FCSTD DOCUMENT  (FreeCAD 1.0R39109 (Git))
Label: roommake
License: All rights reserved
LicenseURL: https://en.wikipedia.org/wiki/All_rights_reserved
objects: App::Link×25, Assembly::JointGroup×1, Assembly::AssemblyObject×1
EXTERNAL_REF file=../room/room.FCStd obj=Part
EXTERNAL_REF file=../sofa/sofa.FCStd obj=Part002
EXTERNAL_REF file=../tvboard/tvboard.FCStd obj=Part
EXTERNAL_REF file=../tv/tv.FCStd obj=Part001
EXTERNAL_REF file=../balanceball/balanceball.FCStd obj=Part001
EXTERNAL_REF file=../clothes_drying_pole/clothes_drying_pole.FCStd obj=Part002
EXTERNAL_REF file=../refrigerator/refrigerator.FCStd obj=Part
EXTERNAL_REF file=../table02/table02.FCStd obj=Part
EXTERNAL_REF file=../toasteroven/toasteroven.FCStd obj=Part
EXTERNAL_REF file=../washing_machine/washing_machine.FCStd obj=Part
EXTERNAL_REF file=../furniture/furniture.FCStd obj=Part003
EXTERNAL_REF file=../dressing_table/Dressing_Table.FCStd obj=Part
EXTERNAL_REF file=../wall1500/wall1500.FCStd obj=Part
EXTERNAL_REF file=../table/table.FCStd obj=Part001
EXTERNAL_REF file=../cocktail/cocktail.FCStd obj=Part001
EXTERNAL_REF file=../moniter/moniter.FCStd obj=Part
EXTERNAL_REF file=../clock/clock.FCStd obj=Part012
EXTERNAL_REF file=../pylon/pylon.FCStd obj=Part001

FEATURE [Assembly::JointGroup] Joints
FEATURE [App::Link] room
  LinkedObject = -> <external ../room/room.FCStd>#Part
FEATURE [App::Link] sofa
  LinkPlacement = pos=(-6.91189e-05,821.257,-6.10352e-05) rot=(0,0,1;3.14159rad)
  LinkedObject = -> <external ../sofa/sofa.FCStd>#Part002
  Placement = pos=(-6.91189e-05,821.257,-6.10352e-05) rot=(0,0,1;3.14159rad)
FEATURE [App::Link] tvboard
  LinkPlacement = pos=(0,2298,-1.52588e-05) rot=(0,0,1;0rad)
  LinkedObject = -> <external ../tvboard/tvboard.FCStd>#Part
  Placement = pos=(0,2298,-1.52588e-05) rot=(0,0,1;0rad)
FEATURE [App::Link] tv
  LinkPlacement = pos=(0,2301,332) rot=(0,0,1;0rad)
  LinkedObject = -> <external ../tv/tv.FCStd>#Part001
  Placement = pos=(0,2301,332) rot=(0,0,1;0rad)
FEATURE [App::Link] balanceball
  LinkPlacement = pos=(-943,2144,-1.26064e-05) rot=(0,0,1;0rad)
  LinkedObject = -> <external ../balanceball/balanceball.FCStd>#Part001
  Placement = pos=(-943,2144,-1.26064e-05) rot=(0,0,1;0rad)
FEATURE [App::Link] clothesdryingpole
  LinkPlacement = pos=(-2049,1585,0) rot=(0,0,1;0rad)
  LinkedObject = -> <external ../clothes_drying_pole/clothes_drying_pole.FCStd>#Part002
  Placement = pos=(-2049,1585,0) rot=(0,0,1;0rad)
FEATURE [App::Link] refrigerator
  LinkPlacement = pos=(-1631,0.00019455,0) rot=(0,0,1;0rad)
  LinkedObject = -> <external ../refrigerator/refrigerator.FCStd>#Part
  Placement = pos=(-1631,0.00019455,0) rot=(0,0,1;0rad)
FEATURE [App::Link] table02
  LinkPlacement = pos=(-2198,-1060,-3.05176e-05) rot=(0,0,-1;1.5708rad)
  LinkedObject = -> <external ../table02/table02.FCStd>#Part
  Placement = pos=(-2198,-1060,-3.05176e-05) rot=(0,0,-1;1.5708rad)
FEATURE [App::Link] toasteroven
  LinkPlacement = pos=(-2215.04,-812.253,802.77) rot=(0,0,1;1.5708rad)
  LinkedObject = -> <external ../toasteroven/toasteroven.FCStd>#Part
  Placement = pos=(-2215.04,-812.253,802.77) rot=(0,0,1;1.5708rad)
FEATURE [App::Link] wachingmachine
  LinkPlacement = pos=(-2220,280,0) rot=(0,0,1;1.5708rad)
  LinkedObject = -> <external ../washing_machine/washing_machine.FCStd>#Part
  Placement = pos=(-2220,280,0) rot=(0,0,1;1.5708rad)
FEATURE [App::Link] furniture
  LinkPlacement = pos=(1220,2120,0) rot=(0,0,1;0rad)
  LinkedObject = -> <external ../furniture/furniture.FCStd>#Part003
  Placement = pos=(1220,2120,0) rot=(0,0,1;0rad)
FEATURE [App::Link] dressing_table
  LinkPlacement = pos=(2017,270,4.547e-13) rot=(0,0,-1;1.5708rad)
  LinkedObject = -> <external ../dressing_table/Dressing_Table.FCStd>#Part
  Placement = pos=(2017,270,4.547e-13) rot=(0,0,-1;1.5708rad)
FEATURE [App::Link] wall1500
  LinkPlacement = pos=(1706,-740.001,0) rot=(0,0,1;0rad)
  LinkedObject = -> <external ../wall1500/wall1500.FCStd>#Part
  Placement = pos=(1706,-740.001,0) rot=(0,0,1;0rad)
FEATURE [App::Link] wall1501
  LinkPlacement = pos=(2,-1703,-0.00012207) rot=(0,0,1;1.5708rad)
  LinkedObject = -> <external ../wall1500/wall1500.FCStd>#Part
  Placement = pos=(2,-1703,-0.00012207) rot=(0,0,1;1.5708rad)
FEATURE [App::Link] table
  LinkPlacement = pos=(-421,-1876,39.9999) rot=(0,0,-1;1.5708rad)
  LinkedObject = -> <external ../table/table.FCStd>#Part001
  Placement = pos=(-421,-1876,39.9999) rot=(0,0,-1;1.5708rad)
FEATURE [App::Link] cocktail
  LinkPlacement = pos=(-475,-1788,670) rot=(0,0,1;0rad)
  LinkedObject = -> <external ../cocktail/cocktail.FCStd>#Part001
  Placement = pos=(-475,-1788,670) rot=(0,0,1;0rad)
FEATURE [App::Link] cocktail001
  LinkPlacement = pos=(-272.591,-1674.31,668.798) rot=(0,0,-1;0.785398rad)
  LinkedObject = -> <external ../cocktail/cocktail.FCStd>#Part001
  Placement = pos=(-272.591,-1674.31,668.798) rot=(0,0,-1;0.785398rad)
FEATURE [App::Link] cocktail002
  LinkPlacement = pos=(-400.482,-2006.5,671.622) rot=(0,0,1;0.785398rad)
  LinkedObject = -> <external ../cocktail/cocktail.FCStd>#Part001
  Placement = pos=(-400.482,-2006.5,671.622) rot=(0,0,1;0.785398rad)
FEATURE [App::Link] table003
  LinkPlacement = pos=(411,-1895,-3.05176e-05) rot=(0,0,-1;1.5708rad)
  LinkedObject = -> <external ../table/table.FCStd>#Part001
  Placement = pos=(411,-1895,-3.05176e-05) rot=(0,0,-1;1.5708rad)
FEATURE [App::Link] moniter
  LinkPlacement = pos=(565.3,-2170.7,631) rot=(0,0,1;1.5708rad)
  LinkedObject = -> <external ../moniter/moniter.FCStd>#Part
  Placement = pos=(565.3,-2170.7,631) rot=(0,0,1;1.5708rad)
FEATURE [App::Link] moniter001
  LinkPlacement = pos=(563.3,-1618.7,633) rot=(0,0,1;1.5708rad)
  LinkedObject = -> <external ../moniter/moniter.FCStd>#Part
  Placement = pos=(563.3,-1618.7,633) rot=(0,0,1;1.5708rad)
FEATURE [App::Link] clock
  LinkPlacement = pos=(0,2440,2040) rot=(0,0,1;0rad)
  LinkedObject = -> <external ../clock/clock.FCStd>#Part012
  Placement = pos=(0,2440,2040) rot=(0,0,1;0rad)
FEATURE [App::Link] pylon
  LinkPlacement = pos=(2295,-958,-1.52588e-05) rot=(0,0,1;0rad)
  LinkedObject = -> <external ../pylon/pylon.FCStd>#Part001
  Placement = pos=(2295,-958,-1.52588e-05) rot=(0,0,1;0rad)
FEATURE [App::Link] pylon001
  LinkPlacement = pos=(2006,-961.001,0) rot=(0,0,1;0rad)
  LinkedObject = -> <external ../pylon/pylon.FCStd>#Part001
  Placement = pos=(2006,-961.001,0) rot=(0,0,1;0rad)
FEATURE [App::Link] pylon002
  LinkPlacement = pos=(2291,-976.001,74) rot=(0,0,1;0rad)
  LinkedObject = -> <external ../pylon/pylon.FCStd>#Part001
  Placement = pos=(2291,-976.001,74) rot=(0,0,1;0rad)
FEATURE [Assembly::AssemblyObject] Assembly
  Group = -> [Joints,room,sofa,tvboard,tv,balanceball,clothesdryingpole,refrigerator,table02,toasteroven,wachingmachine,furniture,dressing_table,wall1500,wall1501,table,cocktail,cocktail001,cocktail002,table003,moniter,moniter001,clock,pylon,pylon001,pylon002]
  Origin = -> Origin
  Type = Assembly

RESOLVED EXTERNAL PARTS (link-assembly join: the EXTERNAL_REF files above that resolve inside this repo's crawl, each included once):
---- part ../balanceball/balanceball.FCStd = doc fcstd_4663324129a9 ----
FCSTD DOCUMENT  (FreeCAD 1.0R39109 (Git))
Label: balanceball
License: All rights reserved
LicenseURL: https://en.wikipedia.org/wiki/All_rights_reserved
objects: Sketcher::SketchObject×4, PartDesign::Body×3, PartDesign::AdditiveSphere×2, PartDesign::Plane×2, App::Part×2, PartDesign::Pad×1, Part::MultiCommon×1, PartDesign::ShapeBinder×1, PartDesign::AdditivePipe×1, Part::MultiFuse×1, Part::FeaturePython×1
note: 29 computed .brp shape members not serialized (recipe doc carries the construction recipe); baked Part::Feature solids carry a one-line shape summary decoded from their .brp

FEATURE [PartDesign::AdditiveSphere] Sphere
  Angle1 = -90
  Angle2 = 90
  Angle3 = 360
  AttacherType = Attacher::AttachEngine3D
  Radius = 275
  Refine = true
  Suppressed = false
FEATURE [Sketcher::SketchObject] Sketch
  ArcFitTolerance = 1e-06
  AttachmentSupport = -> [XZ_Plane]
  ExternalGeometry = -> [Sphere]
  FullyConstrained = false
  MakeInternals = false
  MapMode = 5
  Placement = pos=(0,0,0) rot=(1,0,0;1.5708rad)
  sketch-geometry (131):
    g0: LineSegment StartX=-291.447 StartY=9.66667 StartZ=0 EndX=-291.447 EndY=10.6667 EndZ=0
    g1: LineSegment StartX=-291.447 StartY=10.6667 StartZ=0 EndX=291.447 EndY=10.6667 EndZ=0
    g2: LineSegment StartX=291.447 StartY=10.6667 StartZ=0 EndX=291.447 EndY=9.66667 EndZ=0
    g3: LineSegment StartX=291.447 StartY=9.66667 StartZ=0 EndX=-291.447 EndY=9.66667 EndZ=0
    g4: LineSegment StartX=-280.491 StartY=30 StartZ=0 EndX=-280.491 EndY=31 EndZ=0
    g5: LineSegment StartX=-280.491 StartY=31 StartZ=0 EndX=280.491 EndY=31 EndZ=0
    g6: LineSegment StartX=280.491 StartY=31 StartZ=0 EndX=280.491 EndY=30 EndZ=0
    g7: LineSegment StartX=280.491 StartY=30 StartZ=0 EndX=-280.491 EndY=30 EndZ=0
    g8: LineSegment StartX=282.77 StartY=51.3333 StartZ=0 EndX=282.77 EndY=50.3333 EndZ=0
    g9: LineSegment StartX=282.77 StartY=50.3333 StartZ=0 EndX=-282.77 EndY=50.3333 EndZ=0
    g10: LineSegment StartX=-282.77 StartY=50.3333 StartZ=0 EndX=-282.77 EndY=51.3333 EndZ=0
    g11: LineSegment StartX=-282.77 StartY=51.3333 StartZ=0 EndX=282.77 EndY=51.3333 EndZ=0
    g12: LineSegment StartX=-276.996 StartY=70.6667 StartZ=0 EndX=-276.996 EndY=71.6667 EndZ=0
    g13: LineSegment StartX=-276.996 StartY=71.6667 StartZ=0 EndX=276.996 EndY=71.6667 EndZ=0
    g14: LineSegment StartX=276.996 StartY=71.6667 StartZ=0 EndX=276.996 EndY=70.6667 EndZ=0
    g15: LineSegment StartX=276.996 StartY=70.6667 StartZ=0 EndX=-276.996 EndY=70.6667 EndZ=0
    g16: LineSegment StartX=271.883 StartY=91 StartZ=0 EndX=-271.883 EndY=91 EndZ=0
    g17: LineSegment StartX=-271.883 StartY=91 StartZ=0 EndX=-271.883 EndY=92 EndZ=0
    g18: LineSegment StartX=-271.883 StartY=92 StartZ=0 EndX=271.883 EndY=92 EndZ=0
    g19: LineSegment StartX=271.883 StartY=92 StartZ=0 EndX=271.883 EndY=91 EndZ=0
    g20: LineSegment StartX=-264.412 StartY=112.333 StartZ=0 EndX=264.412 EndY=112.333 EndZ=0
    g21: LineSegment StartX=264.412 StartY=112.333 StartZ=0 EndX=264.412 EndY=111.333 EndZ=0
    g22: LineSegment StartX=264.412 StartY=111.333 StartZ=0 EndX=-264.412 EndY=111.333 EndZ=0
    g23: LineSegment StartX=-264.412 StartY=111.333 StartZ=0 EndX=-264.412 EndY=112.333 EndZ=0
    g24: LineSegment StartX=256.154 StartY=132.667 StartZ=0 EndX=256.154 EndY=131.667 EndZ=0
    g25: LineSegment StartX=256.154 StartY=131.667 StartZ=0 EndX=-256.154 EndY=131.667 EndZ=0
    g26: LineSegment StartX=-256.154 StartY=131.667 StartZ=0 EndX=-256.154 EndY=132.667 EndZ=0
    g27: LineSegment StartX=-256.154 StartY=132.667 StartZ=0 EndX=256.154 EndY=132.667 EndZ=0
    g28: LineSegment StartX=-246.008 StartY=153 StartZ=0 EndX=246.008 EndY=153 EndZ=0
    g29: LineSegment StartX=246.008 StartY=153 StartZ=0 EndX=246.008 EndY=152 EndZ=0
    g30: LineSegment StartX=246.008 StartY=152 StartZ=0 EndX=-246.008 EndY=152 EndZ=0
    g31: LineSegment StartX=-246.008 StartY=152 StartZ=0 EndX=-246.008 EndY=153 EndZ=0
    g32: LineSegment StartX=237.302 StartY=173.333 StartZ=0 EndX=237.302 EndY=172.333 EndZ=0
    g33: LineSegment StartX=237.302 StartY=172.333 StartZ=0 EndX=-237.302 EndY=172.333 EndZ=0
    g34: LineSegment StartX=-237.302 StartY=172.333 StartZ=0 EndX=-237.302 EndY=173.333 EndZ=0
    g35: LineSegment StartX=-237.302 StartY=173.333 StartZ=0 EndX=237.302 EndY=173.333 EndZ=0
    g36: LineSegment StartX=-221.839 StartY=192.667 StartZ=0 EndX=-221.839 EndY=193.667 EndZ=0
    g37: LineSegment StartX=-221.839 StartY=193.667 StartZ=0 EndX=221.839 EndY=193.667 EndZ=0
    g38: LineSegment StartX=221.839 StartY=193.667 StartZ=0 EndX=221.839 EndY=192.667 EndZ=0
    g39: LineSegment StartX=221.839 StartY=192.667 StartZ=0 EndX=-221.839 EndY=192.667 EndZ=0
    g40: LineSegment StartX=212.405 StartY=214 StartZ=0 EndX=212.405 EndY=213 EndZ=0
    g41: LineSegment StartX=212.405 StartY=213 StartZ=0 EndX=-212.405 EndY=213 EndZ=0
    g42: LineSegment StartX=-212.405 StartY=213 StartZ=0 EndX=-212.405 EndY=214 EndZ=0
    g43: LineSegment StartX=-212.405 StartY=214 StartZ=0 EndX=212.405 EndY=214 EndZ=0
    g44: LineSegment StartX=-195.863 StartY=234.333 StartZ=0 EndX=195.863 EndY=234.333 EndZ=0
    g45: LineSegment StartX=195.863 StartY=234.333 StartZ=0 EndX=195.863 EndY=233.333 EndZ=0
    g46: LineSegment StartX=195.863 StartY=233.333 StartZ=0 EndX=-195.863 EndY=233.333 EndZ=0
    g47: LineSegment StartX=-195.863 StartY=233.333 StartZ=0 EndX=-195.863 EndY=234.333 EndZ=0
    g48: LineSegment StartX=184.098 StartY=254.667 StartZ=0 EndX=184.098 EndY=253.667 EndZ=0
    g49: LineSegment StartX=184.098 StartY=253.667 StartZ=0 EndX=-184.098 EndY=253.667 EndZ=0
    g50: LineSegment StartX=-184.098 StartY=253.667 StartZ=0 EndX=-184.098 EndY=254.667 EndZ=0
    g51: LineSegment StartX=-184.098 StartY=254.667 StartZ=0 EndX=184.098 EndY=254.667 EndZ=0
    g52: LineSegment StartX=-283.15 StartY=-10.6667 StartZ=0 EndX=-283.15 EndY=-9.66667 EndZ=0
    g53: LineSegment StartX=-283.15 StartY=-9.66667 StartZ=0 EndX=283.15 EndY=-9.66667 EndZ=0
    g54: LineSegment StartX=283.15 StartY=-9.66667 StartZ=0 EndX=283.15 EndY=-10.6667 EndZ=0
    g55: LineSegment StartX=283.15 StartY=-10.6667 StartZ=0 EndX=-283.15 EndY=-10.6667 EndZ=0
    g56: LineSegment StartX=285.733 StartY=-31 StartZ=0 EndX=-285.733 EndY=-31 EndZ=0
    g57: LineSegment StartX=-285.733 StartY=-31 StartZ=0 EndX=-285.733 EndY=-30 EndZ=0
    g58: LineSegment StartX=-285.733 StartY=-30 StartZ=0 EndX=285.733 EndY=-30 EndZ=0
    g59: LineSegment StartX=285.733 StartY=-30 StartZ=0 EndX=285.733 EndY=-31 EndZ=0
    g60: LineSegment StartX=-283.692 StartY=-51.3333 StartZ=0 EndX=-283.692 EndY=-50.3333 EndZ=0
    g61: LineSegment StartX=-283.692 StartY=-50.3333 StartZ=0 EndX=283.692 EndY=-50.3333 EndZ=0
    g62: LineSegment StartX=283.692 StartY=-50.3333 StartZ=0 EndX=283.692 EndY=-51.3333 EndZ=0
    g63: LineSegment StartX=283.692 StartY=-51.3333 StartZ=0 EndX=-283.692 EndY=-51.3333 EndZ=0
    g64: LineSegment StartX=278.903 StartY=-71.6667 StartZ=0 EndX=-278.903 EndY=-71.6667 EndZ=0
    g65: LineSegment StartX=-278.903 StartY=-71.6667 StartZ=0 EndX=-278.903 EndY=-70.6667 EndZ=0
    g66: LineSegment StartX=-278.903 StartY=-70.6667 StartZ=0 EndX=278.903 EndY=-70.6667 EndZ=0
    g67: LineSegment StartX=278.903 StartY=-70.6667 StartZ=0 EndX=278.903 EndY=-71.6667 EndZ=0
    g68: LineSegment StartX=-269.142 StartY=-92 StartZ=0 EndX=-269.142 EndY=-91 EndZ=0
    g69: LineSegment StartX=-269.142 StartY=-91 StartZ=0 EndX=269.142 EndY=-91 EndZ=0
    g70: LineSegment StartX=269.142 StartY=-91 StartZ=0 EndX=269.142 EndY=-92 EndZ=0
    g71: LineSegment StartX=269.142 StartY=-92 StartZ=0 EndX=-269.142 EndY=-92 EndZ=0
    g72: LineSegment StartX=260.857 StartY=-112.333 StartZ=0 EndX=-260.857 EndY=-112.333 EndZ=0
    g73: LineSegment StartX=-260.857 StartY=-112.333 StartZ=0 EndX=-260.857 EndY=-111.333 EndZ=0
    g74: LineSegment StartX=-260.857 StartY=-111.333 StartZ=0 EndX=260.857 EndY=-111.333 EndZ=0
    g75: LineSegment StartX=260.857 StartY=-111.333 StartZ=0 EndX=260.857 EndY=-112.333 EndZ=0
    g76: LineSegment StartX=-246.128 StartY=-132.667 StartZ=0 EndX=-246.128 EndY=-131.667 EndZ=0
    g77: LineSegment StartX=-246.128 StartY=-131.667 StartZ=0 EndX=246.128 EndY=-131.667 EndZ=0
    g78: LineSegment StartX=246.128 StartY=-131.667 StartZ=0 EndX=246.128 EndY=-132.667 EndZ=0
    g79: LineSegment StartX=246.128 StartY=-132.667 StartZ=0 EndX=-246.128 EndY=-132.667 EndZ=0
    g80: LineSegment StartX=237.57 StartY=-153 StartZ=0 EndX=-237.57 EndY=-153 EndZ=0
    g81: LineSegment StartX=-237.57 StartY=-153 StartZ=0 EndX=-237.57 EndY=-152 EndZ=0
    g82: LineSegment StartX=-237.57 StartY=-152 StartZ=0 EndX=237.57 EndY=-152 EndZ=0
    g83: LineSegment StartX=237.57 StartY=-152 StartZ=0 EndX=237.57 EndY=-153 EndZ=0
    g84: LineSegment StartX=-225.124 StartY=-173.333 StartZ=0 EndX=-225.124 EndY=-172.333 EndZ=0
    g85: LineSegment StartX=-225.124 StartY=-172.333 StartZ=0 EndX=225.124 EndY=-172.333 EndZ=0
    g86: LineSegment StartX=225.124 StartY=-172.333 StartZ=0 EndX=225.124 EndY=-173.333 EndZ=0
    g87: LineSegment StartX=225.124 StartY=-173.333 StartZ=0 EndX=-225.124 EndY=-173.333 EndZ=0
    g88: LineSegment StartX=209.157 StartY=-193.667 StartZ=0 EndX=-209.157 EndY=-193.667 EndZ=0
    g89: LineSegment StartX=-209.157 StartY=-193.667 StartZ=0 EndX=-209.157 EndY=-192.667 EndZ=0
    g90: LineSegment StartX=-209.157 StartY=-192.667 StartZ=0 EndX=209.157 EndY=-192.667 EndZ=0
    g91: LineSegment StartX=209.157 StartY=-192.667 StartZ=0 EndX=209.157 EndY=-193.667 EndZ=0
    g92: LineSegment StartX=-190.627 StartY=-214 StartZ=0 EndX=-190.627 EndY=-213 EndZ=0
    g93: LineSegment StartX=-190.627 StartY=-213 StartZ=0 EndX=190.627 EndY=-213 EndZ=0
    g94: LineSegment StartX=190.627 StartY=-213 StartZ=0 EndX=190.627 EndY=-214 EndZ=0
    g95: LineSegment StartX=190.627 StartY=-214 StartZ=0 EndX=-190.627 EndY=-214 EndZ=0
    g96: LineSegment StartX=-172.023 StartY=-234.333 StartZ=0 EndX=-172.023 EndY=-233.333 EndZ=0
    g97: LineSegment StartX=-172.023 StartY=-233.333 StartZ=0 EndX=172.023 EndY=-233.333 EndZ=0
    g98: LineSegment StartX=172.023 StartY=-233.333 StartZ=0 EndX=172.023 EndY=-234.333 EndZ=0
    g99: LineSegment StartX=172.023 StartY=-234.333 StartZ=0 EndX=-172.023 EndY=-234.333 EndZ=0
    g100: LineSegment StartX=-150.671 StartY=-254.667 StartZ=0 EndX=-150.671 EndY=-253.667 EndZ=0
    g101: LineSegment StartX=-150.671 StartY=-253.667 StartZ=0 EndX=150.671 EndY=-253.667 EndZ=0
    g102: LineSegment StartX=150.671 StartY=-253.667 StartZ=0 EndX=150.671 EndY=-254.667 EndZ=0
    g103: LineSegment StartX=150.671 StartY=-254.667 StartZ=0 EndX=-150.671 EndY=-254.667 EndZ=0
    g104: LineSegment [constr] StartX=8.42e-14 StartY=275 StartZ=0 EndX=8.42e-14 EndY=253.667 EndZ=0
    g105: LineSegment [constr] StartX=7.37e-14 StartY=254.667 StartZ=0 EndX=7.37e-14 EndY=233.333 EndZ=0
    g106: LineSegment [constr] StartX=6.83e-14 StartY=234.333 StartZ=0 EndX=6.83e-14 EndY=213 EndZ=0
    g107: LineSegment [constr] StartX=9.01e-14 StartY=214 StartZ=0 EndX=9.01e-14 EndY=192.667 EndZ=0
    g108: LineSegment [constr] StartX=7.41e-14 StartY=193.667 StartZ=0 EndX=7.41e-14 EndY=172.333 EndZ=0
    g109: LineSegment [constr] StartX=8.64e-14 StartY=173.333 StartZ=0 EndX=8.64e-14 EndY=152 EndZ=0
    g110: LineSegment [constr] StartX=8.72e-14 StartY=153 StartZ=0 EndX=8.72e-14 EndY=131.667 EndZ=0
    g111: LineSegment [constr] StartX=1.192e-13 StartY=132.667 StartZ=0 EndX=1.192e-13 EndY=111.333 EndZ=0
    g112: LineSegment [constr] StartX=1.25e-13 StartY=112.333 StartZ=0 EndX=1.25e-13 EndY=91 EndZ=0
    g113: LineSegment [constr] StartX=1.363e-13 StartY=92 StartZ=0 EndX=1.363e-13 EndY=70.6667 EndZ=0
    g114: LineSegment [constr] StartX=1.131e-13 StartY=71.6667 StartZ=0 EndX=1.131e-13 EndY=50.3333 EndZ=0
    g115: LineSegment [constr] StartX=8.7e-14 StartY=51.3333 StartZ=0 EndX=8.7e-14 EndY=30 EndZ=0
    g116: LineSegment [constr] StartX=1.326e-13 StartY=31 StartZ=0 EndX=1.326e-13 EndY=9.66667 EndZ=0
    g117: LineSegment [constr] StartX=9.7e-14 StartY=10.6667 StartZ=0 EndX=9.7e-14 EndY=-10.6667 EndZ=0
    g118: LineSegment [constr] StartX=1.219e-13 StartY=-9.66667 StartZ=0 EndX=1.219e-13 EndY=-31 EndZ=0
    g119: LineSegment [constr] StartX=8.3e-14 StartY=-30 StartZ=0 EndX=8.3e-14 EndY=-51.3333 EndZ=0
    g120: LineSegment [constr] StartX=9.47e-14 StartY=-50.3333 StartZ=0 EndX=9.47e-14 EndY=-71.6667 EndZ=0
    g121: LineSegment [constr] StartX=1.138e-13 StartY=-70.6667 StartZ=0 EndX=1.138e-13 EndY=-92 EndZ=0
    g122: LineSegment [constr] StartX=1.058e-13 StartY=-91 StartZ=0 EndX=1.058e-13 EndY=-112.333 EndZ=0
    g123: LineSegment [constr] StartX=1.327e-13 StartY=-111.333 StartZ=0 EndX=1.327e-13 EndY=-132.667 EndZ=0
    g124: LineSegment [constr] StartX=1.275e-13 StartY=-131.667 StartZ=0 EndX=1.275e-13 EndY=-153 EndZ=0
    g125: LineSegment [constr] StartX=1.325e-13 StartY=-152 StartZ=0 EndX=1.325e-13 EndY=-173.333 EndZ=0
    g126: LineSegment [constr] StartX=1.362e-13 StartY=-172.333 StartZ=0 EndX=1.362e-13 EndY=-193.667 EndZ=0
    g127: LineSegment [constr] StartX=1.246e-13 StartY=-192.667 StartZ=0 EndX=1.246e-13 EndY=-214 EndZ=0
    g128: LineSegment [constr] StartX=1.449e-13 StartY=-213 StartZ=0 EndX=1.449e-13 EndY=-234.333 EndZ=0
    g129: LineSegment [constr] StartX=1.405e-13 StartY=-233.333 StartZ=0 EndX=1.405e-13 EndY=-254.667 EndZ=0
    g130: LineSegment [constr] StartX=1.48e-13 StartY=-253.667 StartZ=0 EndX=-5.05e-14 EndY=-275 EndZ=0
  constraints (340):
    c: Coincident(g0,g1)
    c: Coincident(g1,g2)
    c: Coincident(g2,g3)
    c: Coincident(g3,g0)
    c: Vertical(g0)
    c: Vertical(g2)
    c: Horizontal(g1)
    c: Horizontal(g3)
    c: Coincident(g4,g5)
    c: Coincident(g5,g6)
    c: Coincident(g6,g7)
    c: Coincident(g7,g4)
    c: Vertical(g4)
    c: Vertical(g6)
    c: Horizontal(g5)
    c: Horizontal(g7)
    c: Coincident(g8,g9)
    c: Coincident(g9,g10)
    c: Coincident(g10,g11)
    c: Coincident(g11,g8)
    c: Vertical(g8)
    c: Vertical(g10)
    c: Horizontal(g9)
    c: Horizontal(g11)
    c: Coincident(g12,g13)
    c: Coincident(g13,g14)
    c: Coincident(g14,g15)
    c: Coincident(g15,g12)
    c: Vertical(g12)
    c: Vertical(g14)
    c: Horizontal(g13)
    c: Horizontal(g15)
    c: Coincident(g16,g17)
    c: Coincident(g17,g18)
    c: Coincident(g18,g19)
    c: Coincident(g19,g16)
    c: Horizontal(g16)
    c: Horizontal(g18)
    c: Vertical(g17)
    c: Vertical(g19)
    c: Coincident(g20,g21)
    c: Coincident(g21,g22)
    c: Coincident(g22,g23)
    c: Coincident(g23,g20)
    c: Horizontal(g20)
    c: Horizontal(g22)
    c: Vertical(g21)
    c: Vertical(g23)
    c: Coincident(g24,g25)
    c: Coincident(g25,g26)
    c: Coincident(g26,g27)
    c: Coincident(g27,g24)
    c: Vertical(g24)
    c: Vertical(g26)
    c: Horizontal(g25)
    c: Horizontal(g27)
    c: Coincident(g28,g29)
    c: Coincident(g29,g30)
    c: Coincident(g30,g31)
    c: Coincident(g31,g28)
    c: Horizontal(g28)
    c: Horizontal(g30)
    c: Vertical(g29)
    c: Vertical(g31)
    c: Coincident(g32,g33)
    c: Coincident(g33,g34)
    c: Coincident(g34,g35)
    c: Coincident(g35,g32)
    c: Vertical(g32)
    c: Vertical(g34)
    c: Horizontal(g33)
    c: Horizontal(g35)
    c: Coincident(g36,g37)
    c: Coincident(g37,g38)
    c: Coincident(g38,g39)
    c: Coincident(g39,g36)
    c: Vertical(g36)
    c: Vertical(g38)
    c: Horizontal(g37)
    c: Horizontal(g39)
    c: Coincident(g40,g41)
    c: Coincident(g41,g42)
    c: Coincident(g42,g43)
    c: Coincident(g43,g40)
    c: Vertical(g40)
    c: Vertical(g42)
    c: Horizontal(g41)
    c: Horizontal(g43)
    c: Coincident(g44,g45)
    c: Coincident(g45,g46)
    c: Coincident(g46,g47)
    c: Coincident(g47,g44)
    c: Horizontal(g44)
    c: Horizontal(g46)
    c: Vertical(g45)
    c: Vertical(g47)
    c: Coincident(g48,g49)
    c: Coincident(g49,g50)
    c: Coincident(g50,g51)
    c: Coincident(g51,g48)
    c: Vertical(g48)
    c: Vertical(g50)
    c: Horizontal(g49)
    c: Horizontal(g51)
    c: Coincident(g52,g53)
    c: Coincident(g53,g54)
    c: Coincident(g54,g55)
    c: Coincident(g55,g52)
    c: Vertical(g52)
    c: Vertical(g54)
    c: Horizontal(g53)
    c: Horizontal(g55)
    c: Coincident(g56,g57)
    c: Coincident(g57,g58)
    c: Coincident(g58,g59)
    c: Coincident(g59,g56)
    c: Horizontal(g56)
    c: Horizontal(g58)
    c: Vertical(g57)
    c: Vertical(g59)
    c: Coincident(g60,g61)
    c: Coincident(g61,g62)
    c: Coincident(g62,g63)
    c: Coincident(g63,g60)
    c: Vertical(g60)
    c: Vertical(g62)
    c: Horizontal(g61)
    c: Horizontal(g63)
    c: Coincident(g64,g65)
    c: Coincident(g65,g66)
    c: Coincident(g66,g67)
    c: Coincident(g67,g64)
    c: Horizontal(g64)
    c: Horizontal(g66)
    c: Vertical(g65)
    c: Vertical(g67)
    c: Coincident(g68,g69)
    c: Coincident(g69,g70)
    c: Coincident(g70,g71)
    c: Coincident(g71,g68)
    c: Vertical(g68)
    c: Vertical(g70)
    c: Horizontal(g69)
    c: Horizontal(g71)
    c: Coincident(g72,g73)
    c: Coincident(g73,g74)
    c: Coincident(g74,g75)
    c: Coincident(g75,g72)
    c: Horizontal(g72)
    c: Horizontal(g74)
    c: Vertical(g73)
    c: Vertical(g75)
    c: Coincident(g76,g77)
    c: Coincident(g77,g78)
    c: Coincident(g78,g79)
    c: Coincident(g79,g76)
    c: Vertical(g76)
    c: Vertical(g78)
    c: Horizontal(g77)
    c: Horizontal(g79)
    c: Coincident(g80,g81)
    c: Coincident(g81,g82)
    c: Coincident(g82,g83)
    c: Coincident(g83,g80)
    c: Horizontal(g80)
    c: Horizontal(g82)
    c: Vertical(g81)
    c: Vertical(g83)
    c: Coincident(g84,g85)
    c: Coincident(g85,g86)
    c: Coincident(g86,g87)
    c: Coincident(g87,g84)
    c: Vertical(g84)
    c: Vertical(g86)
    c: Horizontal(g85)
    c: Horizontal(g87)
    c: Coincident(g88,g89)
    c: Coincident(g89,g90)
    c: Coincident(g90,g91)
    c: Coincident(g91,g88)
    c: Horizontal(g88)
    c: Horizontal(g90)
    c: Vertical(g89)
    c: Vertical(g91)
    c: Coincident(g92,g93)
    c: Coincident(g93,g94)
    c: Coincident(g94,g95)
    c: Coincident(g95,g92)
    c: Vertical(g92)
    c: Vertical(g94)
    c: Horizontal(g93)
    c: Horizontal(g95)
    c: Coincident(g96,g97)
    c: Coincident(g97,g98)
    c: Coincident(g98,g99)
    c: Coincident(g99,g96)
    c: Vertical(g96)
    c: Vertical(g98)
    c: Horizontal(g97)
    c: Horizontal(g99)
    c: Coincident(g100,g101)
    c: Coincident(g101,g102)
    c: Coincident(g102,g103)
    c: Coincident(g103,g100)
    c: Vertical(g100)
    c: Vertical(g102)
    c: Horizontal(g101)
    c: Horizontal(g103)
    c: Equal(g50,g47)
    c: Equal(g47,g42)
    c: Equal(g42,g36)
    c: Equal(g36,g34)
    c: Equal(g34,g31)
    c: Equal(g31,g26)
    c: Equal(g26,g23)
    c: Equal(g23,g17)
    c: Equal(g17,g12)
    c: Equal(g12,g10)
    c: Equal(g10,g4)
    c: Equal(g4,g0)
    c: Equal(g0,g52)
    c: Equal(g52,g57)
    c: Equal(g57,g60)
    c: Equal(g60,g65)
    c: Equal(g65,g68)
    c: Equal(g68,g73)
    c: Equal(g73,g76)
    c: Equal(g76,g81)
    c: Equal(g81,g84)
    c: Equal(g84,g89)
    c: Equal(g89,g92)
    c: Equal(g92,g96)
    c: Equal(g96,g100)
    c: Coincident(g104,g-3)
    c: Symmetric(g49,g49,g104)
    c: Symmetric(g51,g51,g105)
    c: Symmetric(g46,g46,g105)
    c: Symmetric(g44,g44,g106)
    c: Symmetric(g41,g41,g106)
    c: Symmetric(g43,g43,g107)
    c: Symmetric(g39,g39,g107)
    c: Symmetric(g37,g37,g108)
    c: Symmetric(g33,g33,g108)
    c: Vertical(g108)
    c: Symmetric(g35,g35,g109)
    c: Symmetric(g30,g30,g109)
    c: Symmetric(g28,g28,g110)
    c: Symmetric(g25,g25,g110)
    c: Symmetric(g27,g27,g111)
    c: Symmetric(g22,g22,g111)
    c: Vertical(g111)
    c: Symmetric(g20,g20,g112)
    c: Symmetric(g16,g16,g112)
    c: Vertical(g112)
    c: Symmetric(g18,g18,g113)
    c: Symmetric(g15,g15,g113)
    c: Symmetric(g13,g13,g114)
    c: Symmetric(g9,g9,g114)
    c: Symmetric(g11,g11,g115)
    c: Symmetric(g7,g7,g115)
    c: Vertical(g115)
    c: Symmetric(g5,g5,g116)
    c: Symmetric(g3,g3,g116)
    c: Symmetric(g1,g1,g117)
    c: Symmetric(g55,g55,g117)
    c: Symmetric(g53,g53,g118)
    c: Symmetric(g56,g56,g118)
    c: Symmetric(g58,g58,g119)
    c: Symmetric(g63,g63,g119)
    c: Symmetric(g61,g61,g120)
    c: Symmetric(g64,g64,g120)
    c: Symmetric(g66,g66,g121)
    c: Symmetric(g71,g71,g121)
    c: Symmetric(g69,g69,g122)
    c: Symmetric(g72,g72,g122)
    c: Vertical(g122)
    c: Symmetric(g74,g74,g123)
    c: Symmetric(g79,g79,g123)
    c: Symmetric(g77,g77,g124)
    c: Symmetric(g80,g80,g124)
    c: Symmetric(g82,g82,g125)
    c: Symmetric(g87,g87,g125)
    c: Symmetric(g85,g85,g126)
    c: Symmetric(g88,g88,g126)
    c: Symmetric(g90,g90,g127)
    c: Symmetric(g95,g95,g127)
    c: Symmetric(g93,g93,g128)
    c: Symmetric(g99,g99,g128)
    c: Symmetric(g97,g97,g129)
    c: Symmetric(g103,g103,g129)
    c: Symmetric(g101,g101,g130)
    c: Coincident(g130,g-3)
    c: Equal(g104,g105)
    c: Equal(g105,g106)
    c: Equal(g106,g107)
    c: Equal(g107,g108)
    c: Equal(g108,g109)
    c: Equal(g109,g110)
    c: Equal(g110,g111)
    c: Equal(g111,g112)
    c: Equal(g112,g113)
    c: Equal(g113,g114)
    c: Equal(g114,g115)
    c: Equal(g115,g116)
    c: Equal(g116,g117)
    c: Equal(g117,g118)
    c: Equal(g118,g119)
    c: Equal(g119,g120)
    c: Equal(g120,g121)
    c: Equal(g121,g122)
    c: Equal(g122,g123)
    c: Equal(g123,g124)
    c: Equal(g124,g125)
    c: Equal(g125,g126)
    c: Equal(g126,g127)
    c: Equal(g127,g128)
    c: Equal(g128,g129)
    c: Equal(g129,g130)
    c: Vertical(g104)
    c: Vertical(g105)
    c: Vertical(g106)
    c: Vertical(g107)
    c: Vertical(g109)
    c: Vertical(g110)
    c: Vertical(g113)
    c: Vertical(g114)
    c: Vertical(g116)
    c: Vertical(g117)
    c: Vertical(g118)
    c: Vertical(g119)
    c: Vertical(g120)
    c: Vertical(g121)
    c: Vertical(g123)
    c: Vertical(g124)
    c: Vertical(g125)
    c: Vertical(g126)
    c: Vertical(g127)
    c: Vertical(g128)
    c: Vertical(g129)
    c: DistanceY(g50,g50) = 1
FEATURE [PartDesign::Pad] Pad
  BaseFeature = -> Sphere
  Direction = (0,-1,2e-16)
  Length = 560
  Length2 = 10
  Midplane = true
  Profile = -> Sketch
  ReferenceAxis = -> Sketch [N_Axis]
  Refine = true
  Suppressed = false
  Type = 0
FEATURE [PartDesign::Body] Body
  AllowCompound = false
  Group = -> [Sphere,Sketch,Pad]
  Origin = -> Origin
  Tip = -> Pad
FEATURE [PartDesign::AdditiveSphere] Sphere001
  Angle1 = -90
  Angle2 = 90
  Angle3 = 360
  AttacherType = Attacher::AttachEngine3D
  Radius = 275.5
  Refine = true
  Suppressed = false
FEATURE [PartDesign::Body] Body001
  AllowCompound = false
  Group = -> [Sphere001]
  Origin = -> Origin001
  Tip = -> Sphere001
FEATURE [Part::MultiCommon] Common
  Refine = true
  Shapes = -> [Body,Body001]
FEATURE [PartDesign::ShapeBinder] CopyCommon
  TraceSupport = false
FEATURE [Sketcher::SketchObject] Sketch001
  ArcFitTolerance = 1e-06
  AttachmentSupport = -> [XZ_Plane002]
  ExternalGeometry = -> [CopyCommon]
  FullyConstrained = false
  MakeInternals = false
  MapMode = 5
  Placement = pos=(0,0,0) rot=(1,0,0;1.5708rad)
  sketch-geometry (2):
    g0: Circle CenterX=-157.732 CenterY=-255.772 CenterZ=0 NormalX=0 NormalY=0 NormalZ=1 AngleXU=0 Radius=25
    g1: LineSegment StartX=-144.873 StartY=-234.333 StartZ=0 EndX=-157.732 EndY=-255.772 EndZ=0
  constraints (4):
    c: PointOnObject(g-3,g0)
    c: Radius(g0) = 25
    c: Coincident(g1,g-3)
    c: Coincident(g1,g0)
FEATURE [PartDesign::Plane] DatumPlane
  AttachmentSupport = -> [Sketch001]
  Length = 438.471
  MapMode = 1
  Placement = pos=(-157.732,-5.68e-14,-255.772) rot=(0,0,1;0rad)
  ResizeMode = 0
  Width = 438.506
FEATURE [Sketcher::SketchObject] Sketch002
  ArcFitTolerance = 1e-06
  AttachmentSupport = -> [DatumPlane]
  ExternalGeometry = -> [CopyCommon]
  FullyConstrained = true
  MakeInternals = false
  MapMode = 5
  Placement = pos=(-157.732,-5.68e-14,-255.772) rot=(0,0,1;0rad)
  sketch-geometry (1):
    g0: Circle CenterX=157.732 CenterY=4.8e-15 CenterZ=0 NormalX=0 NormalY=0 NormalZ=1 AngleXU=0 Radius=157.732
  constraints (2):
    c: Coincident(g0,g-3)
    c: PointOnObject(g-1,g0)
FEATURE [PartDesign::Plane] DatumPlane001
  AttachmentSupport = -> [Sketch001]
  Length = 372.613
  MapMode = 11
  Placement = pos=(-157.732,-5.68e-14,-255.772) rot=(0.57735,-0.57735,0.57735;2.0944rad)
  ResizeMode = 0
  Width = 432.239
FEATURE [Sketcher::SketchObject] Sketch003
  ArcFitTolerance = 1e-06
  AttachmentSupport = -> [DatumPlane001]
  ExternalGeometry = -> [Sketch001]
  FullyConstrained = false
  MakeInternals = false
  MapMode = 5
  Placement = pos=(-157.732,-5.68e-14,-255.772) rot=(0.57735,-0.57735,0.57735;2.0944rad)
  sketch-geometry (1):
    g0: Circle CenterX=0 CenterY=0 CenterZ=0 NormalX=0 NormalY=0 NormalZ=1 AngleXU=0 Radius=25
  constraints (1):
    c: Coincident(g0,g-1)
FEATURE [PartDesign::AdditivePipe] AdditivePipe
  AuxilleryCurvelinear = true
  AuxillerySpineTangent = false
  Binormal = (0,0,0)
  Mode = 0
  Placement = pos=(-157.732,-5.68e-14,-255.772) rot=(0.57735,-0.57735,0.57735;2.0944rad)
  Profile = -> Sketch003
  Refine = true
  Spine = -> Sketch002
  SpineTangent = false
  Suppressed = false
  Transformation = 0
  Transition = 0
FEATURE [PartDesign::Body] Body002
  AllowCompound = false
  Group = -> [CopyCommon,Sketch001,DatumPlane,Sketch002,DatumPlane001,Sketch003,AdditivePipe]
  Origin = -> Origin002
  Tip = -> AdditivePipe
FEATURE [Part::MultiFuse] Fusion
  Placement = pos=(0,0,280) rot=(0,0,1;0rad)
  Refine = true
  Shapes = -> [Common,Body002]
FEATURE [App::Part] Part  label="balanceball1"
  Group = -> [Body,Body001,Common,Body002,Fusion]
  Origin = -> Origin003
  Placement = pos=(0,0,280) rot=(0,0,1;0rad)
FEATURE [Part::FeaturePython] Clone  label="balanceball_clone"  # Draft clone (typed FeaturePython)
  AttacherType = Attacher::AttachEngine3D
  Fuse = false
  Objects = -> [Part]
  Scale = (1,1,1)
FEATURE [App::Part] Part001  label="balanceball"
  Group = -> [Clone]
  Origin = -> Origin004
---- part ../clock/clock.FCStd = doc fcstd_bdbfecd46041 ----
FCSTD DOCUMENT  (FreeCAD 1.0R39109 (Git))
Label: clock
License: All rights reserved
LicenseURL: https://en.wikipedia.org/wiki/All_rights_reserved
objects: Part::FeaturePython×13, App::Part×13, Sketcher::SketchObject×6, PartDesign::Body×6, PartDesign::ShapeBinder×5, PartDesign::Pad×5, PartDesign::Revolution×1
note: 53 computed .brp shape members not serialized (recipe doc carries the construction recipe); baked Part::Feature solids carry a one-line shape summary decoded from their .brp

FEATURE [Sketcher::SketchObject] Sketch
  ArcFitTolerance = 1e-06
  AttachmentSupport = -> [XZ_Plane]
  FullyConstrained = true
  MakeInternals = false
  MapMode = 5
  Placement = pos=(0,0,0) rot=(1,0,0;1.5708rad)
  sketch-geometry (12):
    g0: LineSegment StartX=0 StartY=0 StartZ=0 EndX=150 EndY=0 EndZ=0
    g1: LineSegment StartX=150 StartY=0 StartZ=0 EndX=150 EndY=55 EndZ=0
    g2: LineSegment StartX=150 StartY=55 StartZ=0 EndX=135 EndY=55 EndZ=0
    g3: LineSegment StartX=135 StartY=55 StartZ=0 EndX=135 EndY=50 EndZ=0
    g4: LineSegment StartX=135 StartY=50 StartZ=0 EndX=140 EndY=50 EndZ=0
    g5: LineSegment StartX=140 StartY=50 StartZ=0 EndX=140 EndY=48 EndZ=0
    g6: LineSegment StartX=140 StartY=48 StartZ=0 EndX=135 EndY=48 EndZ=0
    g7: LineSegment StartX=135 StartY=48 StartZ=0 EndX=135 EndY=25 EndZ=0
    g8: LineSegment StartX=135 StartY=25 StartZ=0 EndX=2.5 EndY=25 EndZ=0
    g9: LineSegment StartX=2.5 StartY=25 StartZ=0 EndX=2.5 EndY=28 EndZ=0
    g10: LineSegment StartX=2.5 StartY=28 StartZ=0 EndX=0 EndY=28 EndZ=0
    g11: LineSegment StartX=0 StartY=28 StartZ=0 EndX=0 EndY=0 EndZ=0
  constraints (35):
    c: Coincident(g-1,g0)
    c: PointOnObject(g0,g-1)
    c: Coincident(g0,g1)
    c: Vertical(g1)
    c: Coincident(g1,g2)
    c: Horizontal(g2)
    c: Coincident(g2,g3)
    c: Vertical(g3)
    c: Coincident(g3,g4)
    c: Horizontal(g4)
    c: Coincident(g4,g5)
    c: Vertical(g5)
    c: Coincident(g5,g6)
    c: Horizontal(g6)
    c: Coincident(g6,g7)
    c: Vertical(g7)
    c: Coincident(g7,g8)
    c: Horizontal(g8)
    c: Coincident(g8,g9)
    c: Vertical(g9)
    c: Coincident(g9,g10)
    c: PointOnObject(g10,g-2)
    c: Horizontal(g10)
    c: Coincident(g10,g11)
    c: Coincident(g11,g0)
    c: DistanceX(g0,g0) = 150
    c: DistanceY(g1,g1) = 55
    c: DistanceX(g2,g2) = 15
    c: DistanceY(g3,g3) = 5
    c: DistanceX(g4,g4) = 5
    c: Equal(g4,g6)
    c: DistanceY(g5,g5) = 2
    c: DistanceY(g7,g2) = 30
    c: DistanceY(g9,g9) = 3
    c: DistanceX(g10,g10) = 2.5
FEATURE [PartDesign::Revolution] Revolution
  Angle = 360
  Angle2 = 60
  Axis = (0,2e-16,1)
  Base = (0,0,0)
  Placement = pos=(0,0,0) rot=(1,0,0;1.5708rad)
  Profile = -> Sketch
  ReferenceAxis = -> Sketch [V_Axis]
  Refine = true
  Reversed = true
  Suppressed = false
  Type = 0
FEATURE [PartDesign::Body] Body
  AllowCompound = false
  Group = -> [Sketch,Revolution]
  Origin = -> Origin
  Tip = -> Revolution
FEATURE [PartDesign::ShapeBinder] CopyRevolution
  Placement = pos=(0,0,0) rot=(1,0,0;1.5708rad)
  TraceSupport = false
FEATURE [Sketcher::SketchObject] Sketch001
  ArcFitTolerance = 1e-06
  AttachmentSupport = -> [CopyRevolution]
  FullyConstrained = true
  MakeInternals = false
  MapMode = 5
  Placement = pos=(0,1.1e-14,25) rot=(0,0,1;3.14159rad)
  sketch-geometry (5):
    g0: Circle CenterX=0 CenterY=6e-16 CenterZ=0 NormalX=0 NormalY=0 NormalZ=1 AngleXU=0 Radius=2.5
    g1: ArcOfCircle CenterX=0 CenterY=6e-16 CenterZ=0 NormalX=0 NormalY=0 NormalZ=1 AngleXU=0 Radius=5 StartAngle=1e-16 EndAngle=3.14159
    g2: LineSegment StartX=5 StartY=1.2e-15 StartZ=0 EndX=5 EndY=-100 EndZ=0
    g3: LineSegment StartX=5 StartY=-100 StartZ=0 EndX=-5 EndY=-100 EndZ=0
    g4: LineSegment StartX=-5 StartY=-100 StartZ=0 EndX=-5 EndY=0 EndZ=0
  constraints (13):
    c: Coincident(g1,g0)
    c: Radius(g0) = 2.5
    c: PointOnObject(g0,g-2)
    c: Vertical(g2)
    c: Coincident(g2,g3)
    c: Horizontal(g3)
    c: Coincident(g3,g4)
    c: Vertical(g4)
    c: PointOnObject(g4,g-1)
    c: Tangent(g1,g4) = 1.5708
    c: Tangent(g1,g2) = 1.5708
    c: DistanceX(g3,g3) = 10
    c: DistanceY(g4,g4) = 100
FEATURE [PartDesign::Pad] Pad
  Direction = (0,0,1)
  Length = 1
  Length2 = 10
  Placement = pos=(0,0,0) rot=(1,0,0;1.5708rad)
  Profile = -> Sketch001
  ReferenceAxis = -> Sketch001 [N_Axis]
  Refine = true
  Suppressed = false
  Type = 0
FEATURE [PartDesign::Body] Body001
  AllowCompound = false
  Group = -> [CopyRevolution,Sketch001,Pad]
  Origin = -> Origin001
  Tip = -> Pad
FEATURE [PartDesign::ShapeBinder] CopyRevolution001
  Placement = pos=(0,0,0) rot=(1,0,0;1.5708rad)
  TraceSupport = false
FEATURE [Sketcher::SketchObject] Sketch002
  ArcFitTolerance = 1e-06
  AttachmentSupport = -> [CopyRevolution001]
  FullyConstrained = true
  MakeInternals = false
  MapMode = 5
  Placement = pos=(0,1.1e-14,25) rot=(0,0,1;3.14159rad)
  sketch-geometry (5):
    g0: Circle CenterX=0 CenterY=0 CenterZ=0 NormalX=0 NormalY=0 NormalZ=1 AngleXU=0 Radius=2.5
    g1: ArcOfCircle CenterX=0 CenterY=0 CenterZ=0 NormalX=0 NormalY=0 NormalZ=1 AngleXU=0 Radius=5 StartAngle=0 EndAngle=3.14159
    g2: LineSegment StartX=5 StartY=0 StartZ=0 EndX=5 EndY=-65 EndZ=0
    g3: LineSegment StartX=5 StartY=-65 StartZ=0 EndX=-5 EndY=-65 EndZ=0
    g4: LineSegment StartX=-5 StartY=-65 StartZ=0 EndX=-5 EndY=0 EndZ=0
  constraints (12):
    c: Coincident(g1,g0)
    c: Radius(g0) = 2.5
    c: Coincident(g0,g-1)
    c: PointOnObject(g2,g-1)
    c: Coincident(g2,g3)
    c: Horizontal(g3)
    c: Coincident(g3,g4)
    c: PointOnObject(g4,g-1)
    c: Tangent(g1,g4) = 1.5708
    c: Tangent(g1,g2) = 1.5708
    c: DistanceX(g3,g3) = 10
    c: DistanceY(g4,g4) = 65
FEATURE [PartDesign::Pad] Pad001
  Direction = (0,0,1)
  Length = 1
  Length2 = 10
  Placement = pos=(0,0,0) rot=(1,0,0;1.5708rad)
  Profile = -> Sketch002
  ReferenceAxis = -> Sketch002 [N_Axis]
  Refine = true
  Suppressed = false
  Type = 0
FEATURE [PartDesign::Body] Body002
  AllowCompound = false
  Group = -> [CopyRevolution001,Sketch002,Pad001]
  Origin = -> Origin002
  Placement = pos=(0,0,1) rot=(0,0,1;1.0472rad)
  Tip = -> Pad001
FEATURE [PartDesign::ShapeBinder] CopyRevolution002
  Placement = pos=(0,0,0) rot=(1,0,0;1.5708rad)
  TraceSupport = false
FEATURE [Sketcher::SketchObject] Sketch003
  ArcFitTolerance = 1e-06
  AttachmentSupport = -> [CopyRevolution002]
  FullyConstrained = false
  MakeInternals = false
  MapMode = 5
  Placement = pos=(0,1.1e-14,25) rot=(0,0,1;3.14159rad)
  sketch-geometry (6):
    g0: Circle CenterX=0 CenterY=0 CenterZ=0 NormalX=0 NormalY=0 NormalZ=1 AngleXU=0 Radius=2.5
    g1: ArcOfCircle CenterX=0 CenterY=0 CenterZ=0 NormalX=0 NormalY=0 NormalZ=1 AngleXU=0 Radius=5 StartAngle=0.986756 EndAngle=6.86723
    g2: LineSegment StartX=4.17121 StartY=2.75699 StartZ=0 EndX=88.2635 EndY=86.8493 EndZ=0
    g3: LineSegment StartX=88.2635 StartY=86.8493 StartZ=0 EndX=86.8493 EndY=88.2635 EndZ=0
    g4: LineSegment StartX=2.75699 StartY=4.17121 StartZ=0 EndX=86.8493 EndY=88.2635 EndZ=0
    g5: LineSegment [constr] StartX=0 StartY=0 StartZ=0 EndX=87.5564 EndY=87.5564 EndZ=0
  constraints (14):
    c: Coincident(g0,g-1)
    c: Coincident(g0,g1)
    c: Radius(g0) = 2.5
    c: Coincident(g3,g2)
    c: Coincident(g4,g3)
    c: Coincident(g5,g0)
    c: Symmetric(g3,g3,g5)
    c: Angle(g-1,g5) = 0.785398
    c: Perpendicular(g3,g4)
    c: Perpendicular(g2,g3)
    c: Distance(g3) = 2
    c: Coincident(g1,g2)
    c: Coincident(g1,g4)
    c: Radius(g1) = 5
FEATURE [PartDesign::Pad] Pad002
  Direction = (0,0,1)
  Length = 0.5
  Length2 = 10
  Placement = pos=(0,0,0) rot=(1,0,0;1.5708rad)
  Profile = -> Sketch003
  ReferenceAxis = -> Sketch003 [N_Axis]
  Refine = true
  Suppressed = false
  Type = 0
FEATURE [PartDesign::Body] Body003
  AllowCompound = false
  Group = -> [CopyRevolution002,Sketch003,Pad002]
  Origin = -> Origin003
  Placement = pos=(0,0,2) rot=(0,0,1;0rad)
  Tip = -> Pad002
FEATURE [PartDesign::ShapeBinder] CopyRevolution003
  Placement = pos=(0,0,0) rot=(1,0,0;1.5708rad)
  TraceSupport = false
FEATURE [Sketcher::SketchObject] Sketch004
  ArcFitTolerance = 1e-06
  AttachmentSupport = -> [CopyRevolution003]
  FullyConstrained = true
  MakeInternals = false
  MapMode = 5
  Placement = pos=(0,1.1e-14,25) rot=(0,0,1;3.14159rad)
  sketch-geometry (4):
    g0: LineSegment StartX=-2.5 StartY=-110 StartZ=0 EndX=-2.5 EndY=-130 EndZ=0
    g1: LineSegment StartX=-2.5 StartY=-130 StartZ=0 EndX=2.5 EndY=-130 EndZ=0
    g2: LineSegment StartX=2.5 StartY=-130 StartZ=0 EndX=2.5 EndY=-110 EndZ=0
    g3: LineSegment StartX=2.5 StartY=-110 StartZ=0 EndX=-2.5 EndY=-110 EndZ=0
  constraints (11):
    c: Coincident(g0,g1)
    c: Coincident(g1,g2)
    c: Coincident(g2,g3)
    c: Coincident(g3,g0)
    c: Vertical(g0)
    c: Vertical(g2)
    c: Horizontal(g1)
    c: DistanceY(g0,g0) = 20
    c: DistanceX(g3,g3) = 5
    c: Symmetric(g0,g2,g-2)
    c: DistanceY(g0) = -110
FEATURE [PartDesign::Pad] Pad003
  Direction = (0,0,1)
  Length = 1
  Length2 = 10
  Placement = pos=(0,0,0) rot=(1,0,0;1.5708rad)
  Profile = -> Sketch004
  ReferenceAxis = -> Sketch004 [N_Axis]
  Refine = true
  Suppressed = false
  Type = 0
FEATURE [PartDesign::Body] Body004
  AllowCompound = false
  Group = -> [CopyRevolution003,Sketch004,Pad003]
  Origin = -> Origin004
  Tip = -> Pad003
FEATURE [Part::FeaturePython] Array  # Draft array (typed FeaturePython)
  AlwaysSyncPlacement = false
  Angle = 360
  ArrayType = 1
  Axis = (0,0,1)
  Base = -> Body004
  Center = (0,0,0)
  Count = 12
  ExpandArray = false
  Fuse = false
  IntervalAxis = (0,0,0)
  IntervalX = (100,0,0)
  IntervalY = (0,100,0)
  IntervalZ = (0,0,100)
  NumberCircles = 3
  NumberPolar = 12
  NumberX = 2
  NumberY = 2
  NumberZ = 1
  PlacementList = 12 placements: [(0,0,0),(0,0,0),(0,0,0),(0,0,0),(0,0,0),(0,0,0),(0,0,0),(0,0,0),(0,0,0),(0,0,0),(0,0,0),(0,0,0)]
  RadialDistance = 50
  ScaleList = (12) [(1,1,1),(1,1,1),(1,1,1),(1,1,1),(1,1,1),(1,1,1),(1,1,1),(1,1,1),(1,1,1),(1,1,1),(1,1,1),(1,1,1)]
  Symmetry = 1
  TangentialDistance = 25
FEATURE [PartDesign::ShapeBinder] CopyRevolution004
  Placement = pos=(0,0,0) rot=(1,0,0;1.5708rad)
  TraceSupport = false
FEATURE [Sketcher::SketchObject] Sketch005
  ArcFitTolerance = 1e-06
  AttachmentSupport = -> [CopyRevolution004]
  FullyConstrained = true
  MakeInternals = false
  MapMode = 5
  Placement = pos=(0,2.11e-14,48) rot=(0,0,1;3.14159rad)
  sketch-geometry (1):
    g0: Circle CenterX=0 CenterY=0 CenterZ=0 NormalX=0 NormalY=0 NormalZ=1 AngleXU=0 Radius=140
  constraints (2):
    c: Coincident(g0,g-1)
    c: Radius(g0) = 140
FEATURE [PartDesign::Pad] Pad004
  Direction = (0,0,1)
  Length = 2
  Length2 = 10
  Placement = pos=(0,0,0) rot=(1,0,0;1.5708rad)
  Profile = -> Sketch005
  ReferenceAxis = -> Sketch005 [N_Axis]
  Refine = true
  Suppressed = false
  Type = 0
FEATURE [PartDesign::Body] Body005
  AllowCompound = false
  Group = -> [CopyRevolution004,Sketch005,Pad004]
  Origin = -> Origin005
  Tip = -> Pad004
FEATURE [App::Part] Part  label="clock1"
  Group = -> [Body,Body001,Body002,Body003,Array,Body005]
  Origin = -> Origin006
  Placement = pos=(0,0,0) rot=(1,0,0;1.5708rad)
FEATURE [App::Part] Part001  label="clock2"
  Group = -> [Part]
  Origin = -> Origin007
  Placement = pos=(0,0,150) rot=(0,0,1;0rad)
FEATURE [App::Part] Part002  label="clock3"
  Group = -> [Part001]
  Origin = -> Origin008
  Placement = pos=(0,0,150) rot=(0,0,1;0rad)
FEATURE [Part::FeaturePython] Clone  label="around"  # Draft clone (typed FeaturePython)
  AttacherType = Attacher::AttachEngine3D
  Fuse = false
  Objects = -> [Body]
  Placement = pos=(0,0,150) rot=(1,0,0;1.5708rad)
  Scale = (1,1,1)
FEATURE [App::Part] Part003  label="around_p"
  Group = -> [Clone]
  Origin = -> Origin009
  Placement = pos=(0,0,150) rot=(0,0,1;0rad)
FEATURE [Part::FeaturePython] Clone001  label="hour"  # Draft clone (typed FeaturePython)
  AttacherType = Attacher::AttachEngine3D
  Fuse = false
  Objects = -> [Body002]
  Placement = pos=(0,0,1) rot=(0,0,1;1.0472rad)
  Scale = (1,1,1)
FEATURE [App::Part] Part005  label="hour1"
  Group = -> [Clone001]
  Origin = -> Origin011
  Placement = pos=(0,0,150) rot=(1,0,0;1.5708rad)
FEATURE [App::Part] Part004  label="hour_p"
  Group = -> [Part005]
  Origin = -> Origin010
  Placement = pos=(0,0,150) rot=(0,0,1;0rad)
FEATURE [Part::FeaturePython] Clone002  label="minute"  # Draft clone (typed FeaturePython)
  AttacherType = Attacher::AttachEngine3D
  Fuse = false
  Objects = -> [Body001]
  Scale = (1,1,1)
FEATURE [App::Part] Part007  label="minute1"
  Group = -> [Clone002]
  Origin = -> Origin013
  Placement = pos=(0,0,150) rot=(1,0,0;1.5708rad)
FEATURE [App::Part] Part006  label="minute_p"
  Group = -> [Part007]
  Origin = -> Origin012
  Placement = pos=(0,0,150) rot=(0,0,1;0rad)
FEATURE [Part::FeaturePython] Clone003  label="symbol"  # Draft clone (typed FeaturePython)
  AttacherType = Attacher::AttachEngine3D
  Fuse = false
  Objects = -> [Array]
  Placement = pos=(0,0,150) rot=(1,0,0;1.5708rad)
  Scale = (1,1,1)
FEATURE [App::Part] Part008  label="symbol_p"
  Group = -> [Clone003]
  Origin = -> Origin014
  Placement = pos=(0,0,150) rot=(0,0,1;0rad)
FEATURE [Part::FeaturePython] Clone004  label="second"  # Draft clone (typed FeaturePython)
  AttacherType = Attacher::AttachEngine3D
  Fuse = false
  Objects = -> [Body003]
  Placement = pos=(0,0,2) rot=(0,0,1;0rad)
  Scale = (1,1,1)
FEATURE [App::Part] Part010  label="second1"
  Group = -> [Clone004]
  Origin = -> Origin016
  Placement = pos=(0,0,150) rot=(1,0,0;1.5708rad)
FEATURE [App::Part] Part009  label="second_p"
  Group = -> [Part010]
  Origin = -> Origin015
  Placement = pos=(0,0,150) rot=(0,0,1;0rad)
FEATURE [Part::FeaturePython] Clone005  label="glass"  # Draft clone (typed FeaturePython)
  AttacherType = Attacher::AttachEngine3D
  Fuse = false
  Objects = -> [Body005]
  Placement = pos=(0,0,150) rot=(1,0,0;1.5708rad)
  Scale = (1,1,1)
FEATURE [App::Part] Part011  label="glass_p"
  Group = -> [Clone005]
  Origin = -> Origin017
  Placement = pos=(0,0,150) rot=(0,0,1;0rad)
FEATURE [Part::FeaturePython] Clone006  label="around_clone"  # Draft clone (typed FeaturePython)
  AttacherType = Attacher::AttachEngine3D
  Fuse = false
  Objects = -> [Part003]
  Scale = (1,1,1)
FEATURE [Part::FeaturePython] Clone007  label="hour_clone"  # Draft clone (typed FeaturePython)
  AttacherType = Attacher::AttachEngine3D
  Fuse = false
  Objects = -> [Part004]
  Scale = (1,1,1)
FEATURE [Part::FeaturePython] Clone008  label="minute_clone"  # Draft clone (typed FeaturePython)
  AttacherType = Attacher::AttachEngine3D
  Fuse = false
  Objects = -> [Part006]
  Scale = (1,1,1)
FEATURE [Part::FeaturePython] Clone009  label="second_clone"  # Draft clone (typed FeaturePython)
  AttacherType = Attacher::AttachEngine3D
  Fuse = false
  Objects = -> [Part009]
  Scale = (1,1,1)
FEATURE [Part::FeaturePython] Clone010  label="symbol_clone"  # Draft clone (typed FeaturePython)
  AttacherType = Attacher::AttachEngine3D
  Fuse = false
  Objects = -> [Part008]
  Scale = (1,1,1)
FEATURE [Part::FeaturePython] Clone011  label="glass_clone"  # Draft clone (typed FeaturePython)
  AttacherType = Attacher::AttachEngine3D
  Fuse = false
  Objects = -> [Part011]
  Scale = (1,1,1)
FEATURE [App::Part] Part012  label="clock"
  Group = -> [Clone006,Clone007,Clone008,Clone009,Clone010,Clone011]
  Origin = -> Origin018
---- part ../clothes_drying_pole/clothes_drying_pole.FCStd = doc fcstd_321dd4cf6566 ----
FCSTD DOCUMENT  (FreeCAD 1.0R39109 (Git))
Label: clothesdryingpole
License: All rights reserved
LicenseURL: https://en.wikipedia.org/wiki/All_rights_reserved
objects: Sketcher::SketchObject×9, PartDesign::Pad×8, PartDesign::ShapeBinder×5, PartDesign::Body×4, PartDesign::Line×2, App::Part×2, PartDesign::Pocket×1, Part::FeaturePython×1, Assembly::JointGroup×1, App::Link×1, Assembly::AssemblyObject×1
note: 56 computed .brp shape members not serialized (recipe doc carries the construction recipe); baked Part::Feature solids carry a one-line shape summary decoded from their .brp

FEATURE [Sketcher::SketchObject] Sketch
  ArcFitTolerance = 1e-06
  AttachmentSupport = -> [XZ_Plane]
  FullyConstrained = true
  MakeInternals = false
  MapMode = 5
  Placement = pos=(0,0,0) rot=(1,0,0;1.5708rad)
  sketch-geometry (16):
    g0: LineSegment StartX=-345 StartY=0 StartZ=0 EndX=-315 EndY=0 EndZ=0
    g1: LineSegment [constr] StartX=315 StartY=0 StartZ=0 EndX=345 EndY=0 EndZ=0
    g2: LineSegment [constr] StartX=-250 StartY=1300 StartZ=0 EndX=-220 EndY=1300 EndZ=0
    g3: LineSegment StartX=220 StartY=1300 StartZ=0 EndX=250 EndY=1300 EndZ=0
    g4: LineSegment [constr] StartX=-220 StartY=1300 StartZ=0 EndX=345 EndY=0 EndZ=0
    g5: LineSegment [constr] StartX=315 StartY=0 StartZ=0 EndX=-250 EndY=1300 EndZ=0
    g6: LineSegment StartX=220 StartY=1300 StartZ=0 EndX=6 EndY=780 EndZ=0
    g7: LineSegment StartX=-345 StartY=0 StartZ=0 EndX=-24 EndY=780 EndZ=0
    g8: LineSegment StartX=-315 StartY=0 StartZ=0 EndX=-8.59091 EndY=744.545 EndZ=0
    g9: LineSegment StartX=250 StartY=1300 StartZ=0 EndX=21.4091 EndY=744.545 EndZ=0
    g10: LineSegment [constr] StartX=-8.59091 StartY=744.545 StartZ=0 EndX=-8.59091 EndY=780 EndZ=0
    g11: LineSegment [constr] StartX=-8.59091 StartY=780 StartZ=0 EndX=-24 EndY=780 EndZ=0
    g12: LineSegment [constr] StartX=6 StartY=780 StartZ=0 EndX=6 EndY=744.545 EndZ=0
    g13: LineSegment [constr] StartX=21.4091 StartY=744.545 StartZ=0 EndX=6 EndY=744.545 EndZ=0
    g14: LineSegment StartX=-24 StartY=780 StartZ=0 EndX=6 EndY=780 EndZ=0
    g15: LineSegment StartX=-8.59091 StartY=744.545 StartZ=0 EndX=21.4091 EndY=744.545 EndZ=0
  constraints (44):
    c: PointOnObject(g0,g-1)
    c: PointOnObject(g0,g-1)
    c: PointOnObject(g1,g-1)
    c: Symmetric(g1,g0,g-1)
    c: DistanceX(g0,g1) = 690
    c: Equal(g1,g0)
    c: Horizontal(g2)
    c: DistanceY(g-1,g2) = 1300
    c: Symmetric(g3,g2,g-2)
    c: Horizontal(g3)
    c: DistanceX(g2,g3) = 500
    c: Equal(g3,g2)
    c: Equal(g2,g1)
    c: Coincident(g4,g2)
    c: Coincident(g4,g1)
    c: Coincident(g5,g1)
    c: Coincident(g5,g2)
    c: Coincident(g6,g3)
    c: Coincident(g7,g0)
    c: Coincident(g8,g0)
    c: Parallel(g6,g8)
    c: Parallel(g8,g7)
    c: Coincident(g9,g3)
    c: Parallel(g9,g6)
    c: Coincident(g10,g8)
    c: Vertical(g10)
    c: Coincident(g11,g10)
    c: Coincident(g11,g7)
    c: Horizontal(g11)
    c: Coincident(g12,g6)
    c: Vertical(g12)
    c: Coincident(g13,g9)
    c: Coincident(g13,g12)
    c: Horizontal(g13)
    c: Equal(g13,g11)
    c: PointOnObject(g9,g4)
    c: PointOnObject(g7,g5)
    c: PointOnObject(g8,g5)
    c: Horizontal(g6,g7)
    c: DistanceX(g0,g0) = 30
    c: Coincident(g14,g7)
    c: Coincident(g14,g6)
    c: Coincident(g15,g8)
    c: Coincident(g15,g9)
FEATURE [PartDesign::Pad] Pad
  Direction = (0,-1,2e-16)
  Length = 35
  Length2 = 10
  Midplane = true
  Placement = pos=(0,0,0) rot=(1,0,0;1.5708rad)
  Profile = -> Sketch
  ReferenceAxis = -> Sketch [N_Axis]
  Refine = true
  Suppressed = false
  Type = 0
FEATURE [Sketcher::SketchObject] Sketch001
  ArcFitTolerance = 1e-06
  AttachmentSupport = -> [XZ_Plane]
  FullyConstrained = false
  MakeInternals = false
  MapMode = 5
  Placement = pos=(0,0,0) rot=(1,0,0;1.5708rad)
  sketch-geometry (4):
    g0: LineSegment StartX=315 StartY=0 StartZ=0 EndX=345 EndY=0 EndZ=0
    g1: LineSegment StartX=-250 StartY=1300 StartZ=0 EndX=-220 EndY=1300 EndZ=0
    g2: LineSegment StartX=-220 StartY=1300 StartZ=0 EndX=345 EndY=0 EndZ=0
    g3: LineSegment StartX=315 StartY=0 StartZ=0 EndX=-250 EndY=1300 EndZ=0
  constraints (9):
    c: PointOnObject(g0,g-1)
    c: Horizontal(g1)
    c: DistanceY(g-1,g1) = 1300
    c: Equal(g1,g0)
    c: Coincident(g2,g1)
    c: Coincident(g2,g0)
    c: Coincident(g3,g0)
    c: Coincident(g3,g1)
    c: DistanceX(g1,g1) = 30
FEATURE [PartDesign::Pad] Pad001
  BaseFeature = -> Pad
  Direction = (0,-1,2e-16)
  Length = 30
  Length2 = 10
  Midplane = true
  Placement = pos=(0,0,0) rot=(1,0,0;1.5708rad)
  Profile = -> Sketch001
  ReferenceAxis = -> Sketch001 [N_Axis]
  Refine = true
  Suppressed = false
  Type = 0
FEATURE [Sketcher::SketchObject] Sketch002
  ArcFitTolerance = 1e-06
  AttachmentSupport = -> [Pad001]
  ExternalGeometry = -> [Pad001]
  FullyConstrained = true
  MakeInternals = false
  MapMode = 5
  Placement = pos=(0,0,-1e-16) rot=(1,0,0;3.14159rad)
  sketch-geometry (8):
    g0: LineSegment StartX=-347 StartY=19.5 StartZ=0 EndX=-347 EndY=-19.5 EndZ=0
    g1: LineSegment StartX=-347 StartY=-19.5 StartZ=0 EndX=-313 EndY=-19.5 EndZ=0
    g2: LineSegment StartX=-313 StartY=-19.5 StartZ=0 EndX=-313 EndY=19.5 EndZ=0
    g3: LineSegment StartX=-313 StartY=19.5 StartZ=0 EndX=-347 EndY=19.5 EndZ=0
    g4: LineSegment [constr] StartX=-345 StartY=17.5 StartZ=0 EndX=-347 EndY=17.5 EndZ=0
    g5: LineSegment [constr] StartX=-345 StartY=17.5 StartZ=0 EndX=-345 EndY=19.5 EndZ=0
    g6: LineSegment [constr] StartX=-315 StartY=-17.5 StartZ=0 EndX=-315 EndY=-19.5 EndZ=0
    g7: LineSegment [constr] StartX=-315 StartY=-17.5 StartZ=0 EndX=-313 EndY=-17.5 EndZ=0
  constraints (24):
    c: Coincident(g0,g1)
    c: Coincident(g1,g2)
    c: Coincident(g2,g3)
    c: Coincident(g3,g0)
    c: Vertical(g0)
    c: Vertical(g2)
    c: Horizontal(g1)
    c: Horizontal(g3)
    c: Coincident(g4,g-3)
    c: PointOnObject(g4,g0)
    c: Horizontal(g4)
    c: Coincident(g5,g4)
    c: PointOnObject(g5,g3)
    c: Vertical(g5)
    c: Coincident(g6,g-4)
    c: PointOnObject(g6,g1)
    c: Vertical(g6)
    c: Coincident(g7,g6)
    c: PointOnObject(g7,g2)
    c: Horizontal(g7)
    c: Equal(g7,g6)
    c: Equal(g6,g5)
    c: Equal(g5,g4)
    c: DistanceY(g5,g5) = 2
FEATURE [PartDesign::Pad] Pad002
  BaseFeature = -> Pad001
  Direction = (0.380571,2e-16,0.924752)
  Length = 30
  Length2 = 10
  Placement = pos=(0,0,0) rot=(1,0,0;1.5708rad)
  Profile = -> Sketch002
  ReferenceAxis = -> Pad001 [Edge24]
  Refine = true
  Suppressed = false
  Type = 0
FEATURE [Sketcher::SketchObject] Sketch003
  ArcFitTolerance = 1e-06
  AttachmentSupport = -> [Pad002]
  ExternalGeometry = -> [Pad002]
  FullyConstrained = true
  MakeInternals = false
  MapMode = 5
  Placement = pos=(0,0,-1e-16) rot=(1,0,0;3.14159rad)
  sketch-geometry (8):
    g0: LineSegment StartX=313 StartY=17 StartZ=0 EndX=313 EndY=-17 EndZ=0
    g1: LineSegment StartX=313 StartY=-17 StartZ=0 EndX=347 EndY=-17 EndZ=0
    g2: LineSegment StartX=347 StartY=-17 StartZ=0 EndX=347 EndY=17 EndZ=0
    g3: LineSegment StartX=347 StartY=17 StartZ=0 EndX=313 EndY=17 EndZ=0
    g4: LineSegment [constr] StartX=315 StartY=15 StartZ=0 EndX=313 EndY=15 EndZ=0
    g5: LineSegment [constr] StartX=315 StartY=15 StartZ=0 EndX=315 EndY=17 EndZ=0
    g6: LineSegment [constr] StartX=345 StartY=-15 StartZ=0 EndX=345 EndY=-17 EndZ=0
    g7: LineSegment [constr] StartX=345 StartY=-15 StartZ=0 EndX=347 EndY=-15 EndZ=0
  constraints (24):
    c: Coincident(g0,g1)
    c: Coincident(g1,g2)
    c: Coincident(g2,g3)
    c: Coincident(g3,g0)
    c: Vertical(g0)
    c: Vertical(g2)
    c: Horizontal(g1)
    c: Horizontal(g3)
    c: Coincident(g4,g-3)
    c: PointOnObject(g4,g0)
    c: Horizontal(g4)
    c: Coincident(g5,g4)
    c: PointOnObject(g5,g3)
    c: Vertical(g5)
    c: Coincident(g6,g-4)
    c: PointOnObject(g6,g1)
    c: Vertical(g6)
    c: Coincident(g7,g6)
    c: PointOnObject(g7,g2)
    c: Horizontal(g7)
    c: Equal(g5,g4)
    c: Equal(g4,g6)
    c: Equal(g6,g7)
    c: DistanceY(g5,g5) = 2
FEATURE [PartDesign::Pad] Pad003
  BaseFeature = -> Pad002
  Direction = (-0.398597,2e-16,0.917126)
  Length = 30
  Length2 = 10
  Placement = pos=(0,0,0) rot=(1,0,0;1.5708rad)
  Profile = -> Sketch003
  ReferenceAxis = -> Pad002 [Edge49]
  Refine = true
  Suppressed = false
  Type = 0
FEATURE [Sketcher::SketchObject] Sketch004
  ArcFitTolerance = 1e-06
  AttachmentSupport = -> [XZ_Plane]
  ExternalGeometry = -> [Pad003]
  FullyConstrained = true
  MakeInternals = false
  MapMode = 5
  Placement = pos=(0,0,0) rot=(1,0,0;1.5708rad)
  sketch-geometry (4):
    g0: Circle CenterX=-235 CenterY=1300 CenterZ=0 NormalX=0 NormalY=0 NormalZ=1 AngleXU=0 Radius=15
    g1: LineSegment [constr] StartX=-220 StartY=1300 StartZ=0 EndX=-219 EndY=1300 EndZ=0
    g2: Circle CenterX=235 CenterY=1300 CenterZ=0 NormalX=0 NormalY=0 NormalZ=1 AngleXU=0 Radius=15
    g3: LineSegment [constr] StartX=220 StartY=1300 StartZ=0 EndX=219 EndY=1300 EndZ=0
  constraints (14):
    c: PointOnObject(g1,g0)
    c: Horizontal(g1)
    c: DistanceX(g1,g1) = 1
    c: PointOnObject(g-3,g0)
    c: PointOnObject(g-3,g0)
    c: Horizontal(g1,g0)
    c: PointOnObject(g3,g2)
    c: Horizontal(g3,g2)
    c: Horizontal(g3)
    c: Radius(g0) = 15
    c: DistanceX(g3,g3) = 1
    c: Radius(g2) = 15
    c: PointOnObject(g-4,g2)
    c: PointOnObject(g-4,g2)
FEATURE [PartDesign::Pocket] Pocket
  BaseFeature = -> Pad003
  Direction = (0,1,-2e-16)
  Length = 40
  Length2 = 5
  Midplane = true
  Placement = pos=(0,0,0) rot=(1,0,0;1.5708rad)
  Profile = -> Sketch004
  ReferenceAxis = -> Sketch004 [N_Axis]
  Refine = true
  Suppressed = false
  Type = 0
FEATURE [Sketcher::SketchObject] Sketch005
  ArcFitTolerance = 1e-06
  AttachmentSupport = -> [XZ_Plane]
  ExternalGeometry = -> [Pocket]
  FullyConstrained = false
  MakeInternals = false
  MapMode = 5
  Placement = pos=(0,0,0) rot=(1,0,0;1.5708rad)
  sketch-geometry (6):
    g0: Circle CenterX=-235 CenterY=1300.01 CenterZ=0 NormalX=0 NormalY=0 NormalZ=1 AngleXU=0 Radius=15
    g1: Circle CenterX=-235 CenterY=1300.01 CenterZ=0 NormalX=0 NormalY=0 NormalZ=1 AngleXU=0 Radius=16
    g2: Circle CenterX=235 CenterY=1300 CenterZ=0 NormalX=0 NormalY=0 NormalZ=1 AngleXU=0 Radius=16
    g3: LineSegment [constr] StartX=220 StartY=1300 StartZ=0 EndX=219 EndY=1300 EndZ=0
    g4: LineSegment [constr] StartX=-220 StartY=1300 StartZ=0 EndX=-219 EndY=1300 EndZ=0
    g5: Circle CenterX=235 CenterY=1300 CenterZ=0 NormalX=0 NormalY=0 NormalZ=1 AngleXU=0 Radius=15
  constraints (13):
    c: Radius(g0) = 15
    c: Coincident(g1,g0)
    c: PointOnObject(g3,g2)
    c: PointOnObject(g4,g0)
    c: PointOnObject(g4,g1)
    c: Coincident(g4,g-4)
    c: Horizontal(g4)
    c: Coincident(g3,g-3)
    c: Horizontal(g3)
    c: Equal(g4,g3)
    c: DistanceX(g4,g4) = 1
    c: Coincident(g5,g2)
    c: Radius(g5) = 15
FEATURE [PartDesign::Pad] Pad004
  BaseFeature = -> Pocket
  Direction = (0,-1,2e-16)
  Length = 40
  Length2 = 10
  Midplane = true
  Placement = pos=(0,0,0) rot=(1,0,0;1.5708rad)
  Profile = -> Sketch005
  ReferenceAxis = -> Sketch005 [N_Axis]
  Refine = true
  Suppressed = false
  Type = 0
FEATURE [PartDesign::Body] Body
  AllowCompound = false
  Group = -> [Sketch,Pad,Sketch001,Pad001,Sketch002,Pad002,Sketch003,Pad003,Sketch004,Pocket,Sketch005,Pad004]
  Origin = -> Origin
  Tip = -> Pad004
FEATURE [Part::FeaturePython] Array  # Draft array (typed FeaturePython)
  AlwaysSyncPlacement = false
  Angle = 360
  ArrayType = 0
  Axis = (0,0,1)
  Base = -> Pad004
  Center = (0,0,0)
  Count = 2
  ExpandArray = false
  Fuse = false
  IntervalAxis = (0,0,0)
  IntervalX = (100,0,0)
  IntervalY = (0,1600,0)
  IntervalZ = (0,0,100)
  NumberCircles = 3
  NumberPolar = 5
  NumberX = 1
  NumberY = 2
  NumberZ = 1
  PlacementList = 2 placements: [(0,0,0),(0,1600,0)]
  RadialDistance = 50
  ScaleList = (2) [(1,1,1),(1,1,1)]
  Symmetry = 1
  TangentialDistance = 25
FEATURE [PartDesign::ShapeBinder] CopyPad004
  Placement = pos=(0,0,0) rot=(1,0,0;1.5708rad)
  TraceSupport = false
FEATURE [Sketcher::SketchObject] Sketch006
  ArcFitTolerance = 1e-06
  AttachmentSupport = -> [CopyPad004]
  FullyConstrained = false
  MakeInternals = false
  MapMode = 5
  Placement = pos=(0,-17.5,3.8e-15) rot=(1,0,0;1.5708rad)
  sketch-geometry (2):
    g0: Circle CenterX=-235 CenterY=1300.01 CenterZ=0 NormalX=0 NormalY=0 NormalZ=1 AngleXU=0 Radius=15
    g1: Circle CenterX=235 CenterY=1300 CenterZ=0 NormalX=0 NormalY=0 NormalZ=1 AngleXU=0 Radius=15
  constraints (2):
    c: Radius(g0) = 15
    c: Radius(g1) = 15
FEATURE [PartDesign::Pad] Pad005
  Direction = (0,-1,2e-16)
  Length = 1650
  Length2 = 10
  Placement = pos=(0,0,0) rot=(1,0,0;1.5708rad)
  Profile = -> Sketch006
  ReferenceAxis = -> Sketch006 [N_Axis]
  Refine = true
  Suppressed = false
  Type = 0
FEATURE [PartDesign::Body] Body001
  AllowCompound = false
  Group = -> [CopyPad004,Sketch006,Pad005]
  Origin = -> Origin001
  Placement = pos=(0,1640,0) rot=(0,0,1;0rad)
  Tip = -> Pad005
FEATURE [PartDesign::ShapeBinder] CopyPad005
  Placement = pos=(0,0,0) rot=(1,0,0;1.5708rad)
  TraceSupport = false
FEATURE [Sketcher::SketchObject] Sketch007
  ArcFitTolerance = 1e-06
  AttachmentSupport = -> [CopyPad005]
  FullyConstrained = false
  MakeInternals = false
  MapMode = 5
  Placement = pos=(0,-15,3.3e-15) rot=(1,0,0;1.5708rad)
  sketch-geometry (1):
    g0: Circle CenterX=-235 CenterY=1300.01 CenterZ=0 NormalX=0 NormalY=0 NormalZ=1 AngleXU=0 Radius=15
  constraints (1):
    c: Radius(g0) = 15
FEATURE [PartDesign::Pad] Pad006
  Direction = (0,-1,2e-16)
  Length = 1650
  Length2 = 10
  Placement = pos=(0,0,0) rot=(1,0,0;1.5708rad)
  Profile = -> Sketch007
  ReferenceAxis = -> Sketch007 [N_Axis]
  Refine = true
  Suppressed = false
  Type = 0
FEATURE [PartDesign::Body] Body002
  AllowCompound = false
  Group = -> [CopyPad005,Sketch007,Pad006]
  Origin = -> Origin002
  Placement = pos=(0,1640,0) rot=(0,0,1;0rad)
  Tip = -> Pad006
FEATURE [PartDesign::ShapeBinder] CopyPad006
  Placement = pos=(0,-15,3.3e-15) rot=(1,0,0;1.5708rad)
  TraceSupport = false
FEATURE [PartDesign::Line] DatumLine
  AttacherType = Attacher::AttachEngineLine
  AttachmentSupport = -> [CopyPad006]
  Length = 20
  MapMode = 29
  Placement = pos=(290.187,-15,126.12) rot=(0.699587,0.699587,0.145454;2.85271rad)
  ResizeMode = 0
FEATURE [PartDesign::ShapeBinder] CopyPad007
  Placement = pos=(0,-17.5,3.9e-15) rot=(1,0,0;1.5708rad)
  TraceSupport = false
FEATURE [PartDesign::Line] DatumLine001
  AttacherType = Attacher::AttachEngineLine
  AttachmentSupport = -> [CopyPad007]
  Length = 20
  MapMode = 29
  Placement = pos=(-269.377,-17.5,110.859) rot=(0.700295,-0.700295,-0.138466;2.86641rad)
  ResizeMode = 0
FEATURE [PartDesign::ShapeBinder] CopyPad008
  Placement = pos=(0,0,0) rot=(1,0,0;1.5708rad)
  TraceSupport = false
FEATURE [Sketcher::SketchObject] Sketch008
  ArcFitTolerance = 1e-06
  AttachmentSupport = -> [CopyPad008]
  ExternalGeometry = -> [DatumLine,DatumLine001]
  FullyConstrained = true
  MakeInternals = false
  MapMode = 5
  Placement = pos=(0,-17.5,3.8e-15) rot=(1,0,0;1.5708rad)
  sketch-geometry (1):
    g0: Circle CenterX=5.62322 CenterY=818.499 CenterZ=0 NormalX=0 NormalY=0 NormalZ=1 AngleXU=0 Radius=15
  constraints (3):
    c: Radius(g0) = 15
    c: Tangent(g0,g-4)
    c: Tangent(g0,g-3)
FEATURE [PartDesign::Pad] Pad007
  Direction = (0,-1,2e-16)
  Length = 1650
  Length2 = 10
  Placement = pos=(0,0,0) rot=(1,0,0;1.5708rad)
  Profile = -> Sketch008
  ReferenceAxis = -> Sketch008 [N_Axis]
  Refine = true
  Suppressed = false
  Type = 0
FEATURE [PartDesign::Body] Body003
  AllowCompound = false
  Group = -> [DatumLine,CopyPad006,DatumLine001,CopyPad007,CopyPad008,Sketch008,Pad007]
  Origin = -> Origin003
  Placement = pos=(0,1640,0) rot=(0,0,1;0rad)
  Tip = -> Pad007
FEATURE [App::Part] Part
  Group = -> [Body,Array,Body001,Body002,Body003]
  Origin = -> Origin004
  Placement = pos=(0,-812.5,0) rot=(0,0,1;0rad)
FEATURE [Assembly::JointGroup] Joints
FEATURE [App::Link] Part001
  LinkedObject = -> Part
FEATURE [Assembly::AssemblyObject] Assembly
  Group = -> [Joints,Part001]
  Origin = -> Origin005
  Placement = pos=(0,-812.5,0) rot=(0,0,1;0rad)
  Type = Assembly
FEATURE [App::Part] Part002  label="clothesdryingpole"
  Group = -> [Assembly,Part]
  Origin = -> Origin006
---- part ../cocktail/cocktail.FCStd = doc fcstd_cef7cd4f3ac4 ----
FCSTD DOCUMENT  (FreeCAD 1.0R39109 (Git))
Label: cocktail
License: All rights reserved
LicenseURL: https://en.wikipedia.org/wiki/All_rights_reserved
objects: Sketcher::SketchObject×4, PartDesign::Body×3, Part::FeaturePython×3, PartDesign::Revolution×2, PartDesign::Fillet×2, App::Part×2, PartDesign::AdditivePipe×1
note: 29 computed .brp shape members not serialized (recipe doc carries the construction recipe); baked Part::Feature solids carry a one-line shape summary decoded from their .brp

FEATURE [Sketcher::SketchObject] Sketch
  ArcFitTolerance = 1e-06
  AttachmentSupport = -> [XZ_Plane]
  FullyConstrained = true
  MakeInternals = false
  MapMode = 5
  Placement = pos=(0,0,0) rot=(1,0,0;1.5708rad)
  sketch-geometry (18):
    g0: LineSegment StartX=0 StartY=50 StartZ=0 EndX=0 EndY=0 EndZ=0
    g1: LineSegment StartX=0 StartY=0 StartZ=0 EndX=40 EndY=0 EndZ=0
    g2: LineSegment StartX=40 StartY=0 StartZ=0 EndX=40 EndY=1 EndZ=0
    g3: LineSegment StartX=40 StartY=1 StartZ=0 EndX=2.5 EndY=2.5 EndZ=0
    g4: LineSegment StartX=2.5 StartY=2.5 StartZ=0 EndX=2.5 EndY=47.5 EndZ=0
    g5: Circle [constr] CenterX=0 CenterY=50 CenterZ=0 NormalX=0 NormalY=0 NormalZ=1 AngleXU=0 Radius=1
    g6: Circle [constr] CenterX=40 CenterY=82.5 CenterZ=0 NormalX=0 NormalY=0 NormalZ=1 AngleXU=0 Radius=1
    g7: Circle [constr] CenterX=40 CenterY=150 CenterZ=0 NormalX=0 NormalY=0 NormalZ=1 AngleXU=0 Radius=1
    g8: BSplineCurve PolesCount=3 KnotsCount=2 Degree=2 IsPeriodic=0
    g9: GeomPoint [constr] X=0 Y=50 Z=0
    g10: GeomPoint [constr] X=40 Y=150 Z=0
    g11: Circle [constr] CenterX=42.5 CenterY=150 CenterZ=0 NormalX=0 NormalY=0 NormalZ=1 AngleXU=0 Radius=1
    g12: Circle [constr] CenterX=42.5 CenterY=80 CenterZ=0 NormalX=0 NormalY=0 NormalZ=1 AngleXU=0 Radius=1
    g13: Circle [constr] CenterX=2.5 CenterY=47.5 CenterZ=0 NormalX=0 NormalY=0 NormalZ=1 AngleXU=0 Radius=1
    g14: BSplineCurve PolesCount=3 KnotsCount=2 Degree=2 IsPeriodic=0
    g15: GeomPoint [constr] X=42.5 Y=150 Z=0
    g16: GeomPoint [constr] X=2.5 Y=47.5 Z=0
    g17: LineSegment StartX=40 StartY=150 StartZ=0 EndX=42.5 EndY=150 EndZ=0
  constraints (43):
    c: PointOnObject(g0,g-2)
    c: Coincident(g0,g-1)
    c: Coincident(g0,g1)
    c: PointOnObject(g1,g-1)
    c: Coincident(g1,g2)
    c: Vertical(g2)
    c: Coincident(g2,g3)
    c: Coincident(g3,g4)
    c: Vertical(g4)
    c: DistanceY(g0,g0) = 50
    c: DistanceX(g1) = 40
    c: DistanceY(g2) = 1
    c: DistanceY(g0,g3) = 2.5
    c: DistanceX(g0,g3) = 2.5
    c: DistanceY(g4,g0) = 2.5
    c: Weight(g5) = 1
    c: Equal(g5,g6)
    c: Equal(g5,g7)
    c: InternalAlignment(g5,g8)
    c: InternalAlignment(g6,g8)
    c: InternalAlignment(g7,g8)
    c: InternalAlignment(g9,g8)
    c: InternalAlignment(g10,g8)
    c: Coincident(g5,g0)
    c: Weight(g11) = 1
    c: Equal(g11,g12)
    c: Equal(g11,g13)
    c: InternalAlignment(g11,g14)
    c: InternalAlignment(g12,g14)
    c: InternalAlignment(g13,g14)
    c: InternalAlignment(g15,g14)
    c: InternalAlignment(g16,g14)
    c: Coincident(g13,g4)
    c: DistanceY(g12,g6) = 2.5
    c: DistanceY(g12) = 80
    c: Vertical(g14,g12)
    c: Vertical(g6,g8)
    c: DistanceY(g14) = 150
    c: DistanceX(g8) = 40
    c: Coincident(g17,g8)
    c: Coincident(g17,g14)
    c: Horizontal(g17)
    c: DistanceX(g17,g17) = 2.5
FEATURE [PartDesign::Revolution] Revolution
  Angle = 360
  Angle2 = 60
  Axis = (0,2e-16,1)
  Base = (0,0,0)
  Placement = pos=(0,0,0) rot=(1,0,0;1.5708rad)
  Profile = -> Sketch
  ReferenceAxis = -> Sketch [V_Axis]
  Refine = true
  Reversed = true
  Suppressed = false
  Type = 0
FEATURE [PartDesign::Fillet] Fillet
  Base = -> Revolution [Face6]
  BaseFeature = -> Revolution
  Placement = pos=(0,0,0) rot=(1,0,0;1.5708rad)
  Radius = 0.5
  Refine = true
  SupportTransform = false
  Suppressed = false
  UseAllEdges = false
FEATURE [PartDesign::Fillet] Fillet001
  Base = -> Fillet [Edge6,Edge3]
  BaseFeature = -> Fillet
  Placement = pos=(0,0,0) rot=(1,0,0;1.5708rad)
  Radius = 5
  Refine = true
  SupportTransform = false
  Suppressed = false
  UseAllEdges = false
FEATURE [PartDesign::Body] Body
  AllowCompound = false
  Group = -> [Sketch,Revolution,Fillet,Fillet001]
  Origin = -> Origin
  Tip = -> Fillet001
FEATURE [Sketcher::SketchObject] Sketch001
  ArcFitTolerance = 1e-06
  AttachmentSupport = -> [XZ_Plane001]
  FullyConstrained = true
  MakeInternals = false
  MapMode = 5
  Placement = pos=(0,0,0) rot=(1,0,0;1.5708rad)
  sketch-geometry (8):
    g0: LineSegment StartX=0 StartY=120 StartZ=0 EndX=0 EndY=50 EndZ=0
    g1: LineSegment StartX=0 StartY=120 StartZ=0 EndX=37.5 EndY=120 EndZ=0
    g2: Circle [constr] CenterX=37.5 CenterY=120 CenterZ=0 NormalX=0 NormalY=0 NormalZ=1 AngleXU=0 Radius=1
    g3: Circle [constr] CenterX=30 CenterY=75 CenterZ=0 NormalX=0 NormalY=0 NormalZ=1 AngleXU=0 Radius=1
    g4: Circle [constr] CenterX=0 CenterY=50 CenterZ=0 NormalX=0 NormalY=0 NormalZ=1 AngleXU=0 Radius=1
    g5: BSplineCurve PolesCount=3 KnotsCount=2 Degree=2 IsPeriodic=0
    g6: GeomPoint [constr] X=37.5 Y=120 Z=0
    g7: GeomPoint [constr] X=0 Y=50 Z=0
  constraints (19):
    c: Coincident(g0,g1)
    c: Horizontal(g1)
    c: Vertical(g0)
    c: PointOnObject(g0,g-2)
    c: DistanceY(g0) = 50
    c: DistanceX(g1) = 37.5
    c: Weight(g2) = 1
    c: Equal(g2,g3)
    c: Equal(g2,g4)
    c: InternalAlignment(g2,g5)
    c: InternalAlignment(g3,g5)
    c: InternalAlignment(g4,g5)
    c: InternalAlignment(g6,g5)
    c: InternalAlignment(g7,g5)
    c: Coincident(g4,g0)
    c: Coincident(g5,g1)
    c: DistanceX(g3) = 30
    c: DistanceY(g3) = 75
    c: DistanceY(g1) = 120
FEATURE [PartDesign::Revolution] Revolution001
  Angle = 360
  Angle2 = 60
  Axis = (0,2e-16,1)
  Base = (0,0,0)
  Placement = pos=(0,0,0) rot=(1,0,0;1.5708rad)
  Profile = -> Sketch001
  ReferenceAxis = -> Sketch001 [V_Axis]
  Refine = true
  Reversed = true
  Suppressed = false
  Type = 0
FEATURE [PartDesign::Body] Body001
  AllowCompound = false
  Group = -> [Sketch001,Revolution001]
  Origin = -> Origin001
  Tip = -> Revolution001
FEATURE [Sketcher::SketchObject] Sketch002
  ArcFitTolerance = 1e-06
  AttachmentSupport = -> [XZ_Plane002]
  FullyConstrained = true
  MakeInternals = false
  MapMode = 5
  Placement = pos=(0,0,0) rot=(1,0,0;1.5708rad)
  sketch-geometry (2):
    g0: LineSegment StartX=0 StartY=53 StartZ=0 EndX=45.6096 EndY=169.382 EndZ=0
    g1: LineSegment StartX=45.6096 StartY=169.382 StartZ=0 EndX=84.3394 EndY=179.382 EndZ=0
  constraints (7):
    c: PointOnObject(g0,g-2)
    c: Coincident(g0,g1)
    c: Distance(g1) = 40
    c: Distance(g0) = 125
    c: DistanceY(g0) = 53
    c: DistanceY(g0,g1) = 10
    c: Angle(g-1,g0) = 1.1973
FEATURE [Sketcher::SketchObject] Sketch003
  ArcFitTolerance = 1e-06
  AttachmentSupport = -> [XY_Plane002]
  FullyConstrained = true
  MakeInternals = false
  Placement = pos=(0,0,53) rot=(0,1,0;0.3735rad)
  sketch-geometry (2):
    g0: Circle CenterX=0 CenterY=0 CenterZ=0 NormalX=0 NormalY=0 NormalZ=1 AngleXU=0 Radius=1.8
    g1: Circle CenterX=0 CenterY=0 CenterZ=0 NormalX=0 NormalY=0 NormalZ=1 AngleXU=0 Radius=2
  constraints (4):
    c: Coincident(g0,g-1)
    c: Coincident(g1,g0)
    c: Radius(g1) = 2
    c: Radius(g0) = 1.8
FEATURE [PartDesign::AdditivePipe] AdditivePipe
  AuxilleryCurvelinear = true
  AuxillerySpineTangent = false
  Binormal = (0,0,0)
  Mode = 0
  Profile = -> Sketch003
  Refine = true
  Spine = -> Sketch002
  SpineTangent = false
  Suppressed = false
  Transformation = 0
  Transition = 2
FEATURE [PartDesign::Body] Body002
  AllowCompound = false
  Group = -> [Sketch002,Sketch003,AdditivePipe]
  Origin = -> Origin002
  Tip = -> AdditivePipe
FEATURE [App::Part] Part  label="cocktail_p"
  Group = -> [Body,Body001,Body002]
  Origin = -> Origin003
FEATURE [Part::FeaturePython] Clone  label="glass"  # Draft clone (typed FeaturePython)
  AttacherType = Attacher::AttachEngine3D
  Fuse = false
  Objects = -> [Body]
  Scale = (1,1,1)
FEATURE [Part::FeaturePython] Clone001  label="content"  # Draft clone (typed FeaturePython)
  AttacherType = Attacher::AttachEngine3D
  Fuse = false
  Objects = -> [Body001]
  Scale = (1,1,1)
FEATURE [Part::FeaturePython] Clone002  label="straw"  # Draft clone (typed FeaturePython)
  AttacherType = Attacher::AttachEngine3D
  Fuse = false
  Objects = -> [Body002]
  Scale = (1,1,1)
FEATURE [App::Part] Part001  label="cocktail"
  Group = -> [Clone,Clone001,Clone002]
  Origin = -> Origin004
---- part ../dressing_table/Dressing_Table.FCStd = doc fcstd_4a7c8d0d2b5c (61602 chars; too large to inline — full recipe in that document) ----
---- part ../furniture/furniture.FCStd = doc fcstd_ed94128c1266 ----
FCSTD DOCUMENT  (FreeCAD 1.0R39109 (Git))
Label: furniture
License: All rights reserved
LicenseURL: https://en.wikipedia.org/wiki/All_rights_reserved
objects: App::Part×4, Sketcher::SketchObject×3, PartDesign::Pad×3, Part::FeaturePython×3, PartDesign::Body×2, Assembly::JointGroup×2, App::Link×2, Assembly::AssemblyObject×2, PartDesign::Fillet×1, PartDesign::Thickness×1, PartDesign::ShapeBinder×1, PartDesign::Plane×1
note: 27 computed .brp shape members not serialized (recipe doc carries the construction recipe); baked Part::Feature solids carry a one-line shape summary decoded from their .brp

FEATURE [Sketcher::SketchObject] Sketch
  ArcFitTolerance = 1e-06
  AttachmentSupport = -> [XY_Plane]
  FullyConstrained = true
  MakeInternals = false
  MapMode = 5
  sketch-geometry (4):
    g0: LineSegment StartX=-600 StartY=200 StartZ=0 EndX=-600 EndY=-200 EndZ=0
    g1: LineSegment StartX=-600 StartY=-200 StartZ=0 EndX=600 EndY=-200 EndZ=0
    g2: LineSegment StartX=600 StartY=-200 StartZ=0 EndX=600 EndY=200 EndZ=0
    g3: LineSegment StartX=600 StartY=200 StartZ=0 EndX=-600 EndY=200 EndZ=0
  constraints (11):
    c: Coincident(g0,g1)
    c: Coincident(g1,g2)
    c: Coincident(g2,g3)
    c: Coincident(g3,g0)
    c: Vertical(g0)
    c: Vertical(g2)
    c: Horizontal(g1)
    c: Horizontal(g3)
    c: Symmetric(g1,g0,g-1)
    c: DistanceX(g3,g3) = 1200
    c: DistanceY(g0,g0) = 400
FEATURE [PartDesign::Pad] Pad
  Direction = (0,0,1)
  Length = 600
  Length2 = 10
  Midplane = true
  Profile = -> Sketch
  ReferenceAxis = -> Sketch [N_Axis]
  Refine = true
  Suppressed = false
  Type = 0
FEATURE [PartDesign::Fillet] Fillet
  Base = -> Pad [Edge8,Edge5,Face5,Edge2,Edge1]
  BaseFeature = -> Pad
  Radius = 50
  Refine = true
  SupportTransform = false
  Suppressed = false
  UseAllEdges = false
FEATURE [PartDesign::Thickness] Thickness
  Base = -> Fillet [Face2]
  BaseFeature = -> Fillet
  Intersection = false
  Join = 0
  Mode = 0
  Refine = true
  Reversed = true
  SupportTransform = false
  Suppressed = false
  Value = 25
FEATURE [Sketcher::SketchObject] Sketch001
  ArcFitTolerance = 1e-06
  AttachmentSupport = -> [Thickness]
  ExternalGeometry = -> [Thickness]
  FullyConstrained = true
  MakeInternals = false
  MapMode = 5
  Placement = pos=(0,0,300) rot=(0,0,1;0rad)
  sketch-geometry (4):
    g0: LineSegment StartX=-575 StartY=12.5 StartZ=0 EndX=-575 EndY=-12.5 EndZ=0
    g1: LineSegment StartX=-575 StartY=-12.5 StartZ=0 EndX=575 EndY=-12.5 EndZ=0
    g2: LineSegment StartX=575 StartY=-12.5 StartZ=0 EndX=575 EndY=12.5 EndZ=0
    g3: LineSegment StartX=575 StartY=12.5 StartZ=0 EndX=-575 EndY=12.5 EndZ=0
  constraints (11):
    c: Coincident(g1,g2)
    c: Coincident(g2,g3)
    c: Coincident(g3,g0)
    c: Vertical(g0)
    c: Vertical(g2)
    c: Horizontal(g3)
    c: Coincident(g0,g1)
    c: PointOnObject(g0,g-4)
    c: Symmetric(g2,g0,g-1)
    c: Parallel(g1,g3)
    c: DistanceY(g0,g0) = 25
FEATURE [PartDesign::Pad] Pad001
  BaseFeature = -> Thickness
  Direction = (0,0,1)
  Length = 10
  Length2 = 10
  Profile = -> Sketch001
  ReferenceAxis = -> Sketch001 [N_Axis]
  Refine = true
  Suppressed = false
  Type = 3
  UpToFace = -> Thickness [Face28]
FEATURE [PartDesign::Body] Body
  AllowCompound = false
  Group = -> [Sketch,Pad,Fillet,Thickness,Sketch001,Pad001]
  Origin = -> Origin
  Tip = -> Pad001
FEATURE [PartDesign::ShapeBinder] CopyPad001
  TraceSupport = false
FEATURE [PartDesign::Plane] DatumPlane
  AttachmentSupport = -> [CopyPad001]
  Length = 60
  MapMode = 5
  Placement = pos=(0,0,300) rot=(0,0,1;0rad)
  ResizeMode = 0
  Width = 60
FEATURE [Sketcher::SketchObject] Sketch002
  ArcFitTolerance = 1e-06
  AttachmentSupport = -> [CopyPad001]
  ExternalGeometry = -> [CopyPad001]
  FullyConstrained = true
  MakeInternals = false
  MapMode = 5
  Placement = pos=(0,0,300) rot=(0,0,1;0rad)
  sketch-geometry (12):
    g0: ArcOfCircle CenterX=-550 CenterY=-150 CenterZ=0 NormalX=0 NormalY=0 NormalZ=1 AngleXU=0 Radius=74.9999 StartAngle=3.14159 EndAngle=4.71239
    g1: ArcOfCircle CenterX=550 CenterY=-150 CenterZ=0 NormalX=0 NormalY=0 NormalZ=1 AngleXU=0 Radius=50 StartAngle=4.71239 EndAngle=6.28319
    g2: ArcOfCircle CenterX=550 CenterY=-150 CenterZ=0 NormalX=0 NormalY=0 NormalZ=1 AngleXU=0 Radius=75 StartAngle=4.71239 EndAngle=6.28318
    g3: ArcOfCircle CenterX=-550 CenterY=-150 CenterZ=0 NormalX=0 NormalY=0 NormalZ=1 AngleXU=0 Radius=49.9999 StartAngle=3.14159 EndAngle=4.71239
    g4: LineSegment StartX=-550 StartY=-225 StartZ=0 EndX=550 EndY=-225 EndZ=0
    g5: LineSegment StartX=-625 StartY=-150 StartZ=0 EndX=-625 EndY=100 EndZ=0
    g6: LineSegment StartX=-625 StartY=100 StartZ=0 EndX=-600 EndY=100 EndZ=0
    g7: LineSegment StartX=-600 StartY=100 StartZ=0 EndX=-600 EndY=-150 EndZ=0
    g8: LineSegment StartX=625 StartY=-150 StartZ=0 EndX=625 EndY=100 EndZ=0
    g9: LineSegment StartX=625 StartY=100 StartZ=0 EndX=600 EndY=100 EndZ=0
    g10: LineSegment StartX=600 StartY=100 StartZ=0 EndX=600 EndY=-150 EndZ=0
    g11: LineSegment StartX=-550 StartY=-200 StartZ=0 EndX=550 EndY=-200 EndZ=0
  constraints (31):
    c: Coincident(g1,g-4)
    c: Coincident(g2,g1)
    c: Coincident(g3,g0)
    c: Coincident(g3,g-6)
    c: Coincident(g4,g0)
    c: Horizontal(g4)
    c: Vertical(g5)
    c: PointOnObject(g6,g-6)
    c: Horizontal(g6)
    c: Coincident(g7,g6)
    c: Coincident(g7,g3)
    c: Coincident(g8,g2)
    c: Vertical(g8)
    c: Coincident(g9,g8)
    c: PointOnObject(g9,g-3)
    c: Horizontal(g9)
    c: Coincident(g10,g9)
    c: Coincident(g1,g-4)
    c: Coincident(g11,g1)
    c: Horizontal(g11)
    c: DistanceX(g6,g6) = 25
    c: Coincident(g5,g6)
    c: Equal(g9,g6)
    c: DistanceY(g6,g-6) = 50
    c: Equal(g5,g8)
    c: Tangent(g0,g4,g0) = -1.5708
    c: Tangent(g4,g2) = -1.5708
    c: Tangent(g10,g1) = 1.5708
    c: DistanceY(g9,g-3) = 50
    c: Tangent(g5,g0) = 1.5708
    c: Tangent(g11,g3) = -1.5708
FEATURE [PartDesign::Pad] Pad002
  Direction = (0,0,1)
  Length = 50
  Length2 = 10
  Midplane = true
  Profile = -> Sketch002
  ReferenceAxis = -> Sketch002 [N_Axis]
  Refine = true
  Suppressed = false
  Type = 0
FEATURE [PartDesign::Body] Body001
  AllowCompound = false
  Group = -> [DatumPlane,CopyPad001,Sketch002,Pad002]
  Origin = -> Origin001
  Placement = pos=(0,0,-150) rot=(0,0,1;0rad)
  Tip = -> Pad002
FEATURE [Part::FeaturePython] Array  # Draft array (typed FeaturePython)
  AlwaysSyncPlacement = false
  Angle = 360
  ArrayType = 0
  Axis = (0,0,1)
  Base = -> Body001
  Center = (0,0,0)
  Count = 2
  ExpandArray = false
  Fuse = false
  IntervalAxis = (0,0,0)
  IntervalX = (100,0,0)
  IntervalY = (0,100,0)
  IntervalZ = (0,0,-350)
  NumberCircles = 3
  NumberPolar = 5
  NumberX = 1
  NumberY = 1
  NumberZ = 2
  PlacementList = 2 placements: [(0,0,-150),(0,0,-500)]
  RadialDistance = 50
  ScaleList = (2) [(1,1,1),(1,1,1)]
  Symmetry = 1
  TangentialDistance = 25
FEATURE [App::Part] Part  label="furniture1"
  Group = -> [Body,Array]
  Origin = -> Origin002
  Placement = pos=(0,0,0) rot=(1,0,0;1.5708rad)
FEATURE [App::Part] Part001  label="furniture2"
  Group = -> [Part]
  Origin = -> Origin003
  Placement = pos=(0,0,225) rot=(0,0,1;0rad)
FEATURE [App::Part] Part002  label="furniture3"
  Group = -> [Part001]
  Origin = -> Origin004
  Placement = pos=(0,0,225) rot=(0,0,1;0rad)
FEATURE [Assembly::JointGroup] Joints
FEATURE [Assembly::JointGroup] Joints001
FEATURE [App::Link] Body002
  LinkPlacement = pos=(0,0,225) rot=(1,0,0;1.5708rad)
  LinkedObject = -> Body
  Placement = pos=(0,0,225) rot=(1,0,0;1.5708rad)
FEATURE [Assembly::AssemblyObject] Assembly  label="body_a"
  Group = -> [Joints,Body002]
  Origin = -> Origin005
  Placement = pos=(0,0,225) rot=(0,0,1;0rad)
  Type = Assembly
FEATURE [App::Link] Array001
  LinkPlacement = pos=(0,0,225) rot=(1,0,0;1.5708rad)
  LinkedObject = -> Array
  Placement = pos=(0,0,225) rot=(1,0,0;1.5708rad)
FEATURE [Assembly::AssemblyObject] Assembly001  label="stand_a"
  Group = -> [Joints001,Array001]
  Origin = -> Origin006
  Placement = pos=(0,0,225) rot=(0,0,1;0rad)
  Type = Assembly
FEATURE [Part::FeaturePython] Clone  label="body_clone"  # Draft clone (typed FeaturePython)
  AttacherType = Attacher::AttachEngine3D
  Fuse = false
  Objects = -> [Assembly]
  Scale = (1,1,1)
FEATURE [Part::FeaturePython] Clone001  label="stand_clone"  # Draft clone (typed FeaturePython)
  AttacherType = Attacher::AttachEngine3D
  Fuse = false
  Objects = -> [Assembly001]
  Scale = (1,1,1)
FEATURE [App::Part] Part003  label="furniture"
  Group = -> [Clone,Clone001]
  Origin = -> Origin007
---- part ../moniter/moniter.FCStd = doc fcstd_a52a240c2762 ----
FCSTD DOCUMENT  (FreeCAD 1.0R39109 (Git))
Label: moniter
License: All rights reserved
LicenseURL: https://en.wikipedia.org/wiki/All_rights_reserved
objects: Sketcher::SketchObject×8, PartDesign::Pad×6, PartDesign::Body×3, PartDesign::Fillet×2, PartDesign::Pocket×2, PartDesign::ShapeBinder×2, Part::FeaturePython×2, Part::Fuse×1, App::Part×1
note: 54 computed .brp shape members not serialized (recipe doc carries the construction recipe); baked Part::Feature solids carry a one-line shape summary decoded from their .brp

FEATURE [Sketcher::SketchObject] Sketch
  ArcFitTolerance = 1e-06
  AttachmentSupport = -> [XY_Plane]
  FullyConstrained = false
  MakeInternals = false
  MapMode = 5
  sketch-geometry (17):
    g0: LineSegment StartX=-47.8454 StartY=29.1131 StartZ=0 EndX=47.8454 EndY=29.1131 EndZ=0
    g1: LineSegment StartX=61.011 StartY=51.3954 StartZ=0 EndX=40.1625 EndY=89.247 EndZ=0
    g2: LineSegment StartX=17.5666 StartY=102.598 StartZ=0 EndX=-17.5666 EndY=102.598 EndZ=0
    g3: LineSegment StartX=-40.1625 StartY=89.247 StartZ=0 EndX=-61.011 EndY=51.3954 EndZ=0
    g4: GeomPoint [constr] X=0 Y=0 Z=0
    g5: ArcOfCircle CenterX=-17.5666 CenterY=76.8013 CenterZ=0 NormalX=0 NormalY=0 NormalZ=1 AngleXU=0 Radius=25.7967 StartAngle=1.5708 EndAngle=2.63814
    g6: GeomPoint [constr] X=-32.8089 Y=102.598 Z=0
    g7: ArcOfCircle CenterX=17.5666 CenterY=76.8013 CenterZ=0 NormalX=0 NormalY=0 NormalZ=1 AngleXU=0 Radius=25.7967 StartAngle=0.503453 EndAngle=1.5708
    g8: GeomPoint [constr] X=32.8089 Y=102.598 Z=0
    g9: ArcOfCircle CenterX=47.8454 CenterY=44.1438 CenterZ=0 NormalX=0 NormalY=0 NormalZ=1 AngleXU=0 Radius=15.0306 StartAngle=4.71239 EndAngle=6.78664
    g10: GeomPoint [constr] X=73.284 Y=29.1131 Z=0
    g11: ArcOfCircle CenterX=-47.8454 CenterY=44.1438 CenterZ=0 NormalX=0 NormalY=0 NormalZ=1 AngleXU=0 Radius=15.0306 StartAngle=2.63814 EndAngle=4.71239
    g12: GeomPoint [constr] X=-73.284 Y=29.1131 Z=0
    g13: LineSegment [constr] StartX=-17.5666 StartY=76.8013 StartZ=0 EndX=47.8454 EndY=44.1438 EndZ=0
    g14: LineSegment [constr] StartX=17.5666 StartY=76.8013 StartZ=0 EndX=-47.8454 EndY=44.1438 EndZ=0
    g15: LineSegment [constr] StartX=17.5666 StartY=76.8013 StartZ=0 EndX=47.8454 EndY=44.1438 EndZ=0
    g16: LineSegment [constr] StartX=-17.5666 StartY=76.8013 StartZ=0 EndX=-47.8454 EndY=44.1438 EndZ=0
  constraints (30):
    c: Horizontal(g0)
    c: Horizontal(g2)
    c: Coincident(g4,g-1)
    c: PointOnObject(g6,g2)
    c: PointOnObject(g6,g3)
    c: Tangent(g2,g5) = -1.5708
    c: Tangent(g3,g5) = -1.5708
    c: PointOnObject(g8,g2)
    c: PointOnObject(g8,g1)
    c: Tangent(g2,g7) = -1.5708
    c: Tangent(g1,g7) = -1.5708
    c: PointOnObject(g10,g1)
    c: PointOnObject(g10,g0)
    c: Tangent(g1,g9) = -1.5708
    c: Tangent(g0,g9) = -1.5708
    c: PointOnObject(g12,g3)
    c: PointOnObject(g12,g0)
    c: Tangent(g3,g11) = -1.5708
    c: Tangent(g0,g11) = -1.5708
    c: Equal(g11,g9)
    c: Coincident(g13,g5)
    c: Coincident(g13,g9)
    c: Coincident(g14,g7)
    c: Coincident(g14,g11)
    c: Equal(g14,g13)
    c: Symmetric(g7,g5,g-2)
    c: Coincident(g15,g7)
    c: Coincident(g15,g9)
    c: Coincident(g16,g5)
    c: Coincident(g16,g11)
FEATURE [PartDesign::Pad] Pad
  Direction = (0,0,1)
  Length = 10
  Length2 = 10
  Profile = -> Sketch
  ReferenceAxis = -> Sketch [N_Axis]
  Refine = true
  Suppressed = false
  Type = 0
FEATURE [Sketcher::SketchObject] Sketch001
  ArcFitTolerance = 1e-06
  AttachmentSupport = -> [Pad]
  FullyConstrained = false
  MakeInternals = false
  MapMode = 5
  Placement = pos=(0,0,10) rot=(0,0,1;0rad)
  sketch-geometry (10):
    g0: LineSegment StartX=-30.568 StartY=79.6606 StartZ=0 EndX=-30.568 EndY=73.3721 EndZ=0
    g1: LineSegment StartX=-20.568 StartY=63.3721 StartZ=0 EndX=20.568 EndY=63.3721 EndZ=0
    g2: LineSegment StartX=30.568 StartY=73.3721 StartZ=0 EndX=30.568 EndY=79.6619 EndZ=0
    g3: ArcOfCircle CenterX=0.00125496 CenterY=43.2656 CenterZ=0 NormalX=0 NormalY=0 NormalZ=1 AngleXU=0 Radius=52.8585 StartAngle=1.09908 EndAngle=2.04258
    g4: ArcOfCircle CenterX=-18.568 CenterY=79.6606 CenterZ=0 NormalX=0 NormalY=0 NormalZ=1 AngleXU=0 Radius=12 StartAngle=2.04258 EndAngle=3.14159
    g5: ArcOfCircle CenterX=18.568 CenterY=79.6619 CenterZ=0 NormalX=0 NormalY=0 NormalZ=1 AngleXU=0 Radius=12 StartAngle=1e-16 EndAngle=1.09908
    g6: ArcOfCircle CenterX=20.568 CenterY=73.3721 CenterZ=0 NormalX=0 NormalY=0 NormalZ=1 AngleXU=0 Radius=10 StartAngle=4.71239 EndAngle=6.28319
    g7: GeomPoint [constr] X=30.568 Y=63.3721 Z=0
    g8: ArcOfCircle CenterX=-20.568 CenterY=73.3721 CenterZ=0 NormalX=0 NormalY=0 NormalZ=1 AngleXU=0 Radius=10 StartAngle=3.14159 EndAngle=4.71239
    g9: GeomPoint [constr] X=-30.568 Y=63.3721 Z=0
  constraints (19):
    c: Vertical(g0)
    c: Vertical(g2)
    c: Symmetric(g9,g7,g-2)
    c: Tangent(g3,g4) = -1.5708
    c: Tangent(g0,g4) = -1.5708
    c: Tangent(g3,g5) = -1.5708
    c: Tangent(g2,g5) = -1.5708
    c: PointOnObject(g7,g2)
    c: PointOnObject(g7,g1)
    c: Tangent(g2,g6) = -1.5708
    c: Tangent(g1,g6) = -1.5708
    c: PointOnObject(g9,g0)
    c: PointOnObject(g9,g1)
    c: Tangent(g0,g8) = -1.5708
    c: Tangent(g1,g8) = -1.5708
    c: Equal(g8,g6)
    c: Equal(g5,g4)
    c: Radius(g8) = 10
    c: Radius(g4) = 12
FEATURE [Sketcher::SketchObject] Sketch002
  ArcFitTolerance = 1e-06
  AttachmentSupport = -> [XZ_Plane001]
  FullyConstrained = false
  MakeInternals = false
  MapMode = 5
  Placement = pos=(0,0,0) rot=(1,0,0;1.5708rad)
  sketch-geometry (4):
    g0: LineSegment StartX=-265.2 StartY=359.744 StartZ=0 EndX=-265.2 EndY=59.7441 EndZ=0
    g1: LineSegment StartX=-265.2 StartY=59.7441 StartZ=0 EndX=265.2 EndY=59.7441 EndZ=0
    g2: LineSegment StartX=265.2 StartY=59.7441 StartZ=0 EndX=265.2 EndY=359.744 EndZ=0
    g3: LineSegment StartX=265.2 StartY=359.744 StartZ=0 EndX=-265.2 EndY=359.744 EndZ=0
  constraints (10):
    c: Coincident(g0,g1)
    c: Coincident(g1,g2)
    c: Coincident(g2,g3)
    c: Coincident(g3,g0)
    c: Vertical(g0)
    c: Vertical(g2)
    c: Horizontal(g1)
    c: Distance(g0,g2) = 530.4
    c: Distance(g1,g3) = 300
    c: Symmetric(g2,g0,g-2)
FEATURE [PartDesign::Pad] Pad002
  Direction = (0,-1,2e-16)
  Length = 30
  Length2 = 10
  Placement = pos=(0,0,0) rot=(1,0,0;1.5708rad)
  Profile = -> Sketch002
  ReferenceAxis = -> Sketch002 [N_Axis]
  Refine = true
  Reversed = true
  Suppressed = false
  TaperAngle = -20
  Type = 0
FEATURE [PartDesign::Fillet] Fillet
  Base = -> Pad002 [Edge6,Edge9,Edge4,Edge2]
  BaseFeature = -> Pad002
  Placement = pos=(0,0,0) rot=(1,0,0;1.5708rad)
  Radius = 5
  Refine = true
  SupportTransform = false
  Suppressed = false
  UseAllEdges = false
FEATURE [Sketcher::SketchObject] Sketch003
  ArcFitTolerance = 1e-06
  AttachmentSupport = -> [Fillet]
  FullyConstrained = false
  MakeInternals = false
  MapMode = 5
  Placement = pos=(0,30,-1.38e-14) rot=(-1,0,0;1.5708rad)
  sketch-geometry (4):
    g0: LineSegment StartX=190.861 StartY=-107.821 StartZ=0 EndX=190.861 EndY=-55.3481 EndZ=0
    g1: LineSegment StartX=190.861 StartY=-55.3481 StartZ=0 EndX=-190.861 EndY=-55.3481 EndZ=0
    g2: LineSegment StartX=-190.861 StartY=-55.3481 StartZ=0 EndX=-190.861 EndY=-107.821 EndZ=0
    g3: LineSegment StartX=-190.861 StartY=-107.821 StartZ=0 EndX=190.861 EndY=-107.821 EndZ=0
  constraints (8):
    c: Coincident(g0,g1)
    c: Coincident(g1,g2)
    c: Coincident(g2,g3)
    c: Coincident(g3,g0)
    c: Vertical(g0)
    c: Vertical(g2)
    c: Horizontal(g1)
    c: Symmetric(g2,g0,g-2)
FEATURE [PartDesign::Pocket] Pocket
  BaseFeature = -> Fillet
  Direction = (0,-1,-2e-16)
  Length = 20
  Length2 = 5
  Placement = pos=(0,0,0) rot=(1,0,0;1.5708rad)
  Profile = -> Sketch003
  ReferenceAxis = -> Sketch003 [N_Axis]
  Refine = true
  Suppressed = false
  Type = 0
FEATURE [Sketcher::SketchObject] Sketch004
  ArcFitTolerance = 1e-06
  AttachmentSupport = -> [Pocket]
  FullyConstrained = false
  MakeInternals = false
  MapMode = 5
  Placement = pos=(0,30,-1.38e-14) rot=(-1,0,0;1.5708rad)
  sketch-geometry (14):
    g0: LineSegment StartX=60 StartY=-228.06 StartZ=0 EndX=60 EndY=-128.06 EndZ=0
    g1: LineSegment StartX=50 StartY=-118.06 StartZ=0 EndX=-50 EndY=-118.06 EndZ=0
    g2: LineSegment StartX=-60 StartY=-128.06 StartZ=0 EndX=-60 EndY=-228.06 EndZ=0
    g3: LineSegment StartX=-50 StartY=-238.06 StartZ=0 EndX=50 EndY=-238.06 EndZ=0
    g4: ArcOfCircle CenterX=50 CenterY=-228.06 CenterZ=0 NormalX=0 NormalY=0 NormalZ=1 AngleXU=0 Radius=10 StartAngle=4.71239 EndAngle=6.28319
    g5: ArcOfCircle CenterX=50 CenterY=-128.06 CenterZ=0 NormalX=0 NormalY=0 NormalZ=1 AngleXU=0 Radius=10 StartAngle=1.1e-15 EndAngle=1.5708
    g6: ArcOfCircle CenterX=-50 CenterY=-128.06 CenterZ=0 NormalX=0 NormalY=0 NormalZ=1 AngleXU=0 Radius=10 StartAngle=1.5708 EndAngle=3.14159
    g7: ArcOfCircle CenterX=-50 CenterY=-228.06 CenterZ=0 NormalX=0 NormalY=0 NormalZ=1 AngleXU=0 Radius=10 StartAngle=3.14159 EndAngle=4.71239
    g8: GeomPoint [constr] X=60 Y=-238.06 Z=0
    g9: GeomPoint [constr] X=-60 Y=-118.06 Z=0
    g10: Circle CenterX=50 CenterY=-228.06 CenterZ=0 NormalX=0 NormalY=0 NormalZ=1 AngleXU=0 Radius=2
    g11: Circle CenterX=-50 CenterY=-228.06 CenterZ=0 NormalX=0 NormalY=0 NormalZ=1 AngleXU=0 Radius=2
    g12: Circle CenterX=50 CenterY=-128.06 CenterZ=0 NormalX=0 NormalY=0 NormalZ=1 AngleXU=0 Radius=2
    g13: Circle CenterX=-50 CenterY=-128.06 CenterZ=0 NormalX=0 NormalY=0 NormalZ=1 AngleXU=0 Radius=2
  constraints (30):
    c: Tangent(g0,g4) = -1.5708
    c: Tangent(g0,g5) = -1.5708
    c: Tangent(g1,g5) = -1.5708
    c: Tangent(g1,g6) = -1.5708
    c: Tangent(g2,g6) = -1.5708
    c: Tangent(g2,g7) = -1.5708
    c: Tangent(g3,g7) = -1.5708
    c: Tangent(g3,g4) = -1.5708
    c: Vertical(g0)
    c: Vertical(g2)
    c: Horizontal(g1)
    c: Horizontal(g3)
    c: Equal(g4,g5)
    c: Equal(g5,g6)
    c: PointOnObject(g8,g0)
    c: PointOnObject(g8,g3)
    c: PointOnObject(g9,g1)
    c: PointOnObject(g9,g2)
    c: DistanceX(g7,g4) = 100
    c: DistanceY(g7,g6) = 100
    c: Symmetric(g4,g7,g-2)
    c: Radius(g4) = 10
    c: Coincident(g10,g4)
    c: Coincident(g11,g7)
    c: Coincident(g12,g5)
    c: Coincident(g13,g6)
    c: Equal(g13,g11)
    c: Equal(g11,g10)
    c: Equal(g10,g12)
    c: Radius(g10) = 2
FEATURE [PartDesign::Pad] Pad003
  BaseFeature = -> Pocket
  Direction = (0,1,2e-16)
  Length = 2
  Length2 = 10
  Placement = pos=(0,0,0) rot=(1,0,0;1.5708rad)
  Profile = -> Sketch004
  ReferenceAxis = -> Sketch004 [N_Axis]
  Refine = true
  Suppressed = false
  Type = 0
FEATURE [PartDesign::Pad] Pad001
  BaseFeature = -> Pad
  Direction = (0,0,1)
  Length = 204
  Length2 = 10
  Profile = -> Sketch001
  ReferenceAxis = -> Sketch001 [N_Axis]
  Refine = true
  Suppressed = false
  Type = 0
FEATURE [PartDesign::ShapeBinder] CopyPad003
  Placement = pos=(0,2,4e-16) rot=(0,0,1;0rad)
  TraceSupport = false
FEATURE [Sketcher::SketchObject] Sketch005
  ArcFitTolerance = 1e-06
  AttachmentSupport = -> [CopyPad003]
  ExternalGeometry = -> [CopyPad003]
  FullyConstrained = false
  MakeInternals = false
  MapMode = 5
  Placement = pos=(0,32,7.3e-15) rot=(0,0.707107,0.707107;3.14159rad)
  sketch-geometry (12):
    g0: LineSegment [constr] StartX=-60 StartY=228.06 StartZ=0 EndX=60 EndY=128.06 EndZ=0
    g1: LineSegment [constr] StartX=60 StartY=228.06 StartZ=0 EndX=-7.1e-15 EndY=178.06 EndZ=0
    g2: LineSegment StartX=-17.106 StartY=184.304 StartZ=0 EndX=-17.106 EndY=171.815 EndZ=0
    g3: LineSegment StartX=-12.1108 StartY=166.82 StartZ=0 EndX=12.1108 EndY=166.82 EndZ=0
    g4: LineSegment StartX=17.106 StartY=171.815 StartZ=0 EndX=17.106 EndY=184.304 EndZ=0
    g5: LineSegment StartX=12.1108 StartY=189.299 StartZ=0 EndX=-12.1108 EndY=189.299 EndZ=0
    g6: ArcOfCircle CenterX=-12.1108 CenterY=184.304 CenterZ=0 NormalX=0 NormalY=0 NormalZ=1 AngleXU=0 Radius=4.99514 StartAngle=1.5708 EndAngle=3.14159
    g7: ArcOfCircle CenterX=-12.1108 CenterY=171.815 CenterZ=0 NormalX=0 NormalY=0 NormalZ=1 AngleXU=0 Radius=4.99514 StartAngle=3.14159 EndAngle=4.71239
    g8: ArcOfCircle CenterX=12.1108 CenterY=171.815 CenterZ=0 NormalX=0 NormalY=0 NormalZ=1 AngleXU=0 Radius=4.99514 StartAngle=4.71239 EndAngle=6.28319
    g9: ArcOfCircle CenterX=12.1108 CenterY=184.304 CenterZ=0 NormalX=0 NormalY=0 NormalZ=1 AngleXU=0 Radius=4.99514 StartAngle=8e-16 EndAngle=1.5708
    g10: GeomPoint [constr] X=-17.106 Y=189.299 Z=0
    g11: GeomPoint [constr] X=17.106 Y=166.82 Z=0
  constraints (23):
    c: Coincident(g0,g-4)
    c: Coincident(g0,g-5)
    c: Coincident(g1,g-4)
    c: Symmetric(g0,g0,g1)
    c: Tangent(g2,g6) = -1.5708
    c: Tangent(g2,g7) = -1.5708
    c: Tangent(g3,g7) = -1.5708
    c: Tangent(g3,g8) = -1.5708
    c: Tangent(g4,g8) = -1.5708
    c: Tangent(g4,g9) = -1.5708
    c: Tangent(g5,g9) = -1.5708
    c: Tangent(g5,g6) = -1.5708
    c: Vertical(g2)
    c: Vertical(g4)
    c: Horizontal(g3)
    c: Horizontal(g5)
    c: Equal(g7,g8)
    c: PointOnObject(g10,g2)
    c: PointOnObject(g10,g5)
    c: PointOnObject(g11,g3)
    c: PointOnObject(g11,g4)
    c: Symmetric(g9,g6,g-2)
    c: Symmetric(g9,g7,g1)
FEATURE [PartDesign::Pad] Pad004
  BaseFeature = -> Pad001
  Direction = (0,1,-2e-16)
  Length = 10
  Length2 = 10
  Profile = -> Sketch005
  ReferenceAxis = -> Sketch005 [N_Axis]
  Refine = true
  Suppressed = false
  Type = 3
  UpToFace = -> Pad001 [Face13]
FEATURE [PartDesign::Fillet] Fillet001
  Base = -> Pad004 [Edge10]
  BaseFeature = -> Pad004
  Radius = 2
  Refine = true
  SupportTransform = false
  Suppressed = false
  UseAllEdges = false
FEATURE [PartDesign::Body] Body
  AllowCompound = false
  Group = -> [Sketch,Pad,Sketch001,Pad001,CopyPad003,Sketch005,Pad004,Fillet001]
  Origin = -> Origin
  Tip = -> Fillet001
FEATURE [Sketcher::SketchObject] Sketch006
  ArcFitTolerance = 1e-06
  AttachmentSupport = -> [Pad003]
  ExternalGeometry = -> [Pad003]
  FullyConstrained = true
  MakeInternals = false
  MapMode = 5
  Placement = pos=(0,1.5e-15,0) rot=(1,0,0;1.5708rad)
  sketch-geometry (9):
    g0: LineSegment StartX=260.502 StartY=64.4426 StartZ=0 EndX=260.502 EndY=355.046 EndZ=0
    g1: LineSegment StartX=260.502 StartY=355.046 StartZ=0 EndX=-260.502 EndY=355.046 EndZ=0
    g2: LineSegment StartX=-260.502 StartY=355.046 StartZ=0 EndX=-260.502 EndY=64.4426 EndZ=0
    g3: LineSegment StartX=-260.502 StartY=64.4426 StartZ=0 EndX=260.502 EndY=64.4426 EndZ=0
    g4: GeomPoint [constr] X=0 Y=209.744 Z=0
    g5: LineSegment [constr] StartX=-260.502 StartY=359.744 StartZ=0 EndX=-260.502 EndY=355.046 EndZ=0
    g6: LineSegment [constr] StartX=260.502 StartY=64.4426 StartZ=0 EndX=260.502 EndY=59.7441 EndZ=0
    g7: LineSegment [constr] StartX=265.2 StartY=64.4426 StartZ=0 EndX=260.502 EndY=64.4426 EndZ=0
    g8: LineSegment [constr] StartX=-265.2 StartY=355.046 StartZ=0 EndX=-260.502 EndY=355.046 EndZ=0
  constraints (21):
    c: Coincident(g0,g1)
    c: Coincident(g1,g2)
    c: Coincident(g2,g3)
    c: Coincident(g3,g0)
    c: Vertical(g0)
    c: Vertical(g2)
    c: Horizontal(g1)
    c: Horizontal(g3)
    c: Symmetric(g2,g0,g4)
    c: PointOnObject(g4,g-2)
    c: Coincident(g5,g-3)
    c: Coincident(g5,g1)
    c: Coincident(g6,g0)
    c: Coincident(g6,g-6)
    c: Vertical(g6)
    c: Equal(g5,g6)
    c: Coincident(g7,g-4)
    c: Coincident(g7,g0)
    c: Coincident(g8,g-5)
    c: Coincident(g8,g1)
    c: Equal(g8,g5)
FEATURE [PartDesign::Pocket] Pocket001
  BaseFeature = -> Pad003
  Direction = (0,1,-2e-16)
  Length = 5
  Length2 = 5
  Placement = pos=(0,0,0) rot=(1,0,0;1.5708rad)
  Profile = -> Sketch006
  ReferenceAxis = -> Sketch006 [N_Axis]
  Refine = true
  Suppressed = false
  Type = 0
FEATURE [PartDesign::Body] Body001
  AllowCompound = false
  Group = -> [Sketch002,Pad002,Fillet,Sketch003,Pocket,Sketch004,Pad003,Sketch006,Pocket001]
  Origin = -> Origin001
  Tip = -> Pocket001
FEATURE [Part::Fuse] Fusion  label="moniter_body"
  Base = -> Body
  Refine = true
  Tool = -> Body001
FEATURE [PartDesign::ShapeBinder] CopyPocket001
  Placement = pos=(0,5,-2e-15) rot=(0,0,1;0rad)
  TraceSupport = false
FEATURE [Sketcher::SketchObject] Sketch007
  ArcFitTolerance = 1e-06
  AttachmentSupport = -> [CopyPocket001]
  ExternalGeometry = -> [CopyPocket001]
  FullyConstrained = true
  MakeInternals = false
  MapMode = 5
  Placement = pos=(0,5,-2e-15) rot=(1,0,0;1.5708rad)
  sketch-geometry (4):
    g0: LineSegment StartX=-260.502 StartY=355.046 StartZ=0 EndX=-260.502 EndY=64.4426 EndZ=0
    g1: LineSegment StartX=-260.502 StartY=64.4426 StartZ=0 EndX=260.502 EndY=64.4426 EndZ=0
    g2: LineSegment StartX=260.502 StartY=64.4426 StartZ=0 EndX=260.502 EndY=355.046 EndZ=0
    g3: LineSegment StartX=260.502 StartY=355.046 StartZ=0 EndX=-260.502 EndY=355.046 EndZ=0
  constraints (10):
    c: Coincident(g0,g1)
    c: Coincident(g1,g2)
    c: Coincident(g2,g3)
    c: Coincident(g3,g0)
    c: Vertical(g0)
    c: Vertical(g2)
    c: Horizontal(g1)
    c: Horizontal(g3)
    c: Coincident(g0,g-3)
    c: Coincident(g1,g-4)
FEATURE [PartDesign::Pad] Pad005
  Direction = (0,-1,2e-16)
  Length = 1
  Length2 = 10
  Placement = pos=(0,5,-2e-15) rot=(0,0,1;0rad)
  Profile = -> Sketch007
  ReferenceAxis = -> Sketch007 [N_Axis]
  Refine = true
  Suppressed = false
  Type = 0
FEATURE [PartDesign::Body] Body002  label="moniter_screen"
  AllowCompound = false
  Group = -> [CopyPocket001,Sketch007,Pad005]
  Origin = -> Origin002
  Tip = -> Pad005
FEATURE [Part::FeaturePython] Clone  label="moniter_body_clone"  # Draft clone (typed FeaturePython)
  AttacherType = Attacher::AttachEngine3D
  Fuse = false
  Objects = -> [Fusion]
  Scale = (1,1,1)
FEATURE [Part::FeaturePython] Clone001  label="moniter_screen_clone"  # Draft clone (typed FeaturePython)
  AttacherType = Attacher::AttachEngine3D
  Fuse = false
  Objects = -> [Body002]
  Scale = (1,1,1)
FEATURE [App::Part] Part  label="moniter"
  Group = -> [Clone,Clone001]
  Origin = -> Origin004
---- part ../pylon/pylon.FCStd = doc fcstd_9ce646337770 ----
FCSTD DOCUMENT  (FreeCAD 1.0R39109 (Git))
Label: pylon
License: All rights reserved
LicenseURL: https://en.wikipedia.org/wiki/All_rights_reserved
objects: Sketcher::SketchObject×2, App::Part×2, PartDesign::Pad×1, PartDesign::Revolution×1, PartDesign::Fillet×1, PartDesign::Thickness×1, PartDesign::Body×1, Part::FeaturePython×1
note: 18 computed .brp shape members not serialized (recipe doc carries the construction recipe); baked Part::Feature solids carry a one-line shape summary decoded from their .brp

FEATURE [Sketcher::SketchObject] Sketch
  ArcFitTolerance = 1e-06
  AttachmentSupport = -> [XY_Plane]
  FullyConstrained = true
  MakeInternals = false
  MapMode = 5
  sketch-geometry (4):
    g0: LineSegment StartX=-125 StartY=125 StartZ=0 EndX=-125 EndY=-125 EndZ=0
    g1: LineSegment StartX=-125 StartY=-125 StartZ=0 EndX=125 EndY=-125 EndZ=0
    g2: LineSegment StartX=125 StartY=-125 StartZ=0 EndX=125 EndY=125 EndZ=0
    g3: LineSegment StartX=125 StartY=125 StartZ=0 EndX=-125 EndY=125 EndZ=0
  constraints (11):
    c: Coincident(g0,g1)
    c: Coincident(g1,g2)
    c: Coincident(g2,g3)
    c: Coincident(g3,g0)
    c: Vertical(g0)
    c: Vertical(g2)
    c: Horizontal(g1)
    c: Horizontal(g3)
    c: Symmetric(g0,g1,g-1)
    c: DistanceX(g3,g3) = 250
    c: Equal(g3,g0)
FEATURE [PartDesign::Pad] Pad
  Direction = (0,0,1)
  Length = 10
  Length2 = 10
  Profile = -> Sketch
  ReferenceAxis = -> Sketch [N_Axis]
  Refine = true
  Reversed = true
  Suppressed = false
  Type = 0
FEATURE [Sketcher::SketchObject] Sketch001
  ArcFitTolerance = 1e-06
  AttachmentSupport = -> [XZ_Plane]
  FullyConstrained = true
  MakeInternals = false
  MapMode = 5
  Placement = pos=(0,0,0) rot=(1,0,0;1.5708rad)
  sketch-geometry (13):
    g0: LineSegment StartX=115 StartY=0 StartZ=0 EndX=0 EndY=0 EndZ=0
    g1: LineSegment StartX=0 StartY=0 StartZ=0 EndX=0 EndY=500 EndZ=0
    g2: LineSegment StartX=0 StartY=500 StartZ=0 EndX=20 EndY=500 EndZ=0
    g3: LineSegment StartX=20 StartY=500 StartZ=0 EndX=33 EndY=405 EndZ=0
    g4: LineSegment StartX=33 StartY=405 StartZ=0 EndX=32.9009 EndY=404.986 EndZ=0
    g5: LineSegment StartX=32.9009 StartY=404.986 StartZ=0 EndX=45.9009 EndY=309.986 EndZ=0
    g6: LineSegment StartX=45.9009 StartY=309.986 StartZ=0 EndX=46 EndY=310 EndZ=0
    g7: LineSegment StartX=46 StartY=310 StartZ=0 EndX=59 EndY=215 EndZ=0
    g8: LineSegment StartX=59 StartY=215 StartZ=0 EndX=58.9009 EndY=214.986 EndZ=0
    g9: LineSegment StartX=58.9009 StartY=214.986 StartZ=0 EndX=71.9009 EndY=119.986 EndZ=0
    g10: LineSegment StartX=71.9009 StartY=119.986 StartZ=0 EndX=72 EndY=120 EndZ=0
    g11: LineSegment StartX=72 StartY=120 StartZ=0 EndX=85 EndY=25 EndZ=0
    g12: LineSegment StartX=85 StartY=25 StartZ=0 EndX=115 EndY=0 EndZ=0
  constraints (38):
    c: PointOnObject(g0,g-1)
    c: Coincident(g0,g-1)
    c: Coincident(g0,g1)
    c: Vertical(g1)
    c: Coincident(g1,g2)
    c: Coincident(g2,g3)
    c: Coincident(g3,g4)
    c: Coincident(g4,g5)
    c: Coincident(g5,g6)
    c: Coincident(g6,g7)
    c: Coincident(g7,g8)
    c: Coincident(g8,g9)
    c: Coincident(g9,g10)
    c: Coincident(g10,g11)
    c: Equal(g3,g5)
    c: Equal(g5,g7)
    c: Equal(g7,g9)
    c: Perpendicular(g4,g3)
    c: Perpendicular(g7,g6)
    c: Perpendicular(g6,g5)
    c: Perpendicular(g5,g4)
    c: Perpendicular(g9,g8)
    c: Perpendicular(g8,g7)
    c: Perpendicular(g9,g10)
    c: Perpendicular(g10,g11)
    c: Horizontal(g2)
    c: Equal(g4,g6)
    c: Equal(g6,g8)
    c: Equal(g8,g10)
    c: DistanceX(g0,g0) = 115
    c: DistanceY(g1,g1) = 500
    c: Distance(g6) = 0.1
    c: DistanceX(g2,g2) = 20
    c: Coincident(g12,g11)
    c: Coincident(g12,g0)
    c: DistanceY(g11) = 25
    c: DistanceX(g12,g12) = 30
    c: Equal(g9,g11)
FEATURE [PartDesign::Revolution] Revolution
  Angle = 360
  Angle2 = 60
  Axis = (0,2e-16,1)
  Base = (0,0,0)
  BaseFeature = -> Pad
  Profile = -> Sketch001
  ReferenceAxis = -> Sketch001 [V_Axis]
  Refine = true
  Reversed = true
  Suppressed = false
  Type = 0
FEATURE [PartDesign::Fillet] Fillet
  Base = -> Revolution [Edge26,Edge29,Edge31,Edge27]
  BaseFeature = -> Revolution
  Radius = 25
  Refine = true
  SupportTransform = false
  Suppressed = false
  UseAllEdges = false
FEATURE [PartDesign::Thickness] Thickness
  Base = -> Fillet [Face11,Face21]
  BaseFeature = -> Fillet
  Intersection = false
  Join = 1
  Mode = 0
  Refine = true
  Reversed = true
  SupportTransform = false
  Suppressed = false
  Value = 3
FEATURE [PartDesign::Body] Body
  AllowCompound = false
  Group = -> [Sketch,Pad,Sketch001,Revolution,Fillet,Thickness]
  Origin = -> Origin
  Placement = pos=(0,0,10) rot=(0,0,1;0rad)
  Tip = -> Thickness
FEATURE [App::Part] Part
  Group = -> [Body]
  Origin = -> Origin001
  Placement = pos=(0,0,10) rot=(0,0,1;0rad)
FEATURE [Part::FeaturePython] Clone  label="pylon_clone"  # Draft clone (typed FeaturePython)
  AttacherType = Attacher::AttachEngine3D
  Fuse = false
  Objects = -> [Part]
  Scale = (1,1,1)
FEATURE [App::Part] Part001  label="pylon"
  Group = -> [Clone]
  Origin = -> Origin002
---- part ../refrigerator/refrigerator.FCStd = doc fcstd_40720735dab3 ----
FCSTD DOCUMENT  (FreeCAD 1.0R39109 (Git))
Label: refrigerator
License: All rights reserved
LicenseURL: https://en.wikipedia.org/wiki/All_rights_reserved
objects: Sketcher::SketchObject×4, PartDesign::Pad×4, PartDesign::Body×1, Part::FeaturePython×1, App::Part×1
note: 22 computed .brp shape members not serialized (recipe doc carries the construction recipe); baked Part::Feature solids carry a one-line shape summary decoded from their .brp

FEATURE [Sketcher::SketchObject] Sketch
  ArcFitTolerance = 1e-06
  AttachmentSupport = -> [XY_Plane]
  FullyConstrained = true
  MakeInternals = false
  MapMode = 5
  sketch-geometry (5):
    g0: LineSegment StartX=-370 StartY=-364.5 StartZ=0 EndX=370 EndY=-364.5 EndZ=0
    g1: LineSegment StartX=370 StartY=-364.5 StartZ=0 EndX=370 EndY=364.5 EndZ=0
    g2: LineSegment StartX=370 StartY=364.5 StartZ=0 EndX=-370 EndY=364.5 EndZ=0
    g3: LineSegment StartX=-370 StartY=364.5 StartZ=0 EndX=-370 EndY=-364.5 EndZ=0
    g4: GeomPoint [constr] X=0 Y=0 Z=0
  constraints (12):
    c: Coincident(g0,g1)
    c: Coincident(g1,g2)
    c: Coincident(g2,g3)
    c: Coincident(g3,g0)
    c: Horizontal(g0)
    c: Horizontal(g2)
    c: Vertical(g1)
    c: Vertical(g3)
    c: Symmetric(g2,g0,g4)
    c: Distance(g1,g3) = 740
    c: Distance(g0,g2) = 729
    c: Coincident(g4,g-1)
FEATURE [PartDesign::Pad] Pad
  Direction = (0,0,1)
  Length = 1818
  Length2 = 10
  Profile = -> Sketch
  ReferenceAxis = -> Sketch [N_Axis]
  Refine = true
  Suppressed = false
  Type = 0
FEATURE [Sketcher::SketchObject] Sketch001
  ArcFitTolerance = 1e-06
  AttachmentSupport = -> [Pad]
  ExternalGeometry = -> [Pad]
  FullyConstrained = true
  MakeInternals = false
  MapMode = 5
  Placement = pos=(0,-364.5,0) rot=(1,0,0;1.5708rad)
  sketch-geometry (10):
    g0: LineSegment [constr] StartX=370 StartY=1818 StartZ=0 EndX=370 EndY=1813 EndZ=0
    g1: LineSegment [constr] StartX=370 StartY=1818 StartZ=0 EndX=365 EndY=1818 EndZ=0
    g2: LineSegment [constr] StartX=-370 StartY=0 StartZ=0 EndX=-370 EndY=5 EndZ=0
    g3: LineSegment [constr] StartX=-370 StartY=0 StartZ=0 EndX=-365 EndY=0 EndZ=0
    g4: LineSegment [constr] StartX=-370 StartY=5 StartZ=0 EndX=-365 EndY=5 EndZ=0
    g5: LineSegment [constr] StartX=370 StartY=1813 StartZ=0 EndX=365 EndY=1813 EndZ=0
    g6: LineSegment StartX=365 StartY=1813 StartZ=0 EndX=-365 EndY=1813 EndZ=0
    g7: LineSegment StartX=-365 StartY=1813 StartZ=0 EndX=-365 EndY=5 EndZ=0
    g8: LineSegment StartX=-365 StartY=5 StartZ=0 EndX=365 EndY=5 EndZ=0
    g9: LineSegment StartX=365 StartY=5 StartZ=0 EndX=365 EndY=1813 EndZ=0
  constraints (28):
    c: Distance(g0) = 5
    c: Coincident(g0,g-4)
    c: PointOnObject(g0,g-3)
    c: Distance(g1) = 5
    c: Coincident(g1,g0)
    c: PointOnObject(g1,g-4)
    c: Distance(g2) = 5
    c: Coincident(g2,g-5)
    c: PointOnObject(g2,g-5)
    c: Distance(g3) = 5
    c: Coincident(g3,g2)
    c: PointOnObject(g3,g-1)
    c: Distance(g4) = 5
    c: Coincident(g4,g2)
    c: Horizontal(g4)
    c: Distance(g5) = 5
    c: Coincident(g5,g0)
    c: Horizontal(g5)
    c: Coincident(g6,g7)
    c: Coincident(g7,g8)
    c: Coincident(g8,g9)
    c: Coincident(g9,g6)
    c: Horizontal(g6)
    c: Horizontal(g8)
    c: Vertical(g7)
    c: Vertical(g9)
    c: Coincident(g6,g5)
    c: Coincident(g7,g4)
FEATURE [PartDesign::Pad] Pad001
  BaseFeature = -> Pad
  Direction = (0,-1,2e-16)
  Length = 1
  Length2 = 10
  Profile = -> Sketch001
  ReferenceAxis = -> Sketch001 [N_Axis]
  Refine = true
  Suppressed = false
  Type = 0
FEATURE [Sketcher::SketchObject] Sketch002
  ArcFitTolerance = 1e-06
  AttachmentSupport = -> [Pad001]
  ExternalGeometry = -> [Pad001]
  FullyConstrained = false
  MakeInternals = false
  MapMode = 5
  Placement = pos=(0,-365.5,0) rot=(1,0,0;1.5708rad)
  sketch-geometry (8):
    g0: LineSegment StartX=-370 StartY=1818 StartZ=0 EndX=-370 EndY=909 EndZ=0
    g1: LineSegment StartX=370 StartY=909 StartZ=0 EndX=370 EndY=1818 EndZ=0
    g2: LineSegment StartX=370 StartY=1818 StartZ=0 EndX=-65.0129 EndY=1818 EndZ=0
    g3: LineSegment StartX=-70.0129 StartY=1818 StartZ=0 EndX=-70.0129 EndY=909 EndZ=0
    g4: LineSegment StartX=-65.0129 StartY=1818 StartZ=0 EndX=-65.0129 EndY=909 EndZ=0
    g5: LineSegment StartX=-70.0129 StartY=1818 StartZ=0 EndX=-370 EndY=1818 EndZ=0
    g6: LineSegment StartX=-70.0129 StartY=909 StartZ=0 EndX=-370 EndY=909 EndZ=0
    g7: LineSegment StartX=-65.0129 StartY=909 StartZ=0 EndX=370 EndY=909 EndZ=0
  constraints (17):
    c: Coincident(g1,g2)
    c: Coincident(g5,g0)
    c: Vertical(g0)
    c: Vertical(g1)
    c: Horizontal(g2)
    c: Coincident(g0,g-4)
    c: Vertical(g3)
    c: PointOnObject(g3,g5)
    c: Vertical(g4)
    c: Coincident(g2,g4)
    c: PointOnObject(g5,g3)
    c: Coincident(g6,g3)
    c: Coincident(g6,g0)
    c: Horizontal(g6)
    c: Coincident(g7,g4)
    c: Coincident(g7,g1)
    c: Horizontal(g7)
FEATURE [PartDesign::Pad] Pad002
  BaseFeature = -> Pad001
  Direction = (0,-1,2e-16)
  Length = 20
  Length2 = 10
  Profile = -> Sketch002
  ReferenceAxis = -> Sketch002 [N_Axis]
  Refine = true
  Suppressed = false
  Type = 0
FEATURE [Sketcher::SketchObject] Sketch003
  ArcFitTolerance = 1e-06
  AttachmentSupport = -> [Pad002]
  ExternalGeometry = -> [Pad002]
  FullyConstrained = false
  MakeInternals = false
  MapMode = 5
  Placement = pos=(0,-385.5,0) rot=(1,0,0;1.5708rad)
  sketch-geometry (19):
    g0: LineSegment StartX=-370 StartY=904.002 StartZ=0 EndX=-70 EndY=904.002 EndZ=0
    g1: LineSegment StartX=-65 StartY=904.002 StartZ=0 EndX=370 EndY=904.002 EndZ=0
    g2: LineSegment [constr] StartX=-70 StartY=904.002 StartZ=0 EndX=-65 EndY=904.002 EndZ=0
    g3: LineSegment StartX=-70 StartY=904.002 StartZ=0 EndX=-70 EndY=759.002 EndZ=0
    g4: LineSegment StartX=-70 StartY=759.002 StartZ=0 EndX=-370 EndY=759.002 EndZ=0
    g5: LineSegment StartX=-370 StartY=904.002 StartZ=0 EndX=-370 EndY=759.002 EndZ=0
    g6: LineSegment StartX=-65 StartY=904.002 StartZ=0 EndX=-65 EndY=759.002 EndZ=0
    g7: LineSegment StartX=370 StartY=904.002 StartZ=0 EndX=370 EndY=759.002 EndZ=0
    g8: LineSegment StartX=370 StartY=759.002 StartZ=0 EndX=-65 EndY=759.002 EndZ=0
    g9: LineSegment [constr] StartX=-370 StartY=759.002 StartZ=0 EndX=-370 EndY=754.002 EndZ=0
    g10: LineSegment StartX=-370 StartY=754.002 StartZ=0 EndX=-370 EndY=379.002 EndZ=0
    g11: LineSegment StartX=-370 StartY=379.002 StartZ=0 EndX=370 EndY=379.002 EndZ=0
    g12: LineSegment StartX=370 StartY=379.002 StartZ=0 EndX=370 EndY=754.002 EndZ=0
    g13: LineSegment StartX=370 StartY=754.002 StartZ=0 EndX=-370 EndY=754.002 EndZ=0
    g14: LineSegment [constr] StartX=-370 StartY=379.002 StartZ=0 EndX=-370 EndY=374.002 EndZ=0
    g15: LineSegment StartX=-370 StartY=374.002 StartZ=0 EndX=-370 EndY=0 EndZ=0
    g16: LineSegment StartX=-370 StartY=0 StartZ=0 EndX=370 EndY=0 EndZ=0
    g17: LineSegment StartX=370 StartY=0 StartZ=0 EndX=370 EndY=374.002 EndZ=0
    g18: LineSegment StartX=370 StartY=374.002 StartZ=0 EndX=-370 EndY=374.002 EndZ=0
  constraints (50):
    c: Horizontal(g0)
    c: Horizontal(g1)
    c: Distance(g2) = 5
    c: Coincident(g2,g0)
    c: Coincident(g2,g1)
    c: Horizontal(g2)
    c: DistanceX(g0,g0) = 300
    c: Distance(g3) = 145
    c: Coincident(g3,g0)
    c: Vertical(g3)
    c: Coincident(g4,g3)
    c: Horizontal(g4)
    c: Vertical(g5)
    c: Coincident(g4,g5)
    c: Distance(g6) = 145
    c: Coincident(g6,g1)
    c: Vertical(g6)
    c: Distance(g7) = 145
    c: Coincident(g7,g1)
    c: Vertical(g7)
    c: Coincident(g8,g7)
    c: Coincident(g8,g6)
    c: Distance(g9) = 5
    c: Coincident(g9,g4)
    c: Vertical(g9)
    c: Coincident(g10,g11)
    c: Coincident(g11,g12)
    c: Coincident(g12,g13)
    c: Coincident(g13,g10)
    c: Vertical(g10)
    c: Vertical(g12)
    c: Horizontal(g11)
    c: Horizontal(g13)
    c: Distance(g10,g12) = 740
    c: Distance(g11,g13) = 375
    c: Coincident(g10,g9)
    c: Coincident(g5,g0)
    c: Distance(g14) = 5
    c: Coincident(g14,g10)
    c: Vertical(g14)
    c: Coincident(g15,g16)
    c: Coincident(g16,g17)
    c: Coincident(g17,g18)
    c: Coincident(g18,g15)
    c: Vertical(g15)
    c: Vertical(g17)
    c: Horizontal(g16)
    c: Horizontal(g18)
    c: Coincident(g15,g14)
    c: Coincident(g16,g-7)
FEATURE [PartDesign::Pad] Pad003
  BaseFeature = -> Pad002
  Direction = (0,-1,2e-16)
  Length = 20
  Length2 = 10
  Profile = -> Sketch003
  ReferenceAxis = -> Sketch003 [N_Axis]
  Refine = true
  Reversed = true
  Suppressed = false
  Type = 0
FEATURE [PartDesign::Body] Body
  AllowCompound = false
  Group = -> [Sketch,Pad,Sketch001,Pad001,Sketch002,Pad002,Sketch003,Pad003]
  Origin = -> Origin
  Tip = -> Pad003
FEATURE [Part::FeaturePython] Clone  label="refrigerator_clone"  # Draft clone (typed FeaturePython)
  AttacherType = Attacher::AttachEngine3D
  Fuse = false
  Objects = -> [Body]
  Scale = (1,1,1)
FEATURE [App::Part] Part  label="refrigerator"
  Group = -> [Clone]
  Origin = -> Origin001
---- part ../room/room.FCStd = doc fcstd_4090f42d3940 ----
FCSTD DOCUMENT  (FreeCAD 1.0R39109 (Git))
Label: room
License: All rights reserved
LicenseURL: https://en.wikipedia.org/wiki/All_rights_reserved
objects: Sketcher::SketchObject×3, Part::FeaturePython×3, App::GeometryPython×2, App::Part×1
note: 11 computed .brp shape members not serialized (recipe doc carries the construction recipe); baked Part::Feature solids carry a one-line shape summary decoded from their .brp

FEATURE [Sketcher::SketchObject] Sketch
  ArcFitTolerance = 1e-06
  FullyConstrained = true
  MakeInternals = false
  sketch-geometry (5):
    g0: LineSegment StartX=-2600 StartY=-2600 StartZ=0 EndX=2600 EndY=-2600 EndZ=0
    g1: LineSegment StartX=2600 StartY=-2600 StartZ=0 EndX=2600 EndY=2600 EndZ=0
    g2: LineSegment StartX=2600 StartY=2600 StartZ=0 EndX=-2600 EndY=2600 EndZ=0
    g3: LineSegment StartX=-2600 StartY=2600 StartZ=0 EndX=-2600 EndY=-2600 EndZ=0
    g4: GeomPoint [constr] X=1.53e-14 Y=4.1e-15 Z=0
  constraints (12):
    c: Coincident(g0,g1)
    c: Coincident(g1,g2)
    c: Coincident(g2,g3)
    c: Coincident(g3,g0)
    c: Horizontal(g0)
    c: Horizontal(g2)
    c: Vertical(g1)
    c: Vertical(g3)
    c: Symmetric(g2,g0,g4)
    c: Coincident(g4,g-1)
    c: DistanceX(g2,g2) = 5200
    c: Equal(g2,g3)
FEATURE [Part::FeaturePython] Structure  label="Slab"  # Arch/BIM 118 (typed FeaturePython)
  Base = -> Sketch
  BaseMirror = false
  BaseOffsetX = 0
  BaseOffsetY = 0
  BasePerpendicularToTool = false
  BaseRotation = 0
  ComputedLength = 200
  FaceMaker = 0
  Height = 200
  HorizontalArea = 27040000
  IfcData = attributes={"GlobalId": {"name": "GlobalId", "type": "IfcGloballyUniqueId", "is_enum": false, "enum_values": []}, "Description": {"... (+453 chars omitted),+1 more (map truncated)
  IfcType = 118
  Length = 0
  MoveBase = false
  MoveWithHost = false
  Nodes = (4) [(-2600,-2600,0),(2600,-2600,0),(2600,2600,0),(-2600,2600,0)]
  NodesOffset = 0
  Normal = (0,0,-1)
  PerimeterLength = 20800
  PredefinedType = 0
  ToolOffsetFirst = 0
  ToolOffsetLast = 0
  VerticalArea = 4160000
  Width = 100
FEATURE [Sketcher::SketchObject] Sketch001
  ArcFitTolerance = 1e-06
  FullyConstrained = true
  MakeInternals = false
  sketch-geometry (5):
    g0: LineSegment StartX=-2500 StartY=2500 StartZ=0 EndX=-2500 EndY=-2500 EndZ=0
    g1: LineSegment StartX=-2500 StartY=-2500 StartZ=0 EndX=2500 EndY=-2500 EndZ=0
    g2: LineSegment StartX=2500 StartY=-2500 StartZ=0 EndX=2500 EndY=2500 EndZ=0
    g3: LineSegment StartX=2500 StartY=2500 StartZ=0 EndX=-2500 EndY=2500 EndZ=0
    g4: GeomPoint [constr] X=-7.4e-15 Y=-2.5e-15 Z=0
  constraints (12):
    c: Coincident(g0,g1)
    c: Coincident(g1,g2)
    c: Coincident(g2,g3)
    c: Coincident(g3,g0)
    c: Vertical(g0)
    c: Vertical(g2)
    c: Horizontal(g1)
    c: Horizontal(g3)
    c: Symmetric(g2,g0,g4)
    c: Coincident(g4,g-1)
    c: DistanceX(g3,g3) = 5000
    c: Equal(g3,g0)
FEATURE [Part::FeaturePython] Wall  label="壁"  # Arch/BIM 166 (typed FeaturePython)
  Align = 2
  ArchSketchData = true
  Area = 60000000
  Base = -> Sketch001
  BlockHeight = 0
  BlockLength = 0
  CountBroken = 0
  CountEntire = 0
  Face = 0
  Height = 3000
  HorizontalArea = 2000000
  IfcData = attributes={"GlobalId": {"name": "GlobalId", "type": "IfcGloballyUniqueId", "is_enum": false, "enum_values": []}, "Description": {"... (+533 chars omitted),+1 more (map truncated)
  IfcType = 166
  Joint = 0
  Length = 20000
  MakeBlocks = false
  MoveBase = false
  MoveWithHost = false
  Normal = (0,0,0)
  OffsetFirst = 0
  OffsetSecond = 0
  PerimeterLength = 40000
  PredefinedType = 0
  VerticalArea = 116640000
  Width = 100
FEATURE [App::GeometryPython] BuildingPart001  label="Level"  # Arch/BIM 14 (typed FeaturePython)
  Area = 0
  CompositionType = 0
  Elevation = 0
  Group = -> [Sketch,Structure,Wall]
  Height = 0
  HeightPropagate = true
  IfcData = attributes={"GlobalId": {"name": "GlobalId", "type": "IfcGloballyUniqueId", "is_enum": false, "enum_values": []}, "Description": {"... (+845 chars omitted),+1 more (map truncated)
  IfcType = 14
  LevelOffset = 0
  LongName = Level
  MaterialsTable = Undefined=0,1,2,3
  OnlySolids = true
  expr: Elevation = .Placement.Base.z
FEATURE [App::GeometryPython] BuildingPart  label="ビルディング"  # Arch/BIM 10 (typed FeaturePython)
  Area = 0
  BuildingType = 0
  CompositionType = 0
  ElevationOfRefHeight = 0
  ElevationOfTerrain = 0
  Group = -> [BuildingPart001]
  Height = 0
  HeightPropagate = true
  IfcData = attributes={"GlobalId": {"name": "GlobalId", "type": "IfcGloballyUniqueId", "is_enum": false, "enum_values": []}, "Description": {"... (+1017 chars omitted),+1 more (map truncated)
  IfcType = 10
  LevelOffset = 0
  LongName = ビルディング
  MaterialsTable = Undefined=0,1,2,3
  OnlySolids = true
FEATURE [Sketcher::SketchObject] Sketch002
  ArcFitTolerance = 1e-06
  FullyConstrained = true
  MakeInternals = false
  Placement = pos=(1841,-2453,0) rot=(0,0.707107,0.707107;3.14159rad)
  sketch-geometry (8):
    g0: LineSegment StartX=0 StartY=0 StartZ=0 EndX=900 EndY=0 EndZ=0
    g1: LineSegment StartX=900 StartY=0 StartZ=0 EndX=900 EndY=2100 EndZ=0
    g2: LineSegment StartX=900 StartY=2100 StartZ=0 EndX=0 EndY=2100 EndZ=0
    g3: LineSegment StartX=0 StartY=2100 StartZ=0 EndX=0 EndY=0 EndZ=0
    g4: LineSegment StartX=49 StartY=0 StartZ=0 EndX=851 EndY=0 EndZ=0
    g5: LineSegment StartX=851 StartY=0 StartZ=0 EndX=851 EndY=2051 EndZ=0
    g6: LineSegment StartX=851 StartY=2051 StartZ=0 EndX=49 EndY=2051 EndZ=0
    g7: LineSegment StartX=49 StartY=2051 StartZ=0 EndX=49 EndY=0 EndZ=0
  constraints (23):
    c: Coincident(g0,g1)
    c: Coincident(g1,g2)
    c: Coincident(g2,g3)
    c: Coincident(g3,g0)
    c: Horizontal(g0)
    c: Horizontal(g2)
    c: Vertical(g1)
    c: Vertical(g3)
    c: Coincident(g4,g5)
    c: Coincident(g5,g6)
    c: Coincident(g6,g7)
    c: Coincident(g7,g4)
    c: Horizontal(g4)
    c: Horizontal(g6)
    c: Vertical(g5)
    c: Vertical(g7)
    c: DistanceY(g1) = 2100  'Height'
    c: DistanceX(g0) = 900  'Width'
    c: DistanceY(g6,g2) = 49  'Frame1'
    c: DistanceX(g2,g6) = 49  'Frame2'
    c: DistanceX(g4,g0) = 49  'Frame3'
    c: DistanceY(g0,g4) = 0
    c: Coincident(g0,g-1)
FEATURE [Part::FeaturePython] Window  label="Door"  # Arch/BIM 41 (typed FeaturePython)
  Area = 1890000
  Base = -> Sketch002
  Frame = 50
  Height = 2100
  HoleDepth = 0
  HoleWire = 0
  HorizontalArea = 0
  Hosts = -> [Wall]
  IfcData = attributes={"GlobalId": {"name": "GlobalId", "type": "IfcGloballyUniqueId", "is_enum": false, "enum_values": []}, "Description": {"... (+1933 chars omitted),+1 more (map truncated)
  IfcType = 41
  LouvreSpacing = 0
  LouvreWidth = 0
  MoveBase = false
  MoveWithHost = true
  Normal = (0,-1,2e-16)
  Offset = 50
  Opening = 40
  OperationType = 0
  OverallHeight = 2100
  OverallWidth = 900
  PerimeterLength = 0
  PredefinedType = 0
  Preset = 6
  SymbolElevation = false
  SymbolPlan = false
  VerticalArea = 0
  Width = 900
  WindowParts = OuterFrame | Frame | Wire0,Wire1 | 50.0+V | 0.00+V | Door | Solid panel | Wire1,Edge8,Mode1 | 50.0 | 50.0+V
  expr: OverallHeight = .Height.Value
  expr: OverallWidth = .Width.Value
FEATURE [App::Part] Part  label="room"
  Group = -> [BuildingPart001,Sketch001,Sketch,Sketch002,Structure,Wall,Window,BuildingPart]
  Origin = -> Origin001
---- part ../sofa/sofa.FCStd = doc fcstd_532626a27f76 ----
FCSTD DOCUMENT  (FreeCAD 1.0R39109 (Git))
Label: sofa
License: All rights reserved
LicenseURL: https://en.wikipedia.org/wiki/All_rights_reserved
objects: Sketcher::SketchObject×17, PartDesign::Pad×14, PartDesign::Fillet×11, PartDesign::Plane×9, PartDesign::Body×9, PartDesign::ShapeBinder×8, PartDesign::Pocket×3, App::Part×3, Part::FeaturePython×2, PartDesign::LinearPattern×1
note: 148 computed .brp shape members not serialized (recipe doc carries the construction recipe); baked Part::Feature solids carry a one-line shape summary decoded from their .brp

FEATURE [Sketcher::SketchObject] Sketch
  ArcFitTolerance = 1e-06
  AttachmentSupport = -> [XZ_Plane]
  FullyConstrained = true
  MakeInternals = false
  MapMode = 5
  Placement = pos=(0,0,0) rot=(1,0,0;1.5708rad)
  sketch-geometry (4):
    g0: LineSegment StartX=-300 StartY=380 StartZ=0 EndX=-300 EndY=180 EndZ=0
    g1: LineSegment StartX=-300 StartY=180 StartZ=0 EndX=300 EndY=180 EndZ=0
    g2: LineSegment StartX=300 StartY=180 StartZ=0 EndX=300 EndY=380 EndZ=0
    g3: LineSegment StartX=300 StartY=380 StartZ=0 EndX=-300 EndY=380 EndZ=0
  constraints (11):
    c: Coincident(g0,g1)
    c: Coincident(g1,g2)
    c: Coincident(g2,g3)
    c: Coincident(g3,g0)
    c: Vertical(g0)
    c: Vertical(g2)
    c: Horizontal(g1)
    c: Distance(g0,g2) = 600
    c: Distance(g1,g3) = 200
    c: Symmetric(g0,g2,g-2)
    c: DistanceY(g-1,g1) = 180
FEATURE [PartDesign::Pad] Pad
  Direction = (0,-1,2e-16)
  Length = 700
  Length2 = 10
  Midplane = true
  Placement = pos=(0,0,0) rot=(1,0,0;1.5708rad)
  Profile = -> Sketch
  ReferenceAxis = -> Sketch [N_Axis]
  Refine = true
  Suppressed = false
  Type = 0
FEATURE [Sketcher::SketchObject] Sketch001
  ArcFitTolerance = 1e-06
  AttachmentSupport = -> [YZ_Plane]
  ExternalGeometry = -> [Pad]
  FullyConstrained = false
  MakeInternals = false
  MapMode = 5
  Placement = pos=(0,0,0) rot=(0.57735,0.57735,0.57735;2.0944rad)
  sketch-geometry (6):
    g0: LineSegment StartX=350 StartY=380 StartZ=0 EndX=420 EndY=599.2 EndZ=0
    g1: LineSegment [constr] StartX=350 StartY=380 StartZ=0 EndX=420 EndY=380 EndZ=0
    g2: LineSegment [constr] StartX=420 StartY=380 StartZ=0 EndX=420 EndY=599.2 EndZ=0
    g3: LineSegment StartX=420 StartY=599.2 StartZ=0 EndX=351.422 EndY=613.236 EndZ=0
    g4: LineSegment StartX=351.422 StartY=613.236 StartZ=0 EndX=280 EndY=380 EndZ=0
    g5: LineSegment StartX=280 StartY=380 StartZ=0 EndX=350 EndY=380 EndZ=0
  constraints (14):
    c: Coincident(g0,g-4)
    c: Coincident(g1,g0)
    c: Horizontal(g1)
    c: Coincident(g2,g1)
    c: Coincident(g2,g0)
    c: Vertical(g2)
    c: Coincident(g3,g0)
    c: PointOnObject(g4,g-3)
    c: Coincident(g5,g4)
    c: Coincident(g5,g0)
    c: DistanceX(g1,g1) = 70
    c: DistanceX(g5,g5) = 70
    c: Equal(g5,g3)
    c: Coincident(g4,g3)
FEATURE [PartDesign::Pad] Pad001
  BaseFeature = -> Pad
  Direction = (1,0,0)
  Length = 600
  Length2 = 10
  Midplane = true
  Placement = pos=(0,0,0) rot=(1,0,0;1.5708rad)
  Profile = -> Sketch001
  ReferenceAxis = -> Sketch001 [N_Axis]
  Suppressed = false
  Type = 0
FEATURE [Sketcher::SketchObject] Sketch002
  ArcFitTolerance = 1e-06
  AttachmentSupport = -> [Pad001]
  ExternalGeometry = -> [Pad001]
  FullyConstrained = false
  MakeInternals = false
  MapMode = 5
  Placement = pos=(300,0,0) rot=(0.707107,0,0.707107;3.14159rad)
  sketch-geometry (4):
    g0: LineSegment StartX=380 StartY=-280 StartZ=0 EndX=449.666 EndY=-80 EndZ=0
    g1: LineSegment StartX=449.666 StartY=-80 StartZ=0 EndX=880 EndY=-177.889 EndZ=0
    g2: LineSegment StartX=880 StartY=-177.889 StartZ=0 EndX=799.667 EndY=-408.511 EndZ=0
    g3: LineSegment StartX=799.667 StartY=-408.511 StartZ=0 EndX=380 EndY=-280 EndZ=0
  constraints (9):
    c: Coincident(g0,g-4)
    c: DistanceY(g0,g0) = 200
    c: Coincident(g1,g0)
    c: DistanceX(g0,g1) = 500
    c: Coincident(g2,g1)
    c: Coincident(g3,g2)
    c: Coincident(g3,g0)
    c: Parallel(g2,g0)
    c: Parallel(g3,g-3)
FEATURE [PartDesign::Pad] Pad002
  BaseFeature = -> Pad001
  Direction = (1,0,-2e-16)
  Length = 600
  Length2 = 10
  Placement = pos=(0,0,0) rot=(1,0,0;1.5708rad)
  Profile = -> Sketch002
  ReferenceAxis = -> Sketch002 [N_Axis]
  Reversed = true
  Suppressed = false
  Type = 0
FEATURE [Sketcher::SketchObject] Sketch003
  ArcFitTolerance = 1e-06
  AttachmentSupport = -> [Pad002]
  ExternalGeometry = -> [Pad002]
  FullyConstrained = false
  MakeInternals = false
  MapMode = 5
  Placement = pos=(300,0,0) rot=(0.707107,0,0.707107;3.14159rad)
  sketch-geometry (4):
    g0: LineSegment StartX=180 StartY=-350 StartZ=0 EndX=180 EndY=329.78 EndZ=0
    g1: LineSegment StartX=180 StartY=329.78 StartZ=0 EndX=100 EndY=329.78 EndZ=0
    g2: LineSegment StartX=100 StartY=329.78 StartZ=0 EndX=100 EndY=-350 EndZ=0
    g3: LineSegment StartX=100 StartY=-350 StartZ=0 EndX=180 EndY=-350 EndZ=0
  constraints (10):
    c: Coincident(g0,g1)
    c: Coincident(g1,g2)
    c: Coincident(g2,g3)
    c: Coincident(g3,g0)
    c: Vertical(g0)
    c: Vertical(g2)
    c: Horizontal(g1)
    c: Horizontal(g3)
    c: Coincident(g0,g-3)
    c: DistanceX(g1,g0) = 80
FEATURE [PartDesign::Pad] Pad003
  BaseFeature = -> Pad002
  Direction = (1,0,-2e-16)
  Length = 600
  Length2 = 10
  Placement = pos=(0,0,0) rot=(1,0,0;1.5708rad)
  Profile = -> Sketch003
  ReferenceAxis = -> Sketch003 [N_Axis]
  Refine = true
  Reversed = true
  Suppressed = false
  Type = 0
FEATURE [PartDesign::Fillet] Fillet
  Base = -> Pad003 [Edge9,Edge10]
  BaseFeature = -> Pad003
  Placement = pos=(0,0,0) rot=(1,0,0;1.5708rad)
  Radius = 10
  Refine = true
  SupportTransform = false
  Suppressed = false
  UseAllEdges = false
FEATURE [PartDesign::Fillet] Fillet001
  Base = -> Fillet [Edge4]
  BaseFeature = -> Fillet
  Placement = pos=(0,0,0) rot=(1,0,0;1.5708rad)
  Radius = 30
  Refine = true
  SupportTransform = false
  Suppressed = false
  UseAllEdges = false
FEATURE [PartDesign::Fillet] Fillet002
  Base = -> Fillet001 [Edge1]
  BaseFeature = -> Fillet001
  Placement = pos=(0,0,0) rot=(1,0,0;1.5708rad)
  Radius = 10
  Refine = true
  SupportTransform = false
  Suppressed = false
  UseAllEdges = false
FEATURE [PartDesign::Fillet] Fillet003
  Base = -> Fillet002 [Edge29,Edge41]
  BaseFeature = -> Fillet002
  Placement = pos=(0,0,0) rot=(1,0,0;1.5708rad)
  Radius = 10
  Refine = true
  SupportTransform = false
  Suppressed = false
  UseAllEdges = false
FEATURE [PartDesign::Fillet] Fillet004
  Base = -> Fillet003 [Edge52]
  BaseFeature = -> Fillet003
  Placement = pos=(0,0,0) rot=(1,0,0;1.5708rad)
  Radius = 30
  Refine = true
  SupportTransform = false
  Suppressed = false
  UseAllEdges = false
FEATURE [PartDesign::Fillet] Fillet005
  Base = -> Fillet004 [Edge27,Edge30,Edge36]
  BaseFeature = -> Fillet004
  Placement = pos=(0,0,0) rot=(1,0,0;1.5708rad)
  Radius = 80
  Refine = true
  SupportTransform = false
  Suppressed = false
  UseAllEdges = false
FEATURE [PartDesign::Fillet] Fillet006
  Base = -> Fillet005 [Edge8,Edge33]
  BaseFeature = -> Fillet005
  Placement = pos=(0,0,0) rot=(1,0,0;1.5708rad)
  Radius = 10
  Refine = true
  SupportTransform = false
  Suppressed = false
  UseAllEdges = false
FEATURE [PartDesign::Plane] DatumPlane
  AttachmentSupport = -> [Fillet006]
  Length = 60
  MapMode = 5
  Placement = pos=(300,0,0) rot=(0.707107,0,0.707107;3.14159rad)
  ResizeMode = 0
  Width = 60
FEATURE [PartDesign::LinearPattern] LinearPattern
  BaseFeature = -> Fillet006
  Direction = -> DatumPlane
  Length = 1200
  Mode = 0
  Occurrences = 3
  Offset = 600
  Originals = -> [Fillet006]
  Placement = pos=(0,0,0) rot=(1,0,0;1.5708rad)
  Refine = true
  Suppressed = false
  TransformMode = 1
FEATURE [Sketcher::SketchObject] Sketch004
  ArcFitTolerance = 1e-06
  AttachmentOffset = pos=(0,0,-80) rot=(0,0,1;0rad)
  AttachmentSupport = -> [LinearPattern]
  ExternalGeometry = -> [LinearPattern]
  FullyConstrained = false
  MakeInternals = false
  MapMode = 5
  Placement = pos=(0,-270,-1.78e-14) rot=(1,0,0;1.5708rad)
  sketch-geometry (8):
    g0: LineSegment StartX=-300 StartY=100 StartZ=0 EndX=-300 EndY=618.908 EndZ=0
    g1: LineSegment StartX=-300 StartY=618.908 StartZ=0 EndX=-450 EndY=618.908 EndZ=0
    g2: LineSegment StartX=-450 StartY=618.908 StartZ=0 EndX=-450 EndY=100 EndZ=0
    g3: LineSegment StartX=-450 StartY=100 StartZ=0 EndX=-300 EndY=100 EndZ=0
    g4: LineSegment StartX=1500 StartY=100 StartZ=0 EndX=1650 EndY=100 EndZ=0
    g5: LineSegment StartX=1650 StartY=100 StartZ=0 EndX=1650 EndY=618.908 EndZ=0
    g6: LineSegment StartX=1650 StartY=618.908 StartZ=0 EndX=1500 EndY=618.908 EndZ=0
    g7: LineSegment StartX=1500 StartY=618.908 StartZ=0 EndX=1500 EndY=100 EndZ=0
  constraints (21):
    c: Coincident(g0,g1)
    c: Coincident(g1,g2)
    c: Coincident(g2,g3)
    c: Coincident(g3,g0)
    c: Vertical(g0)
    c: Vertical(g2)
    c: Horizontal(g1)
    c: Horizontal(g3)
    c: Coincident(g0,g-4)
    c: Coincident(g4,g5)
    c: Coincident(g5,g6)
    c: Coincident(g6,g7)
    c: Coincident(g7,g4)
    c: Horizontal(g4)
    c: Horizontal(g6)
    c: Vertical(g5)
    c: Vertical(g7)
    c: Coincident(g4,g-4)
    c: Equal(g6,g1)
    c: DistanceX(g1,g1) = 150
    c: Equal(g2,g5)
FEATURE [PartDesign::Pad] Pad004
  BaseFeature = -> LinearPattern
  Direction = (0,-1,2e-16)
  Length = 620
  Length2 = 10
  Placement = pos=(0,0,0) rot=(1,0,0;1.5708rad)
  Profile = -> Sketch004
  ReferenceAxis = -> Sketch004 [N_Axis]
  Reversed = true
  Suppressed = false
  Type = 0
FEATURE [Sketcher::SketchObject] Sketch005
  ArcFitTolerance = 1e-06
  AttachmentSupport = -> [Pad004]
  ExternalGeometry = -> [Pad004]
  FullyConstrained = false
  MakeInternals = false
  MapMode = 5
  Placement = pos=(1650,0,0) rot=(0.707107,0,0.707107;3.14159rad)
  sketch-geometry (10):
    g0: Circle [constr] CenterX=618.908 CenterY=-350 CenterZ=0 NormalX=0 NormalY=0 NormalZ=1 AngleXU=0 Radius=1
    g1-g4: Circle [constr] x4 (B-spline internal-alignment scaffolding for g5; pole/knot coordinates omitted)
    g5: BSplineCurve PolesCount=4 KnotsCount=2 Degree=3 IsPeriodic=0
    g6: GeomPoint [constr] X=618.908 Y=-350 Z=0
    g7: GeomPoint [constr] X=544.087 Y=270 Z=0
    g8: LineSegment StartX=544.087 StartY=270 StartZ=0 EndX=618.908 EndY=270 EndZ=0
    g9: LineSegment StartX=618.908 StartY=-350 StartZ=0 EndX=618.908 EndY=270 EndZ=0
  constraints (15):
    c: Weight(g0) = 1
    c: Weight(g1) = 1
    c: Equal(g1,g2)
    c: Equal(g1,g3)
    c: Equal(g1,g4)
    c: InternalAlignment(g1-g4 -> g5) x4
    c: InternalAlignment(g6,g5)
    c: InternalAlignment(g7,g5)
    c: Coincident(g1,g0)
    c: PointOnObject(g4,g-4)
    c: Coincident(g-5,g5)
    c: Coincident(g9,g0)
    c: Coincident(g9,g8)
    c: Vertical(g9)
    c: Coincident(g5,g8)
FEATURE [PartDesign::Pocket] Pocket
  BaseFeature = -> Pad004
  Direction = (-1,0,2e-16)
  Length = 150
  Length2 = 5
  Placement = pos=(0,0,0) rot=(1,0,0;1.5708rad)
  Profile = -> Sketch005
  ReferenceAxis = -> Sketch005 [N_Axis]
  Suppressed = false
  Type = 0
FEATURE [Sketcher::SketchObject] Sketch006
  ArcFitTolerance = 1e-06
  AttachmentSupport = -> [Pocket]
  ExternalGeometry = -> [Pocket]
  FullyConstrained = false
  MakeInternals = false
  MapMode = 5
  Placement = pos=(-450,0,0) rot=(0.707107,0,-0.707107;3.14159rad)
  sketch-geometry (10):
    g0: Circle [constr] CenterX=-618.908 CenterY=-350 CenterZ=0 NormalX=0 NormalY=0 NormalZ=1 AngleXU=0 Radius=1
    g1-g4: Circle [constr] x4 (B-spline internal-alignment scaffolding for g5; pole/knot coordinates omitted)
    g5: BSplineCurve PolesCount=4 KnotsCount=2 Degree=3 IsPeriodic=0
    g6: GeomPoint [constr] X=-618.908 Y=-350 Z=0
    g7: GeomPoint [constr] X=-544.087 Y=270 Z=0
    g8: LineSegment StartX=-544.087 StartY=270 StartZ=0 EndX=-618.908 EndY=270 EndZ=0
    g9: LineSegment StartX=-618.908 StartY=-350 StartZ=0 EndX=-618.908 EndY=270 EndZ=0
  constraints (13):
    c: Weight(g0) = 1
    c: Weight(g1) = 1
    c: Equal(g1,g2)
    c: Equal(g1,g3)
    c: Equal(g1,g4)
    c: InternalAlignment(g1-g4 -> g5) x4
    c: InternalAlignment(g6,g5)
    c: InternalAlignment(g7,g5)
    c: Coincident(g1,g0)
    c: Coincident(g9,g0)
    c: Coincident(g9,g8)
    c: Vertical(g9)
    c: Coincident(g5,g8)
FEATURE [PartDesign::Pocket] Pocket001
  BaseFeature = -> Pocket
  Direction = (1,0,2e-16)
  Length = 150
  Length2 = 5
  Placement = pos=(0,0,0) rot=(1,0,0;1.5708rad)
  Profile = -> Sketch006
  ReferenceAxis = -> Sketch006 [N_Axis]
  Suppressed = false
  Type = 0
FEATURE [PartDesign::Fillet] Fillet007
  Base = -> Pocket001 [Edge94,Edge87]
  BaseFeature = -> Pocket001
  Placement = pos=(0,0,0) rot=(1,0,0;1.5708rad)
  Radius = 50
  SupportTransform = false
  Suppressed = false
  UseAllEdges = false
FEATURE [PartDesign::Fillet] Fillet008
  Base = -> Fillet007 [Edge18,Edge155]
  BaseFeature = -> Fillet007
  Placement = pos=(0,0,0) rot=(1,0,0;1.5708rad)
  Radius = 9.9
  Refine = true
  SupportTransform = false
  Suppressed = false
  UseAllEdges = false
FEATURE [PartDesign::Fillet] Fillet009
  Base = -> Fillet008 [Edge102,Edge54]
  BaseFeature = -> Fillet008
  Placement = pos=(0,0,0) rot=(1,0,0;1.5708rad)
  Radius = 100
  Refine = true
  SupportTransform = false
  Suppressed = false
  UseAllEdges = false
FEATURE [PartDesign::Fillet] Fillet010
  Base = -> Fillet009 [Edge147,Edge9]
  BaseFeature = -> Fillet009
  Placement = pos=(0,0,0) rot=(1,0,0;1.5708rad)
  Radius = 5
  Refine = true
  SupportTransform = false
  Suppressed = false
  UseAllEdges = false
FEATURE [Sketcher::SketchObject] Sketch007
  ArcFitTolerance = 1e-06
  AttachmentSupport = -> [Fillet010]
  ExternalGeometry = -> [Fillet010]
  FullyConstrained = false
  MakeInternals = false
  MapMode = 5
  Placement = pos=(0,3e-14,100) rot=(1,0,0;3.14159rad)
  sketch-geometry (14):
    g0: Circle CenterX=900 CenterY=235.906 CenterZ=0 NormalX=0 NormalY=0 NormalZ=1 AngleXU=0 Radius=25
    g1: Circle CenterX=300 CenterY=235.906 CenterZ=0 NormalX=0 NormalY=0 NormalZ=1 AngleXU=0 Radius=25
    g2: Circle CenterX=300 CenterY=-248.707 CenterZ=0 NormalX=0 NormalY=0 NormalZ=1 AngleXU=0 Radius=25
    g3: Circle CenterX=900 CenterY=-248.707 CenterZ=0 NormalX=0 NormalY=0 NormalZ=1 AngleXU=0 Radius=25
    g4: Circle CenterX=1408.78 CenterY=235.906 CenterZ=0 NormalX=0 NormalY=0 NormalZ=1 AngleXU=0 Radius=25
    g5: Circle CenterX=1408.78 CenterY=-248.707 CenterZ=0 NormalX=0 NormalY=0 NormalZ=1 AngleXU=0 Radius=25
    g6: Circle CenterX=-208.781 CenterY=-248.707 CenterZ=0 NormalX=0 NormalY=0 NormalZ=1 AngleXU=0 Radius=25
    g7: Circle CenterX=-208.781 CenterY=235.906 CenterZ=0 NormalX=0 NormalY=0 NormalZ=1 AngleXU=0 Radius=25
    g8: LineSegment [constr] StartX=900 StartY=320 StartZ=0 EndX=900 EndY=235.906 EndZ=0
    g9: LineSegment [constr] StartX=300 StartY=320 StartZ=0 EndX=300 EndY=235.906 EndZ=0
    g10: LineSegment [constr] StartX=900 StartY=235.906 StartZ=0 EndX=1408.78 EndY=235.906 EndZ=0
    g11: LineSegment [constr] StartX=300 StartY=235.906 StartZ=0 EndX=-208.781 EndY=235.906 EndZ=0
    g12: LineSegment [constr] StartX=-208.781 StartY=-248.707 StartZ=0 EndX=300 EndY=-248.707 EndZ=0
    g13: LineSegment [constr] StartX=1408.78 StartY=-248.707 StartZ=0 EndX=900 EndY=-248.707 EndZ=0
  constraints (33):
    c: Equal(g7,g1)
    c: Equal(g1,g0)
    c: Equal(g0,g4)
    c: Equal(g4,g5)
    c: Equal(g5,g3)
    c: Equal(g3,g2)
    c: Equal(g2,g6)
    c: Horizontal(g7,g1)
    c: Horizontal(g1,g0)
    c: Horizontal(g0,g4)
    c: Horizontal(g6,g2)
    c: Horizontal(g2,g3)
    c: Horizontal(g3,g5)
    c: Coincident(g8,g-4)
    c: Vertical(g8)
    c: Coincident(g9,g-3)
    c: Vertical(g9)
    c: Coincident(g10,g0)
    c: Coincident(g10,g4)
    c: Coincident(g11,g1)
    c: Coincident(g11,g7)
    c: Equal(g11,g10)
    c: Coincident(g12,g6)
    c: Coincident(g12,g2)
    c: Coincident(g13,g5)
    c: Coincident(g13,g3)
    c: Equal(g13,g12)
    c: Equal(g12,g10)
    c: Coincident(g1,g9)
    c: Coincident(g8,g0)
    c: Vertical(g0,g3)
    c: Vertical(g1,g2)
    c: Diameter(g7) = 50
FEATURE [PartDesign::Pad] Pad005
  BaseFeature = -> Fillet010
  Direction = (0,0,-1)
  Length = 100
  Length2 = 10
  Placement = pos=(0,0,0) rot=(1,0,0;1.5708rad)
  Profile = -> Sketch007
  ReferenceAxis = -> Sketch007 [N_Axis]
  Refine = true
  Suppressed = false
  TaperAngle = -5
  Type = 0
FEATURE [PartDesign::ShapeBinder] CopyPad005
  Placement = pos=(0,0,0) rot=(1,0,0;1.5708rad)
  TraceSupport = false
FEATURE [PartDesign::Plane] DatumPlane001
  AttachmentSupport = -> [CopyPad005]
  Length = 60
  MapMode = 5
  Placement = pos=(0,7.8e-15,100) rot=(1,0,0;3.14159rad)
  ResizeMode = 0
  Width = 60
FEATURE [Sketcher::SketchObject] Sketch008
  ArcFitTolerance = 1e-06
  AttachmentSupport = -> [DatumPlane001]
  ExternalGeometry = -> [CopyPad005]
  FullyConstrained = true
  MakeInternals = false
  MapMode = 5
  Placement = pos=(0,7.8e-15,100) rot=(1,0,0;3.14159rad)
  sketch-geometry (1):
    g0: Circle CenterX=-208.781 CenterY=235.906 CenterZ=0 NormalX=0 NormalY=0 NormalZ=1 AngleXU=0 Radius=25
  constraints (2):
    c: Coincident(g0,g-3)
    c: Equal(g0,g-3)
FEATURE [PartDesign::Pad] Pad006
  Direction = (0,0,-1)
  Length = 100
  Length2 = 10
  Placement = pos=(0,5.22e-14,100) rot=(1,0,0;3.14159rad)
  Profile = -> Sketch008
  ReferenceAxis = -> Sketch008 [N_Axis]
  Refine = true
  Suppressed = false
  TaperAngle = -5
  Type = 0
FEATURE [PartDesign::Body] Body001
  AllowCompound = false
  Group = -> [DatumPlane001,CopyPad005,Sketch008,Pad006]
  Origin = -> Origin003
  Placement = pos=(-600,0,0) rot=(0,0,1;0rad)
  Tip = -> Pad006
FEATURE [PartDesign::ShapeBinder] CopyPad006
  Placement = pos=(0,0,0) rot=(1,0,0;1.5708rad)
  TraceSupport = false
FEATURE [PartDesign::Plane] DatumPlane002
  AttachmentSupport = -> [CopyPad006]
  Length = 60
  MapMode = 5
  Placement = pos=(0,7.8e-15,100) rot=(1,0,0;3.14159rad)
  ResizeMode = 0
  Width = 60
FEATURE [Sketcher::SketchObject] Sketch009
  ArcFitTolerance = 1e-06
  AttachmentSupport = -> [DatumPlane002]
  ExternalGeometry = -> [CopyPad006]
  FullyConstrained = true
  MakeInternals = false
  MapMode = 5
  Placement = pos=(0,7.8e-15,100) rot=(1,0,0;3.14159rad)
  sketch-geometry (1):
    g0: Circle CenterX=300 CenterY=235.906 CenterZ=0 NormalX=0 NormalY=0 NormalZ=1 AngleXU=0 Radius=25
  constraints (2):
    c: Coincident(g0,g-3)
    c: Equal(g0,g-3)
FEATURE [PartDesign::Pad] Pad007
  Direction = (0,0,-1)
  Length = 100
  Length2 = 10
  Placement = pos=(0,7.44e-14,100) rot=(1,0,0;3.14159rad)
  Profile = -> Sketch009
  ReferenceAxis = -> Sketch009 [N_Axis]
  Refine = true
  Suppressed = false
  TaperAngle = -5
  Type = 0
FEATURE [PartDesign::Body] Body002
  AllowCompound = false
  Group = -> [DatumPlane002,CopyPad006,Sketch009,Pad007]
  Origin = -> Origin004
  Placement = pos=(-600,0,0) rot=(0,0,1;0rad)
  Tip = -> Pad007
FEATURE [PartDesign::ShapeBinder] CopyPad007
  Placement = pos=(0,0,0) rot=(1,0,0;1.5708rad)
  TraceSupport = false
FEATURE [PartDesign::Plane] DatumPlane003
  AttachmentSupport = -> [CopyPad007]
  Length = 60
  MapMode = 5
  Placement = pos=(0,7.8e-15,100) rot=(1,0,0;3.14159rad)
  ResizeMode = 0
  Width = 60
FEATURE [Sketcher::SketchObject] Sketch010
  ArcFitTolerance = 1e-06
  AttachmentSupport = -> [DatumPlane003]
  ExternalGeometry = -> [CopyPad007]
  FullyConstrained = true
  MakeInternals = false
  MapMode = 5
  Placement = pos=(0,7.8e-15,100) rot=(1,0,0;3.14159rad)
  sketch-geometry (1):
    g0: Circle CenterX=900 CenterY=235.906 CenterZ=0 NormalX=0 NormalY=0 NormalZ=1 AngleXU=0 Radius=25
  constraints (2):
    c: Coincident(g0,g-3)
    c: Equal(g0,g-3)
FEATURE [PartDesign::Pad] Pad008
  Direction = (0,0,-1)
  Length = 100
  Length2 = 10
  Placement = pos=(0,7.44e-14,100) rot=(1,0,0;3.14159rad)
  Profile = -> Sketch010
  ReferenceAxis = -> Sketch010 [N_Axis]
  Refine = true
  Suppressed = false
  TaperAngle = -5
  Type = 0
FEATURE [PartDesign::Body] Body003
  AllowCompound = false
  Group = -> [DatumPlane003,CopyPad007,Sketch010,Pad008]
  Origin = -> Origin006
  Placement = pos=(-600,0,0) rot=(0,0,1;0rad)
  Tip = -> Pad008
FEATURE [PartDesign::ShapeBinder] CopyPad008
  Placement = pos=(0,0,0) rot=(1,0,0;1.5708rad)
  TraceSupport = false
FEATURE [PartDesign::Plane] DatumPlane004
  AttachmentSupport = -> [CopyPad008]
  Length = 60
  MapMode = 5
  Placement = pos=(0,7.8e-15,100) rot=(1,0,0;3.14159rad)
  ResizeMode = 0
  Width = 60
FEATURE [Sketcher::SketchObject] Sketch011
  ArcFitTolerance = 1e-06
  AttachmentSupport = -> [DatumPlane004]
  ExternalGeometry = -> [CopyPad008]
  FullyConstrained = true
  MakeInternals = false
  MapMode = 5
  Placement = pos=(0,7.8e-15,100) rot=(1,0,0;3.14159rad)
  sketch-geometry (1):
    g0: Circle CenterX=1408.78 CenterY=235.906 CenterZ=0 NormalX=0 NormalY=0 NormalZ=1 AngleXU=0 Radius=25
  constraints (2):
    c: Coincident(g0,g-3)
    c: Equal(g0,g-3)
FEATURE [PartDesign::Pad] Pad009
  Direction = (0,0,-1)
  Length = 100
  Length2 = 10
  Placement = pos=(0,7.44e-14,100) rot=(1,0,0;3.14159rad)
  Profile = -> Sketch011
  ReferenceAxis = -> Sketch011 [N_Axis]
  Refine = true
  Suppressed = false
  TaperAngle = -5
  Type = 0
FEATURE [PartDesign::Body] Body004
  AllowCompound = false
  Group = -> [DatumPlane004,CopyPad008,Sketch011,Pad009]
  Origin = -> Origin007
  Placement = pos=(-600,0,0) rot=(0,0,1;0rad)
  Tip = -> Pad009
FEATURE [PartDesign::ShapeBinder] CopyPad009
  Placement = pos=(0,0,0) rot=(1,0,0;1.5708rad)
  TraceSupport = false
FEATURE [PartDesign::Plane] DatumPlane005
  AttachmentSupport = -> [CopyPad009]
  Length = 60
  MapMode = 5
  Placement = pos=(0,7.8e-15,100) rot=(1,0,0;3.14159rad)
  ResizeMode = 0
  Width = 60
FEATURE [Sketcher::SketchObject] Sketch012
  ArcFitTolerance = 1e-06
  AttachmentSupport = -> [DatumPlane005]
  ExternalGeometry = -> [CopyPad009]
  FullyConstrained = true
  MakeInternals = false
  MapMode = 5
  Placement = pos=(0,7.8e-15,100) rot=(1,0,0;3.14159rad)
  sketch-geometry (1):
    g0: Circle CenterX=-208.781 CenterY=-248.707 CenterZ=0 NormalX=0 NormalY=0 NormalZ=1 AngleXU=0 Radius=25
  constraints (2):
    c: Coincident(g0,g-3)
    c: Equal(g0,g-3)
FEATURE [PartDesign::Pad] Pad010
  Direction = (0,0,-1)
  Length = 100
  Length2 = 10
  Placement = pos=(0,7.44e-14,100) rot=(1,0,0;3.14159rad)
  Profile = -> Sketch012
  ReferenceAxis = -> Sketch012 [N_Axis]
  Refine = true
  Suppressed = false
  TaperAngle = -5
  Type = 0
FEATURE [PartDesign::Body] Body005
  AllowCompound = false
  Group = -> [DatumPlane005,CopyPad009,Sketch012,Pad010]
  Origin = -> Origin008
  Placement = pos=(-600,0,0) rot=(0,0,1;0rad)
  Tip = -> Pad010
FEATURE [PartDesign::ShapeBinder] CopyPad010
  Placement = pos=(0,0,0) rot=(1,0,0;1.5708rad)
  TraceSupport = false
FEATURE [PartDesign::Plane] DatumPlane006
  AttachmentSupport = -> [CopyPad010]
  Length = 60
  MapMode = 5
  Placement = pos=(0,7.8e-15,100) rot=(1,0,0;3.14159rad)
  ResizeMode = 0
  Width = 60
FEATURE [Sketcher::SketchObject] Sketch013
  ArcFitTolerance = 1e-06
  AttachmentSupport = -> [DatumPlane006]
  ExternalGeometry = -> [CopyPad010]
  FullyConstrained = true
  MakeInternals = false
  MapMode = 5
  Placement = pos=(0,7.8e-15,100) rot=(1,0,0;3.14159rad)
  sketch-geometry (1):
    g0: Circle CenterX=300 CenterY=-248.707 CenterZ=0 NormalX=0 NormalY=0 NormalZ=1 AngleXU=0 Radius=25
  constraints (2):
    c: Coincident(g0,g-3)
    c: Equal(g0,g-3)
FEATURE [PartDesign::Pad] Pad011
  Direction = (0,0,-1)
  Length = 100
  Length2 = 10
  Placement = pos=(0,7.44e-14,100) rot=(1,0,0;3.14159rad)
  Profile = -> Sketch013
  ReferenceAxis = -> Sketch013 [N_Axis]
  Refine = true
  Suppressed = false
  TaperAngle = -5
  Type = 0
FEATURE [PartDesign::Body] Body006
  AllowCompound = false
  Group = -> [DatumPlane006,CopyPad010,Sketch013,Pad011]
  Origin = -> Origin009
  Placement = pos=(-600,0,0) rot=(0,0,1;0rad)
  Tip = -> Pad011
FEATURE [PartDesign::ShapeBinder] CopyPad011
  Placement = pos=(0,0,0) rot=(1,0,0;1.5708rad)
  TraceSupport = false
FEATURE [PartDesign::Plane] DatumPlane007
  AttachmentSupport = -> [CopyPad011]
  Length = 60
  MapMode = 5
  Placement = pos=(0,7.8e-15,100) rot=(1,0,0;3.14159rad)
  ResizeMode = 0
  Width = 60
FEATURE [Sketcher::SketchObject] Sketch014
  ArcFitTolerance = 1e-06
  AttachmentSupport = -> [DatumPlane007]
  ExternalGeometry = -> [CopyPad011]
  FullyConstrained = true
  MakeInternals = false
  MapMode = 5
  Placement = pos=(0,7.8e-15,100) rot=(1,0,0;3.14159rad)
  sketch-geometry (1):
    g0: Circle CenterX=900 CenterY=-248.707 CenterZ=0 NormalX=0 NormalY=0 NormalZ=1 AngleXU=0 Radius=25
  constraints (2):
    c: Coincident(g0,g-3)
    c: Equal(g0,g-3)
FEATURE [PartDesign::Pad] Pad012
  Direction = (0,0,-1)
  Length = 100
  Length2 = 10
  Placement = pos=(0,3e-14,100) rot=(1,0,0;3.14159rad)
  Profile = -> Sketch014
  ReferenceAxis = -> Sketch014 [N_Axis]
  Refine = true
  Suppressed = false
  TaperAngle = -5
  Type = 0
FEATURE [PartDesign::Body] Body007
  AllowCompound = false
  Group = -> [DatumPlane007,CopyPad011,Sketch014,Pad012]
  Origin = -> Origin010
  Placement = pos=(-600,0,0) rot=(0,0,1;0rad)
  Tip = -> Pad012
FEATURE [PartDesign::ShapeBinder] CopyPad012
  Placement = pos=(0,0,0) rot=(1,0,0;1.5708rad)
  TraceSupport = false
FEATURE [PartDesign::Plane] DatumPlane008
  AttachmentSupport = -> [CopyPad012]
  Length = 60
  MapMode = 5
  Placement = pos=(0,7.8e-15,100) rot=(1,0,0;3.14159rad)
  ResizeMode = 0
  Width = 60
FEATURE [Sketcher::SketchObject] Sketch015
  ArcFitTolerance = 1e-06
  AttachmentSupport = -> [DatumPlane008]
  ExternalGeometry = -> [CopyPad012]
  FullyConstrained = true
  MakeInternals = false
  MapMode = 5
  Placement = pos=(0,7.8e-15,100) rot=(1,0,0;3.14159rad)
  sketch-geometry (1):
    g0: Circle CenterX=1408.78 CenterY=-248.707 CenterZ=0 NormalX=0 NormalY=0 NormalZ=1 AngleXU=0 Radius=25
  constraints (2):
    c: Coincident(g0,g-3)
    c: Equal(g0,g-3)
FEATURE [PartDesign::Pad] Pad013
  Direction = (0,0,-1)
  Length = 100
  Length2 = 10
  Placement = pos=(0,7.44e-14,100) rot=(1,0,0;3.14159rad)
  Profile = -> Sketch015
  ReferenceAxis = -> Sketch015 [N_Axis]
  Refine = true
  Suppressed = false
  TaperAngle = -5
  Type = 0
FEATURE [PartDesign::Body] Body008
  AllowCompound = false
  Group = -> [DatumPlane008,CopyPad012,Sketch015,Pad013]
  Origin = -> Origin011
  Placement = pos=(-600,0,0) rot=(0,0,1;0rad)
  Tip = -> Pad013
FEATURE [App::Part] Part  label="Foot"
  Group = -> [Body001,Body002,Body003,Body004,Body005,Body006,Body007,Body008]
  Origin = -> Origin005
  Placement = pos=(-600,0,0) rot=(0,0,1;0rad)
FEATURE [Part::FeaturePython] Clone001  label="foot_clone"  # Draft clone (typed FeaturePython)
  AttacherType = Attacher::AttachEngine3D
  Fuse = false
  Objects = -> [Part]
  Scale = (1,1,1)
FEATURE [Sketcher::SketchObject] Sketch016
  ArcFitTolerance = 1e-06
  AttachmentSupport = -> [Pad005]
  FullyConstrained = false
  MakeInternals = false
  MapMode = 5
  Placement = pos=(0,0,2.89e-14) rot=(1,0,0;3.14159rad)
  sketch-geometry (4):
    g0: LineSegment StartX=-340.164 StartY=321.267 StartZ=0 EndX=-340.164 EndY=-393.446 EndZ=0
    g1: LineSegment StartX=-340.164 StartY=-393.446 StartZ=0 EndX=1597.02 EndY=-393.446 EndZ=0
    g2: LineSegment StartX=1597.02 StartY=-393.446 StartZ=0 EndX=1597.02 EndY=321.267 EndZ=0
    g3: LineSegment StartX=1597.02 StartY=321.267 StartZ=0 EndX=-340.164 EndY=321.267 EndZ=0
  constraints (8):
    c: Coincident(g0,g1)
    c: Coincident(g1,g2)
    c: Coincident(g2,g3)
    c: Coincident(g3,g0)
    c: Vertical(g0)
    c: Vertical(g2)
    c: Horizontal(g1)
    c: Horizontal(g3)
FEATURE [PartDesign::Pocket] Pocket002
  BaseFeature = -> Pad005
  Direction = (0,0,1)
  Length = 100
  Length2 = 5
  Placement = pos=(0,0,0) rot=(1,0,0;1.5708rad)
  Profile = -> Sketch016
  ReferenceAxis = -> Sketch016 [N_Axis]
  Refine = true
  Suppressed = false
  Type = 0
FEATURE [PartDesign::Body] Body
  AllowCompound = false
  Group = -> [Sketch,Pad,Sketch001,Pad001,Sketch002,Pad002,Sketch003,Pad003,Fillet,Fillet001,Fillet002,Fillet003,Fillet004,Fillet005,Fillet006,DatumPlane,LinearPattern,Sketch004,Pad004,Sketch005,Pocket,Sketch006,Pocket001,Fillet007,Fillet008,Fillet009,Fillet010,Sketch007,Pad005,Sketch016,Pocket002]
  Origin = -> Origin
  Placement = pos=(-600,0,0) rot=(0,0,1;0rad)
  Tip = -> Pocket002
FEATURE [App::Part] Part001  label="body_p"
  Group = -> [Body]
  Origin = -> Origin012
  Placement = pos=(-600,0,0) rot=(0,0,1;0rad)
FEATURE [Part::FeaturePython] Clone  label="body_clone"  # Draft clone (typed FeaturePython)
  AttacherType = Attacher::AttachEngine3D
  Fuse = false
  Objects = -> [Part001]
  Scale = (1,1,1)
FEATURE [App::Part] Part002  label="sofa"
  Group = -> [Clone001,Clone]
  Origin = -> Origin013
---- part ../table/table.FCStd = doc fcstd_ad61ff0dbca0 ----
FCSTD DOCUMENT  (FreeCAD 1.0R39109 (Git))
Label: table
License: All rights reserved
LicenseURL: https://en.wikipedia.org/wiki/All_rights_reserved
objects: Sketcher::SketchObject×7, PartDesign::Pad×7, PartDesign::Pocket×2, App::Part×2, PartDesign::Body×1, Assembly::JointGroup×1, Part::FeaturePython×1
note: 43 computed .brp shape members not serialized (recipe doc carries the construction recipe); baked Part::Feature solids carry a one-line shape summary decoded from their .brp

FEATURE [Sketcher::SketchObject] Sketch
  ArcFitTolerance = 1e-06
  AttachmentSupport = -> [XY_Plane]
  FullyConstrained = true
  MakeInternals = false
  MapMode = 5
  sketch-geometry (5):
    g0: LineSegment StartX=-550 StartY=-350 StartZ=0 EndX=550 EndY=-350 EndZ=0
    g1: LineSegment StartX=550 StartY=-350 StartZ=0 EndX=550 EndY=350 EndZ=0
    g2: LineSegment StartX=550 StartY=350 StartZ=0 EndX=-550 EndY=350 EndZ=0
    g3: LineSegment StartX=-550 StartY=350 StartZ=0 EndX=-550 EndY=-350 EndZ=0
    g4: GeomPoint [constr] X=0 Y=0 Z=0
  constraints (12):
    c: Coincident(g0,g1)
    c: Coincident(g1,g2)
    c: Coincident(g2,g3)
    c: Coincident(g3,g0)
    c: Horizontal(g0)
    c: Horizontal(g2)
    c: Vertical(g1)
    c: Vertical(g3)
    c: Symmetric(g2,g0,g4)
    c: Coincident(g4,g-1)
    c: DistanceX(g2,g2) = 1100
    c: DistanceY(g3,g3) = 700
FEATURE [PartDesign::Pad] Pad
  Direction = (0,0,1)
  Length = 30
  Length2 = 10
  Profile = -> Sketch
  ReferenceAxis = -> Sketch [N_Axis]
  Refine = true
  Suppressed = false
  Type = 0
FEATURE [Sketcher::SketchObject] Sketch001
  ArcFitTolerance = 1e-06
  AttachmentSupport = -> [Pad]
  ExternalGeometry = -> [Pad]
  FullyConstrained = true
  MakeInternals = false
  MapMode = 5
  Placement = pos=(0,0,0) rot=(1,0,0;3.14159rad)
  sketch-geometry (16):
    g0: LineSegment StartX=-470 StartY=270 StartZ=0 EndX=-470 EndY=210 EndZ=0
    g1: LineSegment StartX=-470 StartY=210 StartZ=0 EndX=-410 EndY=210 EndZ=0
    g2: LineSegment StartX=-410 StartY=210 StartZ=0 EndX=-410 EndY=270 EndZ=0
    g3: LineSegment StartX=-410 StartY=270 StartZ=0 EndX=-470 EndY=270 EndZ=0
    g4: LineSegment StartX=410 StartY=270 StartZ=0 EndX=410 EndY=210 EndZ=0
    g5: LineSegment StartX=410 StartY=210 StartZ=0 EndX=470 EndY=210 EndZ=0
    g6: LineSegment StartX=470 StartY=210 StartZ=0 EndX=470 EndY=270 EndZ=0
    g7: LineSegment StartX=470 StartY=270 StartZ=0 EndX=410 EndY=270 EndZ=0
    g8: LineSegment StartX=410 StartY=-210 StartZ=0 EndX=410 EndY=-270 EndZ=0
    g9: LineSegment StartX=410 StartY=-270 StartZ=0 EndX=470 EndY=-270 EndZ=0
    g10: LineSegment StartX=470 StartY=-270 StartZ=0 EndX=470 EndY=-210 EndZ=0
    g11: LineSegment StartX=470 StartY=-210 StartZ=0 EndX=410 EndY=-210 EndZ=0
    g12: LineSegment StartX=-470 StartY=-210 StartZ=0 EndX=-470 EndY=-270 EndZ=0
    g13: LineSegment StartX=-470 StartY=-270 StartZ=0 EndX=-410 EndY=-270 EndZ=0
    g14: LineSegment StartX=-410 StartY=-270 StartZ=0 EndX=-410 EndY=-210 EndZ=0
    g15: LineSegment StartX=-410 StartY=-210 StartZ=0 EndX=-470 EndY=-210 EndZ=0
  constraints (48):
    c: Coincident(g0,g1)
    c: Coincident(g1,g2)
    c: Coincident(g2,g3)
    c: Coincident(g3,g0)
    c: Vertical(g0)
    c: Vertical(g2)
    c: Horizontal(g1)
    c: Horizontal(g3)
    c: DistanceX(g1,g1) = 60
    c: DistanceY(g2,g2) = 60
    c: DistanceX(g-4,g0) = 80
    c: DistanceY(g0,g-4) = 80
    c: Coincident(g4,g5)
    c: Coincident(g5,g6)
    c: Coincident(g6,g7)
    c: Coincident(g7,g4)
    c: Vertical(g4)
    c: Vertical(g6)
    c: Horizontal(g5)
    c: Horizontal(g7)
    c: Coincident(g8,g9)
    c: Coincident(g9,g10)
    c: Coincident(g10,g11)
    c: Coincident(g11,g8)
    c: Vertical(g8)
    c: Vertical(g10)
    c: Horizontal(g9)
    c: Horizontal(g11)
    c: Coincident(g12,g13)
    c: Coincident(g13,g14)
    c: Coincident(g14,g15)
    c: Coincident(g15,g12)
    c: Vertical(g12)
    c: Vertical(g14)
    c: Horizontal(g13)
    c: Horizontal(g15)
    c: Equal(g1,g15)
    c: Equal(g15,g11)
    c: Equal(g11,g7)
    c: Equal(g2,g6)
    c: Equal(g6,g10)
    c: Equal(g10,g14)
    c: DistanceX(g-6,g12) = 80
    c: DistanceX(g9,g-6) = 80
    c: DistanceX(g6,g-5) = 80
    c: DistanceY(g6,g-5) = 80
    c: DistanceY(g-6,g9) = 80
    c: DistanceY(g-6,g12) = 80
FEATURE [PartDesign::Pad] Pad001
  BaseFeature = -> Pad
  Direction = (0,0,-1)
  Length = 600
  Length2 = 10
  Profile = -> Sketch001
  ReferenceAxis = -> Sketch001 [N_Axis]
  Refine = true
  Suppressed = false
  Type = 0
FEATURE [Sketcher::SketchObject] Sketch002
  ArcFitTolerance = 1e-06
  AttachmentSupport = -> [Pad001]
  ExternalGeometry = -> [Pad001]
  FullyConstrained = true
  MakeInternals = false
  MapMode = 5
  Placement = pos=(0,-270,0) rot=(1,0,0;1.5708rad)
  sketch-geometry (12):
    g0: LineSegment StartX=470 StartY=-600 StartZ=0 EndX=470 EndY=-200 EndZ=0
    g1: LineSegment StartX=410 StartY=-600 StartZ=0 EndX=410 EndY=-200 EndZ=0
    g2: LineSegment StartX=410 StartY=-600 StartZ=0 EndX=417.5 EndY=-600 EndZ=0
    g3: LineSegment StartX=410 StartY=-200 StartZ=0 EndX=417.5 EndY=-600 EndZ=0
    g4: LineSegment StartX=470 StartY=-200 StartZ=0 EndX=462.5 EndY=-600 EndZ=0
    g5: LineSegment StartX=462.5 StartY=-600 StartZ=0 EndX=470 EndY=-600 EndZ=0
    g6: LineSegment StartX=-410 StartY=-600 StartZ=0 EndX=-410 EndY=-200 EndZ=0
    g7: LineSegment StartX=-470 StartY=-600 StartZ=0 EndX=-470 EndY=-200 EndZ=0
    g8: LineSegment StartX=-470 StartY=-200 StartZ=0 EndX=-462.5 EndY=-600 EndZ=0
    g9: LineSegment StartX=-417.5 StartY=-600 StartZ=0 EndX=-410 EndY=-200 EndZ=0
    g10: LineSegment StartX=-417.5 StartY=-600 StartZ=0 EndX=-410 EndY=-600 EndZ=0
    g11: LineSegment StartX=-462.5 StartY=-600 StartZ=0 EndX=-470 EndY=-600 EndZ=0
  constraints (33):
    c: Coincident(g0,g-3)
    c: Vertical(g0)
    c: DistanceY(g0,g0) = 400
    c: Coincident(g1,g-3)
    c: Vertical(g1)
    c: Equal(g1,g0)
    c: Coincident(g2,g1)
    c: Coincident(g5,g0)
    c: Coincident(g3,g1)
    c: Coincident(g4,g0)
    c: PointOnObject(g4,g5)
    c: Coincident(g2,g3)
    c: PointOnObject(g5,g4)
    c: DistanceX(g1,g2) = 7.5
    c: Equal(g5,g2)
    c: Coincident(g6,g-4)
    c: Vertical(g6)
    c: Coincident(g7,g-4)
    c: Vertical(g7)
    c: Equal(g6,g7)
    c: Equal(g7,g1)
    c: Coincident(g8,g7)
    c: PointOnObject(g8,g-4)
    c: PointOnObject(g9,g-4)
    c: Coincident(g9,g6)
    c: Coincident(g10,g9)
    c: Coincident(g10,g6)
    c: Coincident(g11,g8)
    c: Coincident(g11,g7)
    c: Equal(g10,g11)
    c: Equal(g11,g2)
    c: PointOnObject(g4,g-3)
    c: PointOnObject(g2,g-3)
FEATURE [PartDesign::Pocket] Pocket
  BaseFeature = -> Pad001
  Direction = (0,1,-2e-16)
  Length = 5
  Length2 = 5
  Profile = -> Sketch002
  ReferenceAxis = -> Sketch002 [N_Axis]
  Refine = true
  Suppressed = false
  Type = 1
FEATURE [Sketcher::SketchObject] Sketch003
  ArcFitTolerance = 1e-06
  AttachmentSupport = -> [Pocket]
  ExternalGeometry = -> [Pocket]
  FullyConstrained = true
  MakeInternals = false
  MapMode = 5
  Placement = pos=(-550,0,0) rot=(0.57735,-0.57735,-0.57735;2.0944rad)
  sketch-geometry (12):
    g0: LineSegment StartX=-270 StartY=-200 StartZ=0 EndX=-270 EndY=-600 EndZ=0
    g1: LineSegment StartX=-210 StartY=-200 StartZ=0 EndX=-210 EndY=-600 EndZ=0
    g2: LineSegment StartX=210 StartY=-200 StartZ=0 EndX=210 EndY=-600 EndZ=0
    g3: LineSegment StartX=270 StartY=-200 StartZ=0 EndX=270 EndY=-600 EndZ=0
    g4: LineSegment StartX=-270 StartY=-600 StartZ=0 EndX=-262.5 EndY=-600 EndZ=0
    g5: LineSegment StartX=210 StartY=-600 StartZ=0 EndX=217.5 EndY=-600 EndZ=0
    g6: LineSegment StartX=-270 StartY=-200 StartZ=0 EndX=-262.5 EndY=-600 EndZ=0
    g7: LineSegment StartX=-217.5 StartY=-600 StartZ=0 EndX=-210 EndY=-200 EndZ=0
    g8: LineSegment StartX=210 StartY=-200 StartZ=0 EndX=217.5 EndY=-600 EndZ=0
    g9: LineSegment StartX=262.5 StartY=-600 StartZ=0 EndX=270 EndY=-200 EndZ=0
    g10: LineSegment StartX=262.5 StartY=-600 StartZ=0 EndX=270 EndY=-600 EndZ=0
    g11: LineSegment StartX=-217.5 StartY=-600 StartZ=0 EndX=-210 EndY=-600 EndZ=0
  constraints (30):
    c: Coincident(g0,g-6)
    c: Coincident(g0,g-6)
    c: Coincident(g1,g-5)
    c: Coincident(g1,g-5)
    c: Coincident(g2,g-4)
    c: Coincident(g2,g-4)
    c: Coincident(g3,g-3)
    c: Coincident(g3,g-3)
    c: Coincident(g4,g0)
    c: Coincident(g11,g1)
    c: Coincident(g5,g2)
    c: Coincident(g10,g3)
    c: Coincident(g6,g0)
    c: PointOnObject(g7,g11)
    c: Coincident(g7,g1)
    c: Coincident(g8,g2)
    c: PointOnObject(g9,g10)
    c: Coincident(g9,g3)
    c: Coincident(g5,g8)
    c: PointOnObject(g10,g9)
    c: DistanceX(g10,g10) = 7.5
    c: Coincident(g4,g6)
    c: PointOnObject(g11,g7)
    c: Equal(g4,g11)
    c: Equal(g11,g5)
    c: Equal(g5,g10)
    c: Horizontal(g10)
    c: Horizontal(g5)
    c: Horizontal(g4)
    c: Horizontal(g11)
FEATURE [PartDesign::Pocket] Pocket001
  BaseFeature = -> Pocket
  Direction = (1,0,0)
  Length = 5
  Length2 = 5
  Profile = -> Sketch003
  ReferenceAxis = -> Sketch003 [N_Axis]
  Suppressed = false
  Type = 1
FEATURE [Sketcher::SketchObject] Sketch004
  ArcFitTolerance = 1e-06
  AttachmentSupport = -> [Pocket001]
  ExternalGeometry = -> [Pocket001]
  FullyConstrained = true
  MakeInternals = false
  MapMode = 5
  Placement = pos=(0,-270,0) rot=(1,0,0;1.5708rad)
  sketch-geometry (4):
    g0: LineSegment StartX=-410 StartY=0 StartZ=0 EndX=-410 EndY=-135 EndZ=0
    g1: LineSegment StartX=-410 StartY=-135 StartZ=0 EndX=410 EndY=-135 EndZ=0
    g2: LineSegment StartX=410 StartY=-135 StartZ=0 EndX=410 EndY=0 EndZ=0
    g3: LineSegment StartX=410 StartY=0 StartZ=0 EndX=-410 EndY=0 EndZ=0
  constraints (11):
    c: Coincident(g0,g1)
    c: Coincident(g1,g2)
    c: Coincident(g2,g3)
    c: Coincident(g3,g0)
    c: Vertical(g0)
    c: Vertical(g2)
    c: Horizontal(g1)
    c: Horizontal(g3)
    c: Coincident(g0,g-3)
    c: PointOnObject(g1,g-4)
    c: DistanceY(g2,g2) = 135
FEATURE [PartDesign::Pad] Pad002
  BaseFeature = -> Pocket001
  Direction = (0,-1,2e-16)
  Length = 10
  Length2 = 10
  Profile = -> Sketch004
  ReferenceAxis = -> Sketch004 [N_Axis]
  Suppressed = false
  Type = 3
  UpToFace = -> Pocket001 [Face21]
FEATURE [PartDesign::Pad] Pad003
  BaseFeature = -> Pad002
  Direction = (1,0,0)
  Length = 10
  Length2 = 10
  Profile = -> Pad002 [Face11]
  Suppressed = false
  Type = 3
  UpToFace = -> Pad002 [Face9]
FEATURE [PartDesign::Pad] Pad004
  BaseFeature = -> Pad003
  Direction = (-1,0,0)
  Length = 10
  Length2 = 10
  Profile = -> Pad003 [Face16]
  Suppressed = false
  Type = 3
  UpToFace = -> Pad003 [Face14]
FEATURE [Sketcher::SketchObject] Sketch005
  ArcFitTolerance = 1e-06
  AttachmentSupport = -> [Pad004]
  ExternalGeometry = -> [Pad004]
  FullyConstrained = true
  MakeInternals = false
  MapMode = 5
  Placement = pos=(0,-270,1.134e-13) rot=(1,0,0;1.5708rad)
  sketch-geometry (8):
    g0: LineSegment StartX=-250 StartY=-22.5 StartZ=0 EndX=-250 EndY=-112.5 EndZ=0
    g1: LineSegment StartX=-250 StartY=-112.5 StartZ=0 EndX=250 EndY=-112.5 EndZ=0
    g2: LineSegment StartX=250 StartY=-112.5 StartZ=0 EndX=250 EndY=-22.5 EndZ=0
    g3: LineSegment StartX=250 StartY=-22.5 StartZ=0 EndX=-250 EndY=-22.5 EndZ=0
    g4: LineSegment [constr] StartX=-250 StartY=-22.5 StartZ=0 EndX=250 EndY=-112.5 EndZ=0
    g5: LineSegment [constr] StartX=250 StartY=-22.5 StartZ=0 EndX=-2.84e-14 EndY=-67.5 EndZ=0
    g6: LineSegment [constr] StartX=-410 StartY=-1.137e-13 StartZ=0 EndX=410 EndY=-135 EndZ=0
    g7: LineSegment [constr] StartX=410 StartY=0 StartZ=0 EndX=0 EndY=-67.5 EndZ=0
  constraints (18):
    c: Coincident(g0,g1)
    c: Coincident(g1,g2)
    c: Coincident(g2,g3)
    c: Coincident(g3,g0)
    c: Vertical(g0)
    c: Horizontal(g1)
    c: DistanceY(g0,g0) = 90
    c: DistanceX(g3,g3) = 500
    c: Symmetric(g2,g0,g-2)
    c: Coincident(g4,g0)
    c: Coincident(g4,g1)
    c: Coincident(g5,g2)
    c: Symmetric(g4,g4,g5)
    c: Coincident(g6,g-6)
    c: Coincident(g6,g-5)
    c: Coincident(g7,g-5)
    c: Symmetric(g6,g6,g7)
    c: Coincident(g5,g7)
FEATURE [PartDesign::Pad] Pad005
  BaseFeature = -> Pad004
  Direction = (0,-1,2e-16)
  Length = 3
  Length2 = 10
  Profile = -> Sketch005
  ReferenceAxis = -> Sketch005 [N_Axis]
  Refine = true
  Suppressed = false
  Type = 0
FEATURE [Sketcher::SketchObject] Sketch006
  ArcFitTolerance = 1e-06
  AttachmentSupport = -> [Pad005]
  ExternalGeometry = -> [Pad005]
  FullyConstrained = true
  MakeInternals = false
  MapMode = 5
  Placement = pos=(0,-273,0) rot=(1,0,0;1.5708rad)
  sketch-geometry (8):
    g0: LineSegment StartX=-55 StartY=-57.5 StartZ=0 EndX=-55 EndY=-77.5 EndZ=0
    g1: LineSegment StartX=-55 StartY=-77.5 StartZ=0 EndX=55 EndY=-77.5 EndZ=0
    g2: LineSegment StartX=55 StartY=-77.5 StartZ=0 EndX=55 EndY=-57.5 EndZ=0
    g3: LineSegment StartX=55 StartY=-57.5 StartZ=0 EndX=-55 EndY=-57.5 EndZ=0
    g4: LineSegment [constr] StartX=-55 StartY=-57.5 StartZ=0 EndX=55 EndY=-77.5 EndZ=0
    g5: LineSegment [constr] StartX=55 StartY=-57.5 StartZ=0 EndX=-2.84e-14 EndY=-67.5 EndZ=0
    g6: LineSegment [constr] StartX=-250 StartY=-22.5 StartZ=0 EndX=250 EndY=-112.5 EndZ=0
    g7: LineSegment [constr] StartX=250 StartY=-22.5 StartZ=0 EndX=-2.84e-14 EndY=-67.5 EndZ=0
  constraints (18):
    c: Coincident(g0,g1)
    c: Coincident(g1,g2)
    c: Coincident(g2,g3)
    c: Coincident(g3,g0)
    c: Vertical(g0)
    c: Horizontal(g1)
    c: DistanceX(g3,g3) = 110
    c: DistanceY(g2,g2) = 20
    c: Coincident(g4,g0)
    c: Coincident(g4,g1)
    c: Coincident(g5,g2)
    c: Symmetric(g2,g0,g-2)
    c: Symmetric(g0,g1,g5)
    c: Coincident(g6,g-4)
    c: Coincident(g6,g-3)
    c: Coincident(g7,g-3)
    c: Symmetric(g6,g6,g7)
    c: Coincident(g5,g7)
FEATURE [PartDesign::Pad] Pad006
  BaseFeature = -> Pad005
  Direction = (0,-1,2e-16)
  Length = 10
  Length2 = 10
  Profile = -> Sketch006
  ReferenceAxis = -> Sketch006 [N_Axis]
  Refine = true
  Suppressed = false
  Type = 0
FEATURE [PartDesign::Body] Body  label="table_b"
  AllowCompound = false
  Group = -> [Sketch,Pad,Sketch001,Pad001,Sketch002,Pocket,Sketch003,Pocket001,Sketch004,Pad002,Pad003,Pad004,Sketch005,Pad005,Sketch006,Pad006]
  Origin = -> Origin
  Placement = pos=(0,0,600) rot=(0,0,1;0rad)
  Tip = -> Pad006
FEATURE [Assembly::JointGroup] Joints
FEATURE [App::Part] Part  label="table_p"
  Group = -> [Body]
  Origin = -> Origin001
  Placement = pos=(0,0,600) rot=(0,0,1;0rad)
FEATURE [Part::FeaturePython] Clone  label="table_clone"  # Draft clone (typed FeaturePython)
  AttacherType = Attacher::AttachEngine3D
  Fuse = false
  Objects = -> [Part]
  Scale = (1,1,1)
FEATURE [App::Part] Part001  label="table"
  Group = -> [Clone]
  Origin = -> Origin002
---- part ../table02/table02.FCStd = doc fcstd_72d7ff84d8e0 ----
FCSTD DOCUMENT  (FreeCAD 1.0R39109 (Git))
Label: table02
License: All rights reserved
LicenseURL: https://en.wikipedia.org/wiki/All_rights_reserved
objects: Sketcher::SketchObject×8, PartDesign::Pad×6, PartDesign::Body×6, Part::FeaturePython×6, PartDesign::Pocket×2, App::Part×1
note: 52 computed .brp shape members not serialized (recipe doc carries the construction recipe); baked Part::Feature solids carry a one-line shape summary decoded from their .brp

FEATURE [Sketcher::SketchObject] Sketch
  ArcFitTolerance = 1e-06
  AttachmentSupport = -> [XY_Plane]
  FullyConstrained = false
  MakeInternals = false
  MapMode = 5
  sketch-geometry (24):
    g0: LineSegment [constr] StartX=-600 StartY=-225 StartZ=0 EndX=600 EndY=-225 EndZ=0
    g1: LineSegment [constr] StartX=600 StartY=-225 StartZ=0 EndX=600 EndY=225 EndZ=0
    g2: LineSegment [constr] StartX=600 StartY=225 StartZ=0 EndX=-600 EndY=225 EndZ=0
    g3: LineSegment [constr] StartX=-600 StartY=225 StartZ=0 EndX=-600 EndY=-225 EndZ=0
    g4: GeomPoint [constr] X=0 Y=0 Z=0
    g5: LineSegment [constr] StartX=-600 StartY=225 StartZ=0 EndX=-600 EndY=265 EndZ=0
    g6: LineSegment [constr] StartX=-600 StartY=265 StartZ=0 EndX=-560 EndY=265 EndZ=0
    g7: LineSegment [constr] StartX=-560 StartY=265 StartZ=0 EndX=-560 EndY=185 EndZ=0
    g8: Circle CenterX=-560 CenterY=185 CenterZ=0 NormalX=0 NormalY=0 NormalZ=1 AngleXU=0 Radius=20
    g9: LineSegment [constr] StartX=-600 StartY=-225 StartZ=0 EndX=-600 EndY=-265 EndZ=0
    g10: LineSegment [constr] StartX=-600 StartY=-265 StartZ=0 EndX=-560 EndY=-265 EndZ=0
    g11: LineSegment [constr] StartX=-560 StartY=-265 StartZ=0 EndX=-560 EndY=-185 EndZ=0
    g12: Circle CenterX=-560 CenterY=-185 CenterZ=0 NormalX=0 NormalY=0 NormalZ=1 AngleXU=0 Radius=20
    g13: Circle CenterX=560 CenterY=185 CenterZ=0 NormalX=0 NormalY=0 NormalZ=1 AngleXU=0 Radius=20
    g14: Circle CenterX=560 CenterY=-185.063 CenterZ=0 NormalX=0 NormalY=0 NormalZ=1 AngleXU=0 Radius=20
    g15: LineSegment [constr] StartX=-560 StartY=185 StartZ=0 EndX=-560 EndY=175 EndZ=0
    g16: LineSegment [constr] StartX=-560 StartY=175 StartZ=0 EndX=-570 EndY=175 EndZ=0
    g17: LineSegment [constr] StartX=-570 StartY=175 StartZ=0 EndX=-570 EndY=195 EndZ=0
    g18: LineSegment [constr] StartX=560 StartY=-185.063 StartZ=0 EndX=570 EndY=-185.063 EndZ=0
    g19: LineSegment [constr] StartX=570 StartY=-185.063 StartZ=0 EndX=570 EndY=-195.063 EndZ=0
    g20: LineSegment [constr] StartX=-570 StartY=195 StartZ=0 EndX=-570 EndY=-195.063 EndZ=0
    g21: LineSegment [constr] StartX=-570 StartY=-195.063 StartZ=0 EndX=570 EndY=-195.063 EndZ=0
    g22: LineSegment [constr] StartX=570 StartY=-195.063 StartZ=0 EndX=570 EndY=195 EndZ=0
    g23: LineSegment [constr] StartX=570 StartY=195 StartZ=0 EndX=-570 EndY=195 EndZ=0
  constraints (61):
    c: Coincident(g0,g1)
    c: Coincident(g1,g2)
    c: Coincident(g2,g3)
    c: Coincident(g3,g0)
    c: Horizontal(g0)
    c: Horizontal(g2)
    c: Vertical(g1)
    c: Vertical(g3)
    c: Symmetric(g2,g0,g4)
    c: Distance(g1,g3) = 1200
    c: Distance(g0,g2) = 450
    c: Coincident(g4,g-1)
    c: Coincident(g5,g2)
    c: Vertical(g5)
    c: DistanceY(g5,g5) = 40
    c: Distance(g6) = 40
    c: Coincident(g6,g5)
    c: Horizontal(g6)
    c: Distance(g7) = 80
    c: Coincident(g7,g6)
    c: Vertical(g7)
    c: Diameter(g8) = 40
    c: Coincident(g8,g7)
    c: Distance(g9) = 40
    c: Coincident(g9,g0)
    c: Vertical(g9)
    c: Distance(g10) = 40
    c: Coincident(g10,g9)
    c: Horizontal(g10)
    c: Distance(g11) = 80
    c: Coincident(g11,g10)
    c: Vertical(g11)
    c: Diameter(g12) = 40
    c: Coincident(g12,g11)
    c: Diameter(g13) = 40
    c: Diameter(g14) = 40
    c: Distance(g15) = 10
    c: Coincident(g15,g7)
    c: Vertical(g15)
    c: Distance(g16) = 10
    c: Coincident(g16,g15)
    c: Horizontal(g16)
    c: Distance(g17) = 20
    c: Coincident(g17,g16)
    c: Vertical(g17)
    c: Distance(g18) = 10
    c: Coincident(g18,g14)
    c: Horizontal(g18)
    c: Distance(g19) = 10
    c: Coincident(g19,g18)
    c: Vertical(g19)
    c: Coincident(g20,g21)
    c: Coincident(g21,g22)
    c: Coincident(g22,g23)
    c: Coincident(g23,g20)
    c: Vertical(g20)
    c: Vertical(g22)
    c: Horizontal(g21)
    c: Horizontal(g23)
    c: Coincident(g20,g17)
    c: Coincident(g21,g19)
FEATURE [PartDesign::Pad] Pad
  Direction = (0,0,1)
  Length = 780
  Length2 = 10
  Profile = -> Sketch
  ReferenceAxis = -> Sketch [N_Axis]
  Refine = true
  Suppressed = false
  Type = 0
FEATURE [PartDesign::Body] Body
  AllowCompound = false
  Group = -> [Sketch,Pad]
  Origin = -> Origin
  Tip = -> Pad
FEATURE [Sketcher::SketchObject] Sketch001
  ArcFitTolerance = 1e-06
  AttachmentSupport = -> [XY_Plane001]
  FullyConstrained = false
  MakeInternals = false
  MapMode = 5
  sketch-geometry (21):
    g0: LineSegment [constr] StartX=-600 StartY=-225 StartZ=0 EndX=600 EndY=-225 EndZ=0
    g1: LineSegment [constr] StartX=600 StartY=-225 StartZ=0 EndX=600 EndY=225 EndZ=0
    g2: LineSegment [constr] StartX=600 StartY=225 StartZ=0 EndX=-600 EndY=225 EndZ=0
    g3: LineSegment [constr] StartX=-600 StartY=225 StartZ=0 EndX=-600 EndY=-225 EndZ=0
    g4: GeomPoint [constr] X=0 Y=0 Z=0
    g5: LineSegment [constr] StartX=-600 StartY=225 StartZ=0 EndX=-600 EndY=265 EndZ=0
    g6: LineSegment [constr] StartX=-600 StartY=265 StartZ=0 EndX=-560 EndY=265 EndZ=0
    g7: LineSegment [constr] StartX=-560 StartY=265 StartZ=0 EndX=-560 EndY=185 EndZ=0
    g8: Circle CenterX=-560 CenterY=185 CenterZ=0 NormalX=0 NormalY=0 NormalZ=1 AngleXU=0 Radius=20
    g9: LineSegment [constr] StartX=-600 StartY=-225 StartZ=0 EndX=-600 EndY=-265 EndZ=0
    g10: LineSegment [constr] StartX=-600 StartY=-265 StartZ=0 EndX=-560 EndY=-265 EndZ=0
    g11: LineSegment [constr] StartX=-560 StartY=-265 StartZ=0 EndX=-560 EndY=-185 EndZ=0
    g12: Circle CenterX=-560 CenterY=-185 CenterZ=0 NormalX=0 NormalY=0 NormalZ=1 AngleXU=0 Radius=20
    g13: Circle CenterX=560 CenterY=185 CenterZ=0 NormalX=0 NormalY=0 NormalZ=1 AngleXU=0 Radius=20
    g14: LineSegment [constr] StartX=-560 StartY=185 StartZ=0 EndX=-560 EndY=175 EndZ=0
    g15: LineSegment [constr] StartX=-560 StartY=175 StartZ=0 EndX=-570 EndY=175 EndZ=0
    g16: LineSegment [constr] StartX=-570 StartY=175 StartZ=0 EndX=-570 EndY=195 EndZ=0
    g17: LineSegment [constr] StartX=-570 StartY=195 StartZ=0 EndX=-570 EndY=-195.063 EndZ=0
    g18: LineSegment [constr] StartX=-570 StartY=-195.063 StartZ=0 EndX=570 EndY=-195.063 EndZ=0
    g19: LineSegment [constr] StartX=570 StartY=-195.063 StartZ=0 EndX=570 EndY=195 EndZ=0
    g20: LineSegment [constr] StartX=570 StartY=195 StartZ=0 EndX=-570 EndY=195 EndZ=0
  constraints (52):
    c: Coincident(g0,g1)
    c: Coincident(g1,g2)
    c: Coincident(g2,g3)
    c: Coincident(g3,g0)
    c: Horizontal(g0)
    c: Horizontal(g2)
    c: Vertical(g1)
    c: Vertical(g3)
    c: Symmetric(g2,g0,g4)
    c: Distance(g1,g3) = 1200
    c: Distance(g0,g2) = 450
    c: Coincident(g4,g-1)
    c: Coincident(g5,g2)
    c: Vertical(g5)
    c: DistanceY(g5,g5) = 40
    c: Distance(g6) = 40
    c: Coincident(g6,g5)
    c: Horizontal(g6)
    c: Distance(g7) = 80
    c: Coincident(g7,g6)
    c: Vertical(g7)
    c: Diameter(g8) = 40
    c: Coincident(g8,g7)
    c: Distance(g9) = 40
    c: Coincident(g9,g0)
    c: Vertical(g9)
    c: Distance(g10) = 40
    c: Coincident(g10,g9)
    c: Horizontal(g10)
    c: Distance(g11) = 80
    c: Coincident(g11,g10)
    c: Vertical(g11)
    c: Diameter(g12) = 40
    c: Coincident(g12,g11)
    c: Diameter(g13) = 40
    c: Distance(g14) = 10
    c: Coincident(g14,g7)
    c: Vertical(g14)
    c: Distance(g15) = 10
    c: Coincident(g15,g14)
    c: Horizontal(g15)
    c: Distance(g16) = 20
    c: Coincident(g16,g15)
    c: Vertical(g16)
    c: Coincident(g17,g18)
    c: Coincident(g19,g20)
    c: Coincident(g20,g17)
    c: Vertical(g17)
    c: Vertical(g19)
    c: Horizontal(g18)
    c: Horizontal(g20)
    c: Coincident(g17,g16)
FEATURE [PartDesign::Pad] Pad001
  Direction = (0,0,1)
  Length = 780
  Length2 = 10
  Profile = -> Sketch001
  ReferenceAxis = -> Sketch001 [N_Axis]
  Refine = true
  Suppressed = false
  Type = 0
FEATURE [PartDesign::Body] Body001
  AllowCompound = false
  Group = -> [Sketch001,Pad001]
  Origin = -> Origin001
  Tip = -> Pad001
FEATURE [Sketcher::SketchObject] Sketch002
  ArcFitTolerance = 1e-06
  AttachmentSupport = -> [XY_Plane002]
  FullyConstrained = false
  MakeInternals = false
  MapMode = 5
  sketch-geometry (22):
    g0: LineSegment [constr] StartX=-600 StartY=-225 StartZ=0 EndX=600 EndY=-225 EndZ=0
    g1: LineSegment [constr] StartX=600 StartY=-225 StartZ=0 EndX=600 EndY=225 EndZ=0
    g2: LineSegment [constr] StartX=600 StartY=225 StartZ=0 EndX=-600 EndY=225 EndZ=0
    g3: LineSegment [constr] StartX=-600 StartY=225 StartZ=0 EndX=-600 EndY=-225 EndZ=0
    g4: GeomPoint [constr] X=0 Y=0 Z=0
    g5: LineSegment [constr] StartX=-600 StartY=225 StartZ=0 EndX=-600 EndY=265 EndZ=0
    g6: LineSegment [constr] StartX=-600 StartY=265 StartZ=0 EndX=-560 EndY=265 EndZ=0
    g7: LineSegment [constr] StartX=-560 StartY=265 StartZ=0 EndX=-560 EndY=185 EndZ=0
    g8: Circle CenterX=-560 CenterY=185 CenterZ=0 NormalX=0 NormalY=0 NormalZ=1 AngleXU=0 Radius=20
    g9: LineSegment [constr] StartX=-600 StartY=-225 StartZ=0 EndX=-600 EndY=-265 EndZ=0
    g10: LineSegment [constr] StartX=-600 StartY=-265 StartZ=0 EndX=-560 EndY=-265 EndZ=0
    g11: LineSegment [constr] StartX=-560 StartY=-265 StartZ=0 EndX=-560 EndY=-185 EndZ=0
    g12: Circle CenterX=-560 CenterY=-185 CenterZ=0 NormalX=0 NormalY=0 NormalZ=1 AngleXU=0 Radius=20
    g13: LineSegment [constr] StartX=-560 StartY=185 StartZ=0 EndX=-560 EndY=175 EndZ=0
    g14: LineSegment [constr] StartX=-560 StartY=175 StartZ=0 EndX=-570 EndY=175 EndZ=0
    g15: LineSegment [constr] StartX=-570 StartY=175 StartZ=0 EndX=-570 EndY=195 EndZ=0
    g16: LineSegment [constr] StartX=560 StartY=-185.063 StartZ=0 EndX=570 EndY=-185.063 EndZ=0
    g17: LineSegment [constr] StartX=570 StartY=-185.063 StartZ=0 EndX=570 EndY=-195.063 EndZ=0
    g18: LineSegment [constr] StartX=-570 StartY=195 StartZ=0 EndX=-570 EndY=-195.063 EndZ=0
    g19: LineSegment [constr] StartX=-570 StartY=-195.063 StartZ=0 EndX=570 EndY=-195.063 EndZ=0
    g20: LineSegment [constr] StartX=570 StartY=-195.063 StartZ=0 EndX=570 EndY=195 EndZ=0
    g21: LineSegment [constr] StartX=570 StartY=195 StartZ=0 EndX=-570 EndY=195 EndZ=0
  constraints (58):
    c: Coincident(g0,g1)
    c: Coincident(g1,g2)
    c: Coincident(g2,g3)
    c: Coincident(g3,g0)
    c: Horizontal(g0)
    c: Horizontal(g2)
    c: Vertical(g1)
    c: Vertical(g3)
    c: Symmetric(g2,g0,g4)
    c: Distance(g1,g3) = 1200
    c: Distance(g0,g2) = 450
    c: Coincident(g4,g-1)
    c: Coincident(g5,g2)
    c: Vertical(g5)
    c: DistanceY(g5,g5) = 40
    c: Distance(g6) = 40
    c: Coincident(g6,g5)
    c: Horizontal(g6)
    c: Distance(g7) = 80
    c: Coincident(g7,g6)
    c: Vertical(g7)
    c: Diameter(g8) = 40
    c: Coincident(g8,g7)
    c: Distance(g9) = 40
    c: Coincident(g9,g0)
    c: Vertical(g9)
    c: Distance(g10) = 40
    c: Coincident(g10,g9)
    c: Horizontal(g10)
    c: Distance(g11) = 80
    c: Coincident(g11,g10)
    c: Vertical(g11)
    c: Diameter(g12) = 40
    c: Coincident(g12,g11)
    c: Distance(g13) = 10
    c: Coincident(g13,g7)
    c: Vertical(g13)
    c: Distance(g14) = 10
    c: Coincident(g14,g13)
    c: Horizontal(g14)
    c: Distance(g15) = 20
    c: Coincident(g15,g14)
    c: Vertical(g15)
    c: Distance(g16) = 10
    c: Horizontal(g16)
    c: Distance(g17) = 10
    c: Coincident(g17,g16)
    c: Vertical(g17)
    c: Coincident(g18,g19)
    c: Coincident(g19,g20)
    c: Coincident(g20,g21)
    c: Coincident(g21,g18)
    c: Vertical(g18)
    c: Vertical(g20)
    c: Horizontal(g19)
    c: Horizontal(g21)
    c: Coincident(g18,g15)
    c: Coincident(g19,g17)
FEATURE [PartDesign::Pad] Pad002
  Direction = (0,0,1)
  Length = 780
  Length2 = 10
  Profile = -> Sketch002
  ReferenceAxis = -> Sketch002 [N_Axis]
  Refine = true
  Suppressed = false
  Type = 0
FEATURE [PartDesign::Body] Body002
  AllowCompound = false
  Group = -> [Sketch002,Pad002]
  Origin = -> Origin002
  Tip = -> Pad002
FEATURE [Sketcher::SketchObject] Sketch003
  ArcFitTolerance = 1e-06
  AttachmentSupport = -> [XY_Plane003]
  FullyConstrained = false
  MakeInternals = false
  MapMode = 5
  sketch-geometry (21):
    g0: LineSegment [constr] StartX=-600 StartY=-225 StartZ=0 EndX=600 EndY=-225 EndZ=0
    g1: LineSegment [constr] StartX=600 StartY=-225 StartZ=0 EndX=600 EndY=225 EndZ=0
    g2: LineSegment [constr] StartX=600 StartY=225 StartZ=0 EndX=-600 EndY=225 EndZ=0
    g3: LineSegment [constr] StartX=-600 StartY=225 StartZ=0 EndX=-600 EndY=-225 EndZ=0
    g4: GeomPoint [constr] X=0 Y=0 Z=0
    g5: LineSegment [constr] StartX=-600 StartY=225 StartZ=0 EndX=-600 EndY=265 EndZ=0
    g6: LineSegment [constr] StartX=-600 StartY=265 StartZ=0 EndX=-560 EndY=265 EndZ=0
    g7: LineSegment [constr] StartX=-560 StartY=265 StartZ=0 EndX=-560 EndY=185 EndZ=0
    g8: Circle CenterX=-560 CenterY=185 CenterZ=0 NormalX=0 NormalY=0 NormalZ=1 AngleXU=0 Radius=20
    g9: LineSegment [constr] StartX=-600 StartY=-225 StartZ=0 EndX=-600 EndY=-265 EndZ=0
    g10: LineSegment [constr] StartX=-600 StartY=-265 StartZ=0 EndX=-560 EndY=-265 EndZ=0
    g11: LineSegment [constr] StartX=-560 StartY=-265 StartZ=0 EndX=-560 EndY=-185 EndZ=0
    g12: LineSegment [constr] StartX=-560 StartY=185 StartZ=0 EndX=-560 EndY=175 EndZ=0
    g13: LineSegment [constr] StartX=-560 StartY=175 StartZ=0 EndX=-570 EndY=175 EndZ=0
    g14: LineSegment [constr] StartX=-570 StartY=175 StartZ=0 EndX=-570 EndY=195 EndZ=0
    g15: LineSegment [constr] StartX=560 StartY=-185.063 StartZ=0 EndX=570 EndY=-185.063 EndZ=0
    g16: LineSegment [constr] StartX=570 StartY=-185.063 StartZ=0 EndX=570 EndY=-195.063 EndZ=0
    g17: LineSegment [constr] StartX=-570 StartY=195 StartZ=0 EndX=-570 EndY=-195.063 EndZ=0
    g18: LineSegment [constr] StartX=-570 StartY=-195.063 StartZ=0 EndX=570 EndY=-195.063 EndZ=0
    g19: LineSegment [constr] StartX=570 StartY=-195.063 StartZ=0 EndX=570 EndY=195 EndZ=0
    g20: LineSegment [constr] StartX=570 StartY=195 StartZ=0 EndX=-570 EndY=195 EndZ=0
  constraints (56):
    c: Coincident(g0,g1)
    c: Coincident(g1,g2)
    c: Coincident(g2,g3)
    c: Coincident(g3,g0)
    c: Horizontal(g0)
    c: Horizontal(g2)
    c: Vertical(g1)
    c: Vertical(g3)
    c: Symmetric(g2,g0,g4)
    c: Distance(g1,g3) = 1200
    c: Distance(g0,g2) = 450
    c: Coincident(g4,g-1)
    c: Coincident(g5,g2)
    c: Vertical(g5)
    c: DistanceY(g5,g5) = 40
    c: Distance(g6) = 40
    c: Coincident(g6,g5)
    c: Horizontal(g6)
    c: Distance(g7) = 80
    c: Coincident(g7,g6)
    c: Vertical(g7)
    c: Diameter(g8) = 40
    c: Coincident(g8,g7)
    c: Distance(g9) = 40
    c: Coincident(g9,g0)
    c: Vertical(g9)
    c: Distance(g10) = 40
    c: Coincident(g10,g9)
    c: Horizontal(g10)
    c: Distance(g11) = 80
    c: Coincident(g11,g10)
    c: Vertical(g11)
    c: Distance(g12) = 10
    c: Coincident(g12,g7)
    c: Vertical(g12)
    c: Distance(g13) = 10
    c: Coincident(g13,g12)
    c: Horizontal(g13)
    c: Distance(g14) = 20
    c: Coincident(g14,g13)
    c: Vertical(g14)
    c: Distance(g15) = 10
    c: Horizontal(g15)
    c: Distance(g16) = 10
    c: Coincident(g16,g15)
    c: Vertical(g16)
    c: Coincident(g17,g18)
    c: Coincident(g18,g19)
    c: Coincident(g19,g20)
    c: Coincident(g20,g17)
    c: Vertical(g17)
    c: Vertical(g19)
    c: Horizontal(g18)
    c: Horizontal(g20)
    c: Coincident(g17,g14)
    c: Coincident(g18,g16)
FEATURE [PartDesign::Pad] Pad003
  Direction = (0,0,1)
  Length = 780
  Length2 = 10
  Profile = -> Sketch003
  ReferenceAxis = -> Sketch003 [N_Axis]
  Refine = true
  Suppressed = false
  Type = 0
FEATURE [PartDesign::Body] Body003
  AllowCompound = false
  Group = -> [Sketch003,Pad003]
  Origin = -> Origin003
  Tip = -> Pad003
FEATURE [Sketcher::SketchObject] Sketch004
  ArcFitTolerance = 1e-06
  AttachmentSupport = -> [XY_Plane004]
  FullyConstrained = false
  MakeInternals = false
  MapMode = 5
  sketch-geometry (20):
    g0: LineSegment [constr] StartX=-600 StartY=-225 StartZ=0 EndX=600 EndY=-225 EndZ=0
    g1: LineSegment [constr] StartX=600 StartY=-225 StartZ=0 EndX=600 EndY=225 EndZ=0
    g2: LineSegment [constr] StartX=600 StartY=225 StartZ=0 EndX=-600 EndY=225 EndZ=0
    g3: LineSegment [constr] StartX=-600 StartY=225 StartZ=0 EndX=-600 EndY=-225 EndZ=0
    g4: GeomPoint [constr] X=0 Y=0 Z=0
    g5: LineSegment [constr] StartX=-600 StartY=225 StartZ=0 EndX=-600 EndY=265 EndZ=0
    g6: LineSegment [constr] StartX=-600 StartY=265 StartZ=0 EndX=-560 EndY=265 EndZ=0
    g7: LineSegment [constr] StartX=-560 StartY=265 StartZ=0 EndX=-560 EndY=185 EndZ=0
    g8: LineSegment [constr] StartX=-600 StartY=-225 StartZ=0 EndX=-600 EndY=-265 EndZ=0
    g9: LineSegment [constr] StartX=-600 StartY=-265 StartZ=0 EndX=-560 EndY=-265 EndZ=0
    g10: LineSegment [constr] StartX=-560 StartY=-265 StartZ=0 EndX=-560 EndY=-185 EndZ=0
    g11: LineSegment [constr] StartX=-560 StartY=185 StartZ=0 EndX=-560 EndY=175 EndZ=0
    g12: LineSegment [constr] StartX=-560 StartY=175 StartZ=0 EndX=-570 EndY=175 EndZ=0
    g13: LineSegment [constr] StartX=-570 StartY=175 StartZ=0 EndX=-570 EndY=195 EndZ=0
    g14: LineSegment [constr] StartX=560 StartY=-185.063 StartZ=0 EndX=570 EndY=-185.063 EndZ=0
    g15: LineSegment [constr] StartX=570 StartY=-185.063 StartZ=0 EndX=570 EndY=-195.063 EndZ=0
    g16: LineSegment StartX=-570 StartY=195 StartZ=0 EndX=-570 EndY=-195.063 EndZ=0
    g17: LineSegment StartX=-570 StartY=-195.063 StartZ=0 EndX=570 EndY=-195.063 EndZ=0
    g18: LineSegment StartX=570 StartY=-195.063 StartZ=0 EndX=570 EndY=195 EndZ=0
    g19: LineSegment StartX=570 StartY=195 StartZ=0 EndX=-570 EndY=195 EndZ=0
  constraints (54):
    c: Coincident(g0,g1)
    c: Coincident(g1,g2)
    c: Coincident(g2,g3)
    c: Coincident(g3,g0)
    c: Horizontal(g0)
    c: Horizontal(g2)
    c: Vertical(g1)
    c: Vertical(g3)
    c: Symmetric(g2,g0,g4)
    c: Distance(g1,g3) = 1200
    c: Distance(g0,g2) = 450
    c: Coincident(g4,g-1)
    c: Coincident(g5,g2)
    c: Vertical(g5)
    c: DistanceY(g5,g5) = 40
    c: Distance(g6) = 40
    c: Coincident(g6,g5)
    c: Horizontal(g6)
    c: Distance(g7) = 80
    c: Coincident(g7,g6)
    c: Vertical(g7)
    c: Distance(g8) = 40
    c: Coincident(g8,g0)
    c: Vertical(g8)
    c: Distance(g9) = 40
    c: Coincident(g9,g8)
    c: Horizontal(g9)
    c: Distance(g10) = 80
    c: Coincident(g10,g9)
    c: Vertical(g10)
    c: Distance(g11) = 10
    c: Coincident(g11,g7)
    c: Vertical(g11)
    c: Distance(g12) = 10
    c: Coincident(g12,g11)
    c: Horizontal(g12)
    c: Distance(g13) = 20
    c: Coincident(g13,g12)
    c: Vertical(g13)
    c: Distance(g14) = 10
    c: Horizontal(g14)
    c: Distance(g15) = 10
    c: Coincident(g15,g14)
    c: Vertical(g15)
    c: Coincident(g16,g17)
    c: Coincident(g17,g18)
    c: Coincident(g18,g19)
    c: Coincident(g19,g16)
    c: Vertical(g16)
    c: Vertical(g18)
    c: Horizontal(g17)
    c: Horizontal(g19)
    c: Coincident(g16,g13)
    c: Coincident(g17,g15)
FEATURE [PartDesign::Pad] Pad004
  Direction = (0,0,1)
  Length = 220
  Length2 = 10
  Profile = -> Sketch004
  ReferenceAxis = -> Sketch004 [N_Axis]
  Refine = true
  Suppressed = false
  Type = 0
FEATURE [Sketcher::SketchObject] Sketch005
  ArcFitTolerance = 1e-06
  AttachmentSupport = -> [Pad004]
  ExternalGeometry = -> [Pad004]
  FullyConstrained = true
  MakeInternals = false
  MapMode = 5
  Placement = pos=(0,0,0) rot=(1,0,0;3.14159rad)
  sketch-geometry (4):
    g0: LineSegment StartX=-570 StartY=195.063 StartZ=0 EndX=-570 EndY=-195 EndZ=0
    g1: LineSegment StartX=-570 StartY=-195 StartZ=0 EndX=570 EndY=-195 EndZ=0
    g2: LineSegment StartX=570 StartY=-195 StartZ=0 EndX=570 EndY=195.063 EndZ=0
    g3: LineSegment StartX=570 StartY=195.063 StartZ=0 EndX=-570 EndY=195.063 EndZ=0
  constraints (10):
    c: Coincident(g0,g1)
    c: Coincident(g1,g2)
    c: Coincident(g2,g3)
    c: Coincident(g3,g0)
    c: Vertical(g0)
    c: Vertical(g2)
    c: Horizontal(g1)
    c: Horizontal(g3)
    c: Coincident(g0,g-3)
    c: Coincident(g1,g-4)
FEATURE [PartDesign::Pocket] Pocket
  BaseFeature = -> Pad004
  Direction = (0,0,1)
  Length = 180
  Length2 = 5
  Profile = -> Sketch005
  ReferenceAxis = -> Sketch005 [N_Axis]
  Refine = true
  Suppressed = false
  Type = 0
FEATURE [PartDesign::Body] Body004
  AllowCompound = false
  Group = -> [Sketch004,Pad004,Sketch005,Pocket]
  Origin = -> Origin004
  Tip = -> Pocket
FEATURE [Sketcher::SketchObject] Sketch006
  ArcFitTolerance = 1e-06
  AttachmentSupport = -> [XY_Plane005]
  FullyConstrained = false
  MakeInternals = false
  MapMode = 5
  sketch-geometry (16):
    g0: LineSegment StartX=-600 StartY=-225 StartZ=0 EndX=600 EndY=-225 EndZ=0
    g1: LineSegment StartX=600 StartY=-225 StartZ=0 EndX=600 EndY=225 EndZ=0
    g2: LineSegment StartX=600 StartY=225 StartZ=0 EndX=-600 EndY=225 EndZ=0
    g3: LineSegment StartX=-600 StartY=225 StartZ=0 EndX=-600 EndY=-225 EndZ=0
    g4: GeomPoint [constr] X=0 Y=0 Z=0
    g5: LineSegment [constr] StartX=-600 StartY=225 StartZ=0 EndX=-600 EndY=265 EndZ=0
    g6: LineSegment [constr] StartX=-600 StartY=265 StartZ=0 EndX=-560 EndY=265 EndZ=0
    g7: LineSegment [constr] StartX=-560 StartY=265 StartZ=0 EndX=-560 EndY=185 EndZ=0
    g8: LineSegment [constr] StartX=-600 StartY=-225 StartZ=0 EndX=-600 EndY=-265 EndZ=0
    g9: LineSegment [constr] StartX=-600 StartY=-265 StartZ=0 EndX=-560 EndY=-265 EndZ=0
    g10: LineSegment [constr] StartX=-560 StartY=-265 StartZ=0 EndX=-560 EndY=-185 EndZ=0
    g11: LineSegment [constr] StartX=-560 StartY=185 StartZ=0 EndX=-560 EndY=175 EndZ=0
    g12: LineSegment [constr] StartX=-560 StartY=175 StartZ=0 EndX=-570 EndY=175 EndZ=0
    g13: LineSegment [constr] StartX=-570 StartY=175 StartZ=0 EndX=-570 EndY=195 EndZ=0
    g14: LineSegment [constr] StartX=560 StartY=-185.063 StartZ=0 EndX=570 EndY=-185.063 EndZ=0
    g15: LineSegment [constr] StartX=570 StartY=-185.063 StartZ=0 EndX=570 EndY=-195.063 EndZ=0
  constraints (44):
    c: Coincident(g0,g1)
    c: Coincident(g1,g2)
    c: Coincident(g2,g3)
    c: Coincident(g3,g0)
    c: Horizontal(g0)
    c: Horizontal(g2)
    c: Vertical(g1)
    c: Vertical(g3)
    c: Symmetric(g2,g0,g4)
    c: Distance(g1,g3) = 1200
    c: Distance(g0,g2) = 450
    c: Coincident(g4,g-1)
    c: Coincident(g5,g2)
    c: Vertical(g5)
    c: DistanceY(g5,g5) = 40
    c: Distance(g6) = 40
    c: Coincident(g6,g5)
    c: Horizontal(g6)
    c: Distance(g7) = 80
    c: Coincident(g7,g6)
    c: Vertical(g7)
    c: Distance(g8) = 40
    c: Coincident(g8,g0)
    c: Vertical(g8)
    c: Distance(g9) = 40
    c: Coincident(g9,g8)
    c: Horizontal(g9)
    c: Distance(g10) = 80
    c: Coincident(g10,g9)
    c: Vertical(g10)
    c: Distance(g11) = 10
    c: Coincident(g11,g7)
    c: Vertical(g11)
    c: Distance(g12) = 10
    c: Coincident(g12,g11)
    c: Horizontal(g12)
    c: Distance(g13) = 20
    c: Coincident(g13,g12)
    c: Vertical(g13)
    c: Distance(g14) = 10
    c: Horizontal(g14)
    c: Distance(g15) = 10
    c: Coincident(g15,g14)
    c: Vertical(g15)
FEATURE [PartDesign::Pad] Pad005
  Direction = (0,0,1)
  Length = 800
  Length2 = 10
  Profile = -> Sketch006
  ReferenceAxis = -> Sketch006 [N_Axis]
  Refine = true
  Suppressed = false
  Type = 0
FEATURE [Sketcher::SketchObject] Sketch007
  ArcFitTolerance = 1e-06
  AttachmentSupport = -> [Pad005]
  ExternalGeometry = -> [Pad005]
  FullyConstrained = true
  MakeInternals = false
  MapMode = 5
  Placement = pos=(0,0,0) rot=(1,0,0;3.14159rad)
  sketch-geometry (4):
    g0: LineSegment StartX=-600 StartY=225 StartZ=0 EndX=-600 EndY=-225 EndZ=0
    g1: LineSegment StartX=-600 StartY=-225 StartZ=0 EndX=600 EndY=-225 EndZ=0
    g2: LineSegment StartX=600 StartY=-225 StartZ=0 EndX=600 EndY=225 EndZ=0
    g3: LineSegment StartX=600 StartY=225 StartZ=0 EndX=-600 EndY=225 EndZ=0
  constraints (10):
    c: Coincident(g0,g1)
    c: Coincident(g1,g2)
    c: Coincident(g2,g3)
    c: Coincident(g3,g0)
    c: Vertical(g0)
    c: Vertical(g2)
    c: Horizontal(g1)
    c: Horizontal(g3)
    c: Coincident(g0,g-3)
    c: Coincident(g1,g-4)
FEATURE [PartDesign::Pocket] Pocket001
  BaseFeature = -> Pad005
  Direction = (0,0,1)
  Length = 760
  Length2 = 5
  Profile = -> Sketch007
  ReferenceAxis = -> Sketch007 [N_Axis]
  Refine = true
  Suppressed = false
  Type = 0
FEATURE [PartDesign::Body] Body005
  AllowCompound = false
  Group = -> [Sketch006,Pad005,Sketch007,Pocket001]
  Origin = -> Origin005
  Tip = -> Pocket001
FEATURE [Part::FeaturePython] Clone  label="foot1_clone"  # Draft clone (typed FeaturePython)
  AttacherType = Attacher::AttachEngine3D
  Fuse = false
  Objects = -> [Body]
  Scale = (1,1,1)
FEATURE [Part::FeaturePython] Clone001  label="foot2_clone"  # Draft clone (typed FeaturePython)
  AttacherType = Attacher::AttachEngine3D
  Fuse = false
  Objects = -> [Body001]
  Scale = (1,1,1)
FEATURE [Part::FeaturePython] Clone002  label="foot3_clone"  # Draft clone (typed FeaturePython)
  AttacherType = Attacher::AttachEngine3D
  Fuse = false
  Objects = -> [Body002]
  Scale = (1,1,1)
FEATURE [Part::FeaturePython] Clone003  label="foot4_clone"  # Draft clone (typed FeaturePython)
  AttacherType = Attacher::AttachEngine3D
  Fuse = false
  Objects = -> [Body003]
  Scale = (1,1,1)
FEATURE [Part::FeaturePython] Clone004  label="plate1_clone"  # Draft clone (typed FeaturePython)
  AttacherType = Attacher::AttachEngine3D
  Fuse = false
  Objects = -> [Body004]
  Scale = (1,1,1)
FEATURE [Part::FeaturePython] Clone005  label="plate2_clone"  # Draft clone (typed FeaturePython)
  AttacherType = Attacher::AttachEngine3D
  Fuse = false
  Objects = -> [Body005]
  Scale = (1,1,1)
FEATURE [App::Part] Part  label="table02"
  Group = -> [Clone,Clone001,Clone002,Clone003,Clone004,Clone005]
  Origin = -> Origin006
---- part ../toasteroven/toasteroven.FCStd = doc fcstd_155c2a613932 ----
FCSTD DOCUMENT  (FreeCAD 1.0R39109 (Git))
Label: toasteroven
License: All rights reserved
LicenseURL: https://en.wikipedia.org/wiki/All_rights_reserved
objects: Sketcher::SketchObject×24, PartDesign::Pad×14, PartDesign::Fillet×14, PartDesign::ShapeBinder×13, PartDesign::Pocket×10, PartDesign::Line×8, PartDesign::Body×6, Part::FeaturePython×6, PartDesign::Plane×2, App::Part×1
note: 197 computed .brp shape members not serialized (recipe doc carries the construction recipe); baked Part::Feature solids carry a one-line shape summary decoded from their .brp

FEATURE [Sketcher::SketchObject] Sketch
  ArcFitTolerance = 1e-06
  AttachmentSupport = -> [XY_Plane]
  FullyConstrained = true
  MakeInternals = false
  MapMode = 5
  sketch-geometry (5):
    g0: LineSegment StartX=-250 StartY=-230 StartZ=0 EndX=250 EndY=-230 EndZ=0
    g1: LineSegment StartX=250 StartY=-230 StartZ=0 EndX=250 EndY=230 EndZ=0
    g2: LineSegment StartX=250 StartY=230 StartZ=0 EndX=-250 EndY=230 EndZ=0
    g3: LineSegment StartX=-250 StartY=230 StartZ=0 EndX=-250 EndY=-230 EndZ=0
    g4: GeomPoint [constr] X=0 Y=0 Z=0
  constraints (12):
    c: Coincident(g0,g1)
    c: Coincident(g1,g2)
    c: Coincident(g2,g3)
    c: Coincident(g3,g0)
    c: Horizontal(g0)
    c: Horizontal(g2)
    c: Vertical(g1)
    c: Vertical(g3)
    c: Symmetric(g2,g0,g4)
    c: Distance(g1,g3) = 500
    c: Distance(g0,g2) = 460
    c: Coincident(g4,g-1)
FEATURE [PartDesign::Pad] Pad
  Direction = (0,0,1)
  Length = 14
  Length2 = 10
  Profile = -> Sketch
  ReferenceAxis = -> Sketch [N_Axis]
  Refine = true
  Suppressed = false
  Type = 0
FEATURE [Sketcher::SketchObject] Sketch001
  ArcFitTolerance = 1e-06
  AttachmentSupport = -> [Pad]
  FullyConstrained = true
  MakeInternals = false
  MapMode = 5
  Placement = pos=(0,0,14) rot=(0,0,1;0rad)
  sketch-geometry (5):
    g0: LineSegment StartX=-254.5 StartY=-234 StartZ=0 EndX=254.5 EndY=-234 EndZ=0
    g1: LineSegment StartX=254.5 StartY=-234 StartZ=0 EndX=254.5 EndY=234 EndZ=0
    g2: LineSegment StartX=254.5 StartY=234 StartZ=0 EndX=-254.5 EndY=234 EndZ=0
    g3: LineSegment StartX=-254.5 StartY=234 StartZ=0 EndX=-254.5 EndY=-234 EndZ=0
    g4: GeomPoint [constr] X=0 Y=0 Z=0
  constraints (12):
    c: Coincident(g0,g1)
    c: Coincident(g1,g2)
    c: Coincident(g2,g3)
    c: Coincident(g3,g0)
    c: Horizontal(g0)
    c: Horizontal(g2)
    c: Vertical(g1)
    c: Vertical(g3)
    c: Symmetric(g2,g0,g4)
    c: Distance(g1,g3) = 509
    c: Distance(g0,g2) = 468
    c: Coincident(g4,g-1)
FEATURE [PartDesign::Pad] Pad001
  BaseFeature = -> Pad
  Direction = (0,0,1)
  Length = 400
  Length2 = 10
  Profile = -> Sketch001
  ReferenceAxis = -> Sketch001 [N_Axis]
  Refine = true
  Suppressed = false
  Type = 0
FEATURE [Sketcher::SketchObject] Sketch002
  ArcFitTolerance = 1e-06
  AttachmentSupport = -> [Pad001]
  ExternalGeometry = -> [Pad001]
  FullyConstrained = false
  MakeInternals = false
  MapMode = 5
  Placement = pos=(0,-234,0) rot=(1,0,0;1.5708rad)
  sketch-geometry (23):
    g0: LineSegment StartX=-254.5 StartY=414 StartZ=0 EndX=-254.5 EndY=124 EndZ=0
    g1: LineSegment StartX=-254.5 StartY=124 StartZ=0 EndX=254.5 EndY=124 EndZ=0
    g2: LineSegment StartX=254.5 StartY=124 StartZ=0 EndX=254.5 EndY=414 EndZ=0
    g3: LineSegment StartX=254.5 StartY=414 StartZ=0 EndX=-254.5 EndY=414 EndZ=0
    g4: LineSegment [constr] StartX=-254.5 StartY=124 StartZ=0 EndX=-254.5 EndY=119 EndZ=0
    g5: LineSegment StartX=-254.5 StartY=119 StartZ=0 EndX=-254.5 EndY=14 EndZ=0
    g6: LineSegment StartX=-254.5 StartY=14 StartZ=0 EndX=254.5 EndY=14 EndZ=0
    g7: LineSegment StartX=254.5 StartY=14 StartZ=0 EndX=254.5 EndY=119 EndZ=0
    g8: LineSegment StartX=254.5 StartY=119 StartZ=0 EndX=-254.5 EndY=119 EndZ=0
    g9: LineSegment StartX=-175 StartY=317.961 StartZ=0 EndX=-175 EndY=220.039 EndZ=0
    g10: LineSegment StartX=-160 StartY=205.039 StartZ=0 EndX=160 EndY=205.039 EndZ=0
    g11: LineSegment StartX=175 StartY=220.039 StartZ=0 EndX=175 EndY=317.961 EndZ=0
    g12: LineSegment StartX=160 StartY=332.961 StartZ=0 EndX=-160 EndY=332.961 EndZ=0
    g13: LineSegment [constr] StartX=0 StartY=414 StartZ=0 EndX=8.1e-15 EndY=124 EndZ=0
    g14: LineSegment [constr] StartX=-175 StartY=332.961 StartZ=0 EndX=0 EndY=269 EndZ=0
    g15: ArcOfCircle CenterX=-160 CenterY=317.961 CenterZ=0 NormalX=0 NormalY=0 NormalZ=1 AngleXU=0 Radius=15 StartAngle=1.5708 EndAngle=3.14159
    g16: GeomPoint [constr] X=-175 Y=332.961 Z=0
    g17: ArcOfCircle CenterX=-160 CenterY=220.039 CenterZ=0 NormalX=0 NormalY=0 NormalZ=1 AngleXU=0 Radius=15 StartAngle=3.14159 EndAngle=4.71239
    g18: GeomPoint [constr] X=-175 Y=205.039 Z=0
    g19: ArcOfCircle CenterX=160 CenterY=220.039 CenterZ=0 NormalX=0 NormalY=0 NormalZ=1 AngleXU=0 Radius=15 StartAngle=4.71239 EndAngle=6.28319
    g20: GeomPoint [constr] X=175 Y=205.039 Z=0
    g21: ArcOfCircle CenterX=160 CenterY=317.961 CenterZ=0 NormalX=0 NormalY=0 NormalZ=1 AngleXU=0 Radius=15 StartAngle=-1.7195e-12 EndAngle=1.5708
    g22: GeomPoint [constr] X=175 Y=332.961 Z=0
  constraints (54):
    c: Coincident(g0,g1)
    c: Coincident(g1,g2)
    c: Coincident(g2,g3)
    c: Coincident(g3,g0)
    c: Vertical(g0)
    c: Vertical(g2)
    c: Horizontal(g1)
    c: Horizontal(g3)
    c: Distance(g1,g3) = 290
    c: Coincident(g0,g-3)
    c: PointOnObject(g1,g-4)
    c: Coincident(g4,g0)
    c: PointOnObject(g4,g-3)
    c: DistanceY(g4,g4) = 5
    c: Coincident(g5,g6)
    c: Coincident(g6,g7)
    c: Coincident(g7,g8)
    c: Coincident(g8,g5)
    c: Vertical(g5)
    c: Vertical(g7)
    c: Horizontal(g6)
    c: Horizontal(g8)
    c: Coincident(g5,g4)
    c: Coincident(g6,g-4)
    c: Vertical(g9)
    c: Vertical(g11)
    c: Horizontal(g10)
    c: DistanceX(g16,g22) = 350
    c: Symmetric(g16,g22,g-2)
    c: PointOnObject(g13,g-2)
    c: Symmetric(g1,g1,g13)
    c: PointOnObject(g13,g3)
    c: Coincident(g14,g16)
    c: Symmetric(g13,g13,g14)
    c: PointOnObject(g16,g12)
    c: PointOnObject(g16,g9)
    c: Tangent(g12,g15) = -1.5708
    c: Tangent(g9,g15) = -1.5708
    c: PointOnObject(g18,g10)
    c: Tangent(g9,g17) = -1.5708
    c: Tangent(g10,g17) = -1.5708
    c: PointOnObject(g20,g10)
    c: PointOnObject(g20,g11)
    c: Tangent(g10,g19) = -1.5708
    c: Tangent(g11,g19) = -1.5708
    c: PointOnObject(g22,g11)
    c: PointOnObject(g22,g12)
    c: Tangent(g11,g21) = -1.5708
    c: Tangent(g12,g21) = -1.5708
    c: Equal(g15,g17)
    c: Equal(g17,g19)
    c: Equal(g19,g21)
    c: Symmetric(g22,g18,g14)
    c: Radius(g15) = 15
FEATURE [PartDesign::Pad] Pad002
  BaseFeature = -> Pad001
  Direction = (0,-1,2e-16)
  Length = 15
  Length2 = 10
  Profile = -> Sketch002
  ReferenceAxis = -> Sketch002 [N_Axis]
  Suppressed = false
  Type = 0
FEATURE [Sketcher::SketchObject] Sketch003
  ArcFitTolerance = 1e-06
  AttachmentSupport = -> [Pad002]
  ExternalGeometry = -> [Pad002]
  FullyConstrained = false
  MakeInternals = false
  MapMode = 5
  Placement = pos=(0,-234,0) rot=(1,0,0;1.5708rad)
  sketch-geometry (14):
    g0: LineSegment [constr] StartX=-160.058 StartY=332.961 StartZ=0 EndX=-175 EndY=332.961 EndZ=0
    g1: LineSegment [constr] StartX=175 StartY=220.08 StartZ=0 EndX=175 EndY=205.039 EndZ=0
    g2: LineSegment [constr] StartX=160 StartY=205.039 StartZ=0 EndX=175 EndY=205.039 EndZ=0
    g3: LineSegment [constr] StartX=-175 StartY=317.961 StartZ=0 EndX=-175 EndY=332.961 EndZ=0
    g4: LineSegment StartX=-175 StartY=317.961 StartZ=0 EndX=-175 EndY=220.039 EndZ=0
    g5: LineSegment StartX=-160 StartY=205.039 StartZ=0 EndX=160 EndY=205.039 EndZ=0
    g6: LineSegment StartX=175 StartY=220.039 StartZ=0 EndX=175 EndY=317.961 EndZ=0
    g7: LineSegment StartX=160 StartY=332.961 StartZ=0 EndX=-160 EndY=332.961 EndZ=0
    g8: ArcOfCircle CenterX=-160 CenterY=317.961 CenterZ=0 NormalX=0 NormalY=0 NormalZ=1 AngleXU=0 Radius=15 StartAngle=1.5708 EndAngle=3.14159
    g9: ArcOfCircle CenterX=-160 CenterY=220.039 CenterZ=0 NormalX=0 NormalY=0 NormalZ=1 AngleXU=0 Radius=15 StartAngle=3.14159 EndAngle=4.71239
    g10: ArcOfCircle CenterX=160 CenterY=220.039 CenterZ=0 NormalX=0 NormalY=0 NormalZ=1 AngleXU=0 Radius=15 StartAngle=4.71239 EndAngle=6.28319
    g11: ArcOfCircle CenterX=160 CenterY=317.961 CenterZ=0 NormalX=0 NormalY=0 NormalZ=1 AngleXU=0 Radius=15 StartAngle=0 EndAngle=1.5708
    g12: GeomPoint [constr] X=-175 Y=332.961 Z=0
    g13: GeomPoint [constr] X=175 Y=205.039 Z=0
  constraints (30):
    c: Coincident(g2,g-6)
    c: Horizontal(g2)
    c: Vertical(g1)
    c: Coincident(g1,g2)
    c: Coincident(g3,g-4)
    c: Vertical(g3)
    c: Horizontal(g0)
    c: Coincident(g0,g3)
    c: Tangent(g4,g8) = -1.5708
    c: Tangent(g4,g9) = -1.5708
    c: Tangent(g5,g9) = -1.5708
    c: Tangent(g5,g10) = -1.5708
    c: Tangent(g6,g10) = -1.5708
    c: Tangent(g6,g11) = -1.5708
    c: Tangent(g7,g11) = -1.5708
    c: Tangent(g7,g8) = -1.5708
    c: Vertical(g4)
    c: Vertical(g6)
    c: Horizontal(g5)
    c: Horizontal(g7)
    c: Equal(g8,g9)
    c: Equal(g9,g10)
    c: Equal(g10,g11)
    c: PointOnObject(g12,g4)
    c: PointOnObject(g12,g7)
    c: PointOnObject(g13,g5)
    c: PointOnObject(g13,g6)
    c: Radius(g9) = 15
    c: Coincident(g12,g0)
    c: Coincident(g13,g1)
FEATURE [PartDesign::Pad] Pad003
  BaseFeature = -> Pad002
  Direction = (0,-1,2e-16)
  Length = 15
  Length2 = 10
  Profile = -> Sketch003
  ReferenceAxis = -> Sketch003 [N_Axis]
  Suppressed = false
  Type = 0
FEATURE [Sketcher::SketchObject] Sketch004
  ArcFitTolerance = 1e-06
  AttachmentSupport = -> [Pad003]
  ExternalGeometry = -> [Pad003]
  FullyConstrained = false
  MakeInternals = false
  MapMode = 5
  Placement = pos=(0,-249,0) rot=(1,0,0;1.5708rad)
  sketch-geometry (6):
    g0: LineSegment StartX=-111.613 StartY=386.284 StartZ=0 EndX=-111.613 EndY=360.677 EndZ=0
    g1: LineSegment StartX=-111.613 StartY=360.677 StartZ=0 EndX=111.814 EndY=360.677 EndZ=0
    g2: LineSegment StartX=111.814 StartY=360.677 StartZ=0 EndX=111.814 EndY=386.284 EndZ=0
    g3: LineSegment StartX=111.814 StartY=386.284 StartZ=0 EndX=-111.613 EndY=386.284 EndZ=0
    g4: LineSegment [constr] StartX=0.100445 StartY=414 StartZ=0 EndX=0.100445 EndY=332.961 EndZ=0
    g5: LineSegment [constr] StartX=-111.613 StartY=386.284 StartZ=0 EndX=0.100445 EndY=373.481 EndZ=0
  constraints (14):
    c: Coincident(g0,g1)
    c: Coincident(g1,g2)
    c: Coincident(g2,g3)
    c: Coincident(g3,g0)
    c: Vertical(g0)
    c: Vertical(g2)
    c: Horizontal(g1)
    c: Horizontal(g3)
    c: Vertical(g4)
    c: PointOnObject(g4,g-4)
    c: PointOnObject(g4,g-3)
    c: Coincident(g5,g0)
    c: Symmetric(g4,g4,g5)
    c: Symmetric(g0,g2,g5)
FEATURE [PartDesign::Pad] Pad004
  BaseFeature = -> Pad003
  Direction = (0,-1,2e-16)
  Length = 50
  Length2 = 10
  Profile = -> Sketch004
  ReferenceAxis = -> Sketch004 [N_Axis]
  Suppressed = false
  Type = 0
FEATURE [Sketcher::SketchObject] Sketch005
  ArcFitTolerance = 1e-06
  AttachmentSupport = -> [Pad004]
  ExternalGeometry = -> [Pad004]
  FullyConstrained = false
  MakeInternals = false
  MapMode = 5
  Placement = pos=(0,8.5e-14,386.284) rot=(0,0,1;0rad)
  sketch-geometry (13):
    g0: LineSegment StartX=-92.1016 StartY=-250.2 StartZ=0 EndX=-92.1016 EndY=-274.605 EndZ=0
    g1: LineSegment StartX=-82.1016 StartY=-284.605 StartZ=0 EndX=82.1016 EndY=-284.605 EndZ=0
    g2: LineSegment StartX=92.1016 StartY=-274.605 StartZ=0 EndX=92.1016 EndY=-250.713 EndZ=0
    g3: LineSegment StartX=91.1044 StartY=-249.713 StartZ=0 EndX=-91.0988 EndY=-249.2 EndZ=0
    g4: ArcOfCircle CenterX=-82.1016 CenterY=-274.605 CenterZ=0 NormalX=0 NormalY=0 NormalZ=1 AngleXU=0 Radius=10 StartAngle=3.14159 EndAngle=4.71239
    g5: GeomPoint [constr] X=-92.1016 Y=-284.605 Z=0
    g6: ArcOfCircle CenterX=82.1016 CenterY=-274.605 CenterZ=0 NormalX=0 NormalY=0 NormalZ=1 AngleXU=0 Radius=10 StartAngle=4.71239 EndAngle=6.28319
    g7: GeomPoint [constr] X=92.1016 Y=-284.605 Z=0
    g8: ArcOfCircle CenterX=-91.1016 CenterY=-250.2 CenterZ=0 NormalX=0 NormalY=0 NormalZ=1 AngleXU=0 Radius=1 StartAngle=1.56798 EndAngle=3.14159
    g9: GeomPoint [constr] X=-92.1012 Y=-249 Z=0
    g10: ArcOfCircle CenterX=91.1016 CenterY=-250.713 CenterZ=0 NormalX=0 NormalY=0 NormalZ=1 AngleXU=0 Radius=1 StartAngle=7.3e-15 EndAngle=1.56798
    g11: GeomPoint [constr] X=92.1012 Y=-249 Z=0
    g12: LineSegment [constr] StartX=-91.0988 StartY=-249.2 StartZ=0 EndX=-91.0988 EndY=-249 EndZ=0
  constraints (23):
    c: Vertical(g0)
    c: Vertical(g2)
    c: Symmetric(g5,g7,g-2)
    c: PointOnObject(g5,g0)
    c: PointOnObject(g5,g1)
    c: Tangent(g0,g4) = -1.5708
    c: Tangent(g1,g4) = -1.5708
    c: PointOnObject(g7,g1)
    c: PointOnObject(g7,g2)
    c: Tangent(g1,g6) = -1.5708
    c: Tangent(g2,g6) = -1.5708
    c: Equal(g6,g4)
    c: Radius(g6) = 10
    c: Tangent(g3,g8) = -1.5708
    c: Tangent(g0,g8) = -1.5708
    c: Tangent(g3,g10) = -1.5708
    c: Tangent(g2,g10) = -1.5708
    c: Equal(g10,g8)
    c: Radius(g10) = 1
    c: Coincident(g12,g3)
    c: Vertical(g12)
    c: PointOnObject(g12,g-3)
    c: DistanceY(g12,g12) = 0.2
FEATURE [PartDesign::Pocket] Pocket
  BaseFeature = -> Pad004
  Direction = (0,0,-1)
  Length = 5
  Length2 = 5
  Profile = -> Sketch005
  ReferenceAxis = -> Sketch005 [N_Axis]
  Suppressed = false
  Type = 1
FEATURE [Sketcher::SketchObject] Sketch006
  ArcFitTolerance = 1e-06
  AttachmentSupport = -> [Pocket]
  ExternalGeometry = -> [Pocket]
  FullyConstrained = false
  MakeInternals = false
  MapMode = 5
  Placement = pos=(0,-249,0) rot=(1,0,0;1.5708rad)
  sketch-geometry (4):
    g0: Circle CenterX=162.576 CenterY=66.5 CenterZ=0 NormalX=0 NormalY=0 NormalZ=1 AngleXU=0 Radius=35
    g1: Circle CenterX=18.3518 CenterY=66.5 CenterZ=0 NormalX=0 NormalY=0 NormalZ=1 AngleXU=0 Radius=35
    g2: LineSegment [constr] StartX=18.3518 StartY=66.5 StartZ=0 EndX=18.3518 EndY=119 EndZ=0
    g3: LineSegment [constr] StartX=18.3518 StartY=66.5 StartZ=0 EndX=18.3518 EndY=14 EndZ=0
  constraints (9):
    c: Equal(g0,g1)
    c: Radius(g1) = 35
    c: Coincident(g2,g1)
    c: Vertical(g2)
    c: Coincident(g3,g1)
    c: PointOnObject(g2,g-3)
    c: PointOnObject(g3,g-4)
    c: Symmetric(g2,g3,g1)
    c: Horizontal(g0,g1)
FEATURE [PartDesign::Pocket] Pocket001
  BaseFeature = -> Pocket
  Direction = (0,1,-2e-16)
  Length = 14
  Length2 = 5
  Profile = -> Sketch006
  ReferenceAxis = -> Sketch006 [N_Axis]
  Suppressed = false
  Type = 0
FEATURE [Sketcher::SketchObject] Sketch007
  ArcFitTolerance = 1e-06
  AttachmentSupport = -> [Pocket001]
  ExternalGeometry = -> [Pocket001]
  FullyConstrained = true
  MakeInternals = false
  MapMode = 5
  Placement = pos=(0,-235,1.105e-13) rot=(1,0,0;1.5708rad)
  sketch-geometry (2):
    g0: Circle CenterX=18.3518 CenterY=66.5 CenterZ=0 NormalX=0 NormalY=0 NormalZ=1 AngleXU=0 Radius=30
    g1: Circle CenterX=162.576 CenterY=66.5 CenterZ=0 NormalX=0 NormalY=0 NormalZ=1 AngleXU=0 Radius=30
  constraints (4):
    c: Diameter(g0) = 60
    c: Coincident(g0,g-3)
    c: Diameter(g1) = 60
    c: Coincident(g1,g-4)
FEATURE [PartDesign::Pad] Pad005
  BaseFeature = -> Pocket001
  Direction = (0,-1,2e-16)
  Length = 15
  Length2 = 10
  Profile = -> Sketch007
  ReferenceAxis = -> Sketch007 [N_Axis]
  Suppressed = false
  Type = 0
FEATURE [Sketcher::SketchObject] Sketch008
  ArcFitTolerance = 1e-06
  AttachmentSupport = -> [Pad005]
  ExternalGeometry = -> [Pad005]
  FullyConstrained = false
  MakeInternals = false
  MapMode = 5
  Placement = pos=(0,-250,1.375e-13) rot=(1,0,0;1.5708rad)
  sketch-geometry (8):
    g0: ArcOfCircle CenterX=18.3518 CenterY=89.5 CenterZ=0 NormalX=0 NormalY=0 NormalZ=1 AngleXU=0 Radius=5.5429 StartAngle=1.2e-15 EndAngle=3.14159
    g1: ArcOfCircle CenterX=18.3518 CenterY=43.5 CenterZ=0 NormalX=0 NormalY=0 NormalZ=1 AngleXU=0 Radius=5.5429 StartAngle=3.14159 EndAngle=6.28319
    g2: LineSegment StartX=23.8947 StartY=89.5 StartZ=0 EndX=23.8947 EndY=43.5 EndZ=0
    g3: LineSegment StartX=12.8089 StartY=89.5 StartZ=0 EndX=12.8089 EndY=43.5 EndZ=0
    g4: ArcOfCircle CenterX=162.576 CenterY=89.5 CenterZ=0 NormalX=0 NormalY=0 NormalZ=1 AngleXU=0 Radius=5.5429 StartAngle=-9e-16 EndAngle=3.14159
    g5: ArcOfCircle CenterX=162.576 CenterY=43.5 CenterZ=0 NormalX=0 NormalY=0 NormalZ=1 AngleXU=0 Radius=5.5429 StartAngle=3.14159 EndAngle=6.28319
    g6: LineSegment StartX=168.119 StartY=89.5 StartZ=0 EndX=168.119 EndY=43.5 EndZ=0
    g7: LineSegment StartX=157.033 StartY=89.5 StartZ=0 EndX=157.033 EndY=43.5 EndZ=0
  constraints (17):
    c: Tangent(g0,g2) = 1.5708
    c: Tangent(g0,g3) = -1.5708
    c: Tangent(g1,g2) = 1.5708
    c: Tangent(g1,g3) = -1.5708
    c: Equal(g0,g1)
    c: Vertical(g2)
    c: Tangent(g4,g6) = 1.5708
    c: Tangent(g4,g7) = -1.5708
    c: Tangent(g5,g6) = 1.5708
    c: Tangent(g5,g7) = -1.5708
    c: Equal(g4,g5)
    c: Symmetric(g0,g1,g-3)
    c: Symmetric(g4,g5,g-4)
    c: Vertical(g4,g5)
    c: Equal(g7,g3)
    c: Equal(g0,g4)
    c: DistanceY(g3,g3) = 46
FEATURE [PartDesign::Pad] Pad006
  BaseFeature = -> Pad005
  Direction = (0,-1,2e-16)
  Length = 15
  Length2 = 10
  Profile = -> Sketch008
  ReferenceAxis = -> Sketch008 [N_Axis]
  Suppressed = false
  Type = 0
FEATURE [Sketcher::SketchObject] Sketch009
  ArcFitTolerance = 1e-06
  AttachmentSupport = -> [Pad001]
  FullyConstrained = false
  MakeInternals = false
  MapMode = 5
  Placement = pos=(0,-234,0) rot=(1,0,0;1.5708rad)
  sketch-geometry (4):
    g0: LineSegment StartX=-227.24 StartY=377.791 StartZ=0 EndX=-227.24 EndY=190.77 EndZ=0
    g1: LineSegment StartX=-227.24 StartY=190.77 StartZ=0 EndX=227.24 EndY=190.77 EndZ=0
    g2: LineSegment StartX=227.24 StartY=190.77 StartZ=0 EndX=227.24 EndY=377.791 EndZ=0
    g3: LineSegment StartX=227.24 StartY=377.791 StartZ=0 EndX=-227.24 EndY=377.791 EndZ=0
  constraints (8):
    c: Coincident(g0,g1)
    c: Coincident(g1,g2)
    c: Coincident(g2,g3)
    c: Coincident(g3,g0)
    c: Vertical(g0)
    c: Vertical(g2)
    c: Horizontal(g1)
    c: Symmetric(g0,g2,g-2)
FEATURE [PartDesign::Pocket] Pocket002
  BaseFeature = -> Pad006
  Direction = (0,1,-2e-16)
  Length = 450
  Length2 = 5
  Profile = -> Sketch009
  ReferenceAxis = -> Sketch009 [N_Axis]
  Suppressed = false
  Type = 0
FEATURE [PartDesign::Fillet] Fillet
  Base = -> Pocket002 [Edge13,Edge14]
  BaseFeature = -> Pocket002
  Radius = 3
  SupportTransform = false
  Suppressed = false
  UseAllEdges = false
FEATURE [PartDesign::Fillet] Fillet001
  Base = -> Fillet [Edge45,Edge38]
  BaseFeature = -> Fillet
  Radius = 40
  SupportTransform = false
  Suppressed = false
  UseAllEdges = false
FEATURE [PartDesign::Fillet] Fillet002
  Base = -> Fillet001 [Edge79,Edge80]
  BaseFeature = -> Fillet001
  Radius = 5
  SupportTransform = false
  Suppressed = false
  UseAllEdges = false
FEATURE [PartDesign::Fillet] Fillet003
  Base = -> Fillet002 [Edge74,Edge94]
  BaseFeature = -> Fillet002
  Radius = 2
  SupportTransform = false
  Suppressed = false
  UseAllEdges = false
FEATURE [PartDesign::Fillet] Fillet004
  Base = -> Fillet003 [Edge33,Edge181]
  BaseFeature = -> Fillet003
  Radius = 3
  SupportTransform = false
  Suppressed = false
  UseAllEdges = false
FEATURE [PartDesign::Fillet] Fillet005
  Base = -> Fillet004 [Edge158,Edge147]
  BaseFeature = -> Fillet004
  Radius = 10
  SupportTransform = false
  Suppressed = false
  UseAllEdges = false
FEATURE [PartDesign::Fillet] Fillet006
  Base = -> Fillet005 [Edge4]
  BaseFeature = -> Fillet005
  Radius = 5
  SupportTransform = false
  Suppressed = false
  UseAllEdges = false
FEATURE [PartDesign::Fillet] Fillet007
  Base = -> Fillet006 [Edge14]
  BaseFeature = -> Fillet006
  Radius = 5
  SupportTransform = false
  Suppressed = false
  UseAllEdges = false
FEATURE [Sketcher::SketchObject] Sketch010
  ArcFitTolerance = 1e-06
  AttachmentSupport = -> [Fillet007]
  ExternalGeometry = -> [Fillet007]
  FullyConstrained = false
  MakeInternals = false
  MapMode = 5
  Placement = pos=(0,-249,0) rot=(1,0,0;1.5708rad)
  sketch-geometry (14):
    g0: LineSegment [constr] StartX=-160 StartY=332.961 StartZ=0 EndX=-175 EndY=332.961 EndZ=0
    g1: LineSegment [constr] StartX=-175 StartY=317.961 StartZ=0 EndX=-175 EndY=332.961 EndZ=0
    g2: LineSegment [constr] StartX=175 StartY=220.039 StartZ=0 EndX=175 EndY=205.039 EndZ=0
    g3: LineSegment [constr] StartX=160 StartY=205.039 StartZ=0 EndX=175 EndY=205.039 EndZ=0
    g4: LineSegment StartX=-175 StartY=317.961 StartZ=0 EndX=-175 EndY=220.039 EndZ=0
    g5: LineSegment StartX=-160 StartY=205.039 StartZ=0 EndX=160 EndY=205.039 EndZ=0
    g6: LineSegment StartX=175 StartY=220.039 StartZ=0 EndX=175 EndY=317.961 EndZ=0
    g7: LineSegment StartX=160 StartY=332.961 StartZ=0 EndX=-160 EndY=332.961 EndZ=0
    g8: ArcOfCircle CenterX=-160 CenterY=317.961 CenterZ=0 NormalX=0 NormalY=0 NormalZ=1 AngleXU=0 Radius=15 StartAngle=1.5708 EndAngle=3.14159
    g9: ArcOfCircle CenterX=-160 CenterY=220.039 CenterZ=0 NormalX=0 NormalY=0 NormalZ=1 AngleXU=0 Radius=15 StartAngle=3.14159 EndAngle=4.71239
    g10: ArcOfCircle CenterX=160 CenterY=220.039 CenterZ=0 NormalX=0 NormalY=0 NormalZ=1 AngleXU=0 Radius=15 StartAngle=4.71239 EndAngle=6.28319
    g11: ArcOfCircle CenterX=160 CenterY=317.961 CenterZ=0 NormalX=0 NormalY=0 NormalZ=1 AngleXU=0 Radius=15 StartAngle=0 EndAngle=1.5708
    g12: GeomPoint [constr] X=-175 Y=332.961 Z=0
    g13: GeomPoint [constr] X=175 Y=205.039 Z=0
  constraints (31):
    c: Coincident(g0,g-3)
    c: Horizontal(g0)
    c: Coincident(g1,g-4)
    c: Vertical(g1)
    c: Coincident(g0,g1)
    c: Coincident(g2,g-5)
    c: Vertical(g2)
    c: Coincident(g3,g-6)
    c: Horizontal(g3)
    c: Coincident(g2,g3)
    c: Tangent(g4,g8) = -1.5708
    c: Tangent(g4,g9) = -1.5708
    c: Tangent(g5,g9) = -1.5708
    c: Tangent(g5,g10) = -1.5708
    c: Tangent(g6,g10) = -1.5708
    c: Tangent(g6,g11) = -1.5708
    c: Tangent(g7,g11) = -1.5708
    c: Tangent(g7,g8) = -1.5708
    c: Vertical(g4)
    c: Vertical(g6)
    c: Horizontal(g5)
    c: Horizontal(g7)
    c: Equal(g8,g9)
    c: Equal(g9,g10)
    c: Equal(g10,g11)
    c: PointOnObject(g12,g4)
    c: PointOnObject(g12,g7)
    c: PointOnObject(g13,g5)
    c: PointOnObject(g13,g6)
    c: Coincident(g12,g0)
    c: Coincident(g13,g2)
FEATURE [PartDesign::Pocket] Pocket003
  BaseFeature = -> Fillet007
  Direction = (0,1,-2e-16)
  Length = 30
  Length2 = 5
  Profile = -> Sketch010
  ReferenceAxis = -> Sketch010 [N_Axis]
  Refine = true
  Suppressed = false
  Type = 0
FEATURE [PartDesign::ShapeBinder] CopyPocket003
  Placement = pos=(0,-235,1.1e-13) rot=(1,0,0;1.5708rad)
  TraceSupport = false
FEATURE [PartDesign::Plane] DatumPlane
  AttachmentSupport = -> [CopyPocket003]
  Length = 105.028
  MapMode = 11
  Placement = pos=(18.3518,-235,66.5) rot=(0.57735,-0.57735,0.57735;2.0944rad)
  ResizeMode = 0
  Width = 63.5277
FEATURE [Sketcher::SketchObject] Sketch011
  ArcFitTolerance = 1e-06
  AttachmentSupport = -> [DatumPlane]
  ExternalGeometry = -> [CopyPocket003]
  FullyConstrained = false
  MakeInternals = false
  MapMode = 5
  Placement = pos=(18.3518,-235,66.5) rot=(0.57735,-0.57735,0.57735;2.0944rad)
  sketch-geometry (1):
    g0: Circle CenterX=0 CenterY=0 CenterZ=0 NormalX=0 NormalY=0 NormalZ=1 AngleXU=0 Radius=30
  constraints (1):
    c: Coincident(g0,g-1)
FEATURE [PartDesign::Pad] Pad007
  Direction = (0,-1,0)
  Length = 15
  Length2 = 10
  Placement = pos=(18.3518,-235,66.5) rot=(0.57735,-0.57735,0.57735;2.0944rad)
  Profile = -> Sketch011
  ReferenceAxis = -> Sketch011 [N_Axis]
  Refine = true
  Suppressed = false
  Type = 0
FEATURE [PartDesign::ShapeBinder] CopyPocket004
  Placement = pos=(0,-250,1.37e-13) rot=(1,0,0;1.5708rad)
  TraceSupport = false
FEATURE [PartDesign::Line] DatumLine
  AttacherType = Attacher::AttachEngineLine
  AttachmentSupport = -> [CopyPocket004]
  Length = 20
  MapMode = 29
  Placement = pos=(12.8089,-250,1.421e-13) rot=(0,1,0;3.14159rad)
  ResizeMode = 0
FEATURE [PartDesign::ShapeBinder] CopyPocket005
  TraceSupport = false
FEATURE [PartDesign::Line] DatumLine001
  AttacherType = Attacher::AttachEngineLine
  AttachmentSupport = -> [CopyPocket005]
  Length = 20
  MapMode = 19
  Placement = pos=(18.3518,-262,89.5) rot=(0,0.707107,0.707107;3.14159rad)
  ResizeMode = 0
FEATURE [PartDesign::ShapeBinder] CopyPocket006
  TraceSupport = false
FEATURE [PartDesign::Line] DatumLine002
  AttacherType = Attacher::AttachEngineLine
  AttachmentSupport = -> [CopyPocket006]
  Length = 20
  MapMode = 19
  Placement = pos=(18.3518,-262,43.5) rot=(-1,0,0;1.5708rad)
  ResizeMode = 0
FEATURE [PartDesign::ShapeBinder] CopyPocket007
  Placement = pos=(0,-250,1.37e-13) rot=(1,0,0;1.5708rad)
  TraceSupport = false
FEATURE [PartDesign::Line] DatumLine003
  AttacherType = Attacher::AttachEngineLine
  AttachmentSupport = -> [CopyPocket007]
  Length = 20
  MapMode = 29
  Placement = pos=(23.8947,-250,1.421e-13) rot=(0,1,0;3.14159rad)
  ResizeMode = 0
FEATURE [Sketcher::SketchObject] Sketch012
  ArcFitTolerance = 1e-06
  AttachmentSupport = -> [Pad007]
  ExternalGeometry = -> [DatumLine,DatumLine003,CopyPocket005,CopyPocket006]
  FullyConstrained = false
  MakeInternals = false
  MapMode = 5
  Placement = pos=(18.3518,-250,66.5) rot=(0.57735,-0.57735,0.57735;2.0944rad)
  sketch-geometry (4):
    g0: ArcOfCircle CenterX=-23 CenterY=-1.851e-13 CenterZ=0 NormalX=0 NormalY=0 NormalZ=1 AngleXU=0 Radius=5.5429 StartAngle=1.5708 EndAngle=4.71239
    g1: ArcOfCircle CenterX=23 CenterY=-1.851e-13 CenterZ=0 NormalX=0 NormalY=0 NormalZ=1 AngleXU=0 Radius=5.5429 StartAngle=4.71239 EndAngle=7.85398
    g2: LineSegment StartX=-23 StartY=5.5429 StartZ=0 EndX=23 EndY=5.5429 EndZ=0
    g3: LineSegment StartX=-23 StartY=-5.5429 StartZ=0 EndX=23 EndY=-5.5429 EndZ=0
  constraints (6):
    c: Tangent(g0,g2) = 1.5708
    c: Tangent(g0,g3) = -1.5708
    c: Tangent(g1,g2) = 1.5708
    c: Tangent(g1,g3) = -1.5708
    c: Equal(g0,g1)
    c: Horizontal(g3)
FEATURE [PartDesign::Pad] Pad008
  BaseFeature = -> Pad007
  Direction = (0,-1,0)
  Length = 15
  Length2 = 10
  Placement = pos=(18.3518,-235,66.5) rot=(0.57735,-0.57735,0.57735;2.0944rad)
  Profile = -> Sketch012
  ReferenceAxis = -> Sketch012 [N_Axis]
  Refine = true
  Suppressed = false
  Type = 0
FEATURE [PartDesign::Fillet] Fillet008
  Base = -> Pad008 [Edge3]
  BaseFeature = -> Pad008
  Placement = pos=(18.3518,-235,66.5) rot=(0.57735,-0.57735,0.57735;2.0944rad)
  Radius = 2
  Refine = true
  SupportTransform = false
  Suppressed = false
  UseAllEdges = false
FEATURE [PartDesign::Fillet] Fillet009
  Base = -> Fillet008 [Edge31]
  BaseFeature = -> Fillet008
  Placement = pos=(18.3518,-235,66.5) rot=(0.57735,-0.57735,0.57735;2.0944rad)
  Radius = 3
  Refine = true
  SupportTransform = false
  Suppressed = false
  UseAllEdges = false
FEATURE [PartDesign::Body] Body001
  AllowCompound = false
  Group = -> [DatumPlane,CopyPocket003,Sketch011,Pad007,DatumLine,CopyPocket004,DatumLine001,CopyPocket005,DatumLine002,CopyPocket006,DatumLine003,CopyPocket007,Sketch012,Pad008,Fillet008,Fillet009]
  Origin = -> Origin001
  Tip = -> Fillet009
FEATURE [PartDesign::ShapeBinder] CopyPocket008
  Placement = pos=(0,-235,1.1e-13) rot=(1,0,0;1.5708rad)
  TraceSupport = false
FEATURE [PartDesign::Plane] DatumPlane001
  AttachmentSupport = -> [CopyPocket008]
  Length = 117.702
  MapMode = 11
  Placement = pos=(162.576,-235,66.5) rot=(0.57735,-0.57735,0.57735;2.0944rad)
  ResizeMode = 0
  Width = 213.778
FEATURE [PartDesign::ShapeBinder] CopyPocket009
  TraceSupport = false
FEATURE [PartDesign::Line] DatumLine004
  AttacherType = Attacher::AttachEngineLine
  AttachmentSupport = -> [CopyPocket009]
  Length = 20
  MapMode = 29
  Placement = pos=(157.033,-262,0) rot=(0,0,1;0rad)
  ResizeMode = 0
FEATURE [PartDesign::ShapeBinder] CopyPocket010
  TraceSupport = false
FEATURE [PartDesign::Line] DatumLine005
  AttacherType = Attacher::AttachEngineLine
  AttachmentSupport = -> [CopyPocket010]
  Length = 20
  MapMode = 19
  Placement = pos=(162.576,-262,89.5) rot=(0,0.707107,0.707107;3.14159rad)
  ResizeMode = 0
FEATURE [PartDesign::ShapeBinder] CopyPocket011
  TraceSupport = false
FEATURE [PartDesign::Line] DatumLine006
  AttacherType = Attacher::AttachEngineLine
  AttachmentSupport = -> [CopyPocket011]
  Length = 20
  MapMode = 29
  Placement = pos=(168.119,-262,0) rot=(0,1,0;3.14159rad)
  ResizeMode = 0
FEATURE [PartDesign::ShapeBinder] CopyPocket012
  TraceSupport = false
FEATURE [PartDesign::Line] DatumLine007
  AttacherType = Attacher::AttachEngineLine
  AttachmentSupport = -> [CopyPocket012]
  Length = 20
  MapMode = 19
  Placement = pos=(162.576,-262,43.5) rot=(-1,0,0;1.5708rad)
  ResizeMode = 0
FEATURE [Sketcher::SketchObject] Sketch013
  ArcFitTolerance = 1e-06
  AttachmentSupport = -> [DatumPlane001]
  ExternalGeometry = -> [CopyPocket008]
  FullyConstrained = false
  MakeInternals = false
  MapMode = 5
  Placement = pos=(162.576,-235,66.5) rot=(0.57735,-0.57735,0.57735;2.0944rad)
  sketch-geometry (1):
    g0: Circle CenterX=0 CenterY=0 CenterZ=0 NormalX=0 NormalY=0 NormalZ=1 AngleXU=0 Radius=30
  constraints (1):
    c: Coincident(g0,g-1)
FEATURE [PartDesign::Pad] Pad009
  Direction = (0,-1,0)
  Length = 15
  Length2 = 10
  Placement = pos=(162.576,-235,66.5) rot=(0.57735,-0.57735,0.57735;2.0944rad)
  Profile = -> Sketch013
  ReferenceAxis = -> Sketch013 [N_Axis]
  Refine = true
  Suppressed = false
  Type = 0
FEATURE [Sketcher::SketchObject] Sketch014
  ArcFitTolerance = 1e-06
  AttachmentSupport = -> [Pad009]
  ExternalGeometry = -> [DatumLine004,DatumLine006,CopyPocket012,CopyPocket010]
  FullyConstrained = false
  MakeInternals = false
  MapMode = 5
  Placement = pos=(162.576,-250,66.5) rot=(0.57735,-0.57735,0.57735;2.0944rad)
  sketch-geometry (4):
    g0: ArcOfCircle CenterX=-23 CenterY=-3.707e-13 CenterZ=0 NormalX=0 NormalY=0 NormalZ=1 AngleXU=0 Radius=5.5429 StartAngle=1.5708 EndAngle=4.71239
    g1: ArcOfCircle CenterX=23 CenterY=-3.707e-13 CenterZ=0 NormalX=0 NormalY=0 NormalZ=1 AngleXU=0 Radius=5.5429 StartAngle=4.71239 EndAngle=7.85398
    g2: LineSegment StartX=-23 StartY=5.5429 StartZ=0 EndX=23 EndY=5.5429 EndZ=0
    g3: LineSegment StartX=-23 StartY=-5.5429 StartZ=0 EndX=23 EndY=-5.5429 EndZ=0
  constraints (6):
    c: Tangent(g0,g2) = 1.5708
    c: Tangent(g0,g3) = -1.5708
    c: Tangent(g1,g2) = 1.5708
    c: Tangent(g1,g3) = -1.5708
    c: Equal(g0,g1)
    c: Horizontal(g3)
FEATURE [PartDesign::Pad] Pad010
  BaseFeature = -> Pad009
  Direction = (0,-1,0)
  Length = 15
  Length2 = 10
  Placement = pos=(162.576,-235,66.5) rot=(0.57735,-0.57735,0.57735;2.0944rad)
  Profile = -> Sketch014
  ReferenceAxis = -> Sketch014 [N_Axis]
  Refine = true
  Suppressed = false
  Type = 0
FEATURE [PartDesign::Fillet] Fillet010
  Base = -> Pad010 [Edge3]
  BaseFeature = -> Pad010
  Placement = pos=(162.576,-235,66.5) rot=(0.57735,-0.57735,0.57735;2.0944rad)
  Radius = 2
  Refine = true
  SupportTransform = false
  Suppressed = false
  UseAllEdges = false
FEATURE [PartDesign::Fillet] Fillet011
  Base = -> Fillet010 [Edge30]
  BaseFeature = -> Fillet010
  Placement = pos=(162.576,-235,66.5) rot=(0.57735,-0.57735,0.57735;2.0944rad)
  Radius = 3
  Refine = true
  SupportTransform = false
  Suppressed = false
  UseAllEdges = false
FEATURE [PartDesign::Body] Body002
  AllowCompound = false
  Group = -> [DatumPlane001,CopyPocket008,DatumLine004,CopyPocket009,DatumLine005,CopyPocket010,DatumLine006,CopyPocket011,DatumLine007,CopyPocket012,Sketch013,Pad009,Sketch014,Pad010,Fillet010,Fillet011]
  Origin = -> Origin002
  Tip = -> Fillet011
FEATURE [Sketcher::SketchObject] Sketch015
  ArcFitTolerance = 1e-06
  AttachmentSupport = -> [Pocket003]
  ExternalGeometry = -> [Pocket003]
  FullyConstrained = false
  MakeInternals = false
  MapMode = 5
  Placement = pos=(0,-265,1.564e-13) rot=(1,0,0;1.5708rad)
  sketch-geometry (1):
    g0: Circle CenterX=18.3518 CenterY=66.5 CenterZ=0 NormalX=0 NormalY=0 NormalZ=1 AngleXU=0 Radius=30
  constraints (1):
    c: Coincident(g0,g-4)
FEATURE [PartDesign::Pocket] Pocket004
  BaseFeature = -> Pocket003
  Direction = (0,1,-2e-16)
  Length = 30
  Length2 = 5
  Profile = -> Sketch015
  ReferenceAxis = -> Sketch015 [N_Axis]
  Refine = true
  Suppressed = false
  Type = 0
FEATURE [Sketcher::SketchObject] Sketch016
  ArcFitTolerance = 1e-06
  AttachmentSupport = -> [Pocket004]
  ExternalGeometry = -> [Pocket004]
  FullyConstrained = true
  MakeInternals = false
  MapMode = 5
  Placement = pos=(0,-265,1.564e-13) rot=(1,0,0;1.5708rad)
  sketch-geometry (1):
    g0: Circle CenterX=162.576 CenterY=66.5 CenterZ=0 NormalX=0 NormalY=0 NormalZ=1 AngleXU=0 Radius=30
  constraints (2):
    c: Coincident(g0,g-3)
    c: Equal(g0,g-3)
FEATURE [PartDesign::Pocket] Pocket005
  BaseFeature = -> Pocket004
  Direction = (0,1,-2e-16)
  Length = 30
  Length2 = 5
  Profile = -> Sketch016
  ReferenceAxis = -> Sketch016 [N_Axis]
  Refine = true
  Suppressed = false
  Type = 0
FEATURE [PartDesign::ShapeBinder] CopyPocket013
  TraceSupport = false
FEATURE [Sketcher::SketchObject] Sketch017
  ArcFitTolerance = 1e-06
  AttachmentSupport = -> [CopyPocket013]
  ExternalGeometry = -> [CopyPocket013]
  FullyConstrained = false
  MakeInternals = false
  MapMode = 5
  Placement = pos=(0,-249,0) rot=(1,0,0;1.5708rad)
  sketch-geometry (14):
    g0: LineSegment [constr] StartX=-160 StartY=332.961 StartZ=0 EndX=-175 EndY=332.895 EndZ=0
    g1: LineSegment [constr] StartX=-175 StartY=317.961 StartZ=0 EndX=-175 EndY=332.895 EndZ=0
    g2: LineSegment [constr] StartX=174.86 StartY=220.039 StartZ=0 EndX=174.86 EndY=205.023 EndZ=0
    g3: LineSegment [constr] StartX=160 StartY=205.039 StartZ=0 EndX=174.86 EndY=205.023 EndZ=0
    g4: LineSegment StartX=-175 StartY=318.234 StartZ=0 EndX=-175 EndY=219.685 EndZ=0
    g5: LineSegment StartX=-160.339 StartY=205.023 StartZ=0 EndX=160.199 EndY=205.023 EndZ=0
    g6: LineSegment StartX=174.86 StartY=219.685 StartZ=0 EndX=174.86 EndY=318.234 EndZ=0
    g7: LineSegment StartX=160.199 StartY=332.895 StartZ=0 EndX=-160.339 EndY=332.895 EndZ=0
    g8: ArcOfCircle CenterX=-160.339 CenterY=318.234 CenterZ=0 NormalX=0 NormalY=0 NormalZ=1 AngleXU=0 Radius=14.6613 StartAngle=1.5708 EndAngle=3.14159
    g9: ArcOfCircle CenterX=-160.339 CenterY=219.685 CenterZ=0 NormalX=0 NormalY=0 NormalZ=1 AngleXU=0 Radius=14.6613 StartAngle=3.14159 EndAngle=4.71239
    g10: ArcOfCircle CenterX=160.199 CenterY=219.685 CenterZ=0 NormalX=0 NormalY=0 NormalZ=1 AngleXU=0 Radius=14.6613 StartAngle=4.71239 EndAngle=6.28319
    g11: ArcOfCircle CenterX=160.199 CenterY=318.234 CenterZ=0 NormalX=0 NormalY=0 NormalZ=1 AngleXU=0 Radius=14.6613 StartAngle=0 EndAngle=1.5708
    g12: GeomPoint [constr] X=-175 Y=332.895 Z=0
    g13: GeomPoint [constr] X=174.86 Y=205.023 Z=0
  constraints (24):
    c: Coincident(g1,g-4)
    c: Vertical(g1)
    c: Coincident(g0,g1)
    c: Vertical(g2)
    c: PointOnObject(g2,g3)
    c: Tangent(g4,g8) = -1.5708
    c: Tangent(g4,g9) = -1.5708
    c: Tangent(g5,g9) = -1.5708
    c: Tangent(g5,g10) = -1.5708
    c: Tangent(g6,g10) = -1.5708
    c: Tangent(g6,g11) = -1.5708
    c: Tangent(g7,g11) = -1.5708
    c: Tangent(g7,g8) = -1.5708
    c: Vertical(g4)
    c: Vertical(g6)
    c: Horizontal(g5)
    c: Horizontal(g7)
    c: Equal(g8,g9)
    c: Equal(g9,g10)
    c: Equal(g10,g11)
    c: PointOnObject(g12,g4)
    c: PointOnObject(g12,g7)
    c: PointOnObject(g13,g5)
    c: PointOnObject(g13,g6)
FEATURE [PartDesign::Pad] Pad011
  Direction = (0,-1,2e-16)
  Length = 15
  Length2 = 10
  Profile = -> Sketch017
  ReferenceAxis = -> Sketch017 [N_Axis]
  Refine = true
  Reversed = true
  Suppressed = false
  Type = 0
FEATURE [PartDesign::Body] Body003
  AllowCompound = false
  Group = -> [CopyPocket013,Sketch017,Pad011]
  Origin = -> Origin003
  Tip = -> Pad011
FEATURE [PartDesign::ShapeBinder] CopyPocket014
  TraceSupport = false
FEATURE [Sketcher::SketchObject] Sketch018
  ArcFitTolerance = 1e-06
  AttachmentSupport = -> [CopyPocket014]
  ExternalGeometry = -> [CopyPocket014]
  FullyConstrained = false
  MakeInternals = false
  MapMode = 5
  Placement = pos=(0,-249,0) rot=(1,0,0;1.5708rad)
  sketch-geometry (12):
    g0: LineSegment [constr] StartX=-106.613 StartY=386.284 StartZ=0 EndX=-111.613 EndY=386.284 EndZ=0
    g1: LineSegment [constr] StartX=-111.613 StartY=381.284 StartZ=0 EndX=-111.613 EndY=386.284 EndZ=0
    g2: LineSegment StartX=-111.613 StartY=381.284 StartZ=0 EndX=-111.613 EndY=365.677 EndZ=0
    g3: LineSegment StartX=-106.613 StartY=360.677 StartZ=0 EndX=106.814 EndY=360.677 EndZ=0
    g4: LineSegment StartX=111.814 StartY=365.677 StartZ=0 EndX=111.814 EndY=381.284 EndZ=0
    g5: LineSegment StartX=106.814 StartY=386.284 StartZ=0 EndX=-106.613 EndY=386.284 EndZ=0
    g6: ArcOfCircle CenterX=-106.613 CenterY=381.284 CenterZ=0 NormalX=0 NormalY=0 NormalZ=1 AngleXU=0 Radius=5 StartAngle=1.5708 EndAngle=3.14159
    g7: ArcOfCircle CenterX=-106.613 CenterY=365.677 CenterZ=0 NormalX=0 NormalY=0 NormalZ=1 AngleXU=0 Radius=5 StartAngle=3.14159 EndAngle=4.71239
    g8: ArcOfCircle CenterX=106.814 CenterY=365.677 CenterZ=0 NormalX=0 NormalY=0 NormalZ=1 AngleXU=0 Radius=5 StartAngle=4.71239 EndAngle=6.28319
    g9: ArcOfCircle CenterX=106.814 CenterY=381.284 CenterZ=0 NormalX=0 NormalY=0 NormalZ=1 AngleXU=0 Radius=5 StartAngle=0 EndAngle=1.5708
    g10: GeomPoint [constr] X=-111.613 Y=386.284 Z=0
    g11: GeomPoint [constr] X=111.814 Y=360.677 Z=0
  constraints (25):
    c: Coincident(g0,g-3)
    c: Horizontal(g0)
    c: Tangent(g1,g-3) = 1.5708
    c: Coincident(g1,g0)
    c: Tangent(g2,g6) = -1.5708
    c: Tangent(g2,g7) = -1.5708
    c: Tangent(g3,g7) = -1.5708
    c: Tangent(g3,g8) = -1.5708
    c: Tangent(g4,g8) = -1.5708
    c: Tangent(g4,g9) = -1.5708
    c: Tangent(g5,g9) = -1.5708
    c: Tangent(g5,g6) = -1.5708
    c: Vertical(g2)
    c: Vertical(g4)
    c: Horizontal(g3)
    c: Horizontal(g5)
    c: Equal(g6,g7)
    c: Equal(g7,g8)
    c: Equal(g8,g9)
    c: PointOnObject(g10,g2)
    c: PointOnObject(g10,g5)
    c: PointOnObject(g11,g3)
    c: PointOnObject(g11,g4)
    c: Coincident(g10,g0)
    c: Coincident(g11,g-5)
FEATURE [Sketcher::SketchObject] Sketch019
  ArcFitTolerance = 1e-06
  AttachmentSupport = -> [Pocket005]
  ExternalGeometry = -> [Pocket005]
  FullyConstrained = false
  MakeInternals = false
  MapMode = 5
  Placement = pos=(0,-299,0) rot=(1,0,0;1.5708rad)
  sketch-geometry (4):
    g0: LineSegment StartX=-111.613 StartY=360.677 StartZ=0 EndX=113.773 EndY=360.677 EndZ=0
    g1: LineSegment StartX=113.773 StartY=360.677 StartZ=0 EndX=113.773 EndY=391.257 EndZ=0
    g2: LineSegment StartX=113.773 StartY=391.257 StartZ=0 EndX=-111.613 EndY=391.257 EndZ=0
    g3: LineSegment StartX=-111.613 StartY=391.257 StartZ=0 EndX=-111.613 EndY=360.677 EndZ=0
  constraints (9):
    c: Coincident(g0,g1)
    c: Coincident(g1,g2)
    c: Coincident(g2,g3)
    c: Coincident(g3,g0)
    c: Horizontal(g0)
    c: Horizontal(g2)
    c: Vertical(g1)
    c: Vertical(g3)
    c: Coincident(g0,g-4)
FEATURE [PartDesign::Pocket] Pocket006
  BaseFeature = -> Pocket005
  Direction = (0,1,-2e-16)
  Length = 50
  Length2 = 5
  Profile = -> Sketch019
  ReferenceAxis = -> Sketch019 [N_Axis]
  Refine = true
  Suppressed = false
  Type = 0
FEATURE [PartDesign::Pad] Pad012
  Direction = (0,-1,2e-16)
  Length = 50
  Length2 = 10
  Profile = -> Sketch018
  ReferenceAxis = -> Sketch018 [N_Axis]
  Refine = true
  Suppressed = false
  Type = 0
FEATURE [Sketcher::SketchObject] Sketch020
  ArcFitTolerance = 1e-06
  AttachmentSupport = -> [Pad012]
  ExternalGeometry = -> [Pad012]
  FullyConstrained = true
  MakeInternals = false
  MapMode = 5
  Placement = pos=(0,8.5e-14,386.284) rot=(0,0,1;0rad)
  sketch-geometry (4):
    g0: LineSegment StartX=-96.6131 StartY=-284 StartZ=0 EndX=96.814 EndY=-284 EndZ=0
    g1: LineSegment StartX=96.814 StartY=-284 StartZ=0 EndX=96.814 EndY=-249 EndZ=0
    g2: LineSegment StartX=96.814 StartY=-249 StartZ=0 EndX=-96.6131 EndY=-249 EndZ=0
    g3: LineSegment StartX=-96.6131 StartY=-249 StartZ=0 EndX=-96.6131 EndY=-284 EndZ=0
  constraints (12):
    c: Coincident(g0,g1)
    c: Coincident(g1,g2)
    c: Coincident(g2,g3)
    c: Coincident(g3,g0)
    c: Horizontal(g0)
    c: Horizontal(g2)
    c: Vertical(g1)
    c: Vertical(g3)
    c: PointOnObject(g2,g-7)
    c: DistanceX(g-5,g0) = 15
    c: DistanceX(g0,g-6) = 15
    c: DistanceY(g-6,g0) = 15
FEATURE [PartDesign::Pocket] Pocket007
  BaseFeature = -> Pad012
  Direction = (0,0,-1)
  Length = 5
  Length2 = 5
  Profile = -> Sketch020
  ReferenceAxis = -> Sketch020 [N_Axis]
  Refine = true
  Suppressed = false
  Type = 1
FEATURE [PartDesign::Fillet] Fillet012
  Base = -> Pocket007 [Edge18]
  BaseFeature = -> Pocket007
  Radius = 5
  Refine = true
  SupportTransform = false
  Suppressed = false
  UseAllEdges = false
FEATURE [PartDesign::Fillet] Fillet013
  Base = -> Fillet012 [Edge22,Edge35,Edge21,Edge36,Edge19,Edge37]
  BaseFeature = -> Fillet012
  Radius = 5
  Refine = true
  SupportTransform = false
  Suppressed = false
  UseAllEdges = false
FEATURE [PartDesign::Body] Body004
  AllowCompound = false
  Group = -> [CopyPocket014,Sketch018,Pad012,Sketch020,Pocket007,Fillet012,Fillet013]
  Origin = -> Origin004
  Tip = -> Fillet013
FEATURE [PartDesign::ShapeBinder] CopyPocket015
  TraceSupport = false
FEATURE [Sketcher::SketchObject] Sketch021
  ArcFitTolerance = 1e-06
  AttachmentSupport = -> [CopyPocket015]
  ExternalGeometry = -> [CopyPocket015]
  FullyConstrained = false
  MakeInternals = false
  MapMode = 5
  Placement = pos=(0,-249,0) rot=(1,0,0;1.5708rad)
  sketch-geometry (14):
    g0: LineSegment [constr] StartX=-160 StartY=332.961 StartZ=0 EndX=-175 EndY=332.942 EndZ=0
    g1: LineSegment [constr] StartX=-175 StartY=317.961 StartZ=0 EndX=-175 EndY=332.942 EndZ=0
    g2: LineSegment [constr] StartX=175 StartY=220.039 StartZ=0 EndX=175 EndY=205.039 EndZ=0
    g3: LineSegment [constr] StartX=160 StartY=205.039 StartZ=0 EndX=175 EndY=205.039 EndZ=0
    g4: LineSegment [constr] StartX=-214.5 StartY=414 StartZ=0 EndX=-254.5 EndY=414 EndZ=0
    g5: LineSegment [constr] StartX=-254.5 StartY=374 StartZ=0 EndX=-254.5 EndY=414 EndZ=0
    g6: LineSegment StartX=-254.5 StartY=374 StartZ=0 EndX=-254.5 EndY=124 EndZ=0
    g7: LineSegment StartX=-254.5 StartY=124 StartZ=0 EndX=254.5 EndY=124 EndZ=0
    g8: LineSegment StartX=254.5 StartY=124 StartZ=0 EndX=254.5 EndY=374 EndZ=0
    g9: LineSegment StartX=214.5 StartY=414 StartZ=0 EndX=-214.5 EndY=414 EndZ=0
    g10: ArcOfCircle CenterX=-214.5 CenterY=374 CenterZ=0 NormalX=0 NormalY=0 NormalZ=1 AngleXU=0 Radius=40 StartAngle=1.5708 EndAngle=3.14159
    g11: ArcOfCircle CenterX=214.5 CenterY=374 CenterZ=0 NormalX=0 NormalY=0 NormalZ=1 AngleXU=0 Radius=40 StartAngle=0 EndAngle=1.5708
    g12: GeomPoint [constr] X=-254.5 Y=414 Z=0
    g13: GeomPoint [constr] X=254.5 Y=124 Z=0
  constraints (27):
    c: Coincident(g1,g-7)
    c: Vertical(g1)
    c: PointOnObject(g0,g1)
    c: Coincident(g2,g-8)
    c: Vertical(g2)
    c: Coincident(g3,g-8)
    c: Horizontal(g3)
    c: Coincident(g2,g3)
    c: Coincident(g4,g-4)
    c: Horizontal(g4)
    c: Coincident(g5,g-3)
    c: Vertical(g5)
    c: Coincident(g4,g5)
    c: Tangent(g6,g10) = -1.5708
    c: Tangent(g8,g11) = -1.5708
    c: Tangent(g9,g11) = -1.5708
    c: Tangent(g9,g10) = -1.5708
    c: Vertical(g6)
    c: Vertical(g8)
    c: Horizontal(g9)
    c: PointOnObject(g12,g9)
    c: Coincident(g12,g4)
    c: Coincident(g13,g-6)
    c: Coincident(g8,g13)
    c: Coincident(g7,g8)
    c: Coincident(g7,g-5)
    c: Coincident(g6,g7)
FEATURE [PartDesign::Pad] Pad013
  Direction = (0,-1,2e-16)
  Length = 15
  Length2 = 10
  Profile = -> Sketch021
  ReferenceAxis = -> Sketch021 [N_Axis]
  Refine = true
  Reversed = true
  Suppressed = false
  Type = 0
FEATURE [Sketcher::SketchObject] Sketch022
  ArcFitTolerance = 1e-06
  AttachmentSupport = -> [Pad013]
  ExternalGeometry = -> [CopyPocket015]
  FullyConstrained = false
  MakeInternals = false
  MapMode = 5
  Placement = pos=(0,-249,0) rot=(1,0,0;1.5708rad)
  sketch-geometry (14):
    g0: LineSegment [constr] StartX=-160 StartY=332.961 StartZ=0 EndX=-175 EndY=332.942 EndZ=0
    g1: LineSegment [constr] StartX=-175 StartY=317.961 StartZ=0 EndX=-175 EndY=332.942 EndZ=0
    g2: LineSegment [constr] StartX=175 StartY=220.039 StartZ=0 EndX=175 EndY=205.039 EndZ=0
    g3: LineSegment [constr] StartX=160 StartY=205.039 StartZ=0 EndX=175 EndY=205.039 EndZ=0
    g4: LineSegment StartX=-175 StartY=317.975 StartZ=0 EndX=-175 EndY=220.006 EndZ=0
    g5: LineSegment StartX=-160.033 StartY=205.039 StartZ=0 EndX=160.033 EndY=205.039 EndZ=0
    g6: LineSegment StartX=175 StartY=220.006 StartZ=0 EndX=175 EndY=317.975 EndZ=0
    g7: LineSegment StartX=160.033 StartY=332.942 StartZ=0 EndX=-160.033 EndY=332.942 EndZ=0
    g8: ArcOfCircle CenterX=-160.033 CenterY=317.975 CenterZ=0 NormalX=0 NormalY=0 NormalZ=1 AngleXU=0 Radius=14.9674 StartAngle=1.5708 EndAngle=3.14159
    g9: ArcOfCircle CenterX=-160.033 CenterY=220.006 CenterZ=0 NormalX=0 NormalY=0 NormalZ=1 AngleXU=0 Radius=14.9674 StartAngle=3.14159 EndAngle=4.71239
    g10: ArcOfCircle CenterX=160.033 CenterY=220.006 CenterZ=0 NormalX=0 NormalY=0 NormalZ=1 AngleXU=0 Radius=14.9674 StartAngle=4.71239 EndAngle=6.28319
    g11: ArcOfCircle CenterX=160.033 CenterY=317.975 CenterZ=0 NormalX=0 NormalY=0 NormalZ=1 AngleXU=0 Radius=14.9674 StartAngle=0 EndAngle=1.5708
    g12: GeomPoint [constr] X=-175 Y=332.942 Z=0
    g13: GeomPoint [constr] X=175 Y=205.039 Z=0
  constraints (26):
    c: Vertical(g1)
    c: PointOnObject(g0,g1)
    c: Vertical(g2)
    c: Horizontal(g3)
    c: Coincident(g2,g3)
    c: Tangent(g4,g8) = -1.5708
    c: Tangent(g4,g9) = -1.5708
    c: Tangent(g5,g9) = -1.5708
    c: Tangent(g5,g10) = -1.5708
    c: Tangent(g6,g10) = -1.5708
    c: Tangent(g6,g11) = -1.5708
    c: Tangent(g7,g11) = -1.5708
    c: Tangent(g7,g8) = -1.5708
    c: Vertical(g4)
    c: Vertical(g6)
    c: Horizontal(g5)
    c: Horizontal(g7)
    c: Equal(g8,g9)
    c: Equal(g9,g10)
    c: Equal(g10,g11)
    c: PointOnObject(g12,g4)
    c: PointOnObject(g12,g7)
    c: PointOnObject(g13,g5)
    c: PointOnObject(g13,g6)
    c: Coincident(g12,g0)
    c: Coincident(g13,g2)
FEATURE [PartDesign::Pocket] Pocket008
  BaseFeature = -> Pad013
  Direction = (0,1,-2e-16)
  Length = 15
  Length2 = 5
  Profile = -> Sketch022
  ReferenceAxis = -> Sketch022 [N_Axis]
  Refine = true
  Suppressed = false
  Type = 0
FEATURE [PartDesign::Body] Body005
  AllowCompound = false
  Group = -> [CopyPocket015,Sketch021,Pad013,Sketch022,Pocket008]
  Origin = -> Origin005
  Tip = -> Pocket008
FEATURE [Sketcher::SketchObject] Sketch023
  ArcFitTolerance = 1e-06
  AttachmentSupport = -> [Pocket006]
  ExternalGeometry = -> [Pocket006]
  FullyConstrained = true
  MakeInternals = false
  MapMode = 5
  Placement = pos=(0,2.73e-14,124) rot=(1,0,0;3.14159rad)
  sketch-geometry (4):
    g0: LineSegment StartX=-254.5 StartY=249 StartZ=0 EndX=-254.5 EndY=234 EndZ=0
    g1: LineSegment StartX=-254.5 StartY=234 StartZ=0 EndX=254.5 EndY=234 EndZ=0
    g2: LineSegment StartX=254.5 StartY=234 StartZ=0 EndX=254.5 EndY=249 EndZ=0
    g3: LineSegment StartX=254.5 StartY=249 StartZ=0 EndX=-254.5 EndY=249 EndZ=0
  constraints (10):
    c: Coincident(g0,g1)
    c: Coincident(g1,g2)
    c: Coincident(g2,g3)
    c: Coincident(g3,g0)
    c: Vertical(g0)
    c: Vertical(g2)
    c: Horizontal(g1)
    c: Horizontal(g3)
    c: Coincident(g0,g-3)
    c: Coincident(g1,g-4)
FEATURE [PartDesign::Pocket] Pocket009
  BaseFeature = -> Pocket006
  Direction = (0,0,1)
  Length = 0
  Length2 = 5
  Profile = -> Sketch023
  ReferenceAxis = -> Sketch023 [N_Axis]
  Refine = true
  Suppressed = false
  Type = 3
  UpToFace = -> Pocket006 [Face5]
FEATURE [PartDesign::Body] Body
  AllowCompound = false
  Group = -> [Sketch,Pad,Sketch001,Pad001,Sketch002,Pad002,Sketch003,Pad003,Sketch004,Pad004,Sketch005,Pocket,Sketch006,Pocket001,Sketch007,Pad005,Sketch008,Pad006,Sketch009,Pocket002,Fillet,Fillet001,Fillet002,Fillet003,Fillet004,Fillet005,Fillet006,Fillet007,Sketch010,Pocket003,Sketch015,Pocket004,Sketch016,Pocket005,Sketch019,Pocket006,Sketch023,Pocket009]
  Origin = -> Origin
  Tip = -> Pocket009
FEATURE [Part::FeaturePython] Clone  label="body_clone"  # Draft clone (typed FeaturePython)
  AttacherType = Attacher::AttachEngine3D
  Fuse = false
  Objects = -> [Body]
  Scale = (1,1,1)
FEATURE [Part::FeaturePython] Clone001  label="left_switch_clone"  # Draft clone (typed FeaturePython)
  AttacherType = Attacher::AttachEngine3D
  Fuse = false
  Objects = -> [Body001]
  Scale = (1,1,1)
FEATURE [Part::FeaturePython] Clone002  label="right_switch_clone"  # Draft clone (typed FeaturePython)
  AttacherType = Attacher::AttachEngine3D
  Fuse = false
  Objects = -> [Body002]
  Scale = (1,1,1)
FEATURE [Part::FeaturePython] Clone003  label="handle_clone"  # Draft clone (typed FeaturePython)
  AttacherType = Attacher::AttachEngine3D
  Fuse = false
  Objects = -> [Body004]
  Scale = (1,1,1)
FEATURE [Part::FeaturePython] Clone004  label="fromt_panel_clone"  # Draft clone (typed FeaturePython)
  AttacherType = Attacher::AttachEngine3D
  Fuse = false
  Objects = -> [Body005]
  Scale = (1,1,1)
FEATURE [Part::FeaturePython] Clone005  label="glass_clone"  # Draft clone (typed FeaturePython)
  AttacherType = Attacher::AttachEngine3D
  Fuse = false
  Objects = -> [Body003]
  Scale = (1,1,1)
FEATURE [App::Part] Part  label="toasteroven"
  Group = -> [Clone,Clone001,Clone002,Clone003,Clone004,Clone005]
  Origin = -> Origin006
---- part ../tv/tv.FCStd = doc fcstd_355544b57ee7 ----
FCSTD DOCUMENT  (FreeCAD 1.0R39109 (Git))
Label: tv
License: All rights reserved
LicenseURL: https://en.wikipedia.org/wiki/All_rights_reserved
objects: Sketcher::SketchObject×9, PartDesign::Pad×6, PartDesign::Pocket×3, PartDesign::Body×3, App::Link×3, PartDesign::Fillet×2, Assembly::JointGroup×2, Assembly::AssemblyObject×2, Part::FeaturePython×2, PartDesign::ShapeBinder×2, PartDesign::Plane×2, App::Part×1
note: 60 computed .brp shape members not serialized (recipe doc carries the construction recipe); baked Part::Feature solids carry a one-line shape summary decoded from their .brp

FEATURE [Sketcher::SketchObject] Sketch003
  ArcFitTolerance = 1e-06
  AttachmentSupport = -> [XZ_Plane]
  FullyConstrained = true
  MakeInternals = false
  MapMode = 5
  Placement = pos=(0,0,0) rot=(1,0,0;1.5708rad)
  sketch-geometry (5):
    g0: LineSegment StartX=-4820 StartY=820 StartZ=0 EndX=4820 EndY=820 EndZ=0
    g1: LineSegment StartX=4820 StartY=820 StartZ=0 EndX=4820 EndY=6290 EndZ=0
    g2: LineSegment StartX=4820 StartY=6290 StartZ=0 EndX=-4820 EndY=6290 EndZ=0
    g3: LineSegment StartX=-4820 StartY=6290 StartZ=0 EndX=-4820 EndY=820 EndZ=0
    g4: GeomPoint [constr] X=0 Y=3555 Z=0
  constraints (13):
    c: Coincident(g0,g1)
    c: Coincident(g1,g2)
    c: Coincident(g2,g3)
    c: Coincident(g3,g0)
    c: Horizontal(g0)
    c: Horizontal(g2)
    c: Vertical(g1)
    c: Vertical(g3)
    c: Symmetric(g2,g0,g4)
    c: Distance(g1,g3) = 9640
    c: PointOnObject(g4,g-2)
    c: DistanceY(g1,g1) = 5470
    c: DistanceY(g0) = 820
FEATURE [PartDesign::Pad] Pad
  Direction = (0,-1,2e-16)
  Length = 100
  Length2 = 10
  Placement = pos=(0,0,0) rot=(1,0,0;1.5708rad)
  Profile = -> Sketch003
  ReferenceAxis = -> Sketch003 [N_Axis]
  Refine = true
  Suppressed = false
  Type = 0
FEATURE [Sketcher::SketchObject] Sketch004
  ArcFitTolerance = 1e-06
  AttachmentSupport = -> [Pad]
  ExternalGeometry = -> [Pad]
  FullyConstrained = true
  MakeInternals = false
  MapMode = 5
  Placement = pos=(0,7.894e-13,0) rot=(-1,0,0;1.5708rad)
  sketch-geometry (4):
    g0: LineSegment StartX=-4820 StartY=-820 StartZ=0 EndX=-4820 EndY=-1620 EndZ=0
    g1: LineSegment StartX=-4820 StartY=-1620 StartZ=0 EndX=4820 EndY=-1620 EndZ=0
    g2: LineSegment StartX=4820 StartY=-1620 StartZ=0 EndX=4820 EndY=-820 EndZ=0
    g3: LineSegment StartX=4820 StartY=-820 StartZ=0 EndX=-4820 EndY=-820 EndZ=0
  constraints (10):
    c: Coincident(g0,g1)
    c: Coincident(g1,g2)
    c: Coincident(g2,g3)
    c: Coincident(g3,g0)
    c: Vertical(g0)
    c: Vertical(g2)
    c: Horizontal(g1)
    c: DistanceY(g0,g0) = 800
    c: Coincident(g2,g-3)
    c: Coincident(g0,g-4)
FEATURE [PartDesign::Pad] Pad001
  BaseFeature = -> Pad
  Direction = (0,1,2e-16)
  Length = 800
  Length2 = 10
  Placement = pos=(0,0,0) rot=(1,0,0;1.5708rad)
  Profile = -> Sketch004
  ReferenceAxis = -> Sketch004 [N_Axis]
  Refine = true
  Suppressed = false
  Type = 0
FEATURE [Sketcher::SketchObject] Sketch005
  ArcFitTolerance = 1e-06
  AttachmentSupport = -> [Pad001]
  ExternalGeometry = -> [Pad001]
  FullyConstrained = false
  MakeInternals = false
  MapMode = 5
  Placement = pos=(0,7.894e-13,0) rot=(-1,0,0;1.5708rad)
  sketch-geometry (4):
    g0: LineSegment StartX=-4720 StartY=-6190 StartZ=0 EndX=4720 EndY=-6190 EndZ=0
    g1: LineSegment StartX=4720 StartY=-6190 StartZ=0 EndX=4720 EndY=-963.315 EndZ=0
    g2: LineSegment StartX=4720 StartY=-963.315 StartZ=0 EndX=-4720 EndY=-963.315 EndZ=0
    g3: LineSegment StartX=-4720 StartY=-963.315 StartZ=0 EndX=-4720 EndY=-6190 EndZ=0
  constraints (11):
    c: Coincident(g0,g1)
    c: Coincident(g1,g2)
    c: Coincident(g2,g3)
    c: Coincident(g3,g0)
    c: Horizontal(g0)
    c: Horizontal(g2)
    c: Vertical(g1)
    c: Vertical(g3)
    c: DistanceY(g-3,g0) = 100
    c: DistanceX(g-3,g0) = 100
    c: DistanceX(g0,g-4) = 100
FEATURE [PartDesign::Pad] Pad002
  BaseFeature = -> Pad001
  Direction = (0,1,2e-16)
  Length = 400
  Length2 = 10
  Placement = pos=(0,0,0) rot=(1,0,0;1.5708rad)
  Profile = -> Sketch005
  ReferenceAxis = -> Sketch005 [N_Axis]
  Refine = true
  Suppressed = false
  TaperAngle = -45
  Type = 0
FEATURE [Sketcher::SketchObject] Sketch008
  ArcFitTolerance = 1e-06
  AttachmentSupport = -> [Pad002]
  ExternalGeometry = -> [Pad002]
  FullyConstrained = false
  MakeInternals = false
  MapMode = 5
  Placement = pos=(0,0,1620) rot=(0,0,1;3.14159rad)
  sketch-geometry (18):
    g0: LineSegment StartX=0 StartY=-400 StartZ=0 EndX=-4226.42 EndY=-400 EndZ=0
    g1: Circle [constr] CenterX=-4226.42 CenterY=-400 CenterZ=0 NormalX=0 NormalY=0 NormalZ=1 AngleXU=0 Radius=1
    g2: Circle [constr] CenterX=-3745.48 CenterY=-741.541 CenterZ=0 NormalX=0 NormalY=0 NormalZ=1 AngleXU=0 Radius=1
    g3: Circle [constr] CenterX=-3483.42 CenterY=-773.588 CenterZ=0 NormalX=0 NormalY=0 NormalZ=1 AngleXU=0 Radius=1
    g4: BSplineCurve PolesCount=4 KnotsCount=2 Degree=3 IsPeriodic=0
    g5: GeomPoint [constr] X=-4226.42 Y=-400 Z=0
    g6: GeomPoint [constr] X=-3109.89 Y=-800 Z=0
    g7: Circle [constr] CenterX=-3109.89 CenterY=-800 CenterZ=0 NormalX=0 NormalY=0 NormalZ=1 AngleXU=0 Radius=1
    g8: LineSegment StartX=-3109.89 StartY=-800 StartZ=0 EndX=0 EndY=-800 EndZ=0
    g9: Circle [constr] CenterX=4226.42 CenterY=-400 CenterZ=0 NormalX=0 NormalY=0 NormalZ=1 AngleXU=0 Radius=1
    g10: Circle [constr] CenterX=3745.48 CenterY=-741.541 CenterZ=0 NormalX=0 NormalY=0 NormalZ=1 AngleXU=0 Radius=1
    g11: Circle [constr] CenterX=3483.42 CenterY=-773.588 CenterZ=0 NormalX=0 NormalY=0 NormalZ=1 AngleXU=0 Radius=1
    g12: BSplineCurve PolesCount=4 KnotsCount=2 Degree=3 IsPeriodic=0
    g13: GeomPoint [constr] X=4226.42 Y=-400 Z=0
    g14: GeomPoint [constr] X=3109.89 Y=-800 Z=0
    g15: Circle [constr] CenterX=3109.89 CenterY=-800 CenterZ=0 NormalX=0 NormalY=0 NormalZ=1 AngleXU=0 Radius=1
    g16: LineSegment StartX=3109.89 StartY=-800 StartZ=0 EndX=0 EndY=-800 EndZ=0
    g17: LineSegment StartX=0 StartY=-400 StartZ=0 EndX=4226.42 EndY=-400 EndZ=0
  constraints (25):
    c: Horizontal(g0)
    c: PointOnObject(g0,g-3)
    c: Weight(g1) = 1
    c: Equal(g1,g2)
    c: Equal(g1,g3)
    c: InternalAlignment(g1,g4)
    c: InternalAlignment(g2,g4)
    c: InternalAlignment(g3,g4)
    c: InternalAlignment(g5,g4)
    c: InternalAlignment(g6,g4)
    c: Coincident(g1,g0)
    c: InternalAlignment(g7,g4)
    c: Equal(g7,g1)
    c: Horizontal(g17)
    c: Weight(g9) = 1
    c: Equal(g9,g10)
    c: Equal(g9,g11)
    c: InternalAlignment(g9,g12)
    c: InternalAlignment(g10,g12)
    c: InternalAlignment(g11,g12)
    c: InternalAlignment(g13,g12)
    c: InternalAlignment(g14,g12)
    c: Coincident(g9,g17)
    c: InternalAlignment(g15,g12)
    c: Equal(g15,g9)
FEATURE [PartDesign::Pad] Pad003
  BaseFeature = -> Pad002
  Direction = (0,0,1)
  Length = 2500
  Length2 = 10
  Placement = pos=(0,0,0) rot=(1,0,0;1.5708rad)
  Profile = -> Sketch008
  ReferenceAxis = -> Sketch008 [N_Axis]
  Refine = true
  Suppressed = false
  Type = 0
FEATURE [Sketcher::SketchObject] Sketch009
  ArcFitTolerance = 1e-06
  AttachmentSupport = -> [Pad003]
  ExternalGeometry = -> [Pad003]
  FullyConstrained = false
  MakeInternals = false
  MapMode = 5
  Placement = pos=(4820,-4.5308e-12,0) rot=(0.707107,0,0.707107;3.14159rad)
  sketch-geometry (8):
    g0: LineSegment StartX=4120 StartY=-800 StartZ=0 EndX=3674.07 EndY=-800 EndZ=0
    g1: Circle [constr] CenterX=4120 CenterY=-400 CenterZ=0 NormalX=0 NormalY=0 NormalZ=1 AngleXU=0 Radius=1
    g2: Circle [constr] CenterX=3794.85 CenterY=-604.641 CenterZ=0 NormalX=0 NormalY=0 NormalZ=1 AngleXU=0 Radius=1
    g3: Circle [constr] CenterX=3674.07 CenterY=-800 CenterZ=0 NormalX=0 NormalY=0 NormalZ=1 AngleXU=0 Radius=1
    g4: BSplineCurve PolesCount=3 KnotsCount=2 Degree=2 IsPeriodic=0
    g5: GeomPoint [constr] X=4120 Y=-400 Z=0
    g6: GeomPoint [constr] X=3674.07 Y=-800 Z=0
    g7: LineSegment StartX=4120 StartY=-400 StartZ=0 EndX=4120 EndY=-800 EndZ=0
  constraints (12):
    c: Coincident(g0,g-4)
    c: Horizontal(g0)
    c: Weight(g1) = 1
    c: Equal(g1,g2)
    c: Equal(g1,g3)
    c: InternalAlignment(g1,g4)
    c: InternalAlignment(g2,g4)
    c: InternalAlignment(g3,g4)
    c: InternalAlignment(g5,g4)
    c: InternalAlignment(g6,g4)
    c: Coincident(g1,g-4)
    c: Coincident(g3,g0)
FEATURE [PartDesign::Pocket] Pocket
  BaseFeature = -> Pad003
  Direction = (-1,0,2e-16)
  Length = 5
  Length2 = 5
  Placement = pos=(0,0,0) rot=(1,0,0;1.5708rad)
  Profile = -> Sketch009
  ReferenceAxis = -> Sketch009 [N_Axis]
  Refine = true
  Suppressed = false
  Type = 1
FEATURE [Sketcher::SketchObject] Sketch010
  ArcFitTolerance = 1e-06
  AttachmentSupport = -> [Pocket]
  ExternalGeometry = -> [Pocket]
  FullyConstrained = false
  MakeInternals = false
  MapMode = 5
  Placement = pos=(0,800,0) rot=(-1,0,0;1.5708rad)
  sketch-geometry (13):
    g0: LineSegment StartX=4524.01 StartY=-3554.92 StartZ=0 EndX=4524.01 EndY=-1739.15 EndZ=0
    g1: LineSegment StartX=4524.01 StartY=-1739.15 StartZ=0 EndX=3287.44 EndY=-1739.15 EndZ=0
    g2: LineSegment StartX=3287.44 StartY=-1739.15 StartZ=0 EndX=3287.44 EndY=-3554.92 EndZ=0
    g3: LineSegment StartX=3287.44 StartY=-3554.92 StartZ=0 EndX=4524.01 EndY=-3554.92 EndZ=0
    g4: LineSegment StartX=-3287.44 StartY=-2395.51 StartZ=0 EndX=-3287.44 EndY=-1732.57 EndZ=0
    g5: LineSegment StartX=-3287.44 StartY=-1732.57 StartZ=0 EndX=-4524.01 EndY=-1732.57 EndZ=0
    g6: LineSegment StartX=-4524.01 StartY=-1732.57 StartZ=0 EndX=-4524.01 EndY=-2395.51 EndZ=0
    g7: LineSegment StartX=-4524.01 StartY=-2395.51 StartZ=0 EndX=-3287.44 EndY=-2395.51 EndZ=0
    g8: LineSegment [constr] StartX=3287.44 StartY=-3554.92 StartZ=0 EndX=3109.89 EndY=-3554.92 EndZ=0
    g9: LineSegment [constr] StartX=3109.89 StartY=-3554.92 StartZ=0 EndX=3109.89 EndY=-3674.07 EndZ=0
    g10: LineSegment [constr] StartX=3287.44 StartY=-1739.15 StartZ=0 EndX=3109.89 EndY=-1739.15 EndZ=0
    g11: LineSegment [constr] StartX=3109.89 StartY=-1739.15 StartZ=0 EndX=3109.89 EndY=-1620 EndZ=0
    g12: LineSegment [constr] StartX=-3287.44 StartY=-1732.57 StartZ=0 EndX=-3109.89 EndY=-1732.57 EndZ=0
  constraints (32):
    c: Coincident(g0,g1)
    c: Coincident(g1,g2)
    c: Coincident(g2,g3)
    c: Coincident(g3,g0)
    c: Vertical(g0)
    c: Vertical(g2)
    c: Horizontal(g1)
    c: Horizontal(g3)
    c: Coincident(g4,g5)
    c: Coincident(g5,g6)
    c: Coincident(g6,g7)
    c: Coincident(g7,g4)
    c: Vertical(g4)
    c: Vertical(g6)
    c: Horizontal(g5)
    c: Horizontal(g7)
    c: Coincident(g8,g2)
    c: PointOnObject(g8,g-3)
    c: Horizontal(g8)
    c: Coincident(g9,g8)
    c: Coincident(g9,g-3)
    c: Coincident(g10,g1)
    c: PointOnObject(g10,g-3)
    c: Horizontal(g10)
    c: Coincident(g11,g10)
    c: Coincident(g11,g-3)
    c: Equal(g9,g11)
    c: Coincident(g12,g4)
    c: PointOnObject(g12,g-4)
    c: Horizontal(g12)
    c: Equal(g12,g10)
    c: Equal(g3,g7)
FEATURE [PartDesign::Pocket] Pocket001
  BaseFeature = -> Pocket
  Direction = (0,-1,-2e-16)
  Length = 330
  Length2 = 5
  Placement = pos=(0,0,0) rot=(1,0,0;1.5708rad)
  Profile = -> Sketch010
  ReferenceAxis = -> Sketch010 [N_Axis]
  Refine = true
  Suppressed = false
  Type = 0
FEATURE [PartDesign::Fillet] Fillet
  Base = -> Pocket001 [Edge54,Edge57]
  BaseFeature = -> Pocket001
  Placement = pos=(0,0,0) rot=(1,0,0;1.5708rad)
  Radius = 50
  Refine = true
  SupportTransform = false
  Suppressed = false
  UseAllEdges = false
FEATURE [PartDesign::Fillet] Fillet001
  Base = -> Fillet [Edge16,Edge1,Edge62,Edge64]
  BaseFeature = -> Fillet
  Placement = pos=(0,0,0) rot=(1,0,0;1.5708rad)
  Radius = 50
  Refine = true
  SupportTransform = false
  Suppressed = false
  UseAllEdges = false
FEATURE [Sketcher::SketchObject] Sketch011
  ArcFitTolerance = 1e-06
  AttachmentSupport = -> [Fillet001]
  ExternalGeometry = -> [Fillet001]
  FullyConstrained = true
  MakeInternals = false
  MapMode = 5
  Placement = pos=(0,-100,0) rot=(1,0,0;1.5708rad)
  sketch-geometry (4):
    g0: LineSegment StartX=-4807.8 StartY=6277.8 StartZ=0 EndX=-4807.8 EndY=832.2 EndZ=0
    g1: LineSegment StartX=-4807.8 StartY=832.2 StartZ=0 EndX=4807.8 EndY=832.2 EndZ=0
    g2: LineSegment StartX=4807.8 StartY=832.2 StartZ=0 EndX=4807.8 EndY=6277.8 EndZ=0
    g3: LineSegment StartX=4807.8 StartY=6277.8 StartZ=0 EndX=-4807.8 EndY=6277.8 EndZ=0
  constraints (12):
    c: Coincident(g0,g1)
    c: Coincident(g1,g2)
    c: Coincident(g2,g3)
    c: Coincident(g3,g0)
    c: Vertical(g0)
    c: Vertical(g2)
    c: Horizontal(g1)
    c: Horizontal(g3)
    c: DistanceY(g0,g-3) = 12.2
    c: DistanceX(g-3,g0) = 12.2
    c: DistanceX(g1,g-4) = 12.2
    c: DistanceY(g-4,g1) = 12.2
FEATURE [PartDesign::Pocket] Pocket002
  BaseFeature = -> Fillet001
  Direction = (0,1,-2e-16)
  Length = 2
  Length2 = 5
  Placement = pos=(0,0,0) rot=(1,0,0;1.5708rad)
  Profile = -> Sketch011
  ReferenceAxis = -> Sketch011 [N_Axis]
  Refine = true
  Suppressed = false
  Type = 0
FEATURE [PartDesign::Body] Body
  AllowCompound = false
  Group = -> [Sketch003,Pad,Sketch004,Pad001,Sketch005,Pad002,Sketch008,Pad003,Sketch009,Pocket,Sketch010,Pocket001,Fillet,Fillet001,Sketch011,Pocket002]
  Origin = -> Origin
  Tip = -> Pocket002
FEATURE [Assembly::JointGroup] Joints
FEATURE [App::Link] Body003  label="Screen"
  LinkPlacement = pos=(0,-350,0) rot=(0,0,1;0rad)
  LinkedObject = -> Body
  Placement = pos=(0,-350,0) rot=(0,0,1;0rad)
FEATURE [Assembly::AssemblyObject] Assembly  label="Screen_a"
  Group = -> [Joints,Body003]
  Origin = -> Origin003
  Placement = pos=(0,-350,0) rot=(0,0,1;0rad)
  Type = Assembly
FEATURE [Part::FeaturePython] Clone001  label="Screen_clone"  # Draft clone (typed FeaturePython)
  AttacherType = Attacher::AttachEngine3D
  Fuse = false
  Objects = -> [Assembly]
  Scale = (0.1,0.1,0.1)
FEATURE [Assembly::JointGroup] Joints001
FEATURE [PartDesign::ShapeBinder] CopyFillet001
  Placement = pos=(0,0,0) rot=(1,0,0;1.5708rad)
  TraceSupport = false
FEATURE [PartDesign::Plane] DatumPlane
  AttachmentOffset = pos=(0,0,-1500) rot=(0,0,1;0rad)
  AttachmentSupport = -> [CopyFillet001]
  Length = 6989.3
  MapMode = 5
  Placement = pos=(3320,0,3.331e-13) rot=(0.707107,0,0.707107;3.14159rad)
  ResizeMode = 0
  Width = 2474.3
FEATURE [Sketcher::SketchObject] Sketch006
  ArcFitTolerance = 1e-06
  AttachmentSupport = -> [DatumPlane]
  ExternalGeometry = -> [CopyFillet001]
  FullyConstrained = false
  MakeInternals = false
  MapMode = 5
  Placement = pos=(3320,0,3.331e-13) rot=(0.707107,0,0.707107;3.14159rad)
  sketch-geometry (17):
    g0: LineSegment StartX=820 StartY=-119.068 StartZ=0 EndX=820 EndY=-580.932 EndZ=0
    g1: LineSegment StartX=820 StartY=-119.068 StartZ=0 EndX=736.366 EndY=-119.068 EndZ=0
    g2: LineSegment StartX=820 StartY=-580.932 StartZ=0 EndX=742.416 EndY=-580.932 EndZ=0
    g3: LineSegment StartX=680.048 StartY=-96.5682 StartZ=0 EndX=0 EndY=550 EndZ=0
    g4: LineSegment StartX=686.36 StartY=-603.183 StartZ=0 EndX=0 EndY=-1250 EndZ=0
    g5: LineSegment [constr] StartX=820 StartY=-350 StartZ=0 EndX=0 EndY=-350 EndZ=0
    g6: LineSegment [constr] StartX=820 StartY=100 StartZ=0 EndX=820 EndY=-119.068 EndZ=0
    g7: LineSegment [constr] StartX=820 StartY=-580.932 StartZ=0 EndX=820 EndY=-800 EndZ=0
    g8: LineSegment StartX=0 StartY=408.983 StartZ=0 EndX=671.046 EndY=-229.026 EndZ=0
    g9: LineSegment StartX=670.497 StartY=-477.115 StartZ=0 EndX=0 EndY=-1108.98 EndZ=0
    g10: ArcOfCircle CenterX=553.355 CenterY=-352.811 CenterZ=0 NormalX=0 NormalY=0 NormalZ=1 AngleXU=0 Radius=170.803 StartAngle=5.46813 EndAngle=7.09382
    g11: LineSegment StartX=0 StartY=550 StartZ=0 EndX=0 EndY=408.983 EndZ=0
    g12: LineSegment StartX=0 StartY=-1108.98 StartZ=0 EndX=0 EndY=-1250 EndZ=0
    g13: ArcOfCircle CenterX=736.366 CenterY=-37.3338 CenterZ=0 NormalX=0 NormalY=0 NormalZ=1 AngleXU=0 Radius=81.7339 StartAngle=3.95222 EndAngle=4.71239
    g14: GeomPoint [constr] X=703.713 Y=-119.068 Z=0
    g15: ArcOfCircle CenterX=742.416 CenterY=-662.666 CenterZ=0 NormalX=0 NormalY=0 NormalZ=1 AngleXU=0 Radius=81.7339 StartAngle=1.5708 EndAngle=2.32654
    g16: GeomPoint [constr] X=709.972 Y=-580.932 Z=0
  constraints (37):
    c: PointOnObject(g0,g-3)
    c: PointOnObject(g0,g-3)
    c: Coincident(g1,g0)
    c: Horizontal(g1)
    c: Coincident(g2,g0)
    c: Horizontal(g2)
    c: PointOnObject(g3,g-2)
    c: DistanceY(g4,g3) = 1800
    c: PointOnObject(g4,g-2)
    c: Symmetric(g0,g0,g5)
    c: Horizontal(g5)
    c: Symmetric(g4,g3,g5)
    c: Coincident(g6,g-3)
    c: Coincident(g6,g0)
    c: Coincident(g7,g0)
    c: Coincident(g7,g-3)
    c: Equal(g7,g6)
    c: PointOnObject(g8,g-2)
    c: PointOnObject(g9,g-2)
    c: Parallel(g8,g3)
    c: Parallel(g9,g4)
    c: Tangent(g8,g10) = 1.5708
    c: Tangent(g9,g10) = 1.5708
    c: Coincident(g11,g3)
    c: Coincident(g11,g8)
    c: Coincident(g12,g9)
    c: Coincident(g12,g4)
    c: PointOnObject(g14,g1)
    c: PointOnObject(g14,g3)
    c: Tangent(g1,g13) = 1.5708
    c: Tangent(g3,g13) = 1.5708
    c: PointOnObject(g16,g2)
    c: PointOnObject(g16,g4)
    c: Tangent(g2,g15) = -1.5708
    c: Tangent(g4,g15) = -1.5708
    c: Equal(g13,g15)
    c: Equal(g12,g11)
FEATURE [PartDesign::Pad] Pad004
  Direction = (1,0,-2e-16)
  Length = 200
  Length2 = 10
  Placement = pos=(3320,0,3.331e-13) rot=(0.707107,0,0.707107;3.14159rad)
  Profile = -> Sketch006
  ReferenceAxis = -> Sketch006 [N_Axis]
  Refine = true
  Reversed = true
  Suppressed = false
  Type = 0
FEATURE [PartDesign::Body] Body001
  AllowCompound = false
  Group = -> [DatumPlane,CopyFillet001,Sketch006,Pad004]
  Origin = -> Origin001
  Tip = -> Pad004
FEATURE [App::Link] Body004  label="Right_Stand"
  LinkPlacement = pos=(0,-350,0) rot=(0,0,1;0rad)
  LinkedObject = -> Body001
  Placement = pos=(0,-350,0) rot=(0,0,1;0rad)
FEATURE [PartDesign::ShapeBinder] CopyFillet002
  Placement = pos=(0,0,0) rot=(1,0,0;1.5708rad)
  TraceSupport = false
FEATURE [PartDesign::Plane] DatumPlane001
  AttachmentOffset = pos=(0,0,-1500) rot=(0,0,1;0rad)
  AttachmentSupport = -> [CopyFillet002]
  Length = 6989.3
  MapMode = 5
  Placement = pos=(-3320,0,3.331e-13) rot=(0.707107,0,-0.707107;3.14159rad)
  ResizeMode = 0
  Width = 2474.3
FEATURE [Sketcher::SketchObject] Sketch007
  ArcFitTolerance = 1e-06
  AttachmentSupport = -> [DatumPlane001]
  FullyConstrained = false
  MakeInternals = false
  MapMode = 5
  Placement = pos=(-3320,0,3.331e-13) rot=(0.707107,0,-0.707107;3.14159rad)
  sketch-geometry (17):
    g0: LineSegment StartX=-820 StartY=-580.932 StartZ=0 EndX=-820 EndY=-119.068 EndZ=0
    g1: LineSegment StartX=-820 StartY=-580.932 StartZ=0 EndX=-736.366 EndY=-580.932 EndZ=0
    g2: LineSegment StartX=-820 StartY=-119.068 StartZ=0 EndX=-742.416 EndY=-119.068 EndZ=0
    g3: LineSegment StartX=-680.048 StartY=-603.432 StartZ=0 EndX=0 EndY=-1250 EndZ=0
    g4: LineSegment StartX=-686.36 StartY=-96.8166 StartZ=0 EndX=0 EndY=550 EndZ=0
    g5: LineSegment [constr] StartX=-820 StartY=-350 StartZ=0 EndX=0 EndY=-350 EndZ=0
    g6: LineSegment [constr] StartX=-820 StartY=-800 StartZ=0 EndX=-820 EndY=-580.932 EndZ=0
    g7: LineSegment [constr] StartX=-820 StartY=-119.068 StartZ=0 EndX=-820 EndY=100 EndZ=0
    g8: LineSegment StartX=0 StartY=-1108.98 StartZ=0 EndX=-671.046 EndY=-470.974 EndZ=0
    g9: LineSegment StartX=-670.497 StartY=-222.885 StartZ=0 EndX=0 EndY=408.983 EndZ=0
    g10: ArcOfCircle CenterX=-553.355 CenterY=-347.189 CenterZ=0 NormalX=0 NormalY=0 NormalZ=1 AngleXU=0 Radius=170.803 StartAngle=2.32654 EndAngle=3.95222
    g11: LineSegment StartX=0 StartY=-1250 StartZ=0 EndX=0 EndY=-1108.98 EndZ=0
    g12: LineSegment StartX=0 StartY=408.983 StartZ=0 EndX=0 EndY=550 EndZ=0
    g13: ArcOfCircle CenterX=-736.366 CenterY=-662.666 CenterZ=0 NormalX=0 NormalY=0 NormalZ=1 AngleXU=0 Radius=81.734 StartAngle=0.81063 EndAngle=1.5708
    g14: GeomPoint [constr] X=-703.713 Y=-580.932 Z=0
    g15: ArcOfCircle CenterX=-742.416 CenterY=-37.3338 CenterZ=0 NormalX=0 NormalY=0 NormalZ=1 AngleXU=0 Radius=81.734 StartAngle=4.71239 EndAngle=5.46813
    g16: GeomPoint [constr] X=-709.972 Y=-119.068 Z=0
  constraints (25):
    c: Coincident(g1,g0)
    c: Coincident(g2,g0)
    c: Symmetric(g0,g0,g5)
    c: Symmetric(g4,g3,g5)
    c: Coincident(g6,g0)
    c: Coincident(g7,g0)
    c: Equal(g7,g6)
    c: Parallel(g8,g3)
    c: Parallel(g9,g4)
    c: Tangent(g8,g10) = 1.5708
    c: Tangent(g9,g10) = 1.5708
    c: Coincident(g11,g3)
    c: Coincident(g11,g8)
    c: Coincident(g12,g9)
    c: Coincident(g12,g4)
    c: PointOnObject(g14,g1)
    c: PointOnObject(g14,g3)
    c: Tangent(g1,g13) = 1.5708
    c: Tangent(g3,g13) = 1.5708
    c: PointOnObject(g16,g2)
    c: PointOnObject(g16,g4)
    c: Tangent(g2,g15) = -1.5708
    c: Tangent(g4,g15) = -1.5708
    c: Equal(g13,g15)
    c: Equal(g12,g11)
FEATURE [PartDesign::Pad] Pad005
  Direction = (-1,0,-2e-16)
  Length = 200
  Length2 = 10
  Placement = pos=(-3320,0,3.331e-13) rot=(0.707107,0,-0.707107;3.14159rad)
  Profile = -> Sketch007
  ReferenceAxis = -> Sketch007 [N_Axis]
  Refine = true
  Reversed = true
  Suppressed = false
  Type = 0
FEATURE [PartDesign::Body] Body002
  AllowCompound = false
  Group = -> [DatumPlane001,CopyFillet002,Sketch007,Pad005]
  Origin = -> Origin002
  Tip = -> Pad005
FEATURE [App::Link] Body005  label="Left_Stand"
  LinkPlacement = pos=(0,-350,0) rot=(0,0,1;0rad)
  LinkedObject = -> Body002
  Placement = pos=(0,-350,0) rot=(0,0,1;0rad)
FEATURE [Assembly::AssemblyObject] Assembly001  label="Stand_a"
  Group = -> [Joints001,Body004,Body005]
  Origin = -> Origin005
  Placement = pos=(0,-350,0) rot=(0,0,1;0rad)
  Type = Assembly
FEATURE [Part::FeaturePython] Clone  label="Stand_clone"  # Draft clone (typed FeaturePython)
  AttacherType = Attacher::AttachEngine3D
  Fuse = false
  Objects = -> [Assembly001]
  Scale = (0.1,0.1,0.1)
FEATURE [App::Part] Part001  label="tv"
  Group = -> [Clone001,Clone]
  Origin = -> Origin004
---- part ../tvboard/tvboard.FCStd = doc fcstd_790a103b0d8b ----
FCSTD DOCUMENT  (FreeCAD 1.0R39109 (Git))
Label: tvboard
License: All rights reserved
LicenseURL: https://en.wikipedia.org/wiki/All_rights_reserved
objects: Sketcher::SketchObject×9, PartDesign::Pad×8, PartDesign::Plane×1, PartDesign::Pocket×1, PartDesign::Body×1, Part::FeaturePython×1, App::Part×1
note: 48 computed .brp shape members not serialized (recipe doc carries the construction recipe); baked Part::Feature solids carry a one-line shape summary decoded from their .brp

FEATURE [Sketcher::SketchObject] Sketch
  ArcFitTolerance = 1e-06
  AttachmentSupport = -> [XY_Plane]
  FullyConstrained = true
  MakeInternals = false
  MapMode = 5
  sketch-geometry (5):
    g0: LineSegment StartX=-542.5 StartY=-140 StartZ=0 EndX=542.5 EndY=-140 EndZ=0
    g1: LineSegment StartX=542.5 StartY=-140 StartZ=0 EndX=542.5 EndY=140 EndZ=0
    g2: LineSegment StartX=542.5 StartY=140 StartZ=0 EndX=-542.5 EndY=140 EndZ=0
    g3: LineSegment StartX=-542.5 StartY=140 StartZ=0 EndX=-542.5 EndY=-140 EndZ=0
    g4: GeomPoint [constr] X=0 Y=0 Z=0
  constraints (12):
    c: Coincident(g0,g1)
    c: Coincident(g1,g2)
    c: Coincident(g2,g3)
    c: Coincident(g3,g0)
    c: Horizontal(g0)
    c: Horizontal(g2)
    c: Vertical(g1)
    c: Vertical(g3)
    c: Symmetric(g2,g0,g4)
    c: Distance(g1,g3) = 1085
    c: Distance(g0,g2) = 280
    c: Coincident(g4,g-1)
FEATURE [PartDesign::Pad] Pad
  Direction = (0,0,1)
  Length = 50
  Length2 = 10
  Profile = -> Sketch
  ReferenceAxis = -> Sketch [N_Axis]
  Refine = true
  Suppressed = false
  Type = 0
FEATURE [Sketcher::SketchObject] Sketch001
  ArcFitTolerance = 1e-06
  AttachmentSupport = -> [Pad]
  FullyConstrained = true
  MakeInternals = false
  MapMode = 5
  Placement = pos=(0,0,50) rot=(0,0,1;0rad)
  sketch-geometry (5):
    g0: LineSegment StartX=-550 StartY=-147.5 StartZ=0 EndX=550 EndY=-147.5 EndZ=0
    g1: LineSegment StartX=550 StartY=-147.5 StartZ=0 EndX=550 EndY=147.5 EndZ=0
    g2: LineSegment StartX=550 StartY=147.5 StartZ=0 EndX=-550 EndY=147.5 EndZ=0
    g3: LineSegment StartX=-550 StartY=147.5 StartZ=0 EndX=-550 EndY=-147.5 EndZ=0
    g4: GeomPoint [constr] X=0 Y=0 Z=0
  constraints (12):
    c: Coincident(g0,g1)
    c: Coincident(g1,g2)
    c: Coincident(g2,g3)
    c: Coincident(g3,g0)
    c: Horizontal(g0)
    c: Horizontal(g2)
    c: Vertical(g1)
    c: Vertical(g3)
    c: Symmetric(g2,g0,g4)
    c: Distance(g1,g3) = 1100
    c: Distance(g0,g2) = 295
    c: Coincident(g4,g-1)
FEATURE [PartDesign::Pad] Pad001
  BaseFeature = -> Pad
  Direction = (0,0,1)
  Length = 10
  Length2 = 10
  Profile = -> Sketch001
  ReferenceAxis = -> Sketch001 [N_Axis]
  Refine = true
  Suppressed = false
  Type = 0
FEATURE [Sketcher::SketchObject] Sketch002
  ArcFitTolerance = 1e-06
  AttachmentSupport = -> [Pad001]
  ExternalGeometry = -> [Pad001]
  FullyConstrained = false
  MakeInternals = false
  MapMode = 5
  Placement = pos=(0,0,60) rot=(0,0,1;0rad)
  sketch-geometry (16):
    g0: LineSegment StartX=-549 StartY=146.5 StartZ=0 EndX=-549 EndY=-135.5 EndZ=0
    g1: LineSegment StartX=-549 StartY=-135.5 StartZ=0 EndX=-539 EndY=-135.5 EndZ=0
    g2: LineSegment StartX=-539 StartY=-135.5 StartZ=0 EndX=-539 EndY=146.5 EndZ=0
    g3: LineSegment StartX=-539 StartY=146.5 StartZ=0 EndX=-549 EndY=146.5 EndZ=0
    g4: LineSegment StartX=-260 StartY=146.5 StartZ=0 EndX=-260 EndY=-135.5 EndZ=0
    g5: LineSegment StartX=-260 StartY=-135.5 StartZ=0 EndX=-250 EndY=-135.5 EndZ=0
    g6: LineSegment StartX=-250 StartY=-135.5 StartZ=0 EndX=-250 EndY=146.5 EndZ=0
    g7: LineSegment StartX=-250 StartY=146.5 StartZ=0 EndX=-260 EndY=146.5 EndZ=0
    g8: LineSegment StartX=250 StartY=146.5 StartZ=0 EndX=250 EndY=-135.5 EndZ=0
    g9: LineSegment StartX=250 StartY=-135.5 StartZ=0 EndX=260 EndY=-135.5 EndZ=0
    g10: LineSegment StartX=260 StartY=-135.5 StartZ=0 EndX=260 EndY=146.5 EndZ=0
    g11: LineSegment StartX=260 StartY=146.5 StartZ=0 EndX=250 EndY=146.5 EndZ=0
    g12: LineSegment StartX=549 StartY=146.5 StartZ=0 EndX=549 EndY=-135.5 EndZ=0
    g13: LineSegment StartX=549 StartY=-135.5 StartZ=0 EndX=539 EndY=-135.5 EndZ=0
    g14: LineSegment StartX=539 StartY=-135.5 StartZ=0 EndX=539 EndY=146.5 EndZ=0
    g15: LineSegment StartX=539 StartY=146.5 StartZ=0 EndX=549 EndY=146.5 EndZ=0
  constraints (43):
    c: Coincident(g0,g1)
    c: Coincident(g1,g2)
    c: Coincident(g2,g3)
    c: Coincident(g3,g0)
    c: Vertical(g0)
    c: Vertical(g2)
    c: Horizontal(g1)
    c: Horizontal(g3)
    c: DistanceY(g0,g-4) = 1
    c: DistanceX(g-4,g0) = 1
    c: DistanceX(g3,g3) = 10
    c: DistanceY(g-3,g1) = 12
    c: Coincident(g4,g5)
    c: Coincident(g5,g6)
    c: Coincident(g6,g7)
    c: Coincident(g7,g4)
    c: Vertical(g4)
    c: Vertical(g6)
    c: Horizontal(g5)
    c: Horizontal(g7)
    c: Coincident(g8,g9)
    c: Coincident(g9,g10)
    c: Coincident(g10,g11)
    c: Coincident(g11,g8)
    c: Vertical(g8)
    c: Vertical(g10)
    c: Horizontal(g9)
    c: Horizontal(g11)
    c: Symmetric(g5,g8,g-2)
    c: DistanceX(g5,g8) = 500
    c: Equal(g7,g11)
    c: Equal(g11,g3)
    c: Horizontal(g4,g8)
    c: Horizontal(g8,g2)
    c: Horizontal(g4,g1)
    c: Coincident(g12,g13)
    c: Coincident(g13,g14)
    c: Coincident(g14,g15)
    c: Coincident(g15,g12)
    c: Vertical(g12)
    c: Vertical(g14)
    c: Horizontal(g13)
    c: Horizontal(g15)
FEATURE [PartDesign::Pad] Pad002
  BaseFeature = -> Pad001
  Direction = (0,0,1)
  Length = 250
  Length2 = 10
  Profile = -> Sketch002
  ReferenceAxis = -> Sketch002 [N_Axis]
  Refine = true
  Suppressed = false
  Type = 0
FEATURE [PartDesign::Plane] DatumPlane
  AttachmentOffset = pos=(0,0,1) rot=(0,0,1;0rad)
  AttachmentSupport = -> [Pad002]
  Length = 60
  MapMode = 5
  Placement = pos=(0,0,61) rot=(0,0,1;0rad)
  ResizeMode = 0
  Width = 60
FEATURE [Sketcher::SketchObject] Sketch003
  ArcFitTolerance = 1e-06
  AttachmentSupport = -> [Pad002]
  ExternalGeometry = -> [Pad002]
  FullyConstrained = false
  MakeInternals = false
  MapMode = 5
  Placement = pos=(0,0,60) rot=(0,0,1;0rad)
  sketch-geometry (5):
    g0: Circle CenterX=544 CenterY=-141.5 CenterZ=0 NormalX=0 NormalY=0 NormalZ=1 AngleXU=0 Radius=2
    g1: LineSegment [constr] StartX=549 StartY=-135.5 StartZ=0 EndX=549 EndY=-147.5 EndZ=0
    g2: GeomPoint X=549 Y=-141.5 Z=0
    g3: GeomPoint X=544 Y=-135.5 Z=0
    g4: Circle CenterX=-544 CenterY=-141.5 CenterZ=0 NormalX=0 NormalY=0 NormalZ=1 AngleXU=0 Radius=2
  constraints (9):
    c: Coincident(g1,g-4)
    c: PointOnObject(g1,g-3)
    c: Vertical(g1)
    c: Symmetric(g1,g1,g2)
    c: Horizontal(g2,g0)
    c: Symmetric(g-4,g1,g3)
    c: Vertical(g3,g0)
    c: Radius(g0) = 2
    c: Radius(g4) = 2
FEATURE [PartDesign::Pad] Pad003
  BaseFeature = -> Pad002
  Direction = (0,0,1)
  Length = 250
  Length2 = 10
  Profile = -> Sketch003
  ReferenceAxis = -> Sketch003 [N_Axis]
  Refine = true
  Suppressed = false
  Type = 0
FEATURE [Sketcher::SketchObject] Sketch004
  ArcFitTolerance = 1e-06
  AttachmentSupport = -> [DatumPlane]
  ExternalGeometry = -> [Pad003]
  FullyConstrained = false
  MakeInternals = false
  MapMode = 5
  Placement = pos=(0,0,61) rot=(0,0,1;0rad)
  sketch-geometry (8):
    g0: LineSegment StartX=-549 StartY=-136.5 StartZ=0 EndX=-549 EndY=-146.5 EndZ=0
    g1: LineSegment StartX=-549 StartY=-146.5 StartZ=0 EndX=-250 EndY=-146.5 EndZ=0
    g2: LineSegment StartX=-250 StartY=-146.5 StartZ=0 EndX=-250 EndY=-136.5 EndZ=0
    g3: LineSegment StartX=-250 StartY=-136.5 StartZ=0 EndX=-549 EndY=-136.5 EndZ=0
    g4: LineSegment StartX=549 StartY=-136.5 StartZ=0 EndX=549 EndY=-146.5 EndZ=0
    g5: LineSegment StartX=549 StartY=-146.5 StartZ=0 EndX=250 EndY=-146.5 EndZ=0
    g6: LineSegment StartX=250 StartY=-146.5 StartZ=0 EndX=250 EndY=-136.5 EndZ=0
    g7: LineSegment StartX=250 StartY=-136.5 StartZ=0 EndX=549 EndY=-136.5 EndZ=0
  constraints (20):
    c: Coincident(g0,g1)
    c: Coincident(g1,g2)
    c: Coincident(g2,g3)
    c: Coincident(g3,g0)
    c: Vertical(g0)
    c: Vertical(g2)
    c: Horizontal(g1)
    c: Horizontal(g3)
    c: Vertical(g2,g-5)
    c: Vertical(g0,g-3)
    c: DistanceY(g-4,g0) = 1
    c: DistanceY(g0,g0) = 10
    c: Coincident(g4,g5)
    c: Coincident(g5,g6)
    c: Coincident(g6,g7)
    c: Coincident(g7,g4)
    c: Vertical(g4)
    c: Vertical(g6)
    c: Horizontal(g5)
    c: Horizontal(g7)
FEATURE [PartDesign::Pad] Pad004
  BaseFeature = -> Pad003
  Direction = (0,0,1)
  Length = 248
  Length2 = 10
  Profile = -> Sketch004
  ReferenceAxis = -> Sketch004 [N_Axis]
  Refine = true
  Suppressed = false
  Type = 0
FEATURE [Sketcher::SketchObject] Sketch005
  ArcFitTolerance = 1e-06
  AttachmentSupport = -> [Pad004]
  ExternalGeometry = -> [Pad004]
  FullyConstrained = true
  MakeInternals = false
  MapMode = 5
  Placement = pos=(0,-135.5,0) rot=(1,0,0;1.5708rad)
  sketch-geometry (5):
    g0: LineSegment StartX=-250 StartY=190 StartZ=0 EndX=-250 EndY=180 EndZ=0
    g1: LineSegment StartX=-250 StartY=180 StartZ=0 EndX=250 EndY=180 EndZ=0
    g2: LineSegment StartX=250 StartY=180 StartZ=0 EndX=250 EndY=190 EndZ=0
    g3: LineSegment StartX=250 StartY=190 StartZ=0 EndX=-250 EndY=190 EndZ=0
    g4: GeomPoint X=-250 Y=185 Z=0
  constraints (12):
    c: Coincident(g0,g1)
    c: Coincident(g1,g2)
    c: Coincident(g2,g3)
    c: Coincident(g3,g0)
    c: Vertical(g0)
    c: Vertical(g2)
    c: Horizontal(g1)
    c: Horizontal(g3)
    c: PointOnObject(g1,g-4)
    c: DistanceY(g2,g2) = 10
    c: Symmetric(g-3,g-3,g4)
    c: Symmetric(g0,g0,g4)
FEATURE [PartDesign::Pad] Pad005
  BaseFeature = -> Pad004
  Direction = (0,-1,2e-16)
  Length = 275
  Length2 = 10
  Profile = -> Sketch005
  ReferenceAxis = -> Sketch005 [N_Axis]
  Reversed = true
  Suppressed = false
  Type = 0
FEATURE [Sketcher::SketchObject] Sketch006
  ArcFitTolerance = 1e-06
  AttachmentSupport = -> [Pad005]
  ExternalGeometry = -> [Pad005]
  FullyConstrained = false
  MakeInternals = false
  MapMode = 5
  Placement = pos=(0,0,60) rot=(0,0,1;0rad)
  sketch-geometry (8):
    g0: LineSegment StartX=-539 StartY=146.5 StartZ=0 EndX=-539 EndY=136.5 EndZ=0
    g1: LineSegment StartX=-539 StartY=136.5 StartZ=0 EndX=-260 EndY=136.5 EndZ=0
    g2: LineSegment StartX=-260 StartY=136.5 StartZ=0 EndX=-260 EndY=146.5 EndZ=0
    g3: LineSegment StartX=-260 StartY=146.5 StartZ=0 EndX=-539 EndY=146.5 EndZ=0
    g4: LineSegment StartX=539 StartY=146.5 StartZ=0 EndX=539 EndY=136.5 EndZ=0
    g5: LineSegment StartX=539 StartY=136.5 StartZ=0 EndX=260 EndY=136.5 EndZ=0
    g6: LineSegment StartX=260 StartY=136.5 StartZ=0 EndX=260 EndY=146.5 EndZ=0
    g7: LineSegment StartX=260 StartY=146.5 StartZ=0 EndX=539 EndY=146.5 EndZ=0
  constraints (19):
    c: Coincident(g0,g1)
    c: Coincident(g1,g2)
    c: Coincident(g2,g3)
    c: Coincident(g3,g0)
    c: Vertical(g0)
    c: Vertical(g2)
    c: Horizontal(g1)
    c: Horizontal(g3)
    c: Coincident(g0,g-3)
    c: PointOnObject(g1,g-4)
    c: DistanceY(g2,g2) = 10
    c: Coincident(g4,g5)
    c: Coincident(g5,g6)
    c: Coincident(g6,g7)
    c: Coincident(g7,g4)
    c: Vertical(g4)
    c: Vertical(g6)
    c: Horizontal(g5)
    c: Horizontal(g7)
FEATURE [PartDesign::Pad] Pad006
  BaseFeature = -> Pad005
  Direction = (0,0,1)
  Length = 250
  Length2 = 10
  Profile = -> Sketch006
  ReferenceAxis = -> Sketch006 [N_Axis]
  Suppressed = false
  Type = 0
FEATURE [Sketcher::SketchObject] Sketch007
  ArcFitTolerance = 1e-06
  AttachmentSupport = -> [Pad006]
  ExternalGeometry = -> [Pad006]
  FullyConstrained = true
  MakeInternals = false
  MapMode = 5
  Placement = pos=(0,0,310) rot=(0,0,1;0rad)
  sketch-geometry (4):
    g0: LineSegment StartX=-550 StartY=147.5 StartZ=0 EndX=-550 EndY=-147.5 EndZ=0
    g1: LineSegment StartX=-550 StartY=-147.5 StartZ=0 EndX=550 EndY=-147.5 EndZ=0
    g2: LineSegment StartX=550 StartY=-147.5 StartZ=0 EndX=550 EndY=147.5 EndZ=0
    g3: LineSegment StartX=550 StartY=147.5 StartZ=0 EndX=-550 EndY=147.5 EndZ=0
  constraints (10):
    c: Coincident(g0,g1)
    c: Coincident(g1,g2)
    c: Coincident(g2,g3)
    c: Coincident(g3,g0)
    c: Vertical(g0)
    c: Vertical(g2)
    c: Horizontal(g1)
    c: Horizontal(g3)
    c: Coincident(g0,g-3)
    c: Coincident(g1,g-4)
FEATURE [PartDesign::Pad] Pad007
  BaseFeature = -> Pad006
  Direction = (0,0,1)
  Length = 10
  Length2 = 10
  Profile = -> Sketch007
  ReferenceAxis = -> Sketch007 [N_Axis]
  Suppressed = false
  Type = 0
FEATURE [Sketcher::SketchObject] Sketch008
  ArcFitTolerance = 1e-06
  AttachmentSupport = -> [Pad007]
  FullyConstrained = false
  MakeInternals = false
  MapMode = 5
  Placement = pos=(0,0,320) rot=(0,0,1;0rad)
  sketch-geometry (4):
    g0: LineSegment StartX=-99.9826 StartY=172.692 StartZ=0 EndX=99.9826 EndY=172.692 EndZ=0
    g1: LineSegment StartX=99.9826 StartY=172.692 StartZ=0 EndX=55.785 EndY=129.303 EndZ=0
    g2: LineSegment StartX=55.785 StartY=129.303 StartZ=0 EndX=-55.785 EndY=129.303 EndZ=0
    g3: LineSegment StartX=-55.785 StartY=129.303 StartZ=0 EndX=-99.9826 EndY=172.692 EndZ=0
  constraints (6):
    c: Coincident(g0,g1)
    c: Coincident(g1,g2)
    c: Coincident(g2,g3)
    c: Coincident(g3,g0)
    c: Symmetric(g0,g0,g-2)
    c: Symmetric(g1,g2,g-2)
FEATURE [PartDesign::Pocket] Pocket
  BaseFeature = -> Pad007
  Direction = (0,0,-1)
  Length = 5
  Length2 = 5
  Profile = -> Sketch008
  ReferenceAxis = -> Sketch008 [N_Axis]
  Refine = true
  Suppressed = false
  Type = 1
FEATURE [PartDesign::Body] Body
  AllowCompound = false
  Group = -> [Sketch,Pad,Sketch001,Pad001,Sketch002,Pad002,DatumPlane,Sketch003,Pad003,Sketch004,Pad004,Sketch005,Pad005,Sketch006,Pad006,Sketch007,Pad007,Sketch008,Pocket]
  Origin = -> Origin
  Tip = -> Pocket
FEATURE [Part::FeaturePython] Clone  label="tvboard_clone"  # Draft clone (typed FeaturePython)
  AttacherType = Attacher::AttachEngine3D
  Fuse = false
  Objects = -> [Body]
  Scale = (1,1,1)
FEATURE [App::Part] Part  label="tvboard"
  Group = -> [Clone]
  Origin = -> Origin001
---- part ../wall1500/wall1500.FCStd = doc fcstd_a3cc7dd72291 ----
FCSTD DOCUMENT  (FreeCAD 1.0R39109 (Git))
Label: wall1500
License: All rights reserved
LicenseURL: https://en.wikipedia.org/wiki/All_rights_reserved
objects: Sketcher::SketchObject×1, PartDesign::Pad×1, PartDesign::Body×1, Part::FeaturePython×1, App::Part×1
note: 7 computed .brp shape members not serialized (recipe doc carries the construction recipe); baked Part::Feature solids carry a one-line shape summary decoded from their .brp

FEATURE [Sketcher::SketchObject] Sketch
  ArcFitTolerance = 1e-06
  AttachmentSupport = -> [XY_Plane]
  FullyConstrained = true
  MakeInternals = false
  MapMode = 5
  sketch-geometry (5):
    g0: LineSegment StartX=-750 StartY=-50 StartZ=0 EndX=750 EndY=-50 EndZ=0
    g1: LineSegment StartX=750 StartY=-50 StartZ=0 EndX=750 EndY=50 EndZ=0
    g2: LineSegment StartX=750 StartY=50 StartZ=0 EndX=-750 EndY=50 EndZ=0
    g3: LineSegment StartX=-750 StartY=50 StartZ=0 EndX=-750 EndY=-50 EndZ=0
    g4: GeomPoint [constr] X=0 Y=0 Z=0
  constraints (12):
    c: Coincident(g0,g1)
    c: Coincident(g1,g2)
    c: Coincident(g2,g3)
    c: Coincident(g3,g0)
    c: Horizontal(g0)
    c: Horizontal(g2)
    c: Vertical(g1)
    c: Vertical(g3)
    c: Symmetric(g2,g0,g4)
    c: Distance(g1,g3) = 1500
    c: Distance(g0,g2) = 100
    c: Coincident(g4,g-1)
FEATURE [PartDesign::Pad] Pad
  Direction = (0,0,1)
  Length = 3000
  Length2 = 10
  Profile = -> Sketch
  ReferenceAxis = -> Sketch [N_Axis]
  Refine = true
  Suppressed = false
  Type = 0
FEATURE [PartDesign::Body] Body
  AllowCompound = false
  Group = -> [Sketch,Pad]
  Origin = -> Origin
  Tip = -> Pad
FEATURE [Part::FeaturePython] Clone  label="wall1500_clone"  # Draft clone (typed FeaturePython)
  AttacherType = Attacher::AttachEngine3D
  Fuse = false
  Objects = -> [Body]
  Scale = (1,1,1)
FEATURE [App::Part] Part  label="wall1500"
  Group = -> [Clone]
  Origin = -> Origin001
---- part ../washing_machine/washing_machine.FCStd = doc fcstd_0f4833736901 ----
FCSTD DOCUMENT  (FreeCAD 1.0R39109 (Git))
Label: washingmachine
License: All rights reserved
LicenseURL: https://en.wikipedia.org/wiki/All_rights_reserved
objects: Sketcher::SketchObject×21, PartDesign::ShapeBinder×19, PartDesign::Pad×16, PartDesign::Fillet×13, PartDesign::Line×11, PartDesign::Plane×7, PartDesign::Body×7, Part::FeaturePython×7, PartDesign::Pocket×5, PartDesign::Chamfer×3, App::Part×1
note: 204 computed .brp shape members not serialized (recipe doc carries the construction recipe); baked Part::Feature solids carry a one-line shape summary decoded from their .brp

FEATURE [Sketcher::SketchObject] Sketch
  ArcFitTolerance = 1e-06
  AttachmentSupport = -> [XY_Plane]
  FullyConstrained = true
  MakeInternals = false
  MapMode = 5
  sketch-geometry (5):
    g0: LineSegment StartX=-380 StartY=-210 StartZ=0 EndX=380 EndY=-210 EndZ=0
    g1: LineSegment StartX=380 StartY=-210 StartZ=0 EndX=380 EndY=210 EndZ=0
    g2: LineSegment StartX=380 StartY=210 StartZ=0 EndX=-380 EndY=210 EndZ=0
    g3: LineSegment StartX=-380 StartY=210 StartZ=0 EndX=-380 EndY=-210 EndZ=0
    g4: GeomPoint [constr] X=0 Y=0 Z=0
  constraints (12):
    c: Coincident(g0,g1)
    c: Coincident(g1,g2)
    c: Coincident(g2,g3)
    c: Coincident(g3,g0)
    c: Horizontal(g0)
    c: Horizontal(g2)
    c: Vertical(g1)
    c: Vertical(g3)
    c: Symmetric(g2,g0,g4)
    c: Coincident(g4,g-1)
    c: DistanceX(g2,g2) = 760
    c: DistanceY(g1,g1) = 420
FEATURE [PartDesign::Pad] Pad
  Direction = (0,0,1)
  Length = 100
  Length2 = 10
  Profile = -> Sketch
  ReferenceAxis = -> Sketch [N_Axis]
  Refine = true
  Suppressed = false
  Type = 0
FEATURE [Sketcher::SketchObject] Sketch001
  ArcFitTolerance = 1e-06
  AttachmentSupport = -> [Pad]
  FullyConstrained = true
  MakeInternals = false
  MapMode = 5
  Placement = pos=(0,0,100) rot=(0,0,1;0rad)
  sketch-geometry (5):
    g0: LineSegment StartX=-390 StartY=-220 StartZ=0 EndX=390 EndY=-220 EndZ=0
    g1: LineSegment StartX=390 StartY=-220 StartZ=0 EndX=390 EndY=220 EndZ=0
    g2: LineSegment StartX=390 StartY=220 StartZ=0 EndX=-390 EndY=220 EndZ=0
    g3: LineSegment StartX=-390 StartY=220 StartZ=0 EndX=-390 EndY=-220 EndZ=0
    g4: GeomPoint [constr] X=0 Y=0 Z=0
  constraints (12):
    c: Coincident(g0,g1)
    c: Coincident(g1,g2)
    c: Coincident(g2,g3)
    c: Coincident(g3,g0)
    c: Horizontal(g0)
    c: Horizontal(g2)
    c: Vertical(g1)
    c: Vertical(g3)
    c: Symmetric(g2,g0,g4)
    c: Distance(g1,g3) = 780
    c: Distance(g0,g2) = 440
    c: Coincident(g4,g-1)
FEATURE [PartDesign::Pad] Pad001
  BaseFeature = -> Pad
  Direction = (0,0,1)
  Length = 740
  Length2 = 10
  Profile = -> Sketch001
  ReferenceAxis = -> Sketch001 [N_Axis]
  Refine = true
  Suppressed = false
  Type = 0
FEATURE [Sketcher::SketchObject] Sketch002
  ArcFitTolerance = 1e-06
  AttachmentSupport = -> [Pad001]
  ExternalGeometry = -> [Pad001]
  FullyConstrained = false
  MakeInternals = false
  MapMode = 5
  Placement = pos=(0,0,840) rot=(0,0,1;0rad)
  sketch-geometry (9):
    g0: LineSegment StartX=-390 StartY=116.893 StartZ=0 EndX=-390 EndY=-220 EndZ=0
    g1: LineSegment StartX=-390 StartY=-220 StartZ=0 EndX=30 EndY=-220 EndZ=0
    g2: LineSegment StartX=30 StartY=-220 StartZ=0 EndX=30 EndY=116.893 EndZ=0
    g3: LineSegment [constr] StartX=30 StartY=220 StartZ=0 EndX=40 EndY=220 EndZ=0
    g4: LineSegment StartX=40 StartY=116.893 StartZ=0 EndX=40 EndY=-220 EndZ=0
    g5: LineSegment StartX=40 StartY=-220 StartZ=0 EndX=390 EndY=-220 EndZ=0
    g6: LineSegment StartX=390 StartY=-220 StartZ=0 EndX=390 EndY=116.893 EndZ=0
    g7: LineSegment StartX=-390 StartY=116.893 StartZ=0 EndX=30 EndY=116.893 EndZ=0
    g8: LineSegment StartX=40 StartY=116.893 StartZ=0 EndX=390 EndY=116.893 EndZ=0
  constraints (20):
    c: Coincident(g0,g1)
    c: Coincident(g1,g2)
    c: Vertical(g0)
    c: Vertical(g2)
    c: Horizontal(g1)
    c: Distance(g1,g-3) = 440
    c: Distance(g3) = 10
    c: PointOnObject(g3,g-3)
    c: Coincident(g4,g5)
    c: Coincident(g5,g6)
    c: Vertical(g4)
    c: Vertical(g6)
    c: Horizontal(g5)
    c: Coincident(g5,g-4)
    c: Horizontal(g7)
    c: Coincident(g0,g7)
    c: Coincident(g2,g7)
    c: Horizontal(g8)
    c: Coincident(g8,g4)
    c: Coincident(g8,g6)
FEATURE [PartDesign::Pad] Pad002
  BaseFeature = -> Pad001
  Direction = (0,0,1)
  Length = 10
  Length2 = 10
  Profile = -> Sketch002
  ReferenceAxis = -> Sketch002 [N_Axis]
  Suppressed = false
  Type = 0
FEATURE [Sketcher::SketchObject] Sketch003
  ArcFitTolerance = 1e-06
  AttachmentSupport = -> [Pad002]
  ExternalGeometry = -> [Pad002]
  FullyConstrained = false
  MakeInternals = false
  MapMode = 5
  Placement = pos=(0,0,840) rot=(0,0,1;0rad)
  sketch-geometry (8):
    g0: LineSegment StartX=390 StartY=116.893 StartZ=0 EndX=390 EndY=220 EndZ=0
    g1: LineSegment StartX=390 StartY=220 StartZ=0 EndX=-390 EndY=220 EndZ=0
    g2: LineSegment StartX=-390 StartY=220 StartZ=0 EndX=-390 EndY=116.893 EndZ=0
    g3: LineSegment StartX=-390 StartY=116.893 StartZ=0 EndX=-297.073 EndY=116.893 EndZ=0
    g4: LineSegment StartX=-297.073 StartY=116.893 StartZ=0 EndX=-297.073 EndY=195.064 EndZ=0
    g5: LineSegment StartX=-297.073 StartY=195.064 StartZ=0 EndX=79.089 EndY=195.064 EndZ=0
    g6: LineSegment StartX=79.089 StartY=195.064 StartZ=0 EndX=79.089 EndY=116.893 EndZ=0
    g7: LineSegment StartX=79.089 StartY=116.893 StartZ=0 EndX=390 EndY=116.893 EndZ=0
  constraints (17):
    c: Coincident(g0,g1)
    c: Coincident(g1,g2)
    c: Horizontal(g1)
    c: Vertical(g0)
    c: Vertical(g2)
    c: Coincident(g0,g-5)
    c: Coincident(g3,g2)
    c: PointOnObject(g3,g-4)
    c: Horizontal(g3)
    c: Coincident(g4,g3)
    c: Vertical(g4)
    c: Horizontal(g5)
    c: PointOnObject(g6,g-3)
    c: Vertical(g6)
    c: Coincident(g7,g6)
    c: Coincident(g7,g0)
    c: Horizontal(g7)
FEATURE [PartDesign::Pad] Pad003
  BaseFeature = -> Pad002
  Direction = (0,0,1)
  Length = 80
  Length2 = 10
  Profile = -> Sketch003
  ReferenceAxis = -> Sketch003 [N_Axis]
  Suppressed = false
  Type = 0
FEATURE [Sketcher::SketchObject] Sketch004
  ArcFitTolerance = 1e-06
  AttachmentSupport = -> [Pad003]
  ExternalGeometry = -> [Pad003]
  FullyConstrained = false
  MakeInternals = false
  MapMode = 5
  Placement = pos=(0,0,840) rot=(0,0,1;0rad)
  sketch-geometry (4):
    g0: Circle CenterX=-236.553 CenterY=155.978 CenterZ=0 NormalX=0 NormalY=0 NormalZ=1 AngleXU=0 Radius=19.0264
    g1: Circle CenterX=17.148 CenterY=155.978 CenterZ=0 NormalX=0 NormalY=0 NormalZ=1 AngleXU=0 Radius=19.0264
    g2: Circle CenterX=-153.083 CenterY=155.978 CenterZ=0 NormalX=0 NormalY=0 NormalZ=1 AngleXU=0 Radius=19.0264
    g3: LineSegment [constr] StartX=-297.073 StartY=155.978 StartZ=0 EndX=79.089 EndY=155.978 EndZ=0
  constraints (7):
    c: Symmetric(g-3,g-3,g3)
    c: Symmetric(g-4,g-4,g3)
    c: PointOnObject(g2,g3)
    c: PointOnObject(g0,g3)
    c: PointOnObject(g1,g3)
    c: Equal(g0,g2)
    c: Equal(g2,g1)
FEATURE [PartDesign::Pad] Pad004
  BaseFeature = -> Pad003
  Direction = (0,0,1)
  Length = 3
  Length2 = 10
  Profile = -> Sketch004
  ReferenceAxis = -> Sketch004 [N_Axis]
  Suppressed = false
  Type = 0
FEATURE [Sketcher::SketchObject] Sketch005
  ArcFitTolerance = 1e-06
  AttachmentSupport = -> [Pad004]
  ExternalGeometry = -> [Pad004]
  FullyConstrained = false
  MakeInternals = false
  MapMode = 5
  Placement = pos=(0,0,843) rot=(0,0,1;0rad)
  sketch-geometry (3):
    g0: Circle CenterX=-236.553 CenterY=155.978 CenterZ=0 NormalX=0 NormalY=0 NormalZ=1 AngleXU=0 Radius=29.3345
    g1: Circle CenterX=-153.083 CenterY=155.978 CenterZ=0 NormalX=0 NormalY=0 NormalZ=1 AngleXU=0 Radius=29.3345
    g2: Circle CenterX=17.148 CenterY=155.978 CenterZ=0 NormalX=0 NormalY=0 NormalZ=1 AngleXU=0 Radius=29.3345
  constraints (5):
    c: Coincident(g0,g-3)
    c: Coincident(g1,g-4)
    c: Coincident(g2,g-5)
    c: Equal(g0,g1)
    c: Equal(g1,g2)
FEATURE [PartDesign::Pad] Pad005
  BaseFeature = -> Pad004
  Direction = (0,0,1)
  Length = 3
  Length2 = 10
  Profile = -> Sketch005
  ReferenceAxis = -> Sketch005 [N_Axis]
  Suppressed = false
  Type = 0
FEATURE [Sketcher::SketchObject] Sketch006
  ArcFitTolerance = 1e-06
  AttachmentSupport = -> [Pad005]
  ExternalGeometry = -> [Pad005]
  FullyConstrained = false
  MakeInternals = false
  MapMode = 5
  Placement = pos=(0,0,846) rot=(0,0,1;0rad)
  sketch-geometry (12):
    g0: ArcOfCircle CenterX=-236.553 CenterY=135.079 CenterZ=0 NormalX=0 NormalY=0 NormalZ=1 AngleXU=0 Radius=5.28796 StartAngle=3.14159 EndAngle=6.28319
    g1: ArcOfCircle CenterX=-236.553 CenterY=176.878 CenterZ=0 NormalX=0 NormalY=0 NormalZ=1 AngleXU=0 Radius=5.28796 StartAngle=-2.7e-15 EndAngle=3.14159
    g2: LineSegment StartX=-241.841 StartY=135.079 StartZ=0 EndX=-241.841 EndY=176.878 EndZ=0
    g3: LineSegment StartX=-231.265 StartY=135.079 StartZ=0 EndX=-231.265 EndY=176.878 EndZ=0
    g4: ArcOfCircle CenterX=-153.083 CenterY=135.079 CenterZ=0 NormalX=0 NormalY=0 NormalZ=1 AngleXU=0 Radius=5.28796 StartAngle=3.14159 EndAngle=6.28319
    g5: ArcOfCircle CenterX=-153.083 CenterY=176.878 CenterZ=0 NormalX=0 NormalY=0 NormalZ=1 AngleXU=0 Radius=5.28796 StartAngle=-1.8e-15 EndAngle=3.14159
    g6: LineSegment StartX=-158.371 StartY=135.079 StartZ=0 EndX=-158.371 EndY=176.878 EndZ=0
    g7: LineSegment StartX=-147.795 StartY=135.079 StartZ=0 EndX=-147.795 EndY=176.878 EndZ=0
    g8: ArcOfCircle CenterX=17.148 CenterY=135.079 CenterZ=0 NormalX=0 NormalY=0 NormalZ=1 AngleXU=0 Radius=5.28796 StartAngle=3.14159 EndAngle=6.28319
    g9: ArcOfCircle CenterX=17.148 CenterY=176.878 CenterZ=0 NormalX=0 NormalY=0 NormalZ=1 AngleXU=0 Radius=5.28796 StartAngle=2.2e-15 EndAngle=3.14159
    g10: LineSegment StartX=11.86 StartY=135.079 StartZ=0 EndX=11.86 EndY=176.878 EndZ=0
    g11: LineSegment StartX=22.4359 StartY=135.079 StartZ=0 EndX=22.4359 EndY=176.878 EndZ=0
  constraints (25):
    c: Tangent(g0,g2) = 1.5708
    c: Tangent(g0,g3) = -1.5708
    c: Tangent(g1,g2) = 1.5708
    c: Tangent(g1,g3) = -1.5708
    c: Equal(g0,g1)
    c: Vertical(g2)
    c: Symmetric(g1,g0,g-3)
    c: Tangent(g4,g6) = 1.5708
    c: Tangent(g4,g7) = -1.5708
    c: Tangent(g5,g6) = 1.5708
    c: Tangent(g5,g7) = -1.5708
    c: Equal(g4,g5)
    c: Tangent(g8,g10) = 1.5708
    c: Tangent(g8,g11) = -1.5708
    c: Tangent(g9,g10) = 1.5708
    c: Tangent(g9,g11) = -1.5708
    c: Equal(g8,g9)
    c: Vertical(g10)
    c: Symmetric(g9,g8,g-5)
    c: Symmetric(g5,g4,g-4)
    c: Equal(g3,g6)
    c: Equal(g6,g10)
    c: Equal(g9,g5)
    c: Equal(g5,g1)
    c: Vertical(g7)
FEATURE [PartDesign::Pad] Pad006
  BaseFeature = -> Pad005
  Direction = (0,0,1)
  Length = 15
  Length2 = 10
  Profile = -> Sketch006
  ReferenceAxis = -> Sketch006 [N_Axis]
  Suppressed = false
  Type = 0
FEATURE [PartDesign::Fillet] Fillet
  Base = -> Pad006 [Edge65,Edge79,Edge69,Edge71,Edge63,Edge70,Edge80]
  BaseFeature = -> Pad006
  Radius = 5
  SupportTransform = false
  Suppressed = false
  UseAllEdges = false
FEATURE [PartDesign::Fillet] Fillet001
  Base = -> Fillet [Edge61,Edge78,Edge60,Edge73,Edge74]
  BaseFeature = -> Fillet
  Radius = 10
  SupportTransform = false
  Suppressed = false
  UseAllEdges = false
FEATURE [PartDesign::Fillet] Fillet002
  Base = -> Fillet001 [Edge50,Edge41,Edge42,Edge72,Edge59,Edge14]
  BaseFeature = -> Fillet001
  Radius = 10
  SupportTransform = false
  Suppressed = false
  UseAllEdges = false
FEATURE [PartDesign::Fillet] Fillet003
  Base = -> Fillet002 [Edge130,Edge132,Edge129,Edge134]
  BaseFeature = -> Fillet002
  Radius = 10
  SupportTransform = false
  Suppressed = false
  UseAllEdges = false
FEATURE [PartDesign::Fillet] Fillet004
  Base = -> Fillet003 [Edge80,Edge88]
  BaseFeature = -> Fillet003
  Radius = 5
  SupportTransform = false
  Suppressed = false
  UseAllEdges = false
FEATURE [PartDesign::Fillet] Fillet005
  Base = -> Fillet004 [Edge194,Edge198,Edge202,Edge220,Edge212,Edge228]
  BaseFeature = -> Fillet004
  Radius = 2
  SupportTransform = false
  Suppressed = false
  UseAllEdges = false
FEATURE [PartDesign::Fillet] Fillet006
  Base = -> Fillet005 [Edge190,Edge192,Edge5]
  BaseFeature = -> Fillet005
  Radius = 1
  SupportTransform = false
  Suppressed = false
  UseAllEdges = false
FEATURE [PartDesign::ShapeBinder] CopyFillet006
  TraceSupport = false
FEATURE [PartDesign::Plane] DatumPlane
  AttachmentSupport = -> [CopyFillet006]
  Length = 495.232
  MapMode = 5
  Placement = pos=(0,0,850) rot=(0,0,1;0rad)
  ResizeMode = 0
  Width = 412.124
FEATURE [PartDesign::ShapeBinder] CopyFillet007
  TraceSupport = false
FEATURE [PartDesign::Plane] DatumPlane001
  AttachmentSupport = -> [CopyFillet007]
  Length = 495.232
  MapMode = 5
  Placement = pos=(0,0,850) rot=(0,0,1;0rad)
  ResizeMode = 0
  Width = 412.124
FEATURE [PartDesign::ShapeBinder] CopyFillet008
  TraceSupport = false
FEATURE [Sketcher::SketchObject] Sketch007
  ArcFitTolerance = 1e-06
  AttachmentSupport = -> [CopyFillet008]
  ExternalGeometry = -> [CopyFillet006,CopyFillet007]
  FullyConstrained = false
  MakeInternals = false
  MapMode = 5
  Placement = pos=(0,0,850) rot=(0,0,1;0rad)
  sketch-geometry (12):
    g0: LineSegment [constr] StartX=30 StartY=-210 StartZ=0 EndX=30 EndY=-220 EndZ=0
    g1: LineSegment [constr] StartX=40 StartY=-210 StartZ=0 EndX=40.1423 EndY=-219.833 EndZ=0
    g2: LineSegment [constr] StartX=20 StartY=-220 StartZ=0 EndX=30 EndY=-220 EndZ=0
    g3: LineSegment [constr] StartX=50 StartY=-220 StartZ=0 EndX=40.1423 EndY=-219.833 EndZ=0
    g4: LineSegment StartX=-390 StartY=116.893 StartZ=0 EndX=-390 EndY=-210 EndZ=0
    g5: LineSegment StartX=-380 StartY=-220 StartZ=0 EndX=20 EndY=-220 EndZ=0
    g6: LineSegment StartX=30 StartY=-210 StartZ=0 EndX=30 EndY=116.893 EndZ=0
    g7: LineSegment StartX=30 StartY=116.893 StartZ=0 EndX=-390 EndY=116.893 EndZ=0
    g8: ArcOfCircle CenterX=-380 CenterY=-210 CenterZ=0 NormalX=0 NormalY=0 NormalZ=1 AngleXU=0 Radius=10 StartAngle=3.14159 EndAngle=4.71239
    g9: ArcOfCircle CenterX=20 CenterY=-210 CenterZ=0 NormalX=0 NormalY=0 NormalZ=1 AngleXU=0 Radius=10 StartAngle=4.71239 EndAngle=6.28319
    g10: GeomPoint [constr] X=-390 Y=116.893 Z=0
    g11: GeomPoint [constr] X=30 Y=-220 Z=0
  constraints (21):
    c: Coincident(g0,g-11)
    c: Vertical(g0)
    c: Coincident(g2,g-4)
    c: Horizontal(g2)
    c: Coincident(g0,g2)
    c: PointOnObject(g1,g3)
    c: Tangent(g4,g8) = -1.5708
    c: Tangent(g5,g8) = -1.5708
    c: Tangent(g5,g9) = -1.5708
    c: Tangent(g6,g9) = -1.5708
    c: Vertical(g4)
    c: Vertical(g6)
    c: Horizontal(g5)
    c: Equal(g8,g9)
    c: PointOnObject(g11,g5)
    c: Coincident(g10,g-14)
    c: Coincident(g11,g0)
    c: Coincident(g7,g10)
    c: Coincident(g4,g7)
    c: Coincident(g6,g-12)
    c: Coincident(g7,g6)
FEATURE [PartDesign::ShapeBinder] CopyCopyFillet007
  TraceSupport = false
FEATURE [PartDesign::Plane] DatumPlane002
  AttachmentSupport = -> [CopyCopyFillet007]
  Length = 490.335
  MapMode = 5
  Placement = pos=(0,0,850) rot=(0,0,1;0rad)
  ResizeMode = 0
  Width = 417.228
FEATURE [Sketcher::SketchObject] Sketch008
  ArcFitTolerance = 1e-06
  AttachmentSupport = -> [DatumPlane002]
  ExternalGeometry = -> [CopyCopyFillet007]
  FullyConstrained = false
  MakeInternals = false
  MapMode = 5
  Placement = pos=(0,0,850) rot=(0,0,1;0rad)
  sketch-geometry (10):
    g0: LineSegment [constr] StartX=40 StartY=-210 StartZ=0 EndX=40 EndY=-220 EndZ=0
    g1: LineSegment [constr] StartX=50 StartY=-220 StartZ=0 EndX=40 EndY=-220 EndZ=0
    g2: LineSegment StartX=390 StartY=116.893 StartZ=0 EndX=40 EndY=116.893 EndZ=0
    g3: LineSegment StartX=40 StartY=116.893 StartZ=0 EndX=40 EndY=-210 EndZ=0
    g4: LineSegment StartX=50 StartY=-220 StartZ=0 EndX=380 EndY=-220 EndZ=0
    g5: LineSegment StartX=390 StartY=-210 StartZ=0 EndX=390 EndY=116.893 EndZ=0
    g6: ArcOfCircle CenterX=50 CenterY=-210 CenterZ=0 NormalX=0 NormalY=0 NormalZ=1 AngleXU=0 Radius=10 StartAngle=3.14159 EndAngle=4.71239
    g7: ArcOfCircle CenterX=380 CenterY=-210 CenterZ=0 NormalX=0 NormalY=0 NormalZ=1 AngleXU=0 Radius=10 StartAngle=4.71239 EndAngle=6.28319
    g8: GeomPoint [constr] X=390 Y=116.893 Z=0
    g9: GeomPoint [constr] X=40 Y=-220 Z=0
  constraints (20):
    c: Coincident(g0,g-6)
    c: Vertical(g0)
    c: Coincident(g1,g-6)
    c: Horizontal(g1)
    c: Coincident(g0,g1)
    c: Tangent(g3,g6) = -1.5708
    c: Tangent(g4,g6) = -1.5708
    c: Tangent(g4,g7) = -1.5708
    c: Tangent(g5,g7) = -1.5708
    c: Horizontal(g4)
    c: Vertical(g3)
    c: Vertical(g5)
    c: Equal(g6,g7)
    c: PointOnObject(g9,g4)
    c: Coincident(g8,g-5)
    c: Coincident(g9,g0)
    c: Coincident(g2,g-3)
    c: Coincident(g3,g2)
    c: Coincident(g8,g5)
    c: Coincident(g2,g5)
FEATURE [PartDesign::Pad] Pad007
  Direction = (0,0,1)
  Length = 10
  Length2 = 10
  Placement = pos=(0,0,850) rot=(0,0,1;0rad)
  Profile = -> Sketch008
  ReferenceAxis = -> Sketch008 [N_Axis]
  Refine = true
  Reversed = true
  Suppressed = false
  Type = 0
FEATURE [PartDesign::Body] Body002
  AllowCompound = false
  Group = -> [DatumPlane002,CopyCopyFillet007,Sketch008,Pad007]
  Origin = -> Origin002
  Tip = -> Pad007
FEATURE [PartDesign::Pad] Pad008
  Direction = (0,0,1)
  Length = 10
  Length2 = 10
  Profile = -> Sketch007
  ReferenceAxis = -> Sketch007 [N_Axis]
  Refine = true
  Reversed = true
  Suppressed = false
  Type = 0
FEATURE [PartDesign::Body] Body001
  AllowCompound = false
  Group = -> [DatumPlane,CopyFillet006,DatumPlane001,CopyFillet007,CopyFillet008,Sketch007,Pad008]
  Origin = -> Origin001
  Tip = -> Pad008
FEATURE [Sketcher::SketchObject] Sketch009
  ArcFitTolerance = 1e-06
  AttachmentSupport = -> [Fillet006]
  ExternalGeometry = -> [Fillet006]
  FullyConstrained = false
  MakeInternals = false
  MapMode = 5
  Placement = pos=(0,0,850) rot=(0,0,1;0rad)
  sketch-geometry (13):
    g0: LineSegment StartX=-385 StartY=116.893 StartZ=0 EndX=-302.073 EndY=116.893 EndZ=0
    g1: ArcOfCircle CenterX=-385 CenterY=121.893 CenterZ=0 NormalX=0 NormalY=0 NormalZ=1 AngleXU=0 Radius=5 StartAngle=3.14159 EndAngle=4.71239
    g2: ArcOfCircle CenterX=-302.073 CenterY=121.893 CenterZ=0 NormalX=0 NormalY=0 NormalZ=1 AngleXU=0 Radius=5 StartAngle=4.71239 EndAngle=6.28319
    g3: GeomPoint [constr] X=-390 Y=116.893 Z=0
    g4: GeomPoint [constr] X=-297.073 Y=185.064 Z=0
    g5: LineSegment [constr] StartX=-390 StartY=-210 StartZ=0 EndX=-390 EndY=-220 EndZ=0
    g6: LineSegment [constr] StartX=-380 StartY=-220 StartZ=0 EndX=-390 EndY=-220 EndZ=0
    g7: LineSegment StartX=-390 StartY=-220 StartZ=0 EndX=30 EndY=-220 EndZ=0
    g8: LineSegment StartX=30 StartY=-220 StartZ=0 EndX=30 EndY=116.893 EndZ=0
    g9: LineSegment StartX=-390 StartY=116.893 StartZ=0 EndX=-390 EndY=-220 EndZ=0
    g10: LineSegment StartX=-390 StartY=116.893 StartZ=0 EndX=-390 EndY=121.893 EndZ=0
    g11: LineSegment StartX=-297.073 StartY=121.893 StartZ=0 EndX=-297.073 EndY=116.893 EndZ=0
    g12: LineSegment StartX=-297.073 StartY=116.893 StartZ=0 EndX=30 EndY=116.893 EndZ=0
  constraints (26):
    c: Tangent(g0,g1) = -1.5708
    c: Tangent(g0,g2) = -1.5708
    c: Horizontal(g0)
    c: Equal(g1,g2)
    c: PointOnObject(g3,g0)
    c: Coincident(g3,g-3)
    c: Coincident(g4,g-10)
    c: Coincident(g5,g-5)
    c: Vertical(g5)
    c: Tangent(g6,g-6) = 1.5708
    c: Coincident(g5,g6)
    c: Coincident(g7,g8)
    c: Coincident(g9,g7)
    c: Horizontal(g7)
    c: Vertical(g8)
    c: Vertical(g9)
    c: Coincident(g7,g5)
    c: Coincident(g8,g-4)
    c: Coincident(g10,g9)
    c: Coincident(g10,g1)
    c: Vertical(g10)
    c: Tangent(g11,g2) = 1.5708
    c: Coincident(g11,g-11)
    c: Vertical(g11)
    c: Coincident(g12,g11)
    c: Coincident(g12,g8)
FEATURE [PartDesign::Pocket] Pocket
  BaseFeature = -> Fillet006
  Direction = (0,0,-1)
  Length = 10
  Length2 = 5
  Profile = -> Sketch009
  ReferenceAxis = -> Sketch009 [N_Axis]
  Refine = true
  Suppressed = false
  Type = 0
FEATURE [Sketcher::SketchObject] Sketch010
  ArcFitTolerance = 1e-06
  AttachmentSupport = -> [Pocket]
  ExternalGeometry = -> [Pocket]
  FullyConstrained = false
  MakeInternals = false
  MapMode = 5
  Placement = pos=(0,0,850) rot=(0,0,1;0rad)
  sketch-geometry (18):
    g0: LineSegment StartX=84.089 StartY=116.893 StartZ=0 EndX=385 EndY=116.893 EndZ=0
    g1: ArcOfCircle CenterX=84.089 CenterY=121.893 CenterZ=0 NormalX=0 NormalY=0 NormalZ=1 AngleXU=0 Radius=5 StartAngle=3.14159 EndAngle=4.71239
    g2: ArcOfCircle CenterX=385 CenterY=121.893 CenterZ=0 NormalX=0 NormalY=0 NormalZ=1 AngleXU=0 Radius=5 StartAngle=4.71239 EndAngle=6.28319
    g3: GeomPoint [constr] X=390 Y=210 Z=0
    g4: GeomPoint [constr] X=79.089 Y=116.893 Z=0
    g5: LineSegment StartX=79.089 StartY=121.893 StartZ=0 EndX=79.089 EndY=116.893 EndZ=0
    g6: LineSegment [constr] StartX=390 StartY=-210 StartZ=0 EndX=390 EndY=-220 EndZ=0
    g7: LineSegment [constr] StartX=380 StartY=-220 StartZ=0 EndX=390 EndY=-220 EndZ=0
    g8: LineSegment StartX=40 StartY=106.893 StartZ=0 EndX=40 EndY=-210 EndZ=0
    g9: LineSegment StartX=50 StartY=-220 StartZ=0 EndX=380 EndY=-220 EndZ=0
    g10: LineSegment StartX=390 StartY=-210 StartZ=0 EndX=390 EndY=106.893 EndZ=0
    g11: ArcOfCircle CenterX=50 CenterY=-210 CenterZ=0 NormalX=0 NormalY=0 NormalZ=1 AngleXU=0 Radius=10 StartAngle=3.14159 EndAngle=4.71239
    g12: ArcOfCircle CenterX=380 CenterY=-210 CenterZ=0 NormalX=0 NormalY=0 NormalZ=1 AngleXU=0 Radius=10 StartAngle=4.71239 EndAngle=6.28319
    g13: GeomPoint [constr] X=40 Y=116.893 Z=0
    g14: GeomPoint [constr] X=390 Y=-220 Z=0
    g15: LineSegment StartX=390 StartY=106.893 StartZ=0 EndX=390 EndY=121.893 EndZ=0
    g16: LineSegment StartX=40 StartY=106.893 StartZ=0 EndX=40 EndY=116.893 EndZ=0
    g17: LineSegment StartX=79.089 StartY=116.893 StartZ=0 EndX=40 EndY=116.893 EndZ=0
  constraints (35):
    c: Tangent(g0,g1) = -1.5708
    c: Tangent(g0,g2) = -1.5708
    c: Horizontal(g0)
    c: Equal(g1,g2)
    c: PointOnObject(g4,g0)
    c: Coincident(g3,g-12)
    c: Coincident(g4,g-8)
    c: Coincident(g5,g1)
    c: Coincident(g5,g4)
    c: Vertical(g5)
    c: Coincident(g6,g-12)
    c: Vertical(g6)
    c: Coincident(g7,g-6)
    c: Horizontal(g7)
    c: Coincident(g6,g7)
    c: Tangent(g8,g11) = -1.5708
    c: Tangent(g9,g11) = -1.5708
    c: Tangent(g9,g12) = -1.5708
    c: Tangent(g10,g12) = -1.5708
    c: Vertical(g8)
    c: Vertical(g10)
    c: Horizontal(g9)
    c: Equal(g11,g12)
    c: PointOnObject(g13,g8)
    c: PointOnObject(g14,g9)
    c: PointOnObject(g14,g10)
    c: Coincident(g13,g-8)
    c: Coincident(g14,g6)
    c: Coincident(g15,g10)
    c: Coincident(g15,g2)
    c: Vertical(g15)
    c: Coincident(g16,g8)
    c: Coincident(g16,g13)
    c: Coincident(g17,g4)
    c: Coincident(g17,g13)
FEATURE [PartDesign::Pocket] Pocket001
  BaseFeature = -> Pocket
  Direction = (0,0,-1)
  Length = 10
  Length2 = 5
  Profile = -> Sketch010
  ReferenceAxis = -> Sketch010 [N_Axis]
  Refine = true
  Suppressed = false
  Type = 0
FEATURE [Sketcher::SketchObject] Sketch011
  ArcFitTolerance = 1e-06
  AttachmentSupport = -> [Pocket001]
  ExternalGeometry = -> [Pocket001]
  FullyConstrained = false
  MakeInternals = false
  MapMode = 5
  Placement = pos=(0,0,920) rot=(0,0,1;0rad)
  sketch-geometry (8):
    g0: LineSegment StartX=-297.073 StartY=116.893 StartZ=0 EndX=-287.073 EndY=116.893 EndZ=0
    g1: LineSegment StartX=-287.073 StartY=116.893 StartZ=0 EndX=-287.073 EndY=121.893 EndZ=0
    g2: LineSegment StartX=-287.073 StartY=121.893 StartZ=0 EndX=-297.073 EndY=121.893 EndZ=0
    g3: LineSegment StartX=-297.073 StartY=116.893 StartZ=0 EndX=-297.073 EndY=121.893 EndZ=0
    g4: LineSegment StartX=69.089 StartY=121.893 StartZ=0 EndX=69.089 EndY=116.893 EndZ=0
    g5: LineSegment StartX=69.089 StartY=116.893 StartZ=0 EndX=79.089 EndY=116.893 EndZ=0
    g6: LineSegment StartX=79.089 StartY=116.893 StartZ=0 EndX=79.089 EndY=121.893 EndZ=0
    g7: LineSegment StartX=69.089 StartY=121.893 StartZ=0 EndX=79.089 EndY=121.893 EndZ=0
  constraints (20):
    c: Coincident(g0,g1)
    c: Coincident(g1,g2)
    c: Vertical(g1)
    c: Horizontal(g0)
    c: Horizontal(g2)
    c: Coincident(g0,g-7)
    c: Coincident(g3,g-7)
    c: Vertical(g3)
    c: Coincident(g2,g3)
    c: PointOnObject(g0,g3)
    c: Coincident(g4,g5)
    c: Horizontal(g5)
    c: Vertical(g4)
    c: Coincident(g4,g-6)
    c: Coincident(g6,g-6)
    c: Vertical(g6)
    c: PointOnObject(g5,g6)
    c: Coincident(g7,g4)
    c: Coincident(g7,g6)
    c: Horizontal(g7)
FEATURE [PartDesign::Pocket] Pocket002
  BaseFeature = -> Pocket001
  Direction = (0,0,-1)
  Length = 80
  Length2 = 5
  Profile = -> Sketch011
  ReferenceAxis = -> Sketch011 [N_Axis]
  Refine = true
  Suppressed = false
  Type = 0
FEATURE [PartDesign::ShapeBinder] CopyPocket002
  TraceSupport = false
FEATURE [PartDesign::Plane] DatumPlane003
  AttachmentSupport = -> [CopyPocket002]
  Length = 872.996
  MapMode = 5
  Placement = pos=(0,0,0) rot=(1,0,0;3.14159rad)
  ResizeMode = 0
  Width = 532.996
FEATURE [Sketcher::SketchObject] Sketch012
  ArcFitTolerance = 1e-06
  AttachmentSupport = -> [DatumPlane003]
  ExternalGeometry = -> [CopyPocket002]
  FullyConstrained = false
  MakeInternals = false
  MapMode = 5
  Placement = pos=(0,0,0) rot=(1,0,0;3.14159rad)
  sketch-geometry (14):
    g0: LineSegment [constr] StartX=380 StartY=-200 StartZ=0 EndX=380 EndY=-228.107 EndZ=0
    g1: LineSegment [constr] StartX=370 StartY=-210 StartZ=0 EndX=380 EndY=-210 EndZ=0
    g2: LineSegment [constr] StartX=-380 StartY=200 StartZ=0 EndX=-380 EndY=236.481 EndZ=0
    g3: LineSegment [constr] StartX=-370 StartY=210 StartZ=0 EndX=-380 EndY=210 EndZ=0
    g4: LineSegment StartX=-380 StartY=200 StartZ=0 EndX=-380 EndY=-200 EndZ=0
    g5: LineSegment StartX=-370 StartY=-210 StartZ=0 EndX=370 EndY=-210 EndZ=0
    g6: LineSegment StartX=380 StartY=-200 StartZ=0 EndX=380 EndY=200 EndZ=0
    g7: LineSegment StartX=370 StartY=210 StartZ=0 EndX=-370 EndY=210 EndZ=0
    g8: ArcOfCircle CenterX=-370 CenterY=200 CenterZ=0 NormalX=0 NormalY=0 NormalZ=1 AngleXU=0 Radius=10 StartAngle=1.5708 EndAngle=3.14159
    g9: ArcOfCircle CenterX=-370 CenterY=-200 CenterZ=0 NormalX=0 NormalY=0 NormalZ=1 AngleXU=0 Radius=10 StartAngle=3.14159 EndAngle=4.71239
    g10: ArcOfCircle CenterX=370 CenterY=-200 CenterZ=0 NormalX=0 NormalY=0 NormalZ=1 AngleXU=0 Radius=10 StartAngle=4.71239 EndAngle=6.28319
    g11: ArcOfCircle CenterX=370 CenterY=200 CenterZ=0 NormalX=0 NormalY=0 NormalZ=1 AngleXU=0 Radius=10 StartAngle=0 EndAngle=1.5708
    g12: GeomPoint [constr] X=-380 Y=210 Z=0
    g13: GeomPoint [constr] X=380 Y=-210 Z=0
  constraints (27):
    c: Coincident(g0,g-5)
    c: Vertical(g0)
    c: Coincident(g2,g-4)
    c: Vertical(g2)
    c: Horizontal(g1)
    c: Horizontal(g3)
    c: Tangent(g4,g8) = -1.5708
    c: Tangent(g4,g9) = -1.5708
    c: Tangent(g5,g9) = -1.5708
    c: Tangent(g5,g10) = -1.5708
    c: Tangent(g6,g10) = -1.5708
    c: Tangent(g6,g11) = -1.5708
    c: Tangent(g7,g11) = -1.5708
    c: Tangent(g7,g8) = -1.5708
    c: Vertical(g4)
    c: Vertical(g6)
    c: Horizontal(g5)
    c: Horizontal(g7)
    c: Equal(g8,g9)
    c: Equal(g9,g10)
    c: Equal(g10,g11)
    c: PointOnObject(g12,g4)
    c: PointOnObject(g12,g7)
    c: PointOnObject(g13,g5)
    c: PointOnObject(g13,g6)
    c: Coincident(g12,g3)
    c: Coincident(g13,g1)
FEATURE [PartDesign::Pad] Pad009
  Direction = (0,0,-1)
  Length = 100
  Length2 = 10
  Placement = pos=(0,0,0) rot=(1,0,0;3.14159rad)
  Profile = -> Sketch012
  ReferenceAxis = -> Sketch012 [N_Axis]
  Refine = true
  Reversed = true
  Suppressed = false
  Type = 0
FEATURE [PartDesign::Body] Body003
  AllowCompound = false
  Group = -> [DatumPlane003,CopyPocket002,Sketch012,Pad009]
  Origin = -> Origin003
  Tip = -> Pad009
FEATURE [Sketcher::SketchObject] Sketch013
  ArcFitTolerance = 1e-06
  AttachmentSupport = -> [Pocket002]
  ExternalGeometry = -> [Pocket002]
  FullyConstrained = false
  MakeInternals = false
  MapMode = 5
  Placement = pos=(0,0,0) rot=(1,0,0;3.14159rad)
  sketch-geometry (8):
    g0: LineSegment [constr] StartX=-370 StartY=210 StartZ=0 EndX=-403.084 EndY=210 EndZ=0
    g1: LineSegment [constr] StartX=-380 StartY=200 StartZ=0 EndX=-380 EndY=210 EndZ=0
    g2: LineSegment [constr] StartX=380 StartY=-200 StartZ=0 EndX=380 EndY=-228.401 EndZ=0
    g3: LineSegment [constr] StartX=370 StartY=-210 StartZ=0 EndX=380 EndY=-210 EndZ=0
    g4: LineSegment StartX=-380 StartY=210 StartZ=0 EndX=-380 EndY=-210 EndZ=0
    g5: LineSegment StartX=-380 StartY=-210 StartZ=0 EndX=380 EndY=-210 EndZ=0
    g6: LineSegment StartX=380 StartY=-210 StartZ=0 EndX=380 EndY=210 EndZ=0
    g7: LineSegment StartX=380 StartY=210 StartZ=0 EndX=-380 EndY=210 EndZ=0
  constraints (19):
    c: Horizontal(g0)
    c: PointOnObject(g1,g0)
    c: Vertical(g1)
    c: Coincident(g3,g-6)
    c: PointOnObject(g3,g2)
    c: Horizontal(g3)
    c: Coincident(g0,g-5)
    c: Coincident(g4,g5)
    c: Coincident(g5,g6)
    c: Coincident(g6,g7)
    c: Coincident(g7,g4)
    c: Vertical(g4)
    c: Vertical(g6)
    c: Horizontal(g5)
    c: Horizontal(g7)
    c: Coincident(g4,g1)
    c: Coincident(g5,g3)
    c: Vertical(g2)
    c: Coincident(g2,g-6)
FEATURE [PartDesign::Pocket] Pocket003
  BaseFeature = -> Pocket002
  Direction = (0,0,1)
  Length = 100
  Length2 = 5
  Profile = -> Sketch013
  ReferenceAxis = -> Sketch013 [N_Axis]
  Refine = true
  Suppressed = false
  Type = 0
FEATURE [Part::FeaturePython] Clone001  label="lid1_clone"  # Draft clone (typed FeaturePython)
  AttacherType = Attacher::AttachEngine3D
  Fuse = false
  Objects = -> [Body001]
  Scale = (1,1,1)
FEATURE [Part::FeaturePython] Clone002  label="lid2_clone"  # Draft clone (typed FeaturePython)
  AttacherType = Attacher::AttachEngine3D
  Fuse = false
  Objects = -> [Body002]
  Scale = (1,1,1)
FEATURE [Part::FeaturePython] Clone003  label="base_clone"  # Draft clone (typed FeaturePython)
  AttacherType = Attacher::AttachEngine3D
  Fuse = false
  Objects = -> [Body003]
  Scale = (1,1,1)
FEATURE [PartDesign::ShapeBinder] CopyPocket003
  Placement = pos=(0,0,843) rot=(0,0,1;0rad)
  TraceSupport = false
FEATURE [PartDesign::Plane] DatumPlane004
  AttachmentSupport = -> [CopyPocket003]
  Length = 259.781
  MapMode = 11
  Placement = pos=(-236.553,155.978,843) rot=(0,0,1;1.5708rad)
  ResizeMode = 0
  Width = 340.352
FEATURE [PartDesign::ShapeBinder] CopyPocket004
  TraceSupport = false
FEATURE [PartDesign::Line] DatumLine
  AttacherType = Attacher::AttachEngineLine
  AttachmentSupport = -> [CopyPocket004]
  Length = 20
  MapMode = 29
  Placement = pos=(-231.265,0,859) rot=(1,0,0;1.5708rad)
  ResizeMode = 0
FEATURE [PartDesign::ShapeBinder] CopyPocket005
  TraceSupport = false
FEATURE [PartDesign::Line] DatumLine001
  AttacherType = Attacher::AttachEngineLine
  AttachmentSupport = -> [CopyPocket005]
  Length = 20
  MapMode = 29
  Placement = pos=(-231.265,0,859) rot=(1,0,0;1.5708rad)
  ResizeMode = 0
FEATURE [PartDesign::ShapeBinder] CopyPocket006
  TraceSupport = false
FEATURE [PartDesign::Line] DatumLine002
  AttacherType = Attacher::AttachEngineLine
  AttachmentSupport = -> [CopyPocket006]
  Length = 20
  MapMode = 19
  Placement = pos=(-236.553,135.079,859) rot=(-1,0,0;3.14159rad)
  ResizeMode = 0
FEATURE [PartDesign::ShapeBinder] CopyPocket007
  TraceSupport = false
FEATURE [PartDesign::Line] DatumLine003
  AttacherType = Attacher::AttachEngineLine
  AttachmentSupport = -> [CopyPocket007]
  Length = 20
  MapMode = 19
  Placement = pos=(-236.553,176.878,859) rot=(0,1,0;3.14159rad)
  ResizeMode = 0
FEATURE [Sketcher::SketchObject] Sketch014
  ArcFitTolerance = 1e-06
  AttachmentSupport = -> [DatumPlane004]
  ExternalGeometry = -> [CopyPocket003]
  FullyConstrained = true
  MakeInternals = false
  MapMode = 5
  Placement = pos=(-236.553,155.978,843) rot=(0,0,1;1.5708rad)
  sketch-geometry (1):
    g0: Circle CenterX=0 CenterY=0 CenterZ=0 NormalX=0 NormalY=0 NormalZ=1 AngleXU=0 Radius=29.3345
  constraints (2):
    c: Coincident(g0,g-1)
    c: Tangent(g0,g-3)
FEATURE [PartDesign::Pad] Pad010
  Direction = (0,0,1)
  Length = 3
  Length2 = 10
  Placement = pos=(-236.553,155.978,843) rot=(0,0,1;1.5708rad)
  Profile = -> Sketch014
  ReferenceAxis = -> Sketch014 [N_Axis]
  Refine = true
  Suppressed = false
  Type = 0
FEATURE [Sketcher::SketchObject] Sketch015
  ArcFitTolerance = 1e-06
  AttachmentSupport = -> [Pad010]
  ExternalGeometry = -> [CopyPocket006,CopyPocket007]
  FullyConstrained = false
  MakeInternals = false
  MapMode = 5
  Placement = pos=(-236.553,155.978,846) rot=(0,0,1;1.5708rad)
  sketch-geometry (4):
    g0: ArcOfCircle CenterX=-20.8993 CenterY=-3.532e-13 CenterZ=0 NormalX=0 NormalY=0 NormalZ=1 AngleXU=0 Radius=5.28796 StartAngle=1.5708 EndAngle=4.71239
    g1: ArcOfCircle CenterX=20.8993 CenterY=-3.532e-13 CenterZ=0 NormalX=0 NormalY=0 NormalZ=1 AngleXU=0 Radius=5.28796 StartAngle=4.71239 EndAngle=7.85398
    g2: LineSegment StartX=-20.8993 StartY=5.28796 StartZ=0 EndX=20.8993 EndY=5.28796 EndZ=0
    g3: LineSegment StartX=-20.8993 StartY=-5.28796 StartZ=0 EndX=20.8993 EndY=-5.28796 EndZ=0
  constraints (6):
    c: Tangent(g0,g2) = 1.5708
    c: Tangent(g0,g3) = -1.5708
    c: Tangent(g1,g2) = 1.5708
    c: Tangent(g1,g3) = -1.5708
    c: Equal(g0,g1)
    c: Horizontal(g3)
FEATURE [PartDesign::Pad] Pad011
  BaseFeature = -> Pad010
  Direction = (0,0,1)
  Length = 15
  Length2 = 10
  Placement = pos=(-236.553,155.978,843) rot=(0,0,1;1.5708rad)
  Profile = -> Sketch015
  ReferenceAxis = -> Sketch015 [N_Axis]
  Refine = true
  Suppressed = false
  Type = 0
FEATURE [PartDesign::Chamfer] Chamfer
  Angle = 45
  Base = -> Pad011 [Edge3]
  BaseFeature = -> Pad011
  ChamferType = 0
  FlipDirection = false
  Placement = pos=(-236.553,155.978,843) rot=(0,0,1;1.5708rad)
  Refine = true
  Size = 1
  Size2 = 1
  SupportTransform = false
  Suppressed = false
  UseAllEdges = false
FEATURE [PartDesign::Fillet] Fillet007
  Base = -> Chamfer [Edge7]
  BaseFeature = -> Chamfer
  Placement = pos=(-236.553,155.978,843) rot=(0,0,1;1.5708rad)
  Radius = 1
  Refine = true
  SupportTransform = false
  Suppressed = false
  UseAllEdges = false
FEATURE [PartDesign::Fillet] Fillet008
  Base = -> Fillet007 [Edge17]
  BaseFeature = -> Fillet007
  Placement = pos=(-236.553,155.978,843) rot=(0,0,1;1.5708rad)
  Radius = 3
  Refine = true
  SupportTransform = false
  Suppressed = false
  UseAllEdges = false
FEATURE [PartDesign::Body] Body004
  AllowCompound = false
  Group = -> [DatumPlane004,CopyPocket003,DatumLine,CopyPocket004,DatumLine001,CopyPocket005,DatumLine002,CopyPocket006,DatumLine003,CopyPocket007,Sketch014,Pad010,Sketch015,Pad011,Chamfer,Fillet007,Fillet008]
  Origin = -> Origin005
  Tip = -> Fillet008
FEATURE [PartDesign::ShapeBinder] CopyPocket008
  Placement = pos=(0,0,843) rot=(0,0,1;0rad)
  TraceSupport = false
FEATURE [PartDesign::Plane] DatumPlane005
  AttachmentSupport = -> [CopyPocket008]
  Length = 252.085
  MapMode = 11
  Placement = pos=(-153.083,155.978,843) rot=(0,0,1;1.5708rad)
  ResizeMode = 0
  Width = 249.187
FEATURE [PartDesign::ShapeBinder] CopyPocket009
  TraceSupport = false
FEATURE [PartDesign::Line] DatumLine004
  AttacherType = Attacher::AttachEngineLine
  AttachmentSupport = -> [CopyPocket009]
  Length = 20
  MapMode = 29
  Placement = pos=(-147.795,0,859) rot=(1,0,0;1.5708rad)
  ResizeMode = 0
FEATURE [PartDesign::ShapeBinder] CopyPocket010
  TraceSupport = false
FEATURE [PartDesign::Line] DatumLine005
  AttacherType = Attacher::AttachEngineLine
  AttachmentSupport = -> [CopyPocket010]
  Length = 20
  MapMode = 29
  Placement = pos=(-147.795,0,859) rot=(1,0,0;1.5708rad)
  ResizeMode = 0
FEATURE [PartDesign::ShapeBinder] CopyPocket011
  TraceSupport = false
FEATURE [PartDesign::Line] DatumLine006
  AttacherType = Attacher::AttachEngineLine
  AttachmentSupport = -> [CopyPocket011]
  Length = 20
  MapMode = 19
  Placement = pos=(-153.083,176.878,859) rot=(0,1,0;3.14159rad)
  ResizeMode = 0
FEATURE [Sketcher::SketchObject] Sketch016
  ArcFitTolerance = 1e-06
  AttachmentSupport = -> [DatumPlane005]
  ExternalGeometry = -> [CopyPocket008]
  FullyConstrained = true
  MakeInternals = false
  MapMode = 5
  Placement = pos=(-153.083,155.978,843) rot=(0,0,1;1.5708rad)
  sketch-geometry (1):
    g0: Circle CenterX=0 CenterY=0 CenterZ=0 NormalX=0 NormalY=0 NormalZ=1 AngleXU=0 Radius=29.3345
  constraints (2):
    c: Coincident(g0,g-1)
    c: Tangent(g0,g-3)
FEATURE [PartDesign::ShapeBinder] CopyPocket012
  TraceSupport = false
FEATURE [PartDesign::Line] DatumLine007
  AttacherType = Attacher::AttachEngineLine
  AttachmentSupport = -> [CopyPocket012]
  Length = 20
  MapMode = 19
  Placement = pos=(-153.083,135.079,859) rot=(-1,0,0;3.14159rad)
  ResizeMode = 0
FEATURE [PartDesign::Pad] Pad012
  Direction = (0,0,1)
  Length = 3
  Length2 = 10
  Placement = pos=(-153.083,155.978,843) rot=(0,0,1;1.5708rad)
  Profile = -> Sketch016
  ReferenceAxis = -> Sketch016 [N_Axis]
  Refine = true
  Suppressed = false
  Type = 0
FEATURE [Sketcher::SketchObject] Sketch017
  ArcFitTolerance = 1e-06
  AttachmentSupport = -> [Pad012]
  ExternalGeometry = -> [CopyPocket012,CopyPocket011]
  FullyConstrained = false
  MakeInternals = false
  MapMode = 5
  Placement = pos=(-153.083,155.978,846) rot=(0,0,1;1.5708rad)
  sketch-geometry (4):
    g0: ArcOfCircle CenterX=-20.8993 CenterY=-3.532e-13 CenterZ=0 NormalX=0 NormalY=0 NormalZ=1 AngleXU=0 Radius=5.28796 StartAngle=1.5708 EndAngle=4.71239
    g1: ArcOfCircle CenterX=20.8993 CenterY=-3.532e-13 CenterZ=0 NormalX=0 NormalY=0 NormalZ=1 AngleXU=0 Radius=5.28796 StartAngle=4.71239 EndAngle=7.85398
    g2: LineSegment StartX=-20.8993 StartY=5.28796 StartZ=0 EndX=20.8993 EndY=5.28796 EndZ=0
    g3: LineSegment StartX=-20.8993 StartY=-5.28796 StartZ=0 EndX=20.8993 EndY=-5.28796 EndZ=0
  constraints (6):
    c: Tangent(g0,g2) = 1.5708
    c: Tangent(g0,g3) = -1.5708
    c: Tangent(g1,g2) = 1.5708
    c: Tangent(g1,g3) = -1.5708
    c: Equal(g0,g1)
    c: Horizontal(g3)
FEATURE [PartDesign::Pad] Pad013
  BaseFeature = -> Pad012
  Direction = (0,0,1)
  Length = 15
  Length2 = 10
  Placement = pos=(-153.083,155.978,843) rot=(0,0,1;1.5708rad)
  Profile = -> Sketch017
  ReferenceAxis = -> Sketch017 [N_Axis]
  Refine = true
  Suppressed = false
  Type = 0
FEATURE [PartDesign::Chamfer] Chamfer001
  Angle = 45
  Base = -> Pad013 [Edge3]
  BaseFeature = -> Pad013
  ChamferType = 0
  FlipDirection = false
  Placement = pos=(-153.083,155.978,843) rot=(0,0,1;1.5708rad)
  Refine = true
  Size = 1
  Size2 = 1
  SupportTransform = false
  Suppressed = false
  UseAllEdges = false
FEATURE [PartDesign::Fillet] Fillet009
  Base = -> Chamfer001 [Edge7]
  BaseFeature = -> Chamfer001
  Placement = pos=(-153.083,155.978,843) rot=(0,0,1;1.5708rad)
  Radius = 1
  Refine = true
  SupportTransform = false
  Suppressed = false
  UseAllEdges = false
FEATURE [PartDesign::Fillet] Fillet010
  Base = -> Fillet009 [Edge17]
  BaseFeature = -> Fillet009
  Placement = pos=(-153.083,155.978,843) rot=(0,0,1;1.5708rad)
  Radius = 3
  Refine = true
  SupportTransform = false
  Suppressed = false
  UseAllEdges = false
FEATURE [PartDesign::Body] Body005
  AllowCompound = false
  Group = -> [DatumPlane005,CopyPocket008,DatumLine004,CopyPocket009,DatumLine005,CopyPocket010,DatumLine006,CopyPocket011,Sketch016,DatumLine007,CopyPocket012,Pad012,Sketch017,Pad013,Chamfer001,Fillet009,Fillet010]
  Origin = -> Origin006
  Tip = -> Fillet010
FEATURE [PartDesign::ShapeBinder] CopyPocket013
  Placement = pos=(0,0,843) rot=(0,0,1;0rad)
  TraceSupport = false
FEATURE [PartDesign::Plane] DatumPlane006
  AttachmentSupport = -> [CopyPocket013]
  Length = 234.835
  MapMode = 11
  Placement = pos=(17.148,155.978,843) rot=(0,0,1;1.5708rad)
  ResizeMode = 0
  Width = 96.0049
FEATURE [PartDesign::ShapeBinder] CopyPocket014
  TraceSupport = false
FEATURE [PartDesign::Line] DatumLine008
  AttacherType = Attacher::AttachEngineLine
  AttachmentSupport = -> [CopyPocket014]
  Length = 20
  MapMode = 29
  Placement = pos=(22.4359,0,848) rot=(0,0.707107,0.707107;3.14159rad)
  ResizeMode = 0
FEATURE [PartDesign::ShapeBinder] CopyPocket015
  TraceSupport = false
FEATURE [PartDesign::Line] DatumLine009
  AttacherType = Attacher::AttachEngineLine
  AttachmentSupport = -> [CopyPocket015]
  Length = 20
  MapMode = 19
  Placement = pos=(17.148,135.079,859) rot=(-1,0,0;3.14159rad)
  ResizeMode = 0
FEATURE [PartDesign::ShapeBinder] CopyPocket016
  TraceSupport = false
FEATURE [PartDesign::Line] DatumLine010
  AttacherType = Attacher::AttachEngineLine
  AttachmentSupport = -> [CopyPocket016]
  Length = 20
  MapMode = 19
  Placement = pos=(17.148,176.878,859) rot=(0,1,0;3.14159rad)
  ResizeMode = 0
FEATURE [Sketcher::SketchObject] Sketch018
  ArcFitTolerance = 1e-06
  AttachmentSupport = -> [DatumPlane006]
  ExternalGeometry = -> [CopyPocket013]
  FullyConstrained = true
  MakeInternals = false
  MapMode = 5
  Placement = pos=(17.148,155.978,843) rot=(0,0,1;1.5708rad)
  sketch-geometry (1):
    g0: Circle CenterX=0 CenterY=0 CenterZ=0 NormalX=0 NormalY=0 NormalZ=1 AngleXU=0 Radius=29.3345
  constraints (2):
    c: Coincident(g0,g-1)
    c: Tangent(g0,g-3)
FEATURE [PartDesign::Pad] Pad014
  Direction = (0,0,1)
  Length = 3
  Length2 = 10
  Placement = pos=(17.148,155.978,843) rot=(0,0,1;1.5708rad)
  Profile = -> Sketch018
  ReferenceAxis = -> Sketch018 [N_Axis]
  Refine = true
  Suppressed = false
  Type = 0
FEATURE [Sketcher::SketchObject] Sketch019
  ArcFitTolerance = 1e-06
  AttachmentSupport = -> [Pad014]
  ExternalGeometry = -> [CopyPocket015,CopyPocket016]
  FullyConstrained = false
  MakeInternals = false
  MapMode = 5
  Placement = pos=(17.148,155.978,846) rot=(0,0,1;1.5708rad)
  sketch-geometry (4):
    g0: ArcOfCircle CenterX=-20.8993 CenterY=-1.765e-13 CenterZ=0 NormalX=0 NormalY=0 NormalZ=1 AngleXU=0 Radius=5.28796 StartAngle=1.5708 EndAngle=4.71239
    g1: ArcOfCircle CenterX=20.8993 CenterY=-1.765e-13 CenterZ=0 NormalX=0 NormalY=0 NormalZ=1 AngleXU=0 Radius=5.28796 StartAngle=4.71239 EndAngle=7.85398
    g2: LineSegment StartX=-20.8993 StartY=5.28796 StartZ=0 EndX=20.8993 EndY=5.28796 EndZ=0
    g3: LineSegment StartX=-20.8993 StartY=-5.28796 StartZ=0 EndX=20.8993 EndY=-5.28796 EndZ=0
  constraints (6):
    c: Tangent(g0,g2) = 1.5708
    c: Tangent(g0,g3) = -1.5708
    c: Tangent(g1,g2) = 1.5708
    c: Tangent(g1,g3) = -1.5708
    c: Equal(g0,g1)
    c: Horizontal(g3)
FEATURE [PartDesign::Pad] Pad015
  BaseFeature = -> Pad014
  Direction = (0,0,1)
  Length = 15
  Length2 = 10
  Placement = pos=(17.148,155.978,843) rot=(0,0,1;1.5708rad)
  Profile = -> Sketch019
  ReferenceAxis = -> Sketch019 [N_Axis]
  Refine = true
  Suppressed = false
  Type = 0
FEATURE [PartDesign::Chamfer] Chamfer002
  Angle = 45
  Base = -> Pad015 [Edge3]
  BaseFeature = -> Pad015
  ChamferType = 0
  FlipDirection = false
  Placement = pos=(17.148,155.978,843) rot=(0,0,1;1.5708rad)
  Refine = true
  Size = 1
  Size2 = 1
  SupportTransform = false
  Suppressed = false
  UseAllEdges = false
FEATURE [PartDesign::Fillet] Fillet011
  Base = -> Chamfer002 [Edge7]
  BaseFeature = -> Chamfer002
  Placement = pos=(17.148,155.978,843) rot=(0,0,1;1.5708rad)
  Radius = 1
  Refine = true
  SupportTransform = false
  Suppressed = false
  UseAllEdges = false
FEATURE [PartDesign::Fillet] Fillet012
  Base = -> Fillet011 [Edge17]
  BaseFeature = -> Fillet011
  Placement = pos=(17.148,155.978,843) rot=(0,0,1;1.5708rad)
  Radius = 3
  Refine = true
  SupportTransform = false
  Suppressed = false
  UseAllEdges = false
FEATURE [PartDesign::Body] Body006
  AllowCompound = false
  Group = -> [DatumPlane006,CopyPocket013,DatumLine008,CopyPocket014,DatumLine009,CopyPocket015,DatumLine010,CopyPocket016,Sketch018,Pad014,Sketch019,Pad015,Chamfer002,Fillet011,Fillet012]
  Origin = -> Origin007
  Tip = -> Fillet012
FEATURE [Sketcher::SketchObject] Sketch020
  ArcFitTolerance = 1e-06
  AttachmentSupport = -> [Pocket003]
  ExternalGeometry = -> [Pocket003]
  FullyConstrained = false
  MakeInternals = false
  MapMode = 5
  Placement = pos=(0,0,861) rot=(0,0,1;0rad)
  sketch-geometry (3):
    g0: Circle CenterX=-236.553 CenterY=155.978 CenterZ=0 NormalX=0 NormalY=0 NormalZ=1 AngleXU=0 Radius=29.3345
    g1: Circle CenterX=17.148 CenterY=155.978 CenterZ=0 NormalX=0 NormalY=0 NormalZ=1 AngleXU=0 Radius=29.3345
    g2: Circle CenterX=-153.083 CenterY=155.978 CenterZ=0 NormalX=0 NormalY=0 NormalZ=1 AngleXU=0 Radius=29.3345
  constraints (5):
    c: Tangent(g0,g-3)
    c: Coincident(g1,g-4)
    c: Equal(g1,g-4)
    c: Coincident(g2,g-5)
    c: Equal(g2,g-5)
FEATURE [PartDesign::Pocket] Pocket004
  BaseFeature = -> Pocket003
  Direction = (0,0,-1)
  Length = 18
  Length2 = 5
  Profile = -> Sketch020
  ReferenceAxis = -> Sketch020 [N_Axis]
  Refine = true
  Suppressed = false
  Type = 0
FEATURE [PartDesign::Body] Body
  AllowCompound = false
  Group = -> [Sketch,Pad,Sketch001,Pad001,Sketch002,Pad002,Sketch003,Pad003,Sketch004,Pad004,Sketch005,Pad005,Sketch006,Pad006,Fillet,Fillet001,Fillet002,Fillet003,Fillet004,Fillet005,Fillet006,Sketch009,Pocket,Sketch010,Pocket001,Sketch011,Pocket002,Sketch013,Pocket003,Sketch020,Pocket004]
  Origin = -> Origin
  Tip = -> Pocket004
FEATURE [Part::FeaturePython] Clone004  label="switch1_clone"  # Draft clone (typed FeaturePython)
  AttacherType = Attacher::AttachEngine3D
  Fuse = false
  Objects = -> [Body004]
  Scale = (1,1,1)
FEATURE [Part::FeaturePython] Clone005  label="switch2_clone"  # Draft clone (typed FeaturePython)
  AttacherType = Attacher::AttachEngine3D
  Fuse = false
  Objects = -> [Body005]
  Scale = (1,1,1)
FEATURE [Part::FeaturePython] Clone006  label="switch3_clone"  # Draft clone (typed FeaturePython)
  AttacherType = Attacher::AttachEngine3D
  Fuse = false
  Objects = -> [Body006]
  Scale = (1,1,1)
FEATURE [Part::FeaturePython] Clone  label="body_clone"  # Draft clone (typed FeaturePython)
  AttacherType = Attacher::AttachEngine3D
  Fuse = false
  Objects = -> [Body]
  Scale = (1,1,1)
FEATURE [App::Part] Part  label="wachingmachine"
  Group = -> [Clone001,Clone002,Clone003,Clone004,Clone005,Clone006,Clone]
  Origin = -> Origin004
